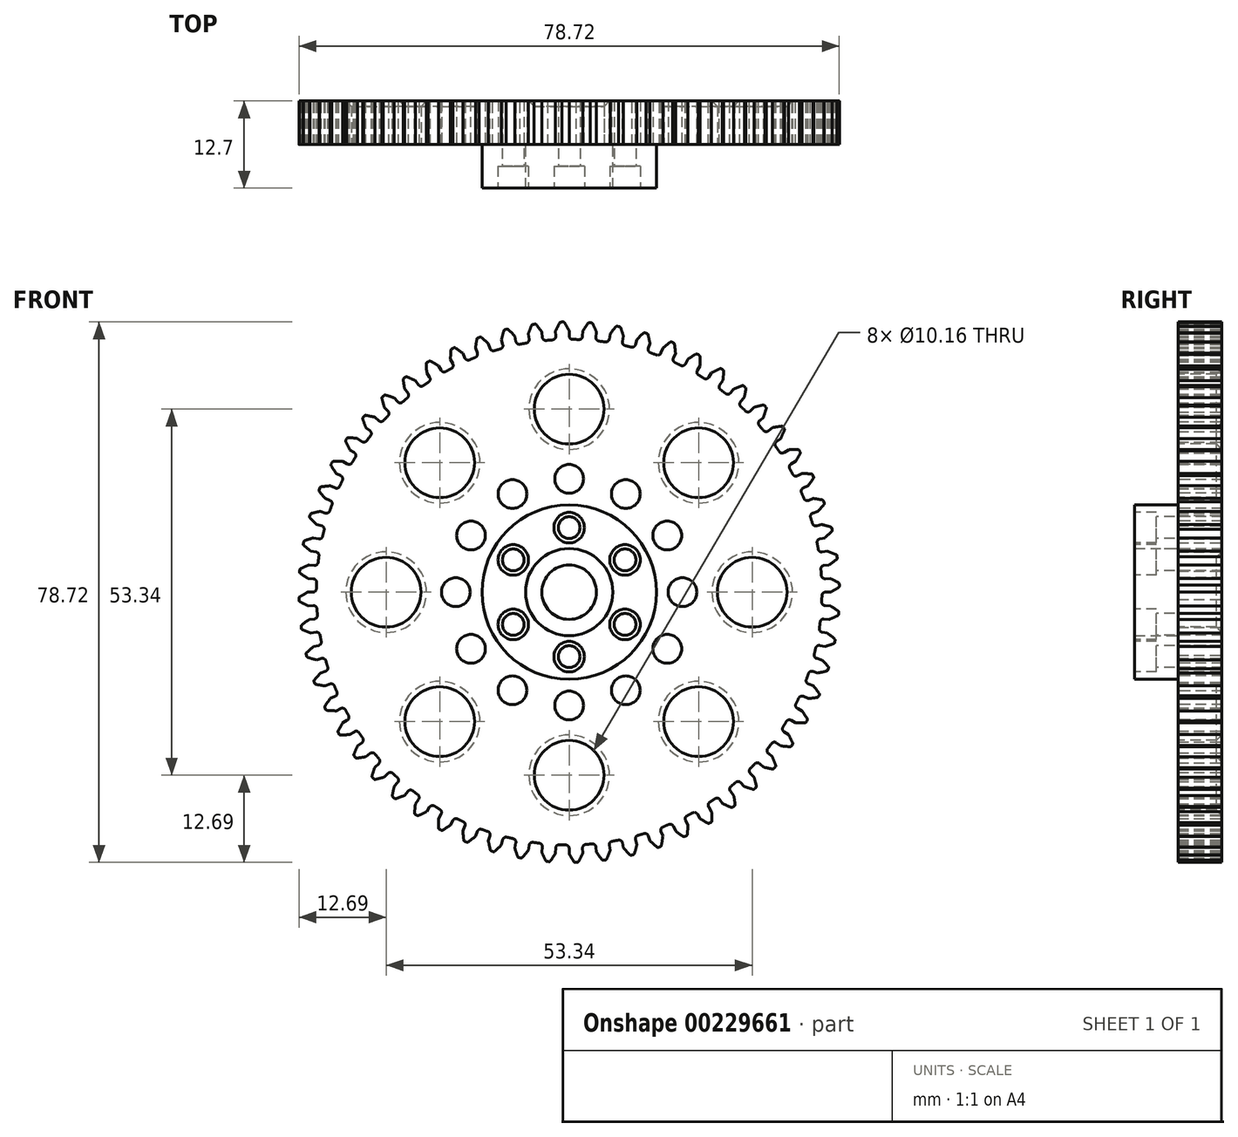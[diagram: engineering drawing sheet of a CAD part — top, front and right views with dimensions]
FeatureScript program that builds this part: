
annotation { "Feature Type Name" : "Feature", "Feature Type Description" : "" }
export const myFeature = defineFeature(function(context is Context, id is Id, definition is map)
    precondition{}
    {
        {
            var Q0;
            Q0=qCreatedBy(makeId("Front.planeOp"),FACE);
            var sketch = newSketch(context, id + "F0", { "sketchPlane" : qUnion([Q0])});
            skArc(sketch, "E0", {"start": v(-2.43, 36.75) * mm, "mid": v(-10.46, 35.31) * mm, "end": v(-17.98, 32.14) * mm});
            skLineSegment(sketch, "E1", {"start": v(0, 0) * mm, "end": v(-1.31, 50.07) * mm, "construction": true});
            skLineSegment(sketch, "E2", {"start": v(-0.86, 39.36) * mm, "end": v(-1.03, 39.36) * mm});
            skLineSegment(sketch, "E3", {"start": v(0, 38.1) * mm, "end": v(0, 37.33) * mm});
            skArc(sketch, "E4.trimOffspring", {"start": v(0, 38.1) * mm, "mid": v(-0.34, 38.69) * mm, "end": v(-0.68, 39.27) * mm});
            skLineSegment(sketch, "E5.MirrorCS", {"start": v(-1.2, 39.35) * mm, "end": v(-1.03, 39.36) * mm});
            skArc(sketch, "E6.MirrorCS", {"start": v(-2, 38.05) * mm, "mid": v(-1.69, 38.65) * mm, "end": v(-1.37, 39.25) * mm});
            skLineSegment(sketch, "E7.MirrorCS", {"start": v(-2, 38.05) * mm, "end": v(-1.95, 37.28) * mm});
            skPoint(sketch, "E8.visualSharp", {"position": v(-1.32, 39.35) * mm});
            skArc(sketch, "E8.filletArc", {"start": v(-1.2, 39.35) * mm, "mid": v(-1.3, 39.32) * mm, "end": v(-1.37, 39.25) * mm});
            skPoint(sketch, "E9.visualSharp", {"position": v(-0.74, 39.36) * mm});
            skArc(sketch, "E9.filletArc", {"start": v(-0.68, 39.27) * mm, "mid": v(-0.76, 39.34) * mm, "end": v(-0.86, 39.36) * mm});
            skPoint(sketch, "E10.visualSharp", {"position": v(0, 36.83) * mm});
            skArc(sketch, "E10.filletArc", {"start": v(0, 37.33) * mm, "mid": v(0.15, 36.98) * mm, "end": v(0.5, 36.83) * mm});
            skPoint(sketch, "E11.visualSharp", {"position": v(-1.93, 36.78) * mm});
            skArc(sketch, "E11.filletArc", {"start": v(-2.43, 36.75) * mm, "mid": v(-2.08, 36.92) * mm, "end": v(-1.95, 37.28) * mm});
            skArc(sketch, "E12.1.0", {"start": v(-6.26, 36.3) * mm, "mid": v(-5.93, 36.5) * mm, "end": v(-5.84, 36.87) * mm});
            skLineSegment(sketch, "E12.1.1", {"start": v(-5.96, 37.63) * mm, "end": v(-5.84, 36.87) * mm});
            skArc(sketch, "E12.1.2", {"start": v(-5.96, 37.63) * mm, "mid": v(-5.72, 38.26) * mm, "end": v(-5.47, 38.89) * mm});
            skArc(sketch, "E12.1.3", {"start": v(-5.31, 39.01) * mm, "mid": v(-5.4, 38.97) * mm, "end": v(-5.47, 38.89) * mm});
            skLineSegment(sketch, "E12.1.4", {"start": v(-5.31, 39.01) * mm, "end": v(-5.14, 39.04) * mm});
            skLineSegment(sketch, "E12.1.5", {"start": v(-4.97, 39.06) * mm, "end": v(-5.14, 39.04) * mm});
            skArc(sketch, "E12.1.6", {"start": v(-4.78, 38.98) * mm, "mid": v(-4.86, 39.04) * mm, "end": v(-4.97, 39.06) * mm});
            skArc(sketch, "E12.1.7", {"start": v(-3.98, 37.9) * mm, "mid": v(-4.38, 38.44) * mm, "end": v(-4.78, 38.98) * mm});
            skLineSegment(sketch, "E12.1.8", {"start": v(-3.98, 37.9) * mm, "end": v(-3.9, 37.13) * mm});
            skArc(sketch, "E12.1.9", {"start": v(-3.9, 37.13) * mm, "mid": v(-3.72, 36.8) * mm, "end": v(-3.35, 36.68) * mm});
            skArc(sketch, "E12.2.0", {"start": v(-10.02, 35.44) * mm, "mid": v(-9.71, 35.68) * mm, "end": v(-9.66, 36.06) * mm});
            skLineSegment(sketch, "E12.2.1", {"start": v(-9.86, 36.8) * mm, "end": v(-9.66, 36.06) * mm});
            skArc(sketch, "E12.2.2", {"start": v(-9.86, 36.8) * mm, "mid": v(-9.69, 37.46) * mm, "end": v(-9.5, 38.1) * mm});
            skArc(sketch, "E12.2.3", {"start": v(-9.36, 38.24) * mm, "mid": v(-9.45, 38.2) * mm, "end": v(-9.5, 38.1) * mm});
            skLineSegment(sketch, "E12.2.4", {"start": v(-9.36, 38.24) * mm, "end": v(-9.2, 38.29) * mm});
            skLineSegment(sketch, "E12.2.5", {"start": v(-9.02, 38.32) * mm, "end": v(-9.2, 38.29) * mm});
            skArc(sketch, "E12.2.6", {"start": v(-8.83, 38.27) * mm, "mid": v(-8.92, 38.32) * mm, "end": v(-9.02, 38.32) * mm});
            skArc(sketch, "E12.2.7", {"start": v(-7.92, 37.27) * mm, "mid": v(-8.37, 37.77) * mm, "end": v(-8.83, 38.27) * mm});
            skLineSegment(sketch, "E12.2.8", {"start": v(-7.92, 37.27) * mm, "end": v(-7.76, 36.52) * mm});
            skArc(sketch, "E12.2.9", {"start": v(-7.76, 36.52) * mm, "mid": v(-7.54, 36.2) * mm, "end": v(-7.17, 36.13) * mm});
            skArc(sketch, "E12.3.0", {"start": v(-13.67, 34.2) * mm, "mid": v(-13.39, 34.47) * mm, "end": v(-13.38, 34.85) * mm});
            skLineSegment(sketch, "E12.3.1", {"start": v(-13.65, 35.57) * mm, "end": v(-13.38, 34.85) * mm});
            skArc(sketch, "E12.3.2", {"start": v(-13.65, 35.57) * mm, "mid": v(-13.55, 36.24) * mm, "end": v(-13.43, 36.9) * mm});
            skArc(sketch, "E12.3.3", {"start": v(-13.3, 37.06) * mm, "mid": v(-13.4, 37) * mm, "end": v(-13.43, 36.9) * mm});
            skLineSegment(sketch, "E12.3.4", {"start": v(-13.3, 37.06) * mm, "end": v(-13.14, 37.12) * mm});
            skLineSegment(sketch, "E12.3.5", {"start": v(-12.98, 37.17) * mm, "end": v(-13.14, 37.12) * mm});
            skArc(sketch, "E12.3.6", {"start": v(-12.78, 37.13) * mm, "mid": v(-12.88, 37.18) * mm, "end": v(-12.98, 37.17) * mm});
            skArc(sketch, "E12.3.7", {"start": v(-11.77, 36.24) * mm, "mid": v(-12.27, 36.69) * mm, "end": v(-12.78, 37.13) * mm});
            skLineSegment(sketch, "E12.3.8", {"start": v(-11.77, 36.24) * mm, "end": v(-11.54, 35.5) * mm});
            skArc(sketch, "E12.3.9", {"start": v(-11.54, 35.5) * mm, "mid": v(-11.29, 35.21) * mm, "end": v(-10.9, 35.18) * mm});
            skArc(sketch, "E12.4.0", {"start": v(-17.17, 32.59) * mm, "mid": v(-16.92, 32.88) * mm, "end": v(-16.95, 33.27) * mm});
            skLineSegment(sketch, "E12.4.1", {"start": v(-17.3, 33.95) * mm, "end": v(-16.95, 33.27) * mm});
            skArc(sketch, "E12.4.2", {"start": v(-17.3, 33.95) * mm, "mid": v(-17.26, 34.62) * mm, "end": v(-17.22, 35.3) * mm});
            skArc(sketch, "E12.4.3", {"start": v(-17.1, 35.46) * mm, "mid": v(-17.18, 35.4) * mm, "end": v(-17.22, 35.3) * mm});
            skLineSegment(sketch, "E12.4.4", {"start": v(-17.1, 35.46) * mm, "end": v(-16.95, 35.54) * mm});
            skLineSegment(sketch, "E12.4.5", {"start": v(-16.8, 35.61) * mm, "end": v(-16.95, 35.54) * mm});
            skArc(sketch, "E12.4.6", {"start": v(-16.6, 35.6) * mm, "mid": v(-16.7, 35.63) * mm, "end": v(-16.8, 35.61) * mm});
            skArc(sketch, "E12.4.7", {"start": v(-15.5, 34.8) * mm, "mid": v(-16.04, 35.2) * mm, "end": v(-16.6, 35.6) * mm});
            skLineSegment(sketch, "E12.4.8", {"start": v(-15.5, 34.8) * mm, "end": v(-15.19, 34.1) * mm});
            skArc(sketch, "E12.4.9", {"start": v(-15.19, 34.1) * mm, "mid": v(-14.9, 33.84) * mm, "end": v(-14.52, 33.85) * mm});
            skArc(sketch, "E12.5.0", {"start": v(-20.48, 30.61) * mm, "mid": v(-20.26, 30.93) * mm, "end": v(-20.33, 31.31) * mm});
            skLineSegment(sketch, "E12.5.1", {"start": v(-20.75, 31.95) * mm, "end": v(-20.33, 31.31) * mm});
            skArc(sketch, "E12.5.2", {"start": v(-20.75, 31.95) * mm, "mid": v(-20.79, 32.63) * mm, "end": v(-20.81, 33.3) * mm});
            skArc(sketch, "E12.5.3", {"start": v(-20.72, 33.48) * mm, "mid": v(-20.79, 33.4) * mm, "end": v(-20.81, 33.3) * mm});
            skLineSegment(sketch, "E12.5.4", {"start": v(-20.72, 33.48) * mm, "end": v(-20.57, 33.57) * mm});
            skLineSegment(sketch, "E12.5.5", {"start": v(-20.42, 33.66) * mm, "end": v(-20.57, 33.57) * mm});
            skArc(sketch, "E12.5.6", {"start": v(-20.22, 33.66) * mm, "mid": v(-20.32, 33.69) * mm, "end": v(-20.42, 33.66) * mm});
            skArc(sketch, "E12.5.7", {"start": v(-19.05, 33) * mm, "mid": v(-19.63, 33.34) * mm, "end": v(-20.22, 33.66) * mm});
            skLineSegment(sketch, "E12.5.8", {"start": v(-19.05, 33) * mm, "end": v(-18.67, 32.33) * mm});
            skArc(sketch, "E12.5.9", {"start": v(-18.67, 32.33) * mm, "mid": v(-18.36, 32.1) * mm, "end": v(-17.98, 32.14) * mm});
            skArc(sketch, "E12.6.0", {"start": v(-23.57, 28.3) * mm, "mid": v(-23.38, 28.65) * mm, "end": v(-23.5, 29.01) * mm});
            skLineSegment(sketch, "E12.6.1", {"start": v(-23.98, 29.6) * mm, "end": v(-23.5, 29.01) * mm});
            skArc(sketch, "E12.6.2", {"start": v(-23.98, 29.6) * mm, "mid": v(-24.09, 30.28) * mm, "end": v(-24.18, 30.95) * mm});
            skArc(sketch, "E12.6.3", {"start": v(-24.1, 31.13) * mm, "mid": v(-24.17, 31.05) * mm, "end": v(-24.18, 30.95) * mm});
            skLineSegment(sketch, "E12.6.4", {"start": v(-24.1, 31.13) * mm, "end": v(-23.97, 31.24) * mm});
            skLineSegment(sketch, "E12.6.5", {"start": v(-23.83, 31.34) * mm, "end": v(-23.97, 31.24) * mm});
            skArc(sketch, "E12.6.6", {"start": v(-23.63, 31.37) * mm, "mid": v(-23.73, 31.38) * mm, "end": v(-23.83, 31.34) * mm});
            skArc(sketch, "E12.6.7", {"start": v(-22.4, 30.82) * mm, "mid": v(-23.01, 31.1) * mm, "end": v(-23.63, 31.37) * mm});
            skLineSegment(sketch, "E12.6.8", {"start": v(-22.4, 30.82) * mm, "end": v(-21.94, 30.2) * mm});
            skArc(sketch, "E12.6.9", {"start": v(-21.94, 30.2) * mm, "mid": v(-21.62, 30) * mm, "end": v(-21.24, 30.09) * mm});
            skArc(sketch, "E12.7.0", {"start": v(-26.4, 25.69) * mm, "mid": v(-26.25, 26.04) * mm, "end": v(-26.4, 26.4) * mm});
            skLineSegment(sketch, "E12.7.1", {"start": v(-26.94, 26.94) * mm, "end": v(-26.4, 26.4) * mm});
            skArc(sketch, "E12.7.2", {"start": v(-26.94, 26.94) * mm, "mid": v(-27.12, 27.6) * mm, "end": v(-27.28, 28.25) * mm});
            skArc(sketch, "E12.7.3", {"start": v(-27.23, 28.44) * mm, "mid": v(-27.28, 28.35) * mm, "end": v(-27.28, 28.25) * mm});
            skLineSegment(sketch, "E12.7.4", {"start": v(-27.23, 28.44) * mm, "end": v(-27.1, 28.56) * mm});
            skLineSegment(sketch, "E12.7.5", {"start": v(-26.98, 28.68) * mm, "end": v(-27.1, 28.56) * mm});
            skArc(sketch, "E12.7.6", {"start": v(-26.78, 28.72) * mm, "mid": v(-26.88, 28.73) * mm, "end": v(-26.98, 28.68) * mm});
            skArc(sketch, "E12.7.7", {"start": v(-25.5, 28.31) * mm, "mid": v(-26.14, 28.53) * mm, "end": v(-26.78, 28.72) * mm});
            skLineSegment(sketch, "E12.7.8", {"start": v(-25.5, 28.31) * mm, "end": v(-24.98, 27.74) * mm});
            skArc(sketch, "E12.7.9", {"start": v(-24.98, 27.74) * mm, "mid": v(-24.63, 27.58) * mm, "end": v(-24.27, 27.7) * mm});
            skArc(sketch, "E12.8.0", {"start": v(-28.93, 22.79) * mm, "mid": v(-28.83, 23.16) * mm, "end": v(-29.01, 23.5) * mm});
            skLineSegment(sketch, "E12.8.1", {"start": v(-29.6, 23.98) * mm, "end": v(-29.01, 23.5) * mm});
            skArc(sketch, "E12.8.2", {"start": v(-29.6, 23.98) * mm, "mid": v(-29.85, 24.6) * mm, "end": v(-30.09, 25.24) * mm});
            skArc(sketch, "E12.8.3", {"start": v(-30.05, 25.44) * mm, "mid": v(-30.1, 25.34) * mm, "end": v(-30.09, 25.24) * mm});
            skLineSegment(sketch, "E12.8.4", {"start": v(-30.05, 25.44) * mm, "end": v(-29.94, 25.57) * mm});
            skLineSegment(sketch, "E12.8.5", {"start": v(-29.83, 25.7) * mm, "end": v(-29.94, 25.57) * mm});
            skArc(sketch, "E12.8.6", {"start": v(-29.64, 25.77) * mm, "mid": v(-29.74, 25.76) * mm, "end": v(-29.83, 25.7) * mm});
            skArc(sketch, "E12.8.7", {"start": v(-28.31, 25.5) * mm, "mid": v(-28.97, 25.64) * mm, "end": v(-29.64, 25.77) * mm});
            skLineSegment(sketch, "E12.8.8", {"start": v(-28.31, 25.5) * mm, "end": v(-27.74, 24.98) * mm});
            skArc(sketch, "E12.8.9", {"start": v(-27.74, 24.98) * mm, "mid": v(-27.38, 24.85) * mm, "end": v(-27.03, 25.01) * mm});
            skArc(sketch, "E12.9.0", {"start": v(-31.16, 19.64) * mm, "mid": v(-31.1, 20.02) * mm, "end": v(-31.31, 20.33) * mm});
            skLineSegment(sketch, "E12.9.1", {"start": v(-31.95, 20.75) * mm, "end": v(-31.31, 20.33) * mm});
            skArc(sketch, "E12.9.2", {"start": v(-31.95, 20.75) * mm, "mid": v(-32.26, 21.35) * mm, "end": v(-32.56, 21.96) * mm});
            skArc(sketch, "E12.9.3", {"start": v(-32.55, 22.16) * mm, "mid": v(-32.58, 22.06) * mm, "end": v(-32.56, 21.96) * mm});
            skLineSegment(sketch, "E12.9.4", {"start": v(-32.55, 22.16) * mm, "end": v(-32.45, 22.3) * mm});
            skLineSegment(sketch, "E12.9.5", {"start": v(-32.35, 22.44) * mm, "end": v(-32.45, 22.3) * mm});
            skArc(sketch, "E12.9.6", {"start": v(-32.17, 22.53) * mm, "mid": v(-32.27, 22.5) * mm, "end": v(-32.35, 22.44) * mm});
            skArc(sketch, "E12.9.7", {"start": v(-30.82, 22.4) * mm, "mid": v(-31.5, 22.47) * mm, "end": v(-32.17, 22.53) * mm});
            skLineSegment(sketch, "E12.9.8", {"start": v(-30.82, 22.4) * mm, "end": v(-30.2, 21.94) * mm});
            skArc(sketch, "E12.9.9", {"start": v(-30.2, 21.94) * mm, "mid": v(-29.83, 21.85) * mm, "end": v(-29.5, 22.05) * mm});
            skArc(sketch, "E12.10.0", {"start": v(-33.04, 16.27) * mm, "mid": v(-33.01, 16.66) * mm, "end": v(-33.27, 16.95) * mm});
            skLineSegment(sketch, "E12.10.1", {"start": v(-33.95, 17.3) * mm, "end": v(-33.27, 16.95) * mm});
            skArc(sketch, "E12.10.2", {"start": v(-33.95, 17.3) * mm, "mid": v(-34.32, 17.86) * mm, "end": v(-34.68, 18.43) * mm});
            skArc(sketch, "E12.10.3", {"start": v(-34.68, 18.63) * mm, "mid": v(-34.7, 18.53) * mm, "end": v(-34.68, 18.43) * mm});
            skLineSegment(sketch, "E12.10.4", {"start": v(-34.68, 18.63) * mm, "end": v(-34.6, 18.79) * mm});
            skLineSegment(sketch, "E12.10.5", {"start": v(-34.52, 18.94) * mm, "end": v(-34.6, 18.79) * mm});
            skArc(sketch, "E12.10.6", {"start": v(-34.35, 19.04) * mm, "mid": v(-34.45, 19.01) * mm, "end": v(-34.52, 18.94) * mm});
            skArc(sketch, "E12.10.7", {"start": v(-33, 19.05) * mm, "mid": v(-33.67, 19.05) * mm, "end": v(-34.35, 19.04) * mm});
            skLineSegment(sketch, "E12.10.8", {"start": v(-33, 19.05) * mm, "end": v(-32.33, 18.67) * mm});
            skArc(sketch, "E12.10.9", {"start": v(-32.33, 18.67) * mm, "mid": v(-31.95, 18.62) * mm, "end": v(-31.64, 18.85) * mm});
            skArc(sketch, "E12.11.0", {"start": v(-34.56, 12.73) * mm, "mid": v(-34.57, 13.12) * mm, "end": v(-34.85, 13.38) * mm});
            skLineSegment(sketch, "E12.11.1", {"start": v(-35.57, 13.65) * mm, "end": v(-34.85, 13.38) * mm});
            skArc(sketch, "E12.11.2", {"start": v(-35.57, 13.65) * mm, "mid": v(-36, 14.18) * mm, "end": v(-36.41, 14.7) * mm});
            skArc(sketch, "E12.11.3", {"start": v(-36.44, 14.9) * mm, "mid": v(-36.45, 14.8) * mm, "end": v(-36.41, 14.7) * mm});
            skLineSegment(sketch, "E12.11.4", {"start": v(-36.44, 14.9) * mm, "end": v(-36.38, 15.07) * mm});
            skLineSegment(sketch, "E12.11.5", {"start": v(-36.3, 15.23) * mm, "end": v(-36.38, 15.07) * mm});
            skArc(sketch, "E12.11.6", {"start": v(-36.15, 15.35) * mm, "mid": v(-36.24, 15.3) * mm, "end": v(-36.3, 15.23) * mm});
            skArc(sketch, "E12.11.7", {"start": v(-34.8, 15.5) * mm, "mid": v(-35.48, 15.43) * mm, "end": v(-36.15, 15.35) * mm});
            skLineSegment(sketch, "E12.11.8", {"start": v(-34.8, 15.5) * mm, "end": v(-34.1, 15.19) * mm});
            skArc(sketch, "E12.11.9", {"start": v(-34.1, 15.19) * mm, "mid": v(-33.72, 15.17) * mm, "end": v(-33.44, 15.44) * mm});
            skArc(sketch, "E12.12.0", {"start": v(-35.7, 9.05) * mm, "mid": v(-35.76, 9.43) * mm, "end": v(-36.06, 9.66) * mm});
            skLineSegment(sketch, "E12.12.1", {"start": v(-36.8, 9.86) * mm, "end": v(-36.06, 9.66) * mm});
            skArc(sketch, "E12.12.2", {"start": v(-36.8, 9.86) * mm, "mid": v(-37.28, 10.34) * mm, "end": v(-37.75, 10.82) * mm});
            skArc(sketch, "E12.12.3", {"start": v(-37.8, 11.01) * mm, "mid": v(-37.8, 10.91) * mm, "end": v(-37.75, 10.82) * mm});
            skLineSegment(sketch, "E12.12.4", {"start": v(-37.8, 11.01) * mm, "end": v(-37.75, 11.18) * mm});
            skLineSegment(sketch, "E12.12.5", {"start": v(-37.7, 11.35) * mm, "end": v(-37.75, 11.18) * mm});
            skArc(sketch, "E12.12.6", {"start": v(-37.56, 11.48) * mm, "mid": v(-37.65, 11.44) * mm, "end": v(-37.7, 11.35) * mm});
            skArc(sketch, "E12.12.7", {"start": v(-36.24, 11.77) * mm, "mid": v(-36.9, 11.64) * mm, "end": v(-37.56, 11.48) * mm});
            skLineSegment(sketch, "E12.12.8", {"start": v(-36.24, 11.77) * mm, "end": v(-35.5, 11.54) * mm});
            skArc(sketch, "E12.12.9", {"start": v(-35.5, 11.54) * mm, "mid": v(-35.12, 11.57) * mm, "end": v(-34.87, 11.86) * mm});
            skArc(sketch, "E12.13.0", {"start": v(-36.45, 5.27) * mm, "mid": v(-36.55, 5.64) * mm, "end": v(-36.87, 5.84) * mm});
            skLineSegment(sketch, "E12.13.1", {"start": v(-37.63, 5.96) * mm, "end": v(-36.87, 5.84) * mm});
            skArc(sketch, "E12.13.2", {"start": v(-37.63, 5.96) * mm, "mid": v(-38.16, 6.38) * mm, "end": v(-38.68, 6.82) * mm});
            skArc(sketch, "E12.13.3", {"start": v(-38.74, 7) * mm, "mid": v(-38.73, 6.9) * mm, "end": v(-38.68, 6.82) * mm});
            skLineSegment(sketch, "E12.13.4", {"start": v(-38.74, 7) * mm, "end": v(-38.72, 7.18) * mm});
            skLineSegment(sketch, "E12.13.5", {"start": v(-38.68, 7.35) * mm, "end": v(-38.72, 7.18) * mm});
            skArc(sketch, "E12.13.6", {"start": v(-38.55, 7.5) * mm, "mid": v(-38.63, 7.44) * mm, "end": v(-38.68, 7.35) * mm});
            skArc(sketch, "E12.13.7", {"start": v(-37.27, 7.92) * mm, "mid": v(-37.91, 7.72) * mm, "end": v(-38.55, 7.5) * mm});
            skLineSegment(sketch, "E12.13.8", {"start": v(-37.27, 7.92) * mm, "end": v(-36.52, 7.76) * mm});
            skArc(sketch, "E12.13.9", {"start": v(-36.52, 7.76) * mm, "mid": v(-36.14, 7.83) * mm, "end": v(-35.92, 8.15) * mm});
            skArc(sketch, "E12.14.0", {"start": v(-36.8, 1.43) * mm, "mid": v(-36.93, 1.79) * mm, "end": v(-37.28, 1.95) * mm});
            skLineSegment(sketch, "E12.14.1", {"start": v(-38.05, 2) * mm, "end": v(-37.28, 1.95) * mm});
            skArc(sketch, "E12.14.2", {"start": v(-38.05, 2) * mm, "mid": v(-38.62, 2.36) * mm, "end": v(-39.18, 2.74) * mm});
            skArc(sketch, "E12.14.3", {"start": v(-39.26, 2.91) * mm, "mid": v(-39.24, 2.81) * mm, "end": v(-39.18, 2.74) * mm});
            skLineSegment(sketch, "E12.14.4", {"start": v(-39.26, 2.91) * mm, "end": v(-39.26, 3.09) * mm});
            skLineSegment(sketch, "E12.14.5", {"start": v(-39.24, 3.26) * mm, "end": v(-39.26, 3.09) * mm});
            skArc(sketch, "E12.14.6", {"start": v(-39.12, 3.43) * mm, "mid": v(-39.2, 3.36) * mm, "end": v(-39.24, 3.26) * mm});
            skArc(sketch, "E12.14.7", {"start": v(-37.9, 3.98) * mm, "mid": v(-38.5, 3.71) * mm, "end": v(-39.12, 3.43) * mm});
            skLineSegment(sketch, "E12.14.8", {"start": v(-37.9, 3.98) * mm, "end": v(-37.13, 3.9) * mm});
            skArc(sketch, "E12.14.9", {"start": v(-37.13, 3.9) * mm, "mid": v(-36.76, 4.01) * mm, "end": v(-36.57, 4.35) * mm});
            skArc(sketch, "E12.15.0", {"start": v(-36.75, -2.43) * mm, "mid": v(-36.92, -2.08) * mm, "end": v(-37.28, -1.95) * mm});
            skLineSegment(sketch, "E12.15.1", {"start": v(-38.05, -2) * mm, "end": v(-37.28, -1.95) * mm});
            skArc(sketch, "E12.15.2", {"start": v(-38.05, -2) * mm, "mid": v(-38.65, -1.69) * mm, "end": v(-39.25, -1.37) * mm});
            skArc(sketch, "E12.15.3", {"start": v(-39.35, -1.2) * mm, "mid": v(-39.32, -1.3) * mm, "end": v(-39.25, -1.37) * mm});
            skLineSegment(sketch, "E12.15.4", {"start": v(-39.35, -1.2) * mm, "end": v(-39.36, -1.03) * mm});
            skLineSegment(sketch, "E12.15.5", {"start": v(-39.36, -0.86) * mm, "end": v(-39.36, -1.03) * mm});
            skArc(sketch, "E12.15.6", {"start": v(-39.27, -0.68) * mm, "mid": v(-39.34, -0.76) * mm, "end": v(-39.36, -0.86) * mm});
            skArc(sketch, "E12.15.7", {"start": v(-38.1, 0) * mm, "mid": v(-38.69, -0.34) * mm, "end": v(-39.27, -0.68) * mm});
            skLineSegment(sketch, "E12.15.8", {"start": v(-38.1, 0) * mm, "end": v(-37.33, 0) * mm});
            skArc(sketch, "E12.15.9", {"start": v(-37.33, 0) * mm, "mid": v(-36.98, 0.15) * mm, "end": v(-36.83, 0.5) * mm});
            skArc(sketch, "E12.16.0", {"start": v(-36.3, -6.26) * mm, "mid": v(-36.5, -5.93) * mm, "end": v(-36.87, -5.84) * mm});
            skLineSegment(sketch, "E12.16.1", {"start": v(-37.63, -5.96) * mm, "end": v(-36.87, -5.84) * mm});
            skArc(sketch, "E12.16.2", {"start": v(-37.63, -5.96) * mm, "mid": v(-38.26, -5.72) * mm, "end": v(-38.89, -5.47) * mm});
            skArc(sketch, "E12.16.3", {"start": v(-39.01, -5.31) * mm, "mid": v(-38.97, -5.4) * mm, "end": v(-38.89, -5.47) * mm});
            skLineSegment(sketch, "E12.16.4", {"start": v(-39.01, -5.31) * mm, "end": v(-39.04, -5.14) * mm});
            skLineSegment(sketch, "E12.16.5", {"start": v(-39.06, -4.97) * mm, "end": v(-39.04, -5.14) * mm});
            skArc(sketch, "E12.16.6", {"start": v(-38.98, -4.78) * mm, "mid": v(-39.04, -4.86) * mm, "end": v(-39.06, -4.97) * mm});
            skArc(sketch, "E12.16.7", {"start": v(-37.9, -3.98) * mm, "mid": v(-38.44, -4.38) * mm, "end": v(-38.98, -4.78) * mm});
            skLineSegment(sketch, "E12.16.8", {"start": v(-37.9, -3.98) * mm, "end": v(-37.13, -3.9) * mm});
            skArc(sketch, "E12.16.9", {"start": v(-37.13, -3.9) * mm, "mid": v(-36.8, -3.72) * mm, "end": v(-36.68, -3.35) * mm});
            skArc(sketch, "E12.17.0", {"start": v(-35.44, -10.02) * mm, "mid": v(-35.68, -9.71) * mm, "end": v(-36.06, -9.66) * mm});
            skLineSegment(sketch, "E12.17.1", {"start": v(-36.8, -9.86) * mm, "end": v(-36.06, -9.66) * mm});
            skArc(sketch, "E12.17.2", {"start": v(-36.8, -9.86) * mm, "mid": v(-37.46, -9.69) * mm, "end": v(-38.1, -9.5) * mm});
            skArc(sketch, "E12.17.3", {"start": v(-38.24, -9.36) * mm, "mid": v(-38.2, -9.45) * mm, "end": v(-38.1, -9.5) * mm});
            skLineSegment(sketch, "E12.17.4", {"start": v(-38.24, -9.36) * mm, "end": v(-38.29, -9.2) * mm});
            skLineSegment(sketch, "E12.17.5", {"start": v(-38.32, -9.02) * mm, "end": v(-38.29, -9.2) * mm});
            skArc(sketch, "E12.17.6", {"start": v(-38.27, -8.83) * mm, "mid": v(-38.32, -8.92) * mm, "end": v(-38.32, -9.02) * mm});
            skArc(sketch, "E12.17.7", {"start": v(-37.27, -7.92) * mm, "mid": v(-37.77, -8.37) * mm, "end": v(-38.27, -8.83) * mm});
            skLineSegment(sketch, "E12.17.8", {"start": v(-37.27, -7.92) * mm, "end": v(-36.52, -7.76) * mm});
            skArc(sketch, "E12.17.9", {"start": v(-36.52, -7.76) * mm, "mid": v(-36.2, -7.54) * mm, "end": v(-36.13, -7.17) * mm});
            skArc(sketch, "E12.18.0", {"start": v(-34.2, -13.67) * mm, "mid": v(-34.47, -13.39) * mm, "end": v(-34.85, -13.38) * mm});
            skLineSegment(sketch, "E12.18.1", {"start": v(-35.57, -13.65) * mm, "end": v(-34.85, -13.38) * mm});
            skArc(sketch, "E12.18.2", {"start": v(-35.57, -13.65) * mm, "mid": v(-36.24, -13.55) * mm, "end": v(-36.9, -13.43) * mm});
            skArc(sketch, "E12.18.3", {"start": v(-37.06, -13.3) * mm, "mid": v(-37, -13.4) * mm, "end": v(-36.9, -13.43) * mm});
            skLineSegment(sketch, "E12.18.4", {"start": v(-37.06, -13.3) * mm, "end": v(-37.12, -13.14) * mm});
            skLineSegment(sketch, "E12.18.5", {"start": v(-37.17, -12.98) * mm, "end": v(-37.12, -13.14) * mm});
            skArc(sketch, "E12.18.6", {"start": v(-37.13, -12.78) * mm, "mid": v(-37.18, -12.88) * mm, "end": v(-37.17, -12.98) * mm});
            skArc(sketch, "E12.18.7", {"start": v(-36.24, -11.77) * mm, "mid": v(-36.69, -12.27) * mm, "end": v(-37.13, -12.78) * mm});
            skLineSegment(sketch, "E12.18.8", {"start": v(-36.24, -11.77) * mm, "end": v(-35.5, -11.54) * mm});
            skArc(sketch, "E12.18.9", {"start": v(-35.5, -11.54) * mm, "mid": v(-35.21, -11.29) * mm, "end": v(-35.18, -10.9) * mm});
            skArc(sketch, "E12.19.0", {"start": v(-32.59, -17.17) * mm, "mid": v(-32.88, -16.92) * mm, "end": v(-33.27, -16.95) * mm});
            skLineSegment(sketch, "E12.19.1", {"start": v(-33.95, -17.3) * mm, "end": v(-33.27, -16.95) * mm});
            skArc(sketch, "E12.19.2", {"start": v(-33.95, -17.3) * mm, "mid": v(-34.62, -17.26) * mm, "end": v(-35.3, -17.22) * mm});
            skArc(sketch, "E12.19.3", {"start": v(-35.46, -17.1) * mm, "mid": v(-35.4, -17.18) * mm, "end": v(-35.3, -17.22) * mm});
            skLineSegment(sketch, "E12.19.4", {"start": v(-35.46, -17.1) * mm, "end": v(-35.54, -16.95) * mm});
            skLineSegment(sketch, "E12.19.5", {"start": v(-35.61, -16.8) * mm, "end": v(-35.54, -16.95) * mm});
            skArc(sketch, "E12.19.6", {"start": v(-35.6, -16.6) * mm, "mid": v(-35.63, -16.7) * mm, "end": v(-35.61, -16.8) * mm});
            skArc(sketch, "E12.19.7", {"start": v(-34.8, -15.5) * mm, "mid": v(-35.2, -16.04) * mm, "end": v(-35.6, -16.6) * mm});
            skLineSegment(sketch, "E12.19.8", {"start": v(-34.8, -15.5) * mm, "end": v(-34.1, -15.19) * mm});
            skArc(sketch, "E12.19.9", {"start": v(-34.1, -15.19) * mm, "mid": v(-33.84, -14.9) * mm, "end": v(-33.85, -14.52) * mm});
            skArc(sketch, "E12.20.0", {"start": v(-30.61, -20.48) * mm, "mid": v(-30.93, -20.26) * mm, "end": v(-31.31, -20.33) * mm});
            skLineSegment(sketch, "E12.20.1", {"start": v(-31.95, -20.75) * mm, "end": v(-31.31, -20.33) * mm});
            skArc(sketch, "E12.20.2", {"start": v(-31.95, -20.75) * mm, "mid": v(-32.63, -20.79) * mm, "end": v(-33.3, -20.81) * mm});
            skArc(sketch, "E12.20.3", {"start": v(-33.48, -20.72) * mm, "mid": v(-33.4, -20.79) * mm, "end": v(-33.3, -20.81) * mm});
            skLineSegment(sketch, "E12.20.4", {"start": v(-33.48, -20.72) * mm, "end": v(-33.57, -20.57) * mm});
            skLineSegment(sketch, "E12.20.5", {"start": v(-33.66, -20.42) * mm, "end": v(-33.57, -20.57) * mm});
            skArc(sketch, "E12.20.6", {"start": v(-33.66, -20.22) * mm, "mid": v(-33.69, -20.32) * mm, "end": v(-33.66, -20.42) * mm});
            skArc(sketch, "E12.20.7", {"start": v(-33, -19.05) * mm, "mid": v(-33.34, -19.63) * mm, "end": v(-33.66, -20.22) * mm});
            skLineSegment(sketch, "E12.20.8", {"start": v(-33, -19.05) * mm, "end": v(-32.33, -18.67) * mm});
            skArc(sketch, "E12.20.9", {"start": v(-32.33, -18.67) * mm, "mid": v(-32.1, -18.36) * mm, "end": v(-32.14, -17.98) * mm});
            skArc(sketch, "E12.21.0", {"start": v(-28.3, -23.57) * mm, "mid": v(-28.65, -23.38) * mm, "end": v(-29.01, -23.5) * mm});
            skLineSegment(sketch, "E12.21.1", {"start": v(-29.6, -23.98) * mm, "end": v(-29.01, -23.5) * mm});
            skArc(sketch, "E12.21.2", {"start": v(-29.6, -23.98) * mm, "mid": v(-30.28, -24.09) * mm, "end": v(-30.95, -24.18) * mm});
            skArc(sketch, "E12.21.3", {"start": v(-31.13, -24.1) * mm, "mid": v(-31.05, -24.17) * mm, "end": v(-30.95, -24.18) * mm});
            skLineSegment(sketch, "E12.21.4", {"start": v(-31.13, -24.1) * mm, "end": v(-31.24, -23.97) * mm});
            skLineSegment(sketch, "E12.21.5", {"start": v(-31.34, -23.83) * mm, "end": v(-31.24, -23.97) * mm});
            skArc(sketch, "E12.21.6", {"start": v(-31.37, -23.63) * mm, "mid": v(-31.38, -23.73) * mm, "end": v(-31.34, -23.83) * mm});
            skArc(sketch, "E12.21.7", {"start": v(-30.82, -22.4) * mm, "mid": v(-31.1, -23.01) * mm, "end": v(-31.37, -23.63) * mm});
            skLineSegment(sketch, "E12.21.8", {"start": v(-30.82, -22.4) * mm, "end": v(-30.2, -21.94) * mm});
            skArc(sketch, "E12.21.9", {"start": v(-30.2, -21.94) * mm, "mid": v(-30, -21.62) * mm, "end": v(-30.09, -21.24) * mm});
            skArc(sketch, "E12.22.0", {"start": v(-25.69, -26.4) * mm, "mid": v(-26.04, -26.25) * mm, "end": v(-26.4, -26.4) * mm});
            skLineSegment(sketch, "E12.22.1", {"start": v(-26.94, -26.94) * mm, "end": v(-26.4, -26.4) * mm});
            skArc(sketch, "E12.22.2", {"start": v(-26.94, -26.94) * mm, "mid": v(-27.6, -27.12) * mm, "end": v(-28.25, -27.28) * mm});
            skArc(sketch, "E12.22.3", {"start": v(-28.44, -27.23) * mm, "mid": v(-28.35, -27.28) * mm, "end": v(-28.25, -27.28) * mm});
            skLineSegment(sketch, "E12.22.4", {"start": v(-28.44, -27.23) * mm, "end": v(-28.56, -27.1) * mm});
            skLineSegment(sketch, "E12.22.5", {"start": v(-28.68, -26.98) * mm, "end": v(-28.56, -27.1) * mm});
            skArc(sketch, "E12.22.6", {"start": v(-28.72, -26.78) * mm, "mid": v(-28.73, -26.88) * mm, "end": v(-28.68, -26.98) * mm});
            skArc(sketch, "E12.22.7", {"start": v(-28.31, -25.5) * mm, "mid": v(-28.53, -26.14) * mm, "end": v(-28.72, -26.78) * mm});
            skLineSegment(sketch, "E12.22.8", {"start": v(-28.31, -25.5) * mm, "end": v(-27.74, -24.98) * mm});
            skArc(sketch, "E12.22.9", {"start": v(-27.74, -24.98) * mm, "mid": v(-27.58, -24.63) * mm, "end": v(-27.7, -24.27) * mm});
            skArc(sketch, "E12.23.0", {"start": v(-22.79, -28.93) * mm, "mid": v(-23.16, -28.83) * mm, "end": v(-23.5, -29.01) * mm});
            skLineSegment(sketch, "E12.23.1", {"start": v(-23.98, -29.6) * mm, "end": v(-23.5, -29.01) * mm});
            skArc(sketch, "E12.23.2", {"start": v(-23.98, -29.6) * mm, "mid": v(-24.6, -29.85) * mm, "end": v(-25.24, -30.09) * mm});
            skArc(sketch, "E12.23.3", {"start": v(-25.44, -30.05) * mm, "mid": v(-25.34, -30.1) * mm, "end": v(-25.24, -30.09) * mm});
            skLineSegment(sketch, "E12.23.4", {"start": v(-25.44, -30.05) * mm, "end": v(-25.57, -29.94) * mm});
            skLineSegment(sketch, "E12.23.5", {"start": v(-25.7, -29.83) * mm, "end": v(-25.57, -29.94) * mm});
            skArc(sketch, "E12.23.6", {"start": v(-25.77, -29.64) * mm, "mid": v(-25.76, -29.74) * mm, "end": v(-25.7, -29.83) * mm});
            skArc(sketch, "E12.23.7", {"start": v(-25.5, -28.31) * mm, "mid": v(-25.64, -28.97) * mm, "end": v(-25.77, -29.64) * mm});
            skLineSegment(sketch, "E12.23.8", {"start": v(-25.5, -28.31) * mm, "end": v(-24.98, -27.74) * mm});
            skArc(sketch, "E12.23.9", {"start": v(-24.98, -27.74) * mm, "mid": v(-24.85, -27.38) * mm, "end": v(-25.01, -27.03) * mm});
            skArc(sketch, "E12.24.0", {"start": v(-19.64, -31.16) * mm, "mid": v(-20.02, -31.1) * mm, "end": v(-20.33, -31.31) * mm});
            skLineSegment(sketch, "E12.24.1", {"start": v(-20.75, -31.95) * mm, "end": v(-20.33, -31.31) * mm});
            skArc(sketch, "E12.24.2", {"start": v(-20.75, -31.95) * mm, "mid": v(-21.35, -32.26) * mm, "end": v(-21.96, -32.56) * mm});
            skArc(sketch, "E12.24.3", {"start": v(-22.16, -32.55) * mm, "mid": v(-22.06, -32.58) * mm, "end": v(-21.96, -32.56) * mm});
            skLineSegment(sketch, "E12.24.4", {"start": v(-22.16, -32.55) * mm, "end": v(-22.3, -32.45) * mm});
            skLineSegment(sketch, "E12.24.5", {"start": v(-22.44, -32.35) * mm, "end": v(-22.3, -32.45) * mm});
            skArc(sketch, "E12.24.6", {"start": v(-22.53, -32.17) * mm, "mid": v(-22.5, -32.27) * mm, "end": v(-22.44, -32.35) * mm});
            skArc(sketch, "E12.24.7", {"start": v(-22.4, -30.82) * mm, "mid": v(-22.47, -31.5) * mm, "end": v(-22.53, -32.17) * mm});
            skLineSegment(sketch, "E12.24.8", {"start": v(-22.4, -30.82) * mm, "end": v(-21.94, -30.2) * mm});
            skArc(sketch, "E12.24.9", {"start": v(-21.94, -30.2) * mm, "mid": v(-21.85, -29.83) * mm, "end": v(-22.05, -29.5) * mm});
            skArc(sketch, "E12.25.0", {"start": v(-16.27, -33.04) * mm, "mid": v(-16.66, -33.01) * mm, "end": v(-16.95, -33.27) * mm});
            skLineSegment(sketch, "E12.25.1", {"start": v(-17.3, -33.95) * mm, "end": v(-16.95, -33.27) * mm});
            skArc(sketch, "E12.25.2", {"start": v(-17.3, -33.95) * mm, "mid": v(-17.86, -34.32) * mm, "end": v(-18.43, -34.68) * mm});
            skArc(sketch, "E12.25.3", {"start": v(-18.63, -34.68) * mm, "mid": v(-18.53, -34.7) * mm, "end": v(-18.43, -34.68) * mm});
            skLineSegment(sketch, "E12.25.4", {"start": v(-18.63, -34.68) * mm, "end": v(-18.79, -34.6) * mm});
            skLineSegment(sketch, "E12.25.5", {"start": v(-18.94, -34.52) * mm, "end": v(-18.79, -34.6) * mm});
            skArc(sketch, "E12.25.6", {"start": v(-19.04, -34.35) * mm, "mid": v(-19.01, -34.45) * mm, "end": v(-18.94, -34.52) * mm});
            skArc(sketch, "E12.25.7", {"start": v(-19.05, -33) * mm, "mid": v(-19.05, -33.67) * mm, "end": v(-19.04, -34.35) * mm});
            skLineSegment(sketch, "E12.25.8", {"start": v(-19.05, -33) * mm, "end": v(-18.67, -32.33) * mm});
            skArc(sketch, "E12.25.9", {"start": v(-18.67, -32.33) * mm, "mid": v(-18.62, -31.95) * mm, "end": v(-18.85, -31.64) * mm});
            skArc(sketch, "E12.26.0", {"start": v(-12.73, -34.56) * mm, "mid": v(-13.12, -34.57) * mm, "end": v(-13.38, -34.85) * mm});
            skLineSegment(sketch, "E12.26.1", {"start": v(-13.65, -35.57) * mm, "end": v(-13.38, -34.85) * mm});
            skArc(sketch, "E12.26.2", {"start": v(-13.65, -35.57) * mm, "mid": v(-14.18, -36) * mm, "end": v(-14.7, -36.41) * mm});
            skArc(sketch, "E12.26.3", {"start": v(-14.9, -36.44) * mm, "mid": v(-14.8, -36.45) * mm, "end": v(-14.7, -36.41) * mm});
            skLineSegment(sketch, "E12.26.4", {"start": v(-14.9, -36.44) * mm, "end": v(-15.07, -36.38) * mm});
            skLineSegment(sketch, "E12.26.5", {"start": v(-15.23, -36.3) * mm, "end": v(-15.07, -36.38) * mm});
            skArc(sketch, "E12.26.6", {"start": v(-15.35, -36.15) * mm, "mid": v(-15.3, -36.24) * mm, "end": v(-15.23, -36.3) * mm});
            skArc(sketch, "E12.26.7", {"start": v(-15.5, -34.8) * mm, "mid": v(-15.43, -35.48) * mm, "end": v(-15.35, -36.15) * mm});
            skLineSegment(sketch, "E12.26.8", {"start": v(-15.5, -34.8) * mm, "end": v(-15.19, -34.1) * mm});
            skArc(sketch, "E12.26.9", {"start": v(-15.19, -34.1) * mm, "mid": v(-15.17, -33.72) * mm, "end": v(-15.44, -33.44) * mm});
            skArc(sketch, "E12.27.0", {"start": v(-9.05, -35.7) * mm, "mid": v(-9.43, -35.76) * mm, "end": v(-9.66, -36.06) * mm});
            skLineSegment(sketch, "E12.27.1", {"start": v(-9.86, -36.8) * mm, "end": v(-9.66, -36.06) * mm});
            skArc(sketch, "E12.27.2", {"start": v(-9.86, -36.8) * mm, "mid": v(-10.34, -37.28) * mm, "end": v(-10.82, -37.75) * mm});
            skArc(sketch, "E12.27.3", {"start": v(-11.01, -37.8) * mm, "mid": v(-10.91, -37.8) * mm, "end": v(-10.82, -37.75) * mm});
            skLineSegment(sketch, "E12.27.4", {"start": v(-11.01, -37.8) * mm, "end": v(-11.18, -37.75) * mm});
            skLineSegment(sketch, "E12.27.5", {"start": v(-11.35, -37.7) * mm, "end": v(-11.18, -37.75) * mm});
            skArc(sketch, "E12.27.6", {"start": v(-11.48, -37.56) * mm, "mid": v(-11.44, -37.65) * mm, "end": v(-11.35, -37.7) * mm});
            skArc(sketch, "E12.27.7", {"start": v(-11.77, -36.24) * mm, "mid": v(-11.64, -36.9) * mm, "end": v(-11.48, -37.56) * mm});
            skLineSegment(sketch, "E12.27.8", {"start": v(-11.77, -36.24) * mm, "end": v(-11.54, -35.5) * mm});
            skArc(sketch, "E12.27.9", {"start": v(-11.54, -35.5) * mm, "mid": v(-11.57, -35.12) * mm, "end": v(-11.86, -34.87) * mm});
            skArc(sketch, "E12.28.0", {"start": v(-5.27, -36.45) * mm, "mid": v(-5.64, -36.55) * mm, "end": v(-5.84, -36.87) * mm});
            skLineSegment(sketch, "E12.28.1", {"start": v(-5.96, -37.63) * mm, "end": v(-5.84, -36.87) * mm});
            skArc(sketch, "E12.28.2", {"start": v(-5.96, -37.63) * mm, "mid": v(-6.38, -38.16) * mm, "end": v(-6.82, -38.68) * mm});
            skArc(sketch, "E12.28.3", {"start": v(-7, -38.74) * mm, "mid": v(-6.9, -38.73) * mm, "end": v(-6.82, -38.68) * mm});
            skLineSegment(sketch, "E12.28.4", {"start": v(-7, -38.74) * mm, "end": v(-7.18, -38.72) * mm});
            skLineSegment(sketch, "E12.28.5", {"start": v(-7.35, -38.68) * mm, "end": v(-7.18, -38.72) * mm});
            skArc(sketch, "E12.28.6", {"start": v(-7.5, -38.55) * mm, "mid": v(-7.44, -38.63) * mm, "end": v(-7.35, -38.68) * mm});
            skArc(sketch, "E12.28.7", {"start": v(-7.92, -37.27) * mm, "mid": v(-7.72, -37.91) * mm, "end": v(-7.5, -38.55) * mm});
            skLineSegment(sketch, "E12.28.8", {"start": v(-7.92, -37.27) * mm, "end": v(-7.76, -36.52) * mm});
            skArc(sketch, "E12.28.9", {"start": v(-7.76, -36.52) * mm, "mid": v(-7.83, -36.14) * mm, "end": v(-8.15, -35.92) * mm});
            skArc(sketch, "E12.29.0", {"start": v(-1.43, -36.8) * mm, "mid": v(-1.79, -36.93) * mm, "end": v(-1.95, -37.28) * mm});
            skLineSegment(sketch, "E12.29.1", {"start": v(-2, -38.05) * mm, "end": v(-1.95, -37.28) * mm});
            skArc(sketch, "E12.29.2", {"start": v(-2, -38.05) * mm, "mid": v(-2.36, -38.62) * mm, "end": v(-2.74, -39.18) * mm});
            skArc(sketch, "E12.29.3", {"start": v(-2.91, -39.26) * mm, "mid": v(-2.81, -39.24) * mm, "end": v(-2.74, -39.18) * mm});
            skLineSegment(sketch, "E12.29.4", {"start": v(-2.91, -39.26) * mm, "end": v(-3.09, -39.26) * mm});
            skLineSegment(sketch, "E12.29.5", {"start": v(-3.26, -39.24) * mm, "end": v(-3.09, -39.26) * mm});
            skArc(sketch, "E12.29.6", {"start": v(-3.43, -39.12) * mm, "mid": v(-3.36, -39.2) * mm, "end": v(-3.26, -39.24) * mm});
            skArc(sketch, "E12.29.7", {"start": v(-3.98, -37.9) * mm, "mid": v(-3.71, -38.5) * mm, "end": v(-3.43, -39.12) * mm});
            skLineSegment(sketch, "E12.29.8", {"start": v(-3.98, -37.9) * mm, "end": v(-3.9, -37.13) * mm});
            skArc(sketch, "E12.29.9", {"start": v(-3.9, -37.13) * mm, "mid": v(-4.01, -36.76) * mm, "end": v(-4.35, -36.57) * mm});
            skArc(sketch, "E12.30.0", {"start": v(2.43, -36.75) * mm, "mid": v(2.08, -36.92) * mm, "end": v(1.95, -37.28) * mm});
            skLineSegment(sketch, "E12.30.1", {"start": v(2, -38.05) * mm, "end": v(1.95, -37.28) * mm});
            skArc(sketch, "E12.30.2", {"start": v(2, -38.05) * mm, "mid": v(1.69, -38.65) * mm, "end": v(1.37, -39.25) * mm});
            skArc(sketch, "E12.30.3", {"start": v(1.2, -39.35) * mm, "mid": v(1.3, -39.32) * mm, "end": v(1.37, -39.25) * mm});
            skLineSegment(sketch, "E12.30.4", {"start": v(1.2, -39.35) * mm, "end": v(1.03, -39.36) * mm});
            skLineSegment(sketch, "E12.30.5", {"start": v(0.86, -39.36) * mm, "end": v(1.03, -39.36) * mm});
            skArc(sketch, "E12.30.6", {"start": v(0.68, -39.27) * mm, "mid": v(0.76, -39.34) * mm, "end": v(0.86, -39.36) * mm});
            skArc(sketch, "E12.30.7", {"start": v(0, -38.1) * mm, "mid": v(0.34, -38.69) * mm, "end": v(0.68, -39.27) * mm});
            skLineSegment(sketch, "E12.30.8", {"start": v(0, -38.1) * mm, "end": v(0, -37.33) * mm});
            skArc(sketch, "E12.30.9", {"start": v(0, -37.33) * mm, "mid": v(-0.15, -36.98) * mm, "end": v(-0.5, -36.83) * mm});
            skArc(sketch, "E12.31.0", {"start": v(6.26, -36.3) * mm, "mid": v(5.93, -36.5) * mm, "end": v(5.84, -36.87) * mm});
            skLineSegment(sketch, "E12.31.1", {"start": v(5.96, -37.63) * mm, "end": v(5.84, -36.87) * mm});
            skArc(sketch, "E12.31.2", {"start": v(5.96, -37.63) * mm, "mid": v(5.72, -38.26) * mm, "end": v(5.47, -38.89) * mm});
            skArc(sketch, "E12.31.3", {"start": v(5.31, -39.01) * mm, "mid": v(5.4, -38.97) * mm, "end": v(5.47, -38.89) * mm});
            skLineSegment(sketch, "E12.31.4", {"start": v(5.31, -39.01) * mm, "end": v(5.14, -39.04) * mm});
            skLineSegment(sketch, "E12.31.5", {"start": v(4.97, -39.06) * mm, "end": v(5.14, -39.04) * mm});
            skArc(sketch, "E12.31.6", {"start": v(4.78, -38.98) * mm, "mid": v(4.86, -39.04) * mm, "end": v(4.97, -39.06) * mm});
            skArc(sketch, "E12.31.7", {"start": v(3.98, -37.9) * mm, "mid": v(4.38, -38.44) * mm, "end": v(4.78, -38.98) * mm});
            skLineSegment(sketch, "E12.31.8", {"start": v(3.98, -37.9) * mm, "end": v(3.9, -37.13) * mm});
            skArc(sketch, "E12.31.9", {"start": v(3.9, -37.13) * mm, "mid": v(3.72, -36.8) * mm, "end": v(3.35, -36.68) * mm});
            skArc(sketch, "E12.32.0", {"start": v(10.02, -35.44) * mm, "mid": v(9.71, -35.68) * mm, "end": v(9.66, -36.06) * mm});
            skLineSegment(sketch, "E12.32.1", {"start": v(9.86, -36.8) * mm, "end": v(9.66, -36.06) * mm});
            skArc(sketch, "E12.32.2", {"start": v(9.86, -36.8) * mm, "mid": v(9.69, -37.46) * mm, "end": v(9.5, -38.1) * mm});
            skArc(sketch, "E12.32.3", {"start": v(9.36, -38.24) * mm, "mid": v(9.45, -38.2) * mm, "end": v(9.5, -38.1) * mm});
            skLineSegment(sketch, "E12.32.4", {"start": v(9.36, -38.24) * mm, "end": v(9.2, -38.29) * mm});
            skLineSegment(sketch, "E12.32.5", {"start": v(9.02, -38.32) * mm, "end": v(9.2, -38.29) * mm});
            skArc(sketch, "E12.32.6", {"start": v(8.83, -38.27) * mm, "mid": v(8.92, -38.32) * mm, "end": v(9.02, -38.32) * mm});
            skArc(sketch, "E12.32.7", {"start": v(7.92, -37.27) * mm, "mid": v(8.37, -37.77) * mm, "end": v(8.83, -38.27) * mm});
            skLineSegment(sketch, "E12.32.8", {"start": v(7.92, -37.27) * mm, "end": v(7.76, -36.52) * mm});
            skArc(sketch, "E12.32.9", {"start": v(7.76, -36.52) * mm, "mid": v(7.54, -36.2) * mm, "end": v(7.17, -36.13) * mm});
            skArc(sketch, "E12.33.0", {"start": v(13.67, -34.2) * mm, "mid": v(13.39, -34.47) * mm, "end": v(13.38, -34.85) * mm});
            skLineSegment(sketch, "E12.33.1", {"start": v(13.65, -35.57) * mm, "end": v(13.38, -34.85) * mm});
            skArc(sketch, "E12.33.2", {"start": v(13.65, -35.57) * mm, "mid": v(13.55, -36.24) * mm, "end": v(13.43, -36.9) * mm});
            skArc(sketch, "E12.33.3", {"start": v(13.3, -37.06) * mm, "mid": v(13.4, -37) * mm, "end": v(13.43, -36.9) * mm});
            skLineSegment(sketch, "E12.33.4", {"start": v(13.3, -37.06) * mm, "end": v(13.14, -37.12) * mm});
            skLineSegment(sketch, "E12.33.5", {"start": v(12.98, -37.17) * mm, "end": v(13.14, -37.12) * mm});
            skArc(sketch, "E12.33.6", {"start": v(12.78, -37.13) * mm, "mid": v(12.88, -37.18) * mm, "end": v(12.98, -37.17) * mm});
            skArc(sketch, "E12.33.7", {"start": v(11.77, -36.24) * mm, "mid": v(12.27, -36.69) * mm, "end": v(12.78, -37.13) * mm});
            skLineSegment(sketch, "E12.33.8", {"start": v(11.77, -36.24) * mm, "end": v(11.54, -35.5) * mm});
            skArc(sketch, "E12.33.9", {"start": v(11.54, -35.5) * mm, "mid": v(11.29, -35.21) * mm, "end": v(10.9, -35.18) * mm});
            skArc(sketch, "E12.34.0", {"start": v(17.17, -32.59) * mm, "mid": v(16.92, -32.88) * mm, "end": v(16.95, -33.27) * mm});
            skLineSegment(sketch, "E12.34.1", {"start": v(17.3, -33.95) * mm, "end": v(16.95, -33.27) * mm});
            skArc(sketch, "E12.34.2", {"start": v(17.3, -33.95) * mm, "mid": v(17.26, -34.62) * mm, "end": v(17.22, -35.3) * mm});
            skArc(sketch, "E12.34.3", {"start": v(17.1, -35.46) * mm, "mid": v(17.18, -35.4) * mm, "end": v(17.22, -35.3) * mm});
            skLineSegment(sketch, "E12.34.4", {"start": v(17.1, -35.46) * mm, "end": v(16.95, -35.54) * mm});
            skLineSegment(sketch, "E12.34.5", {"start": v(16.8, -35.61) * mm, "end": v(16.95, -35.54) * mm});
            skArc(sketch, "E12.34.6", {"start": v(16.6, -35.6) * mm, "mid": v(16.7, -35.63) * mm, "end": v(16.8, -35.61) * mm});
            skArc(sketch, "E12.34.7", {"start": v(15.5, -34.8) * mm, "mid": v(16.04, -35.2) * mm, "end": v(16.6, -35.6) * mm});
            skLineSegment(sketch, "E12.34.8", {"start": v(15.5, -34.8) * mm, "end": v(15.19, -34.1) * mm});
            skArc(sketch, "E12.34.9", {"start": v(15.19, -34.1) * mm, "mid": v(14.9, -33.84) * mm, "end": v(14.52, -33.85) * mm});
            skArc(sketch, "E12.35.0", {"start": v(20.48, -30.61) * mm, "mid": v(20.26, -30.93) * mm, "end": v(20.33, -31.31) * mm});
            skLineSegment(sketch, "E12.35.1", {"start": v(20.75, -31.95) * mm, "end": v(20.33, -31.31) * mm});
            skArc(sketch, "E12.35.2", {"start": v(20.75, -31.95) * mm, "mid": v(20.79, -32.63) * mm, "end": v(20.81, -33.3) * mm});
            skArc(sketch, "E12.35.3", {"start": v(20.72, -33.48) * mm, "mid": v(20.79, -33.4) * mm, "end": v(20.81, -33.3) * mm});
            skLineSegment(sketch, "E12.35.4", {"start": v(20.72, -33.48) * mm, "end": v(20.57, -33.57) * mm});
            skLineSegment(sketch, "E12.35.5", {"start": v(20.42, -33.66) * mm, "end": v(20.57, -33.57) * mm});
            skArc(sketch, "E12.35.6", {"start": v(20.22, -33.66) * mm, "mid": v(20.32, -33.69) * mm, "end": v(20.42, -33.66) * mm});
            skArc(sketch, "E12.35.7", {"start": v(19.05, -33) * mm, "mid": v(19.63, -33.34) * mm, "end": v(20.22, -33.66) * mm});
            skLineSegment(sketch, "E12.35.8", {"start": v(19.05, -33) * mm, "end": v(18.67, -32.33) * mm});
            skArc(sketch, "E12.35.9", {"start": v(18.67, -32.33) * mm, "mid": v(18.36, -32.1) * mm, "end": v(17.98, -32.14) * mm});
            skArc(sketch, "E12.36.0", {"start": v(23.57, -28.3) * mm, "mid": v(23.38, -28.65) * mm, "end": v(23.5, -29.01) * mm});
            skLineSegment(sketch, "E12.36.1", {"start": v(23.98, -29.6) * mm, "end": v(23.5, -29.01) * mm});
            skArc(sketch, "E12.36.2", {"start": v(23.98, -29.6) * mm, "mid": v(24.09, -30.28) * mm, "end": v(24.18, -30.95) * mm});
            skArc(sketch, "E12.36.3", {"start": v(24.1, -31.13) * mm, "mid": v(24.17, -31.05) * mm, "end": v(24.18, -30.95) * mm});
            skLineSegment(sketch, "E12.36.4", {"start": v(24.1, -31.13) * mm, "end": v(23.97, -31.24) * mm});
            skLineSegment(sketch, "E12.36.5", {"start": v(23.83, -31.34) * mm, "end": v(23.97, -31.24) * mm});
            skArc(sketch, "E12.36.6", {"start": v(23.63, -31.37) * mm, "mid": v(23.73, -31.38) * mm, "end": v(23.83, -31.34) * mm});
            skArc(sketch, "E12.36.7", {"start": v(22.4, -30.82) * mm, "mid": v(23.01, -31.1) * mm, "end": v(23.63, -31.37) * mm});
            skLineSegment(sketch, "E12.36.8", {"start": v(22.4, -30.82) * mm, "end": v(21.94, -30.2) * mm});
            skArc(sketch, "E12.36.9", {"start": v(21.94, -30.2) * mm, "mid": v(21.62, -30) * mm, "end": v(21.24, -30.09) * mm});
            skArc(sketch, "E12.37.0", {"start": v(26.4, -25.69) * mm, "mid": v(26.25, -26.04) * mm, "end": v(26.4, -26.4) * mm});
            skLineSegment(sketch, "E12.37.1", {"start": v(26.94, -26.94) * mm, "end": v(26.4, -26.4) * mm});
            skArc(sketch, "E12.37.2", {"start": v(26.94, -26.94) * mm, "mid": v(27.12, -27.6) * mm, "end": v(27.28, -28.25) * mm});
            skArc(sketch, "E12.37.3", {"start": v(27.23, -28.44) * mm, "mid": v(27.28, -28.35) * mm, "end": v(27.28, -28.25) * mm});
            skLineSegment(sketch, "E12.37.4", {"start": v(27.23, -28.44) * mm, "end": v(27.1, -28.56) * mm});
            skLineSegment(sketch, "E12.37.5", {"start": v(26.98, -28.68) * mm, "end": v(27.1, -28.56) * mm});
            skArc(sketch, "E12.37.6", {"start": v(26.78, -28.72) * mm, "mid": v(26.88, -28.73) * mm, "end": v(26.98, -28.68) * mm});
            skArc(sketch, "E12.37.7", {"start": v(25.5, -28.31) * mm, "mid": v(26.14, -28.53) * mm, "end": v(26.78, -28.72) * mm});
            skLineSegment(sketch, "E12.37.8", {"start": v(25.5, -28.31) * mm, "end": v(24.98, -27.74) * mm});
            skArc(sketch, "E12.37.9", {"start": v(24.98, -27.74) * mm, "mid": v(24.63, -27.58) * mm, "end": v(24.27, -27.7) * mm});
            skArc(sketch, "E12.38.0", {"start": v(28.93, -22.79) * mm, "mid": v(28.83, -23.16) * mm, "end": v(29.01, -23.5) * mm});
            skLineSegment(sketch, "E12.38.1", {"start": v(29.6, -23.98) * mm, "end": v(29.01, -23.5) * mm});
            skArc(sketch, "E12.38.2", {"start": v(29.6, -23.98) * mm, "mid": v(29.85, -24.6) * mm, "end": v(30.09, -25.24) * mm});
            skArc(sketch, "E12.38.3", {"start": v(30.05, -25.44) * mm, "mid": v(30.1, -25.34) * mm, "end": v(30.09, -25.24) * mm});
            skLineSegment(sketch, "E12.38.4", {"start": v(30.05, -25.44) * mm, "end": v(29.94, -25.57) * mm});
            skLineSegment(sketch, "E12.38.5", {"start": v(29.83, -25.7) * mm, "end": v(29.94, -25.57) * mm});
            skArc(sketch, "E12.38.6", {"start": v(29.64, -25.77) * mm, "mid": v(29.74, -25.76) * mm, "end": v(29.83, -25.7) * mm});
            skArc(sketch, "E12.38.7", {"start": v(28.31, -25.5) * mm, "mid": v(28.97, -25.64) * mm, "end": v(29.64, -25.77) * mm});
            skLineSegment(sketch, "E12.38.8", {"start": v(28.31, -25.5) * mm, "end": v(27.74, -24.98) * mm});
            skArc(sketch, "E12.38.9", {"start": v(27.74, -24.98) * mm, "mid": v(27.38, -24.85) * mm, "end": v(27.03, -25.01) * mm});
            skArc(sketch, "E12.39.0", {"start": v(31.16, -19.64) * mm, "mid": v(31.1, -20.02) * mm, "end": v(31.31, -20.33) * mm});
            skLineSegment(sketch, "E12.39.1", {"start": v(31.95, -20.75) * mm, "end": v(31.31, -20.33) * mm});
            skArc(sketch, "E12.39.2", {"start": v(31.95, -20.75) * mm, "mid": v(32.26, -21.35) * mm, "end": v(32.56, -21.96) * mm});
            skArc(sketch, "E12.39.3", {"start": v(32.55, -22.16) * mm, "mid": v(32.58, -22.06) * mm, "end": v(32.56, -21.96) * mm});
            skLineSegment(sketch, "E12.39.4", {"start": v(32.55, -22.16) * mm, "end": v(32.45, -22.3) * mm});
            skLineSegment(sketch, "E12.39.5", {"start": v(32.35, -22.44) * mm, "end": v(32.45, -22.3) * mm});
            skArc(sketch, "E12.39.6", {"start": v(32.17, -22.53) * mm, "mid": v(32.27, -22.5) * mm, "end": v(32.35, -22.44) * mm});
            skArc(sketch, "E12.39.7", {"start": v(30.82, -22.4) * mm, "mid": v(31.5, -22.47) * mm, "end": v(32.17, -22.53) * mm});
            skLineSegment(sketch, "E12.39.8", {"start": v(30.82, -22.4) * mm, "end": v(30.2, -21.94) * mm});
            skArc(sketch, "E12.39.9", {"start": v(30.2, -21.94) * mm, "mid": v(29.83, -21.85) * mm, "end": v(29.5, -22.05) * mm});
            skArc(sketch, "E12.40.0", {"start": v(33.04, -16.27) * mm, "mid": v(33.01, -16.66) * mm, "end": v(33.27, -16.95) * mm});
            skLineSegment(sketch, "E12.40.1", {"start": v(33.95, -17.3) * mm, "end": v(33.27, -16.95) * mm});
            skArc(sketch, "E12.40.2", {"start": v(33.95, -17.3) * mm, "mid": v(34.32, -17.86) * mm, "end": v(34.68, -18.43) * mm});
            skArc(sketch, "E12.40.3", {"start": v(34.68, -18.63) * mm, "mid": v(34.7, -18.53) * mm, "end": v(34.68, -18.43) * mm});
            skLineSegment(sketch, "E12.40.4", {"start": v(34.68, -18.63) * mm, "end": v(34.6, -18.79) * mm});
            skLineSegment(sketch, "E12.40.5", {"start": v(34.52, -18.94) * mm, "end": v(34.6, -18.79) * mm});
            skArc(sketch, "E12.40.6", {"start": v(34.35, -19.04) * mm, "mid": v(34.45, -19.01) * mm, "end": v(34.52, -18.94) * mm});
            skArc(sketch, "E12.40.7", {"start": v(33, -19.05) * mm, "mid": v(33.67, -19.05) * mm, "end": v(34.35, -19.04) * mm});
            skLineSegment(sketch, "E12.40.8", {"start": v(33, -19.05) * mm, "end": v(32.33, -18.67) * mm});
            skArc(sketch, "E12.40.9", {"start": v(32.33, -18.67) * mm, "mid": v(31.95, -18.62) * mm, "end": v(31.64, -18.85) * mm});
            skArc(sketch, "E12.41.0", {"start": v(34.56, -12.73) * mm, "mid": v(34.57, -13.12) * mm, "end": v(34.85, -13.38) * mm});
            skLineSegment(sketch, "E12.41.1", {"start": v(35.57, -13.65) * mm, "end": v(34.85, -13.38) * mm});
            skArc(sketch, "E12.41.2", {"start": v(35.57, -13.65) * mm, "mid": v(36, -14.18) * mm, "end": v(36.41, -14.7) * mm});
            skArc(sketch, "E12.41.3", {"start": v(36.44, -14.9) * mm, "mid": v(36.45, -14.8) * mm, "end": v(36.41, -14.7) * mm});
            skLineSegment(sketch, "E12.41.4", {"start": v(36.44, -14.9) * mm, "end": v(36.38, -15.07) * mm});
            skLineSegment(sketch, "E12.41.5", {"start": v(36.3, -15.23) * mm, "end": v(36.38, -15.07) * mm});
            skArc(sketch, "E12.41.6", {"start": v(36.15, -15.35) * mm, "mid": v(36.24, -15.3) * mm, "end": v(36.3, -15.23) * mm});
            skArc(sketch, "E12.41.7", {"start": v(34.8, -15.5) * mm, "mid": v(35.48, -15.43) * mm, "end": v(36.15, -15.35) * mm});
            skLineSegment(sketch, "E12.41.8", {"start": v(34.8, -15.5) * mm, "end": v(34.1, -15.19) * mm});
            skArc(sketch, "E12.41.9", {"start": v(34.1, -15.19) * mm, "mid": v(33.72, -15.17) * mm, "end": v(33.44, -15.44) * mm});
            skArc(sketch, "E12.42.0", {"start": v(35.7, -9.05) * mm, "mid": v(35.76, -9.43) * mm, "end": v(36.06, -9.66) * mm});
            skLineSegment(sketch, "E12.42.1", {"start": v(36.8, -9.86) * mm, "end": v(36.06, -9.66) * mm});
            skArc(sketch, "E12.42.2", {"start": v(36.8, -9.86) * mm, "mid": v(37.28, -10.34) * mm, "end": v(37.75, -10.82) * mm});
            skArc(sketch, "E12.42.3", {"start": v(37.8, -11.01) * mm, "mid": v(37.8, -10.91) * mm, "end": v(37.75, -10.82) * mm});
            skLineSegment(sketch, "E12.42.4", {"start": v(37.8, -11.01) * mm, "end": v(37.75, -11.18) * mm});
            skLineSegment(sketch, "E12.42.5", {"start": v(37.7, -11.35) * mm, "end": v(37.75, -11.18) * mm});
            skArc(sketch, "E12.42.6", {"start": v(37.56, -11.48) * mm, "mid": v(37.65, -11.44) * mm, "end": v(37.7, -11.35) * mm});
            skArc(sketch, "E12.42.7", {"start": v(36.24, -11.77) * mm, "mid": v(36.9, -11.64) * mm, "end": v(37.56, -11.48) * mm});
            skLineSegment(sketch, "E12.42.8", {"start": v(36.24, -11.77) * mm, "end": v(35.5, -11.54) * mm});
            skArc(sketch, "E12.42.9", {"start": v(35.5, -11.54) * mm, "mid": v(35.12, -11.57) * mm, "end": v(34.87, -11.86) * mm});
            skArc(sketch, "E12.43.0", {"start": v(36.45, -5.27) * mm, "mid": v(36.55, -5.64) * mm, "end": v(36.87, -5.84) * mm});
            skLineSegment(sketch, "E12.43.1", {"start": v(37.63, -5.96) * mm, "end": v(36.87, -5.84) * mm});
            skArc(sketch, "E12.43.2", {"start": v(37.63, -5.96) * mm, "mid": v(38.16, -6.38) * mm, "end": v(38.68, -6.82) * mm});
            skArc(sketch, "E12.43.3", {"start": v(38.74, -7) * mm, "mid": v(38.73, -6.9) * mm, "end": v(38.68, -6.82) * mm});
            skLineSegment(sketch, "E12.43.4", {"start": v(38.74, -7) * mm, "end": v(38.72, -7.18) * mm});
            skLineSegment(sketch, "E12.43.5", {"start": v(38.68, -7.35) * mm, "end": v(38.72, -7.18) * mm});
            skArc(sketch, "E12.43.6", {"start": v(38.55, -7.5) * mm, "mid": v(38.63, -7.44) * mm, "end": v(38.68, -7.35) * mm});
            skArc(sketch, "E12.43.7", {"start": v(37.27, -7.92) * mm, "mid": v(37.91, -7.72) * mm, "end": v(38.55, -7.5) * mm});
            skLineSegment(sketch, "E12.43.8", {"start": v(37.27, -7.92) * mm, "end": v(36.52, -7.76) * mm});
            skArc(sketch, "E12.43.9", {"start": v(36.52, -7.76) * mm, "mid": v(36.14, -7.83) * mm, "end": v(35.92, -8.15) * mm});
            skArc(sketch, "E12.44.0", {"start": v(36.8, -1.43) * mm, "mid": v(36.93, -1.79) * mm, "end": v(37.28, -1.95) * mm});
            skLineSegment(sketch, "E12.44.1", {"start": v(38.05, -2) * mm, "end": v(37.28, -1.95) * mm});
            skArc(sketch, "E12.44.2", {"start": v(38.05, -2) * mm, "mid": v(38.62, -2.36) * mm, "end": v(39.18, -2.74) * mm});
            skArc(sketch, "E12.44.3", {"start": v(39.26, -2.91) * mm, "mid": v(39.24, -2.81) * mm, "end": v(39.18, -2.74) * mm});
            skLineSegment(sketch, "E12.44.4", {"start": v(39.26, -2.91) * mm, "end": v(39.26, -3.09) * mm});
            skLineSegment(sketch, "E12.44.5", {"start": v(39.24, -3.26) * mm, "end": v(39.26, -3.09) * mm});
            skArc(sketch, "E12.44.6", {"start": v(39.12, -3.43) * mm, "mid": v(39.2, -3.36) * mm, "end": v(39.24, -3.26) * mm});
            skArc(sketch, "E12.44.7", {"start": v(37.9, -3.98) * mm, "mid": v(38.5, -3.71) * mm, "end": v(39.12, -3.43) * mm});
            skLineSegment(sketch, "E12.44.8", {"start": v(37.9, -3.98) * mm, "end": v(37.13, -3.9) * mm});
            skArc(sketch, "E12.44.9", {"start": v(37.13, -3.9) * mm, "mid": v(36.76, -4.01) * mm, "end": v(36.57, -4.35) * mm});
            skArc(sketch, "E12.45.0", {"start": v(36.75, 2.43) * mm, "mid": v(36.92, 2.08) * mm, "end": v(37.28, 1.95) * mm});
            skLineSegment(sketch, "E12.45.1", {"start": v(38.05, 2) * mm, "end": v(37.28, 1.95) * mm});
            skArc(sketch, "E12.45.2", {"start": v(38.05, 2) * mm, "mid": v(38.65, 1.69) * mm, "end": v(39.25, 1.37) * mm});
            skArc(sketch, "E12.45.3", {"start": v(39.35, 1.2) * mm, "mid": v(39.32, 1.3) * mm, "end": v(39.25, 1.37) * mm});
            skLineSegment(sketch, "E12.45.4", {"start": v(39.35, 1.2) * mm, "end": v(39.36, 1.03) * mm});
            skLineSegment(sketch, "E12.45.5", {"start": v(39.36, 0.86) * mm, "end": v(39.36, 1.03) * mm});
            skArc(sketch, "E12.45.6", {"start": v(39.27, 0.68) * mm, "mid": v(39.34, 0.76) * mm, "end": v(39.36, 0.86) * mm});
            skArc(sketch, "E12.45.7", {"start": v(38.1, 0) * mm, "mid": v(38.69, 0.34) * mm, "end": v(39.27, 0.68) * mm});
            skLineSegment(sketch, "E12.45.8", {"start": v(38.1, 0) * mm, "end": v(37.33, 0) * mm});
            skArc(sketch, "E12.45.9", {"start": v(37.33, 0) * mm, "mid": v(36.98, -0.15) * mm, "end": v(36.83, -0.5) * mm});
            skArc(sketch, "E12.46.0", {"start": v(36.3, 6.26) * mm, "mid": v(36.5, 5.93) * mm, "end": v(36.87, 5.84) * mm});
            skLineSegment(sketch, "E12.46.1", {"start": v(37.63, 5.96) * mm, "end": v(36.87, 5.84) * mm});
            skArc(sketch, "E12.46.2", {"start": v(37.63, 5.96) * mm, "mid": v(38.26, 5.72) * mm, "end": v(38.89, 5.47) * mm});
            skArc(sketch, "E12.46.3", {"start": v(39.01, 5.31) * mm, "mid": v(38.97, 5.4) * mm, "end": v(38.89, 5.47) * mm});
            skLineSegment(sketch, "E12.46.4", {"start": v(39.01, 5.31) * mm, "end": v(39.04, 5.14) * mm});
            skLineSegment(sketch, "E12.46.5", {"start": v(39.06, 4.97) * mm, "end": v(39.04, 5.14) * mm});
            skArc(sketch, "E12.46.6", {"start": v(38.98, 4.78) * mm, "mid": v(39.04, 4.86) * mm, "end": v(39.06, 4.97) * mm});
            skArc(sketch, "E12.46.7", {"start": v(37.9, 3.98) * mm, "mid": v(38.44, 4.38) * mm, "end": v(38.98, 4.78) * mm});
            skLineSegment(sketch, "E12.46.8", {"start": v(37.9, 3.98) * mm, "end": v(37.13, 3.9) * mm});
            skArc(sketch, "E12.46.9", {"start": v(37.13, 3.9) * mm, "mid": v(36.8, 3.72) * mm, "end": v(36.68, 3.35) * mm});
            skArc(sketch, "E12.47.0", {"start": v(35.44, 10.02) * mm, "mid": v(35.68, 9.71) * mm, "end": v(36.06, 9.66) * mm});
            skLineSegment(sketch, "E12.47.1", {"start": v(36.8, 9.86) * mm, "end": v(36.06, 9.66) * mm});
            skArc(sketch, "E12.47.2", {"start": v(36.8, 9.86) * mm, "mid": v(37.46, 9.69) * mm, "end": v(38.1, 9.5) * mm});
            skArc(sketch, "E12.47.3", {"start": v(38.24, 9.36) * mm, "mid": v(38.2, 9.45) * mm, "end": v(38.1, 9.5) * mm});
            skLineSegment(sketch, "E12.47.4", {"start": v(38.24, 9.36) * mm, "end": v(38.29, 9.2) * mm});
            skLineSegment(sketch, "E12.47.5", {"start": v(38.32, 9.02) * mm, "end": v(38.29, 9.2) * mm});
            skArc(sketch, "E12.47.6", {"start": v(38.27, 8.83) * mm, "mid": v(38.32, 8.92) * mm, "end": v(38.32, 9.02) * mm});
            skArc(sketch, "E12.47.7", {"start": v(37.27, 7.92) * mm, "mid": v(37.77, 8.37) * mm, "end": v(38.27, 8.83) * mm});
            skLineSegment(sketch, "E12.47.8", {"start": v(37.27, 7.92) * mm, "end": v(36.52, 7.76) * mm});
            skArc(sketch, "E12.47.9", {"start": v(36.52, 7.76) * mm, "mid": v(36.2, 7.54) * mm, "end": v(36.13, 7.17) * mm});
            skArc(sketch, "E12.48.0", {"start": v(34.2, 13.67) * mm, "mid": v(34.47, 13.39) * mm, "end": v(34.85, 13.38) * mm});
            skLineSegment(sketch, "E12.48.1", {"start": v(35.57, 13.65) * mm, "end": v(34.85, 13.38) * mm});
            skArc(sketch, "E12.48.2", {"start": v(35.57, 13.65) * mm, "mid": v(36.24, 13.55) * mm, "end": v(36.9, 13.43) * mm});
            skArc(sketch, "E12.48.3", {"start": v(37.06, 13.3) * mm, "mid": v(37, 13.4) * mm, "end": v(36.9, 13.43) * mm});
            skLineSegment(sketch, "E12.48.4", {"start": v(37.06, 13.3) * mm, "end": v(37.12, 13.14) * mm});
            skLineSegment(sketch, "E12.48.5", {"start": v(37.17, 12.98) * mm, "end": v(37.12, 13.14) * mm});
            skArc(sketch, "E12.48.6", {"start": v(37.13, 12.78) * mm, "mid": v(37.18, 12.88) * mm, "end": v(37.17, 12.98) * mm});
            skArc(sketch, "E12.48.7", {"start": v(36.24, 11.77) * mm, "mid": v(36.69, 12.27) * mm, "end": v(37.13, 12.78) * mm});
            skLineSegment(sketch, "E12.48.8", {"start": v(36.24, 11.77) * mm, "end": v(35.5, 11.54) * mm});
            skArc(sketch, "E12.48.9", {"start": v(35.5, 11.54) * mm, "mid": v(35.21, 11.29) * mm, "end": v(35.18, 10.9) * mm});
            skArc(sketch, "E12.49.0", {"start": v(32.59, 17.17) * mm, "mid": v(32.88, 16.92) * mm, "end": v(33.27, 16.95) * mm});
            skLineSegment(sketch, "E12.49.1", {"start": v(33.95, 17.3) * mm, "end": v(33.27, 16.95) * mm});
            skArc(sketch, "E12.49.2", {"start": v(33.95, 17.3) * mm, "mid": v(34.62, 17.26) * mm, "end": v(35.3, 17.22) * mm});
            skArc(sketch, "E12.49.3", {"start": v(35.46, 17.1) * mm, "mid": v(35.4, 17.18) * mm, "end": v(35.3, 17.22) * mm});
            skLineSegment(sketch, "E12.49.4", {"start": v(35.46, 17.1) * mm, "end": v(35.54, 16.95) * mm});
            skLineSegment(sketch, "E12.49.5", {"start": v(35.61, 16.8) * mm, "end": v(35.54, 16.95) * mm});
            skArc(sketch, "E12.49.6", {"start": v(35.6, 16.6) * mm, "mid": v(35.63, 16.7) * mm, "end": v(35.61, 16.8) * mm});
            skArc(sketch, "E12.49.7", {"start": v(34.8, 15.5) * mm, "mid": v(35.2, 16.04) * mm, "end": v(35.6, 16.6) * mm});
            skLineSegment(sketch, "E12.49.8", {"start": v(34.8, 15.5) * mm, "end": v(34.1, 15.19) * mm});
            skArc(sketch, "E12.49.9", {"start": v(34.1, 15.19) * mm, "mid": v(33.84, 14.9) * mm, "end": v(33.85, 14.52) * mm});
            skArc(sketch, "E12.50.0", {"start": v(30.61, 20.48) * mm, "mid": v(30.93, 20.26) * mm, "end": v(31.31, 20.33) * mm});
            skLineSegment(sketch, "E12.50.1", {"start": v(31.95, 20.75) * mm, "end": v(31.31, 20.33) * mm});
            skArc(sketch, "E12.50.2", {"start": v(31.95, 20.75) * mm, "mid": v(32.63, 20.79) * mm, "end": v(33.3, 20.81) * mm});
            skArc(sketch, "E12.50.3", {"start": v(33.48, 20.72) * mm, "mid": v(33.4, 20.79) * mm, "end": v(33.3, 20.81) * mm});
            skLineSegment(sketch, "E12.50.4", {"start": v(33.48, 20.72) * mm, "end": v(33.57, 20.57) * mm});
            skLineSegment(sketch, "E12.50.5", {"start": v(33.66, 20.42) * mm, "end": v(33.57, 20.57) * mm});
            skArc(sketch, "E12.50.6", {"start": v(33.66, 20.22) * mm, "mid": v(33.69, 20.32) * mm, "end": v(33.66, 20.42) * mm});
            skArc(sketch, "E12.50.7", {"start": v(33, 19.05) * mm, "mid": v(33.34, 19.63) * mm, "end": v(33.66, 20.22) * mm});
            skLineSegment(sketch, "E12.50.8", {"start": v(33, 19.05) * mm, "end": v(32.33, 18.67) * mm});
            skArc(sketch, "E12.50.9", {"start": v(32.33, 18.67) * mm, "mid": v(32.1, 18.36) * mm, "end": v(32.14, 17.98) * mm});
            skArc(sketch, "E12.51.0", {"start": v(28.3, 23.57) * mm, "mid": v(28.65, 23.38) * mm, "end": v(29.01, 23.5) * mm});
            skLineSegment(sketch, "E12.51.1", {"start": v(29.6, 23.98) * mm, "end": v(29.01, 23.5) * mm});
            skArc(sketch, "E12.51.2", {"start": v(29.6, 23.98) * mm, "mid": v(30.28, 24.09) * mm, "end": v(30.95, 24.18) * mm});
            skArc(sketch, "E12.51.3", {"start": v(31.13, 24.1) * mm, "mid": v(31.05, 24.17) * mm, "end": v(30.95, 24.18) * mm});
            skLineSegment(sketch, "E12.51.4", {"start": v(31.13, 24.1) * mm, "end": v(31.24, 23.97) * mm});
            skLineSegment(sketch, "E12.51.5", {"start": v(31.34, 23.83) * mm, "end": v(31.24, 23.97) * mm});
            skArc(sketch, "E12.51.6", {"start": v(31.37, 23.63) * mm, "mid": v(31.38, 23.73) * mm, "end": v(31.34, 23.83) * mm});
            skArc(sketch, "E12.51.7", {"start": v(30.82, 22.4) * mm, "mid": v(31.1, 23.01) * mm, "end": v(31.37, 23.63) * mm});
            skLineSegment(sketch, "E12.51.8", {"start": v(30.82, 22.4) * mm, "end": v(30.2, 21.94) * mm});
            skArc(sketch, "E12.51.9", {"start": v(30.2, 21.94) * mm, "mid": v(30, 21.62) * mm, "end": v(30.09, 21.24) * mm});
            skArc(sketch, "E12.52.0", {"start": v(25.69, 26.4) * mm, "mid": v(26.04, 26.25) * mm, "end": v(26.4, 26.4) * mm});
            skLineSegment(sketch, "E12.52.1", {"start": v(26.94, 26.94) * mm, "end": v(26.4, 26.4) * mm});
            skArc(sketch, "E12.52.2", {"start": v(26.94, 26.94) * mm, "mid": v(27.6, 27.12) * mm, "end": v(28.25, 27.28) * mm});
            skArc(sketch, "E12.52.3", {"start": v(28.44, 27.23) * mm, "mid": v(28.35, 27.28) * mm, "end": v(28.25, 27.28) * mm});
            skLineSegment(sketch, "E12.52.4", {"start": v(28.44, 27.23) * mm, "end": v(28.56, 27.1) * mm});
            skLineSegment(sketch, "E12.52.5", {"start": v(28.68, 26.98) * mm, "end": v(28.56, 27.1) * mm});
            skArc(sketch, "E12.52.6", {"start": v(28.72, 26.78) * mm, "mid": v(28.73, 26.88) * mm, "end": v(28.68, 26.98) * mm});
            skArc(sketch, "E12.52.7", {"start": v(28.31, 25.5) * mm, "mid": v(28.53, 26.14) * mm, "end": v(28.72, 26.78) * mm});
            skLineSegment(sketch, "E12.52.8", {"start": v(28.31, 25.5) * mm, "end": v(27.74, 24.98) * mm});
            skArc(sketch, "E12.52.9", {"start": v(27.74, 24.98) * mm, "mid": v(27.58, 24.63) * mm, "end": v(27.7, 24.27) * mm});
            skArc(sketch, "E12.53.0", {"start": v(22.79, 28.93) * mm, "mid": v(23.16, 28.83) * mm, "end": v(23.5, 29.01) * mm});
            skLineSegment(sketch, "E12.53.1", {"start": v(23.98, 29.6) * mm, "end": v(23.5, 29.01) * mm});
            skArc(sketch, "E12.53.2", {"start": v(23.98, 29.6) * mm, "mid": v(24.6, 29.85) * mm, "end": v(25.24, 30.09) * mm});
            skArc(sketch, "E12.53.3", {"start": v(25.44, 30.05) * mm, "mid": v(25.34, 30.1) * mm, "end": v(25.24, 30.09) * mm});
            skLineSegment(sketch, "E12.53.4", {"start": v(25.44, 30.05) * mm, "end": v(25.57, 29.94) * mm});
            skLineSegment(sketch, "E12.53.5", {"start": v(25.7, 29.83) * mm, "end": v(25.57, 29.94) * mm});
            skArc(sketch, "E12.53.6", {"start": v(25.77, 29.64) * mm, "mid": v(25.76, 29.74) * mm, "end": v(25.7, 29.83) * mm});
            skArc(sketch, "E12.53.7", {"start": v(25.5, 28.31) * mm, "mid": v(25.64, 28.97) * mm, "end": v(25.77, 29.64) * mm});
            skLineSegment(sketch, "E12.53.8", {"start": v(25.5, 28.31) * mm, "end": v(24.98, 27.74) * mm});
            skArc(sketch, "E12.53.9", {"start": v(24.98, 27.74) * mm, "mid": v(24.85, 27.38) * mm, "end": v(25.01, 27.03) * mm});
            skArc(sketch, "E12.54.0", {"start": v(19.64, 31.16) * mm, "mid": v(20.02, 31.1) * mm, "end": v(20.33, 31.31) * mm});
            skLineSegment(sketch, "E12.54.1", {"start": v(20.75, 31.95) * mm, "end": v(20.33, 31.31) * mm});
            skArc(sketch, "E12.54.2", {"start": v(20.75, 31.95) * mm, "mid": v(21.35, 32.26) * mm, "end": v(21.96, 32.56) * mm});
            skArc(sketch, "E12.54.3", {"start": v(22.16, 32.55) * mm, "mid": v(22.06, 32.58) * mm, "end": v(21.96, 32.56) * mm});
            skLineSegment(sketch, "E12.54.4", {"start": v(22.16, 32.55) * mm, "end": v(22.3, 32.45) * mm});
            skLineSegment(sketch, "E12.54.5", {"start": v(22.44, 32.35) * mm, "end": v(22.3, 32.45) * mm});
            skArc(sketch, "E12.54.6", {"start": v(22.53, 32.17) * mm, "mid": v(22.5, 32.27) * mm, "end": v(22.44, 32.35) * mm});
            skArc(sketch, "E12.54.7", {"start": v(22.4, 30.82) * mm, "mid": v(22.47, 31.5) * mm, "end": v(22.53, 32.17) * mm});
            skLineSegment(sketch, "E12.54.8", {"start": v(22.4, 30.82) * mm, "end": v(21.94, 30.2) * mm});
            skArc(sketch, "E12.54.9", {"start": v(21.94, 30.2) * mm, "mid": v(21.85, 29.83) * mm, "end": v(22.05, 29.5) * mm});
            skArc(sketch, "E12.55.0", {"start": v(16.27, 33.04) * mm, "mid": v(16.66, 33.01) * mm, "end": v(16.95, 33.27) * mm});
            skLineSegment(sketch, "E12.55.1", {"start": v(17.3, 33.95) * mm, "end": v(16.95, 33.27) * mm});
            skArc(sketch, "E12.55.2", {"start": v(17.3, 33.95) * mm, "mid": v(17.86, 34.32) * mm, "end": v(18.43, 34.68) * mm});
            skArc(sketch, "E12.55.3", {"start": v(18.63, 34.68) * mm, "mid": v(18.53, 34.7) * mm, "end": v(18.43, 34.68) * mm});
            skLineSegment(sketch, "E12.55.4", {"start": v(18.63, 34.68) * mm, "end": v(18.79, 34.6) * mm});
            skLineSegment(sketch, "E12.55.5", {"start": v(18.94, 34.52) * mm, "end": v(18.79, 34.6) * mm});
            skArc(sketch, "E12.55.6", {"start": v(19.04, 34.35) * mm, "mid": v(19.01, 34.45) * mm, "end": v(18.94, 34.52) * mm});
            skArc(sketch, "E12.55.7", {"start": v(19.05, 33) * mm, "mid": v(19.05, 33.67) * mm, "end": v(19.04, 34.35) * mm});
            skLineSegment(sketch, "E12.55.8", {"start": v(19.05, 33) * mm, "end": v(18.67, 32.33) * mm});
            skArc(sketch, "E12.55.9", {"start": v(18.67, 32.33) * mm, "mid": v(18.62, 31.95) * mm, "end": v(18.85, 31.64) * mm});
            skArc(sketch, "E12.56.0", {"start": v(12.73, 34.56) * mm, "mid": v(13.12, 34.57) * mm, "end": v(13.38, 34.85) * mm});
            skLineSegment(sketch, "E12.56.1", {"start": v(13.65, 35.57) * mm, "end": v(13.38, 34.85) * mm});
            skArc(sketch, "E12.56.2", {"start": v(13.65, 35.57) * mm, "mid": v(14.18, 36) * mm, "end": v(14.7, 36.41) * mm});
            skArc(sketch, "E12.56.3", {"start": v(14.9, 36.44) * mm, "mid": v(14.8, 36.45) * mm, "end": v(14.7, 36.41) * mm});
            skLineSegment(sketch, "E12.56.4", {"start": v(14.9, 36.44) * mm, "end": v(15.07, 36.38) * mm});
            skLineSegment(sketch, "E12.56.5", {"start": v(15.23, 36.3) * mm, "end": v(15.07, 36.38) * mm});
            skArc(sketch, "E12.56.6", {"start": v(15.35, 36.15) * mm, "mid": v(15.3, 36.24) * mm, "end": v(15.23, 36.3) * mm});
            skArc(sketch, "E12.56.7", {"start": v(15.5, 34.8) * mm, "mid": v(15.43, 35.48) * mm, "end": v(15.35, 36.15) * mm});
            skLineSegment(sketch, "E12.56.8", {"start": v(15.5, 34.8) * mm, "end": v(15.19, 34.1) * mm});
            skArc(sketch, "E12.56.9", {"start": v(15.19, 34.1) * mm, "mid": v(15.17, 33.72) * mm, "end": v(15.44, 33.44) * mm});
            skArc(sketch, "E12.57.0", {"start": v(9.05, 35.7) * mm, "mid": v(9.43, 35.76) * mm, "end": v(9.66, 36.06) * mm});
            skLineSegment(sketch, "E12.57.1", {"start": v(9.86, 36.8) * mm, "end": v(9.66, 36.06) * mm});
            skArc(sketch, "E12.57.2", {"start": v(9.86, 36.8) * mm, "mid": v(10.34, 37.28) * mm, "end": v(10.82, 37.75) * mm});
            skArc(sketch, "E12.57.3", {"start": v(11.01, 37.8) * mm, "mid": v(10.91, 37.8) * mm, "end": v(10.82, 37.75) * mm});
            skLineSegment(sketch, "E12.57.4", {"start": v(11.01, 37.8) * mm, "end": v(11.18, 37.75) * mm});
            skLineSegment(sketch, "E12.57.5", {"start": v(11.35, 37.7) * mm, "end": v(11.18, 37.75) * mm});
            skArc(sketch, "E12.57.6", {"start": v(11.48, 37.56) * mm, "mid": v(11.44, 37.65) * mm, "end": v(11.35, 37.7) * mm});
            skArc(sketch, "E12.57.7", {"start": v(11.77, 36.24) * mm, "mid": v(11.64, 36.9) * mm, "end": v(11.48, 37.56) * mm});
            skLineSegment(sketch, "E12.57.8", {"start": v(11.77, 36.24) * mm, "end": v(11.54, 35.5) * mm});
            skArc(sketch, "E12.57.9", {"start": v(11.54, 35.5) * mm, "mid": v(11.57, 35.12) * mm, "end": v(11.86, 34.87) * mm});
            skArc(sketch, "E12.58.0", {"start": v(5.27, 36.45) * mm, "mid": v(5.64, 36.55) * mm, "end": v(5.84, 36.87) * mm});
            skLineSegment(sketch, "E12.58.1", {"start": v(5.96, 37.63) * mm, "end": v(5.84, 36.87) * mm});
            skArc(sketch, "E12.58.2", {"start": v(5.96, 37.63) * mm, "mid": v(6.38, 38.16) * mm, "end": v(6.82, 38.68) * mm});
            skArc(sketch, "E12.58.3", {"start": v(7, 38.74) * mm, "mid": v(6.9, 38.73) * mm, "end": v(6.82, 38.68) * mm});
            skLineSegment(sketch, "E12.58.4", {"start": v(7, 38.74) * mm, "end": v(7.18, 38.72) * mm});
            skLineSegment(sketch, "E12.58.5", {"start": v(7.35, 38.68) * mm, "end": v(7.18, 38.72) * mm});
            skArc(sketch, "E12.58.6", {"start": v(7.5, 38.55) * mm, "mid": v(7.44, 38.63) * mm, "end": v(7.35, 38.68) * mm});
            skArc(sketch, "E12.58.7", {"start": v(7.92, 37.27) * mm, "mid": v(7.72, 37.91) * mm, "end": v(7.5, 38.55) * mm});
            skLineSegment(sketch, "E12.58.8", {"start": v(7.92, 37.27) * mm, "end": v(7.76, 36.52) * mm});
            skArc(sketch, "E12.58.9", {"start": v(7.76, 36.52) * mm, "mid": v(7.83, 36.14) * mm, "end": v(8.15, 35.92) * mm});
            skArc(sketch, "E12.59.0", {"start": v(1.43, 36.8) * mm, "mid": v(1.79, 36.93) * mm, "end": v(1.95, 37.28) * mm});
            skLineSegment(sketch, "E12.59.1", {"start": v(2, 38.05) * mm, "end": v(1.95, 37.28) * mm});
            skArc(sketch, "E12.59.2", {"start": v(2, 38.05) * mm, "mid": v(2.36, 38.62) * mm, "end": v(2.74, 39.18) * mm});
            skArc(sketch, "E12.59.3", {"start": v(2.91, 39.26) * mm, "mid": v(2.81, 39.24) * mm, "end": v(2.74, 39.18) * mm});
            skLineSegment(sketch, "E12.59.4", {"start": v(2.91, 39.26) * mm, "end": v(3.09, 39.26) * mm});
            skLineSegment(sketch, "E12.59.5", {"start": v(3.26, 39.24) * mm, "end": v(3.09, 39.26) * mm});
            skArc(sketch, "E12.59.6", {"start": v(3.43, 39.12) * mm, "mid": v(3.36, 39.2) * mm, "end": v(3.26, 39.24) * mm});
            skArc(sketch, "E12.59.7", {"start": v(3.98, 37.9) * mm, "mid": v(3.71, 38.5) * mm, "end": v(3.43, 39.12) * mm});
            skLineSegment(sketch, "E12.59.8", {"start": v(3.98, 37.9) * mm, "end": v(3.9, 37.13) * mm});
            skArc(sketch, "E12.59.9", {"start": v(3.9, 37.13) * mm, "mid": v(4.01, 36.76) * mm, "end": v(4.35, 36.57) * mm});
            skArc(sketch, "E13.trimOffspring", {"start": v(-23.57, 28.3) * mm, "mid": v(12.3, -34.72) * mm, "end": v(0.5, 36.83) * mm});
            skArc(sketch, "E14.trimOffspring", {"start": v(-20.48, 30.61) * mm, "mid": v(-20.86, 30.35) * mm, "end": v(-21.24, 30.09) * mm});
            skSolve(sketch);
        }
        {
            var Q0;
            Q0 = qSketchRegion(id + "F0", true);
            extrude(context, id + "F1", {"entities" : qUnion([Q0]), "depth" : 6.35 * mm});
        }
        {
            var Q0;
            Q0=makeQuery(id+"F1.opExtrude","CAP_FACE",FACE,{"disambiguationData":[OSD([sQuery(id+"F0.wireOp",EDGE,"E0"),sQuery(id+"F0.wireOp",EDGE,"E2"),sQuery(id+"F0.wireOp",EDGE,"E3"),sQuery(id+"F0.wireOp",EDGE,"E4.trimOffspring"),sQuery(id+"F0.wireOp",EDGE,"E5.MirrorCS"),sQuery(id+"F0.wireOp",EDGE,"E6.MirrorCS"),sQuery(id+"F0.wireOp",EDGE,"E7.MirrorCS"),sQuery(id+"F0.wireOp",EDGE,"E8.filletArc"),sQuery(id+"F0.wireOp",EDGE,"E9.filletArc"),sQuery(id+"F0.wireOp",EDGE,"E10.filletArc"),sQuery(id+"F0.wireOp",EDGE,"E11.filletArc"),sQuery(id+"F0.wireOp",EDGE,"E12.1.0"),sQuery(id+"F0.wireOp",EDGE,"E12.1.1"),sQuery(id+"F0.wireOp",EDGE,"E12.1.2"),sQuery(id+"F0.wireOp",EDGE,"E12.1.3"),sQuery(id+"F0.wireOp",EDGE,"E12.1.4"),sQuery(id+"F0.wireOp",EDGE,"E12.1.5"),sQuery(id+"F0.wireOp",EDGE,"E12.1.6"),sQuery(id+"F0.wireOp",EDGE,"E12.1.7"),sQuery(id+"F0.wireOp",EDGE,"E12.1.8"),sQuery(id+"F0.wireOp",EDGE,"E12.1.9"),sQuery(id+"F0.wireOp",EDGE,"E12.2.0"),sQuery(id+"F0.wireOp",EDGE,"E12.2.1"),sQuery(id+"F0.wireOp",EDGE,"E12.2.2"),sQuery(id+"F0.wireOp",EDGE,"E12.2.3"),sQuery(id+"F0.wireOp",EDGE,"E12.2.4"),sQuery(id+"F0.wireOp",EDGE,"E12.2.5"),sQuery(id+"F0.wireOp",EDGE,"E12.2.6"),sQuery(id+"F0.wireOp",EDGE,"E12.2.7"),sQuery(id+"F0.wireOp",EDGE,"E12.2.8"),sQuery(id+"F0.wireOp",EDGE,"E12.2.9"),sQuery(id+"F0.wireOp",EDGE,"E12.3.0"),sQuery(id+"F0.wireOp",EDGE,"E12.3.1"),sQuery(id+"F0.wireOp",EDGE,"E12.3.2"),sQuery(id+"F0.wireOp",EDGE,"E12.3.3"),sQuery(id+"F0.wireOp",EDGE,"E12.3.4"),sQuery(id+"F0.wireOp",EDGE,"E12.3.5"),sQuery(id+"F0.wireOp",EDGE,"E12.3.6"),sQuery(id+"F0.wireOp",EDGE,"E12.3.7"),sQuery(id+"F0.wireOp",EDGE,"E12.3.8"),sQuery(id+"F0.wireOp",EDGE,"E12.3.9"),sQuery(id+"F0.wireOp",EDGE,"E12.4.0"),sQuery(id+"F0.wireOp",EDGE,"E12.4.1"),sQuery(id+"F0.wireOp",EDGE,"E12.4.2"),sQuery(id+"F0.wireOp",EDGE,"E12.4.3"),sQuery(id+"F0.wireOp",EDGE,"E12.4.4"),sQuery(id+"F0.wireOp",EDGE,"E12.4.5"),sQuery(id+"F0.wireOp",EDGE,"E12.4.6"),sQuery(id+"F0.wireOp",EDGE,"E12.4.7"),sQuery(id+"F0.wireOp",EDGE,"E12.4.8"),sQuery(id+"F0.wireOp",EDGE,"E12.4.9"),sQuery(id+"F0.wireOp",EDGE,"E12.5.0"),sQuery(id+"F0.wireOp",EDGE,"E12.5.1"),sQuery(id+"F0.wireOp",EDGE,"E12.5.2"),sQuery(id+"F0.wireOp",EDGE,"E12.5.3"),sQuery(id+"F0.wireOp",EDGE,"E12.5.4"),sQuery(id+"F0.wireOp",EDGE,"E12.5.5"),sQuery(id+"F0.wireOp",EDGE,"E12.5.6"),sQuery(id+"F0.wireOp",EDGE,"E12.5.7"),sQuery(id+"F0.wireOp",EDGE,"E12.5.8"),sQuery(id+"F0.wireOp",EDGE,"E12.5.9"),sQuery(id+"F0.wireOp",EDGE,"E12.6.0"),sQuery(id+"F0.wireOp",EDGE,"E12.6.1"),sQuery(id+"F0.wireOp",EDGE,"E12.6.2"),sQuery(id+"F0.wireOp",EDGE,"E12.6.3"),sQuery(id+"F0.wireOp",EDGE,"E12.6.4"),sQuery(id+"F0.wireOp",EDGE,"E12.6.5"),sQuery(id+"F0.wireOp",EDGE,"E12.6.6"),sQuery(id+"F0.wireOp",EDGE,"E12.6.7"),sQuery(id+"F0.wireOp",EDGE,"E12.6.8"),sQuery(id+"F0.wireOp",EDGE,"E12.6.9"),sQuery(id+"F0.wireOp",EDGE,"E12.7.0"),sQuery(id+"F0.wireOp",EDGE,"E12.7.1"),sQuery(id+"F0.wireOp",EDGE,"E12.7.2"),sQuery(id+"F0.wireOp",EDGE,"E12.7.3"),sQuery(id+"F0.wireOp",EDGE,"E12.7.4"),sQuery(id+"F0.wireOp",EDGE,"E12.7.5"),sQuery(id+"F0.wireOp",EDGE,"E12.7.6"),sQuery(id+"F0.wireOp",EDGE,"E12.7.7"),sQuery(id+"F0.wireOp",EDGE,"E12.7.8"),sQuery(id+"F0.wireOp",EDGE,"E12.7.9"),sQuery(id+"F0.wireOp",EDGE,"E12.8.0"),sQuery(id+"F0.wireOp",EDGE,"E12.8.1"),sQuery(id+"F0.wireOp",EDGE,"E12.8.2"),sQuery(id+"F0.wireOp",EDGE,"E12.8.3"),sQuery(id+"F0.wireOp",EDGE,"E12.8.4"),sQuery(id+"F0.wireOp",EDGE,"E12.8.5"),sQuery(id+"F0.wireOp",EDGE,"E12.8.6"),sQuery(id+"F0.wireOp",EDGE,"E12.8.7"),sQuery(id+"F0.wireOp",EDGE,"E12.8.8"),sQuery(id+"F0.wireOp",EDGE,"E12.8.9"),sQuery(id+"F0.wireOp",EDGE,"E12.9.0"),sQuery(id+"F0.wireOp",EDGE,"E12.9.1"),sQuery(id+"F0.wireOp",EDGE,"E12.9.2"),sQuery(id+"F0.wireOp",EDGE,"E12.9.3"),sQuery(id+"F0.wireOp",EDGE,"E12.9.4"),sQuery(id+"F0.wireOp",EDGE,"E12.9.5"),sQuery(id+"F0.wireOp",EDGE,"E12.9.6"),sQuery(id+"F0.wireOp",EDGE,"E12.9.7"),sQuery(id+"F0.wireOp",EDGE,"E12.9.8"),sQuery(id+"F0.wireOp",EDGE,"E12.9.9"),sQuery(id+"F0.wireOp",EDGE,"E12.10.0"),sQuery(id+"F0.wireOp",EDGE,"E12.10.1"),sQuery(id+"F0.wireOp",EDGE,"E12.10.2"),sQuery(id+"F0.wireOp",EDGE,"E12.10.3"),sQuery(id+"F0.wireOp",EDGE,"E12.10.4"),sQuery(id+"F0.wireOp",EDGE,"E12.10.5"),sQuery(id+"F0.wireOp",EDGE,"E12.10.6"),sQuery(id+"F0.wireOp",EDGE,"E12.10.7"),sQuery(id+"F0.wireOp",EDGE,"E12.10.8"),sQuery(id+"F0.wireOp",EDGE,"E12.10.9"),sQuery(id+"F0.wireOp",EDGE,"E12.11.0"),sQuery(id+"F0.wireOp",EDGE,"E12.11.1"),sQuery(id+"F0.wireOp",EDGE,"E12.11.2"),sQuery(id+"F0.wireOp",EDGE,"E12.11.3"),sQuery(id+"F0.wireOp",EDGE,"E12.11.4"),sQuery(id+"F0.wireOp",EDGE,"E12.11.5"),sQuery(id+"F0.wireOp",EDGE,"E12.11.6"),sQuery(id+"F0.wireOp",EDGE,"E12.11.7"),sQuery(id+"F0.wireOp",EDGE,"E12.11.8"),sQuery(id+"F0.wireOp",EDGE,"E12.11.9"),sQuery(id+"F0.wireOp",EDGE,"E12.12.0"),sQuery(id+"F0.wireOp",EDGE,"E12.12.1"),sQuery(id+"F0.wireOp",EDGE,"E12.12.2"),sQuery(id+"F0.wireOp",EDGE,"E12.12.3"),sQuery(id+"F0.wireOp",EDGE,"E12.12.4"),sQuery(id+"F0.wireOp",EDGE,"E12.12.5"),sQuery(id+"F0.wireOp",EDGE,"E12.12.6"),sQuery(id+"F0.wireOp",EDGE,"E12.12.7"),sQuery(id+"F0.wireOp",EDGE,"E12.12.8"),sQuery(id+"F0.wireOp",EDGE,"E12.12.9"),sQuery(id+"F0.wireOp",EDGE,"E12.13.0"),sQuery(id+"F0.wireOp",EDGE,"E12.13.1"),sQuery(id+"F0.wireOp",EDGE,"E12.13.2"),sQuery(id+"F0.wireOp",EDGE,"E12.13.3"),sQuery(id+"F0.wireOp",EDGE,"E12.13.4"),sQuery(id+"F0.wireOp",EDGE,"E12.13.5"),sQuery(id+"F0.wireOp",EDGE,"E12.13.6"),sQuery(id+"F0.wireOp",EDGE,"E12.13.7"),sQuery(id+"F0.wireOp",EDGE,"E12.13.8"),sQuery(id+"F0.wireOp",EDGE,"E12.13.9"),sQuery(id+"F0.wireOp",EDGE,"E12.14.0"),sQuery(id+"F0.wireOp",EDGE,"E12.14.1"),sQuery(id+"F0.wireOp",EDGE,"E12.14.2"),sQuery(id+"F0.wireOp",EDGE,"E12.14.3"),sQuery(id+"F0.wireOp",EDGE,"E12.14.4"),sQuery(id+"F0.wireOp",EDGE,"E12.14.5"),sQuery(id+"F0.wireOp",EDGE,"E12.14.6"),sQuery(id+"F0.wireOp",EDGE,"E12.14.7"),sQuery(id+"F0.wireOp",EDGE,"E12.14.8"),sQuery(id+"F0.wireOp",EDGE,"E12.14.9"),sQuery(id+"F0.wireOp",EDGE,"E12.15.0"),sQuery(id+"F0.wireOp",EDGE,"E12.15.1"),sQuery(id+"F0.wireOp",EDGE,"E12.15.2"),sQuery(id+"F0.wireOp",EDGE,"E12.15.3"),sQuery(id+"F0.wireOp",EDGE,"E12.15.4"),sQuery(id+"F0.wireOp",EDGE,"E12.15.5"),sQuery(id+"F0.wireOp",EDGE,"E12.15.6"),sQuery(id+"F0.wireOp",EDGE,"E12.15.7"),sQuery(id+"F0.wireOp",EDGE,"E12.15.8"),sQuery(id+"F0.wireOp",EDGE,"E12.15.9"),sQuery(id+"F0.wireOp",EDGE,"E12.16.0"),sQuery(id+"F0.wireOp",EDGE,"E12.16.1"),sQuery(id+"F0.wireOp",EDGE,"E12.16.2"),sQuery(id+"F0.wireOp",EDGE,"E12.16.3"),sQuery(id+"F0.wireOp",EDGE,"E12.16.4"),sQuery(id+"F0.wireOp",EDGE,"E12.16.5"),sQuery(id+"F0.wireOp",EDGE,"E12.16.6"),sQuery(id+"F0.wireOp",EDGE,"E12.16.7"),sQuery(id+"F0.wireOp",EDGE,"E12.16.8"),sQuery(id+"F0.wireOp",EDGE,"E12.16.9"),sQuery(id+"F0.wireOp",EDGE,"E12.17.0"),sQuery(id+"F0.wireOp",EDGE,"E12.17.1"),sQuery(id+"F0.wireOp",EDGE,"E12.17.2"),sQuery(id+"F0.wireOp",EDGE,"E12.17.3"),sQuery(id+"F0.wireOp",EDGE,"E12.17.4"),sQuery(id+"F0.wireOp",EDGE,"E12.17.5"),sQuery(id+"F0.wireOp",EDGE,"E12.17.6"),sQuery(id+"F0.wireOp",EDGE,"E12.17.7"),sQuery(id+"F0.wireOp",EDGE,"E12.17.8"),sQuery(id+"F0.wireOp",EDGE,"E12.17.9"),sQuery(id+"F0.wireOp",EDGE,"E12.18.0"),sQuery(id+"F0.wireOp",EDGE,"E12.18.1"),sQuery(id+"F0.wireOp",EDGE,"E12.18.2"),sQuery(id+"F0.wireOp",EDGE,"E12.18.3"),sQuery(id+"F0.wireOp",EDGE,"E12.18.4"),sQuery(id+"F0.wireOp",EDGE,"E12.18.5"),sQuery(id+"F0.wireOp",EDGE,"E12.18.6"),sQuery(id+"F0.wireOp",EDGE,"E12.18.7"),sQuery(id+"F0.wireOp",EDGE,"E12.18.8"),sQuery(id+"F0.wireOp",EDGE,"E12.18.9"),sQuery(id+"F0.wireOp",EDGE,"E12.19.0"),sQuery(id+"F0.wireOp",EDGE,"E12.19.1"),sQuery(id+"F0.wireOp",EDGE,"E12.19.2"),sQuery(id+"F0.wireOp",EDGE,"E12.19.3"),sQuery(id+"F0.wireOp",EDGE,"E12.19.4"),sQuery(id+"F0.wireOp",EDGE,"E12.19.5"),sQuery(id+"F0.wireOp",EDGE,"E12.19.6"),sQuery(id+"F0.wireOp",EDGE,"E12.19.7"),sQuery(id+"F0.wireOp",EDGE,"E12.19.8"),sQuery(id+"F0.wireOp",EDGE,"E12.19.9"),sQuery(id+"F0.wireOp",EDGE,"E12.20.0"),sQuery(id+"F0.wireOp",EDGE,"E12.20.1"),sQuery(id+"F0.wireOp",EDGE,"E12.20.2"),sQuery(id+"F0.wireOp",EDGE,"E12.20.3"),sQuery(id+"F0.wireOp",EDGE,"E12.20.4"),sQuery(id+"F0.wireOp",EDGE,"E12.20.5"),sQuery(id+"F0.wireOp",EDGE,"E12.20.6"),sQuery(id+"F0.wireOp",EDGE,"E12.20.7"),sQuery(id+"F0.wireOp",EDGE,"E12.20.8"),sQuery(id+"F0.wireOp",EDGE,"E12.20.9"),sQuery(id+"F0.wireOp",EDGE,"E12.21.0"),sQuery(id+"F0.wireOp",EDGE,"E12.21.1"),sQuery(id+"F0.wireOp",EDGE,"E12.21.2"),sQuery(id+"F0.wireOp",EDGE,"E12.21.3"),sQuery(id+"F0.wireOp",EDGE,"E12.21.4"),sQuery(id+"F0.wireOp",EDGE,"E12.21.5"),sQuery(id+"F0.wireOp",EDGE,"E12.21.6"),sQuery(id+"F0.wireOp",EDGE,"E12.21.7"),sQuery(id+"F0.wireOp",EDGE,"E12.21.8"),sQuery(id+"F0.wireOp",EDGE,"E12.21.9"),sQuery(id+"F0.wireOp",EDGE,"E12.22.0"),sQuery(id+"F0.wireOp",EDGE,"E12.22.1"),sQuery(id+"F0.wireOp",EDGE,"E12.22.2"),sQuery(id+"F0.wireOp",EDGE,"E12.22.3"),sQuery(id+"F0.wireOp",EDGE,"E12.22.4"),sQuery(id+"F0.wireOp",EDGE,"E12.22.5"),sQuery(id+"F0.wireOp",EDGE,"E12.22.6"),sQuery(id+"F0.wireOp",EDGE,"E12.22.7"),sQuery(id+"F0.wireOp",EDGE,"E12.22.8"),sQuery(id+"F0.wireOp",EDGE,"E12.22.9"),sQuery(id+"F0.wireOp",EDGE,"E12.23.0"),sQuery(id+"F0.wireOp",EDGE,"E12.23.1"),sQuery(id+"F0.wireOp",EDGE,"E12.23.2"),sQuery(id+"F0.wireOp",EDGE,"E12.23.3"),sQuery(id+"F0.wireOp",EDGE,"E12.23.4"),sQuery(id+"F0.wireOp",EDGE,"E12.23.5"),sQuery(id+"F0.wireOp",EDGE,"E12.23.6"),sQuery(id+"F0.wireOp",EDGE,"E12.23.7"),sQuery(id+"F0.wireOp",EDGE,"E12.23.8"),sQuery(id+"F0.wireOp",EDGE,"E12.23.9"),sQuery(id+"F0.wireOp",EDGE,"E12.24.0"),sQuery(id+"F0.wireOp",EDGE,"E12.24.1"),sQuery(id+"F0.wireOp",EDGE,"E12.24.2"),sQuery(id+"F0.wireOp",EDGE,"E12.24.3"),sQuery(id+"F0.wireOp",EDGE,"E12.24.4"),sQuery(id+"F0.wireOp",EDGE,"E12.24.5"),sQuery(id+"F0.wireOp",EDGE,"E12.24.6"),sQuery(id+"F0.wireOp",EDGE,"E12.24.7"),sQuery(id+"F0.wireOp",EDGE,"E12.24.8"),sQuery(id+"F0.wireOp",EDGE,"E12.24.9"),sQuery(id+"F0.wireOp",EDGE,"E12.25.0"),sQuery(id+"F0.wireOp",EDGE,"E12.25.1"),sQuery(id+"F0.wireOp",EDGE,"E12.25.2"),sQuery(id+"F0.wireOp",EDGE,"E12.25.3"),sQuery(id+"F0.wireOp",EDGE,"E12.25.4"),sQuery(id+"F0.wireOp",EDGE,"E12.25.5"),sQuery(id+"F0.wireOp",EDGE,"E12.25.6"),sQuery(id+"F0.wireOp",EDGE,"E12.25.7"),sQuery(id+"F0.wireOp",EDGE,"E12.25.8"),sQuery(id+"F0.wireOp",EDGE,"E12.25.9"),sQuery(id+"F0.wireOp",EDGE,"E12.26.0"),sQuery(id+"F0.wireOp",EDGE,"E12.26.1"),sQuery(id+"F0.wireOp",EDGE,"E12.26.2"),sQuery(id+"F0.wireOp",EDGE,"E12.26.3"),sQuery(id+"F0.wireOp",EDGE,"E12.26.4"),sQuery(id+"F0.wireOp",EDGE,"E12.26.5"),sQuery(id+"F0.wireOp",EDGE,"E12.26.6"),sQuery(id+"F0.wireOp",EDGE,"E12.26.7"),sQuery(id+"F0.wireOp",EDGE,"E12.26.8"),sQuery(id+"F0.wireOp",EDGE,"E12.26.9"),sQuery(id+"F0.wireOp",EDGE,"E12.27.0"),sQuery(id+"F0.wireOp",EDGE,"E12.27.1"),sQuery(id+"F0.wireOp",EDGE,"E12.27.2"),sQuery(id+"F0.wireOp",EDGE,"E12.27.3"),sQuery(id+"F0.wireOp",EDGE,"E12.27.4"),sQuery(id+"F0.wireOp",EDGE,"E12.27.5"),sQuery(id+"F0.wireOp",EDGE,"E12.27.6"),sQuery(id+"F0.wireOp",EDGE,"E12.27.7"),sQuery(id+"F0.wireOp",EDGE,"E12.27.8"),sQuery(id+"F0.wireOp",EDGE,"E12.27.9"),sQuery(id+"F0.wireOp",EDGE,"E12.28.0"),sQuery(id+"F0.wireOp",EDGE,"E12.28.1"),sQuery(id+"F0.wireOp",EDGE,"E12.28.2"),sQuery(id+"F0.wireOp",EDGE,"E12.28.3"),sQuery(id+"F0.wireOp",EDGE,"E12.28.4"),sQuery(id+"F0.wireOp",EDGE,"E12.28.5"),sQuery(id+"F0.wireOp",EDGE,"E12.28.6"),sQuery(id+"F0.wireOp",EDGE,"E12.28.7"),sQuery(id+"F0.wireOp",EDGE,"E12.28.8"),sQuery(id+"F0.wireOp",EDGE,"E12.28.9"),sQuery(id+"F0.wireOp",EDGE,"E12.29.0"),sQuery(id+"F0.wireOp",EDGE,"E12.29.1"),sQuery(id+"F0.wireOp",EDGE,"E12.29.2"),sQuery(id+"F0.wireOp",EDGE,"E12.29.3"),sQuery(id+"F0.wireOp",EDGE,"E12.29.4"),sQuery(id+"F0.wireOp",EDGE,"E12.29.5"),sQuery(id+"F0.wireOp",EDGE,"E12.29.6"),sQuery(id+"F0.wireOp",EDGE,"E12.29.7"),sQuery(id+"F0.wireOp",EDGE,"E12.29.8"),sQuery(id+"F0.wireOp",EDGE,"E12.29.9"),sQuery(id+"F0.wireOp",EDGE,"E12.30.0"),sQuery(id+"F0.wireOp",EDGE,"E12.30.1"),sQuery(id+"F0.wireOp",EDGE,"E12.30.2"),sQuery(id+"F0.wireOp",EDGE,"E12.30.3"),sQuery(id+"F0.wireOp",EDGE,"E12.30.4"),sQuery(id+"F0.wireOp",EDGE,"E12.30.5"),sQuery(id+"F0.wireOp",EDGE,"E12.30.6"),sQuery(id+"F0.wireOp",EDGE,"E12.30.7"),sQuery(id+"F0.wireOp",EDGE,"E12.30.8"),sQuery(id+"F0.wireOp",EDGE,"E12.30.9"),sQuery(id+"F0.wireOp",EDGE,"E12.31.0"),sQuery(id+"F0.wireOp",EDGE,"E12.31.1"),sQuery(id+"F0.wireOp",EDGE,"E12.31.2"),sQuery(id+"F0.wireOp",EDGE,"E12.31.3"),sQuery(id+"F0.wireOp",EDGE,"E12.31.4"),sQuery(id+"F0.wireOp",EDGE,"E12.31.5"),sQuery(id+"F0.wireOp",EDGE,"E12.31.6"),sQuery(id+"F0.wireOp",EDGE,"E12.31.7"),sQuery(id+"F0.wireOp",EDGE,"E12.31.8"),sQuery(id+"F0.wireOp",EDGE,"E12.31.9"),sQuery(id+"F0.wireOp",EDGE,"E12.32.0"),sQuery(id+"F0.wireOp",EDGE,"E12.32.1"),sQuery(id+"F0.wireOp",EDGE,"E12.32.2"),sQuery(id+"F0.wireOp",EDGE,"E12.32.3"),sQuery(id+"F0.wireOp",EDGE,"E12.32.4"),sQuery(id+"F0.wireOp",EDGE,"E12.32.5"),sQuery(id+"F0.wireOp",EDGE,"E12.32.6"),sQuery(id+"F0.wireOp",EDGE,"E12.32.7"),sQuery(id+"F0.wireOp",EDGE,"E12.32.8"),sQuery(id+"F0.wireOp",EDGE,"E12.32.9"),sQuery(id+"F0.wireOp",EDGE,"E12.33.0"),sQuery(id+"F0.wireOp",EDGE,"E12.33.1"),sQuery(id+"F0.wireOp",EDGE,"E12.33.2"),sQuery(id+"F0.wireOp",EDGE,"E12.33.3"),sQuery(id+"F0.wireOp",EDGE,"E12.33.4"),sQuery(id+"F0.wireOp",EDGE,"E12.33.5"),sQuery(id+"F0.wireOp",EDGE,"E12.33.6"),sQuery(id+"F0.wireOp",EDGE,"E12.33.7"),sQuery(id+"F0.wireOp",EDGE,"E12.33.8"),sQuery(id+"F0.wireOp",EDGE,"E12.33.9"),sQuery(id+"F0.wireOp",EDGE,"E12.34.0"),sQuery(id+"F0.wireOp",EDGE,"E12.34.1"),sQuery(id+"F0.wireOp",EDGE,"E12.34.2"),sQuery(id+"F0.wireOp",EDGE,"E12.34.3"),sQuery(id+"F0.wireOp",EDGE,"E12.34.4"),sQuery(id+"F0.wireOp",EDGE,"E12.34.5"),sQuery(id+"F0.wireOp",EDGE,"E12.34.6"),sQuery(id+"F0.wireOp",EDGE,"E12.34.7"),sQuery(id+"F0.wireOp",EDGE,"E12.34.8"),sQuery(id+"F0.wireOp",EDGE,"E12.34.9"),sQuery(id+"F0.wireOp",EDGE,"E12.35.0"),sQuery(id+"F0.wireOp",EDGE,"E12.35.1"),sQuery(id+"F0.wireOp",EDGE,"E12.35.2"),sQuery(id+"F0.wireOp",EDGE,"E12.35.3"),sQuery(id+"F0.wireOp",EDGE,"E12.35.4"),sQuery(id+"F0.wireOp",EDGE,"E12.35.5"),sQuery(id+"F0.wireOp",EDGE,"E12.35.6"),sQuery(id+"F0.wireOp",EDGE,"E12.35.7"),sQuery(id+"F0.wireOp",EDGE,"E12.35.8"),sQuery(id+"F0.wireOp",EDGE,"E12.35.9"),sQuery(id+"F0.wireOp",EDGE,"E12.36.0"),sQuery(id+"F0.wireOp",EDGE,"E12.36.1"),sQuery(id+"F0.wireOp",EDGE,"E12.36.2"),sQuery(id+"F0.wireOp",EDGE,"E12.36.3"),sQuery(id+"F0.wireOp",EDGE,"E12.36.4"),sQuery(id+"F0.wireOp",EDGE,"E12.36.5"),sQuery(id+"F0.wireOp",EDGE,"E12.36.6"),sQuery(id+"F0.wireOp",EDGE,"E12.36.7"),sQuery(id+"F0.wireOp",EDGE,"E12.36.8"),sQuery(id+"F0.wireOp",EDGE,"E12.36.9"),sQuery(id+"F0.wireOp",EDGE,"E12.37.0"),sQuery(id+"F0.wireOp",EDGE,"E12.37.1"),sQuery(id+"F0.wireOp",EDGE,"E12.37.2"),sQuery(id+"F0.wireOp",EDGE,"E12.37.3"),sQuery(id+"F0.wireOp",EDGE,"E12.37.4"),sQuery(id+"F0.wireOp",EDGE,"E12.37.5"),sQuery(id+"F0.wireOp",EDGE,"E12.37.6"),sQuery(id+"F0.wireOp",EDGE,"E12.37.7"),sQuery(id+"F0.wireOp",EDGE,"E12.37.8"),sQuery(id+"F0.wireOp",EDGE,"E12.37.9"),sQuery(id+"F0.wireOp",EDGE,"E12.38.0"),sQuery(id+"F0.wireOp",EDGE,"E12.38.1"),sQuery(id+"F0.wireOp",EDGE,"E12.38.2"),sQuery(id+"F0.wireOp",EDGE,"E12.38.3"),sQuery(id+"F0.wireOp",EDGE,"E12.38.4"),sQuery(id+"F0.wireOp",EDGE,"E12.38.5"),sQuery(id+"F0.wireOp",EDGE,"E12.38.6"),sQuery(id+"F0.wireOp",EDGE,"E12.38.7"),sQuery(id+"F0.wireOp",EDGE,"E12.38.8"),sQuery(id+"F0.wireOp",EDGE,"E12.38.9"),sQuery(id+"F0.wireOp",EDGE,"E12.39.0"),sQuery(id+"F0.wireOp",EDGE,"E12.39.1"),sQuery(id+"F0.wireOp",EDGE,"E12.39.2"),sQuery(id+"F0.wireOp",EDGE,"E12.39.3"),sQuery(id+"F0.wireOp",EDGE,"E12.39.4"),sQuery(id+"F0.wireOp",EDGE,"E12.39.5"),sQuery(id+"F0.wireOp",EDGE,"E12.39.6"),sQuery(id+"F0.wireOp",EDGE,"E12.39.7"),sQuery(id+"F0.wireOp",EDGE,"E12.39.8"),sQuery(id+"F0.wireOp",EDGE,"E12.39.9"),sQuery(id+"F0.wireOp",EDGE,"E12.40.0"),sQuery(id+"F0.wireOp",EDGE,"E12.40.1"),sQuery(id+"F0.wireOp",EDGE,"E12.40.2"),sQuery(id+"F0.wireOp",EDGE,"E12.40.3"),sQuery(id+"F0.wireOp",EDGE,"E12.40.4"),sQuery(id+"F0.wireOp",EDGE,"E12.40.5"),sQuery(id+"F0.wireOp",EDGE,"E12.40.6"),sQuery(id+"F0.wireOp",EDGE,"E12.40.7"),sQuery(id+"F0.wireOp",EDGE,"E12.40.8"),sQuery(id+"F0.wireOp",EDGE,"E12.40.9"),sQuery(id+"F0.wireOp",EDGE,"E12.41.0"),sQuery(id+"F0.wireOp",EDGE,"E12.41.1"),sQuery(id+"F0.wireOp",EDGE,"E12.41.2"),sQuery(id+"F0.wireOp",EDGE,"E12.41.3"),sQuery(id+"F0.wireOp",EDGE,"E12.41.4"),sQuery(id+"F0.wireOp",EDGE,"E12.41.5"),sQuery(id+"F0.wireOp",EDGE,"E12.41.6"),sQuery(id+"F0.wireOp",EDGE,"E12.41.7"),sQuery(id+"F0.wireOp",EDGE,"E12.41.8"),sQuery(id+"F0.wireOp",EDGE,"E12.41.9"),sQuery(id+"F0.wireOp",EDGE,"E12.42.0"),sQuery(id+"F0.wireOp",EDGE,"E12.42.1"),sQuery(id+"F0.wireOp",EDGE,"E12.42.2"),sQuery(id+"F0.wireOp",EDGE,"E12.42.3"),sQuery(id+"F0.wireOp",EDGE,"E12.42.4"),sQuery(id+"F0.wireOp",EDGE,"E12.42.5"),sQuery(id+"F0.wireOp",EDGE,"E12.42.6"),sQuery(id+"F0.wireOp",EDGE,"E12.42.7"),sQuery(id+"F0.wireOp",EDGE,"E12.42.8"),sQuery(id+"F0.wireOp",EDGE,"E12.42.9"),sQuery(id+"F0.wireOp",EDGE,"E12.43.0"),sQuery(id+"F0.wireOp",EDGE,"E12.43.1"),sQuery(id+"F0.wireOp",EDGE,"E12.43.2"),sQuery(id+"F0.wireOp",EDGE,"E12.43.3"),sQuery(id+"F0.wireOp",EDGE,"E12.43.4"),sQuery(id+"F0.wireOp",EDGE,"E12.43.5"),sQuery(id+"F0.wireOp",EDGE,"E12.43.6"),sQuery(id+"F0.wireOp",EDGE,"E12.43.7"),sQuery(id+"F0.wireOp",EDGE,"E12.43.8"),sQuery(id+"F0.wireOp",EDGE,"E12.43.9"),sQuery(id+"F0.wireOp",EDGE,"E12.44.0"),sQuery(id+"F0.wireOp",EDGE,"E12.44.1"),sQuery(id+"F0.wireOp",EDGE,"E12.44.2"),sQuery(id+"F0.wireOp",EDGE,"E12.44.3"),sQuery(id+"F0.wireOp",EDGE,"E12.44.4"),sQuery(id+"F0.wireOp",EDGE,"E12.44.5"),sQuery(id+"F0.wireOp",EDGE,"E12.44.6"),sQuery(id+"F0.wireOp",EDGE,"E12.44.7"),sQuery(id+"F0.wireOp",EDGE,"E12.44.8"),sQuery(id+"F0.wireOp",EDGE,"E12.44.9"),sQuery(id+"F0.wireOp",EDGE,"E12.45.0"),sQuery(id+"F0.wireOp",EDGE,"E12.45.1"),sQuery(id+"F0.wireOp",EDGE,"E12.45.2"),sQuery(id+"F0.wireOp",EDGE,"E12.45.3"),sQuery(id+"F0.wireOp",EDGE,"E12.45.4"),sQuery(id+"F0.wireOp",EDGE,"E12.45.5"),sQuery(id+"F0.wireOp",EDGE,"E12.45.6"),sQuery(id+"F0.wireOp",EDGE,"E12.45.7"),sQuery(id+"F0.wireOp",EDGE,"E12.45.8"),sQuery(id+"F0.wireOp",EDGE,"E12.45.9"),sQuery(id+"F0.wireOp",EDGE,"E12.46.0"),sQuery(id+"F0.wireOp",EDGE,"E12.46.1"),sQuery(id+"F0.wireOp",EDGE,"E12.46.2"),sQuery(id+"F0.wireOp",EDGE,"E12.46.3"),sQuery(id+"F0.wireOp",EDGE,"E12.46.4"),sQuery(id+"F0.wireOp",EDGE,"E12.46.5"),sQuery(id+"F0.wireOp",EDGE,"E12.46.6"),sQuery(id+"F0.wireOp",EDGE,"E12.46.7"),sQuery(id+"F0.wireOp",EDGE,"E12.46.8"),sQuery(id+"F0.wireOp",EDGE,"E12.46.9"),sQuery(id+"F0.wireOp",EDGE,"E12.47.0"),sQuery(id+"F0.wireOp",EDGE,"E12.47.1"),sQuery(id+"F0.wireOp",EDGE,"E12.47.2"),sQuery(id+"F0.wireOp",EDGE,"E12.47.3"),sQuery(id+"F0.wireOp",EDGE,"E12.47.4"),sQuery(id+"F0.wireOp",EDGE,"E12.47.5"),sQuery(id+"F0.wireOp",EDGE,"E12.47.6"),sQuery(id+"F0.wireOp",EDGE,"E12.47.7"),sQuery(id+"F0.wireOp",EDGE,"E12.47.8"),sQuery(id+"F0.wireOp",EDGE,"E12.47.9"),sQuery(id+"F0.wireOp",EDGE,"E12.48.0"),sQuery(id+"F0.wireOp",EDGE,"E12.48.1"),sQuery(id+"F0.wireOp",EDGE,"E12.48.2"),sQuery(id+"F0.wireOp",EDGE,"E12.48.3"),sQuery(id+"F0.wireOp",EDGE,"E12.48.4"),sQuery(id+"F0.wireOp",EDGE,"E12.48.5"),sQuery(id+"F0.wireOp",EDGE,"E12.48.6"),sQuery(id+"F0.wireOp",EDGE,"E12.48.7"),sQuery(id+"F0.wireOp",EDGE,"E12.48.8"),sQuery(id+"F0.wireOp",EDGE,"E12.48.9"),sQuery(id+"F0.wireOp",EDGE,"E12.49.0"),sQuery(id+"F0.wireOp",EDGE,"E12.49.1"),sQuery(id+"F0.wireOp",EDGE,"E12.49.2"),sQuery(id+"F0.wireOp",EDGE,"E12.49.3"),sQuery(id+"F0.wireOp",EDGE,"E12.49.4"),sQuery(id+"F0.wireOp",EDGE,"E12.49.5"),sQuery(id+"F0.wireOp",EDGE,"E12.49.6"),sQuery(id+"F0.wireOp",EDGE,"E12.49.7"),sQuery(id+"F0.wireOp",EDGE,"E12.49.8"),sQuery(id+"F0.wireOp",EDGE,"E12.49.9"),sQuery(id+"F0.wireOp",EDGE,"E12.50.0"),sQuery(id+"F0.wireOp",EDGE,"E12.50.1"),sQuery(id+"F0.wireOp",EDGE,"E12.50.2"),sQuery(id+"F0.wireOp",EDGE,"E12.50.3"),sQuery(id+"F0.wireOp",EDGE,"E12.50.4"),sQuery(id+"F0.wireOp",EDGE,"E12.50.5"),sQuery(id+"F0.wireOp",EDGE,"E12.50.6"),sQuery(id+"F0.wireOp",EDGE,"E12.50.7"),sQuery(id+"F0.wireOp",EDGE,"E12.50.8"),sQuery(id+"F0.wireOp",EDGE,"E12.50.9"),sQuery(id+"F0.wireOp",EDGE,"E12.51.0"),sQuery(id+"F0.wireOp",EDGE,"E12.51.1"),sQuery(id+"F0.wireOp",EDGE,"E12.51.2"),sQuery(id+"F0.wireOp",EDGE,"E12.51.3"),sQuery(id+"F0.wireOp",EDGE,"E12.51.4"),sQuery(id+"F0.wireOp",EDGE,"E12.51.5"),sQuery(id+"F0.wireOp",EDGE,"E12.51.6"),sQuery(id+"F0.wireOp",EDGE,"E12.51.7"),sQuery(id+"F0.wireOp",EDGE,"E12.51.8"),sQuery(id+"F0.wireOp",EDGE,"E12.51.9"),sQuery(id+"F0.wireOp",EDGE,"E12.52.0"),sQuery(id+"F0.wireOp",EDGE,"E12.52.1"),sQuery(id+"F0.wireOp",EDGE,"E12.52.2"),sQuery(id+"F0.wireOp",EDGE,"E12.52.3"),sQuery(id+"F0.wireOp",EDGE,"E12.52.4"),sQuery(id+"F0.wireOp",EDGE,"E12.52.5"),sQuery(id+"F0.wireOp",EDGE,"E12.52.6"),sQuery(id+"F0.wireOp",EDGE,"E12.52.7"),sQuery(id+"F0.wireOp",EDGE,"E12.52.8"),sQuery(id+"F0.wireOp",EDGE,"E12.52.9"),sQuery(id+"F0.wireOp",EDGE,"E12.53.0"),sQuery(id+"F0.wireOp",EDGE,"E12.53.1"),sQuery(id+"F0.wireOp",EDGE,"E12.53.2"),sQuery(id+"F0.wireOp",EDGE,"E12.53.3"),sQuery(id+"F0.wireOp",EDGE,"E12.53.4"),sQuery(id+"F0.wireOp",EDGE,"E12.53.5"),sQuery(id+"F0.wireOp",EDGE,"E12.53.6"),sQuery(id+"F0.wireOp",EDGE,"E12.53.7"),sQuery(id+"F0.wireOp",EDGE,"E12.53.8"),sQuery(id+"F0.wireOp",EDGE,"E12.53.9"),sQuery(id+"F0.wireOp",EDGE,"E12.54.0"),sQuery(id+"F0.wireOp",EDGE,"E12.54.1"),sQuery(id+"F0.wireOp",EDGE,"E12.54.2"),sQuery(id+"F0.wireOp",EDGE,"E12.54.3"),sQuery(id+"F0.wireOp",EDGE,"E12.54.4"),sQuery(id+"F0.wireOp",EDGE,"E12.54.5"),sQuery(id+"F0.wireOp",EDGE,"E12.54.6"),sQuery(id+"F0.wireOp",EDGE,"E12.54.7"),sQuery(id+"F0.wireOp",EDGE,"E12.54.8"),sQuery(id+"F0.wireOp",EDGE,"E12.54.9"),sQuery(id+"F0.wireOp",EDGE,"E12.55.0"),sQuery(id+"F0.wireOp",EDGE,"E12.55.1"),sQuery(id+"F0.wireOp",EDGE,"E12.55.2"),sQuery(id+"F0.wireOp",EDGE,"E12.55.3"),sQuery(id+"F0.wireOp",EDGE,"E12.55.4"),sQuery(id+"F0.wireOp",EDGE,"E12.55.5"),sQuery(id+"F0.wireOp",EDGE,"E12.55.6"),sQuery(id+"F0.wireOp",EDGE,"E12.55.7"),sQuery(id+"F0.wireOp",EDGE,"E12.55.8"),sQuery(id+"F0.wireOp",EDGE,"E12.55.9"),sQuery(id+"F0.wireOp",EDGE,"E12.56.0"),sQuery(id+"F0.wireOp",EDGE,"E12.56.1"),sQuery(id+"F0.wireOp",EDGE,"E12.56.2"),sQuery(id+"F0.wireOp",EDGE,"E12.56.3"),sQuery(id+"F0.wireOp",EDGE,"E12.56.4"),sQuery(id+"F0.wireOp",EDGE,"E12.56.5"),sQuery(id+"F0.wireOp",EDGE,"E12.56.6"),sQuery(id+"F0.wireOp",EDGE,"E12.56.7"),sQuery(id+"F0.wireOp",EDGE,"E12.56.8"),sQuery(id+"F0.wireOp",EDGE,"E12.56.9"),sQuery(id+"F0.wireOp",EDGE,"E12.57.0"),sQuery(id+"F0.wireOp",EDGE,"E12.57.1"),sQuery(id+"F0.wireOp",EDGE,"E12.57.2"),sQuery(id+"F0.wireOp",EDGE,"E12.57.3"),sQuery(id+"F0.wireOp",EDGE,"E12.57.4"),sQuery(id+"F0.wireOp",EDGE,"E12.57.5"),sQuery(id+"F0.wireOp",EDGE,"E12.57.6"),sQuery(id+"F0.wireOp",EDGE,"E12.57.7"),sQuery(id+"F0.wireOp",EDGE,"E12.57.8"),sQuery(id+"F0.wireOp",EDGE,"E12.57.9"),sQuery(id+"F0.wireOp",EDGE,"E12.58.0"),sQuery(id+"F0.wireOp",EDGE,"E12.58.1"),sQuery(id+"F0.wireOp",EDGE,"E12.58.2"),sQuery(id+"F0.wireOp",EDGE,"E12.58.3"),sQuery(id+"F0.wireOp",EDGE,"E12.58.4"),sQuery(id+"F0.wireOp",EDGE,"E12.58.5"),sQuery(id+"F0.wireOp",EDGE,"E12.58.6"),sQuery(id+"F0.wireOp",EDGE,"E12.58.7"),sQuery(id+"F0.wireOp",EDGE,"E12.58.8"),sQuery(id+"F0.wireOp",EDGE,"E12.58.9"),sQuery(id+"F0.wireOp",EDGE,"E12.59.0"),sQuery(id+"F0.wireOp",EDGE,"E12.59.1"),sQuery(id+"F0.wireOp",EDGE,"E12.59.2"),sQuery(id+"F0.wireOp",EDGE,"E12.59.3"),sQuery(id+"F0.wireOp",EDGE,"E12.59.4"),sQuery(id+"F0.wireOp",EDGE,"E12.59.5"),sQuery(id+"F0.wireOp",EDGE,"E12.59.6"),sQuery(id+"F0.wireOp",EDGE,"E12.59.7"),sQuery(id+"F0.wireOp",EDGE,"E12.59.8"),sQuery(id+"F0.wireOp",EDGE,"E12.59.9"),sQuery(id+"F0.wireOp",EDGE,"E13.trimOffspring"),sQuery(id+"F0.wireOp",EDGE,"E14.trimOffspring")])],"isStart":false});
            var sketch = newSketch(context, id + "F2", { "sketchPlane" : qUnion([Q0])});
            skCircle(sketch, "E15", {"center": v(0, 26.67) * mm, "radius": 5.08 * mm});
            skCircle(sketch, "E16", {"center": v(0, 16.51) * mm, "radius": 2.1 * mm});
            skCircle(sketch, "E17.1.0", {"center": v(-18.86, 18.86) * mm, "radius": 5.08 * mm});
            skCircle(sketch, "E17.2.0", {"center": v(-26.67, 0) * mm, "radius": 5.08 * mm});
            skCircle(sketch, "E17.3.0", {"center": v(-18.86, -18.86) * mm, "radius": 5.08 * mm});
            skCircle(sketch, "E17.4.0", {"center": v(0, -26.67) * mm, "radius": 5.08 * mm});
            skCircle(sketch, "E17.5.0", {"center": v(18.86, -18.86) * mm, "radius": 5.08 * mm});
            skCircle(sketch, "E17.6.0", {"center": v(26.67, 0) * mm, "radius": 5.08 * mm});
            skCircle(sketch, "E17.7.0", {"center": v(18.86, 18.86) * mm, "radius": 5.08 * mm});
            skPoint(sketch, "E17.center", {"position": v(0, 0) * mm});
            skCircle(sketch, "E18.1.0", {"center": v(-8.26, 14.3) * mm, "radius": 2.1 * mm});
            skCircle(sketch, "E18.2.0", {"center": v(-14.3, 8.26) * mm, "radius": 2.1 * mm});
            skCircle(sketch, "E18.3.0", {"center": v(-16.51, 0) * mm, "radius": 2.1 * mm});
            skCircle(sketch, "E18.4.0", {"center": v(-14.3, -8.25) * mm, "radius": 2.1 * mm});
            skCircle(sketch, "E18.5.0", {"center": v(-8.26, -14.3) * mm, "radius": 2.1 * mm});
            skCircle(sketch, "E18.6.0", {"center": v(0, -16.51) * mm, "radius": 2.1 * mm});
            skCircle(sketch, "E18.7.0", {"center": v(8.25, -14.3) * mm, "radius": 2.1 * mm});
            skCircle(sketch, "E18.8.0", {"center": v(14.3, -8.26) * mm, "radius": 2.1 * mm});
            skCircle(sketch, "E18.9.0", {"center": v(16.51, 0) * mm, "radius": 2.1 * mm});
            skCircle(sketch, "E18.10.0", {"center": v(14.3, 8.25) * mm, "radius": 2.1 * mm});
            skCircle(sketch, "E18.11.0", {"center": v(8.26, 14.3) * mm, "radius": 2.1 * mm});
            skSolve(sketch);
        }
        {
            var Q0;
            Q0 = qSketchRegion(id + "F2", true);
            extrude(context, id + "F3", {"entities" : qUnion([Q0]), "operationType" : NewBodyOperationType.REMOVE, "endBound" : BoundingType.THROUGH_ALL, "oppositeDirection" : true, "depth" : 25.4 * mm});
        }
        {
            var Q0;
            Q0=makeQuery(id+"F1.opExtrude","CAP_FACE",FACE,{"disambiguationData":[OSD([sQuery(id+"F0.wireOp",EDGE,"E0"),sQuery(id+"F0.wireOp",EDGE,"E2"),sQuery(id+"F0.wireOp",EDGE,"E3"),sQuery(id+"F0.wireOp",EDGE,"E4.trimOffspring"),sQuery(id+"F0.wireOp",EDGE,"E5.MirrorCS"),sQuery(id+"F0.wireOp",EDGE,"E6.MirrorCS"),sQuery(id+"F0.wireOp",EDGE,"E7.MirrorCS"),sQuery(id+"F0.wireOp",EDGE,"E8.filletArc"),sQuery(id+"F0.wireOp",EDGE,"E9.filletArc"),sQuery(id+"F0.wireOp",EDGE,"E10.filletArc"),sQuery(id+"F0.wireOp",EDGE,"E11.filletArc"),sQuery(id+"F0.wireOp",EDGE,"E12.1.0"),sQuery(id+"F0.wireOp",EDGE,"E12.1.1"),sQuery(id+"F0.wireOp",EDGE,"E12.1.2"),sQuery(id+"F0.wireOp",EDGE,"E12.1.3"),sQuery(id+"F0.wireOp",EDGE,"E12.1.4"),sQuery(id+"F0.wireOp",EDGE,"E12.1.5"),sQuery(id+"F0.wireOp",EDGE,"E12.1.6"),sQuery(id+"F0.wireOp",EDGE,"E12.1.7"),sQuery(id+"F0.wireOp",EDGE,"E12.1.8"),sQuery(id+"F0.wireOp",EDGE,"E12.1.9"),sQuery(id+"F0.wireOp",EDGE,"E12.2.0"),sQuery(id+"F0.wireOp",EDGE,"E12.2.1"),sQuery(id+"F0.wireOp",EDGE,"E12.2.2"),sQuery(id+"F0.wireOp",EDGE,"E12.2.3"),sQuery(id+"F0.wireOp",EDGE,"E12.2.4"),sQuery(id+"F0.wireOp",EDGE,"E12.2.5"),sQuery(id+"F0.wireOp",EDGE,"E12.2.6"),sQuery(id+"F0.wireOp",EDGE,"E12.2.7"),sQuery(id+"F0.wireOp",EDGE,"E12.2.8"),sQuery(id+"F0.wireOp",EDGE,"E12.2.9"),sQuery(id+"F0.wireOp",EDGE,"E12.3.0"),sQuery(id+"F0.wireOp",EDGE,"E12.3.1"),sQuery(id+"F0.wireOp",EDGE,"E12.3.2"),sQuery(id+"F0.wireOp",EDGE,"E12.3.3"),sQuery(id+"F0.wireOp",EDGE,"E12.3.4"),sQuery(id+"F0.wireOp",EDGE,"E12.3.5"),sQuery(id+"F0.wireOp",EDGE,"E12.3.6"),sQuery(id+"F0.wireOp",EDGE,"E12.3.7"),sQuery(id+"F0.wireOp",EDGE,"E12.3.8"),sQuery(id+"F0.wireOp",EDGE,"E12.3.9"),sQuery(id+"F0.wireOp",EDGE,"E12.4.0"),sQuery(id+"F0.wireOp",EDGE,"E12.4.1"),sQuery(id+"F0.wireOp",EDGE,"E12.4.2"),sQuery(id+"F0.wireOp",EDGE,"E12.4.3"),sQuery(id+"F0.wireOp",EDGE,"E12.4.4"),sQuery(id+"F0.wireOp",EDGE,"E12.4.5"),sQuery(id+"F0.wireOp",EDGE,"E12.4.6"),sQuery(id+"F0.wireOp",EDGE,"E12.4.7"),sQuery(id+"F0.wireOp",EDGE,"E12.4.8"),sQuery(id+"F0.wireOp",EDGE,"E12.4.9"),sQuery(id+"F0.wireOp",EDGE,"E12.5.0"),sQuery(id+"F0.wireOp",EDGE,"E12.5.1"),sQuery(id+"F0.wireOp",EDGE,"E12.5.2"),sQuery(id+"F0.wireOp",EDGE,"E12.5.3"),sQuery(id+"F0.wireOp",EDGE,"E12.5.4"),sQuery(id+"F0.wireOp",EDGE,"E12.5.5"),sQuery(id+"F0.wireOp",EDGE,"E12.5.6"),sQuery(id+"F0.wireOp",EDGE,"E12.5.7"),sQuery(id+"F0.wireOp",EDGE,"E12.5.8"),sQuery(id+"F0.wireOp",EDGE,"E12.5.9"),sQuery(id+"F0.wireOp",EDGE,"E12.6.0"),sQuery(id+"F0.wireOp",EDGE,"E12.6.1"),sQuery(id+"F0.wireOp",EDGE,"E12.6.2"),sQuery(id+"F0.wireOp",EDGE,"E12.6.3"),sQuery(id+"F0.wireOp",EDGE,"E12.6.4"),sQuery(id+"F0.wireOp",EDGE,"E12.6.5"),sQuery(id+"F0.wireOp",EDGE,"E12.6.6"),sQuery(id+"F0.wireOp",EDGE,"E12.6.7"),sQuery(id+"F0.wireOp",EDGE,"E12.6.8"),sQuery(id+"F0.wireOp",EDGE,"E12.6.9"),sQuery(id+"F0.wireOp",EDGE,"E12.7.0"),sQuery(id+"F0.wireOp",EDGE,"E12.7.1"),sQuery(id+"F0.wireOp",EDGE,"E12.7.2"),sQuery(id+"F0.wireOp",EDGE,"E12.7.3"),sQuery(id+"F0.wireOp",EDGE,"E12.7.4"),sQuery(id+"F0.wireOp",EDGE,"E12.7.5"),sQuery(id+"F0.wireOp",EDGE,"E12.7.6"),sQuery(id+"F0.wireOp",EDGE,"E12.7.7"),sQuery(id+"F0.wireOp",EDGE,"E12.7.8"),sQuery(id+"F0.wireOp",EDGE,"E12.7.9"),sQuery(id+"F0.wireOp",EDGE,"E12.8.0"),sQuery(id+"F0.wireOp",EDGE,"E12.8.1"),sQuery(id+"F0.wireOp",EDGE,"E12.8.2"),sQuery(id+"F0.wireOp",EDGE,"E12.8.3"),sQuery(id+"F0.wireOp",EDGE,"E12.8.4"),sQuery(id+"F0.wireOp",EDGE,"E12.8.5"),sQuery(id+"F0.wireOp",EDGE,"E12.8.6"),sQuery(id+"F0.wireOp",EDGE,"E12.8.7"),sQuery(id+"F0.wireOp",EDGE,"E12.8.8"),sQuery(id+"F0.wireOp",EDGE,"E12.8.9"),sQuery(id+"F0.wireOp",EDGE,"E12.9.0"),sQuery(id+"F0.wireOp",EDGE,"E12.9.1"),sQuery(id+"F0.wireOp",EDGE,"E12.9.2"),sQuery(id+"F0.wireOp",EDGE,"E12.9.3"),sQuery(id+"F0.wireOp",EDGE,"E12.9.4"),sQuery(id+"F0.wireOp",EDGE,"E12.9.5"),sQuery(id+"F0.wireOp",EDGE,"E12.9.6"),sQuery(id+"F0.wireOp",EDGE,"E12.9.7"),sQuery(id+"F0.wireOp",EDGE,"E12.9.8"),sQuery(id+"F0.wireOp",EDGE,"E12.9.9"),sQuery(id+"F0.wireOp",EDGE,"E12.10.0"),sQuery(id+"F0.wireOp",EDGE,"E12.10.1"),sQuery(id+"F0.wireOp",EDGE,"E12.10.2"),sQuery(id+"F0.wireOp",EDGE,"E12.10.3"),sQuery(id+"F0.wireOp",EDGE,"E12.10.4"),sQuery(id+"F0.wireOp",EDGE,"E12.10.5"),sQuery(id+"F0.wireOp",EDGE,"E12.10.6"),sQuery(id+"F0.wireOp",EDGE,"E12.10.7"),sQuery(id+"F0.wireOp",EDGE,"E12.10.8"),sQuery(id+"F0.wireOp",EDGE,"E12.10.9"),sQuery(id+"F0.wireOp",EDGE,"E12.11.0"),sQuery(id+"F0.wireOp",EDGE,"E12.11.1"),sQuery(id+"F0.wireOp",EDGE,"E12.11.2"),sQuery(id+"F0.wireOp",EDGE,"E12.11.3"),sQuery(id+"F0.wireOp",EDGE,"E12.11.4"),sQuery(id+"F0.wireOp",EDGE,"E12.11.5"),sQuery(id+"F0.wireOp",EDGE,"E12.11.6"),sQuery(id+"F0.wireOp",EDGE,"E12.11.7"),sQuery(id+"F0.wireOp",EDGE,"E12.11.8"),sQuery(id+"F0.wireOp",EDGE,"E12.11.9"),sQuery(id+"F0.wireOp",EDGE,"E12.12.0"),sQuery(id+"F0.wireOp",EDGE,"E12.12.1"),sQuery(id+"F0.wireOp",EDGE,"E12.12.2"),sQuery(id+"F0.wireOp",EDGE,"E12.12.3"),sQuery(id+"F0.wireOp",EDGE,"E12.12.4"),sQuery(id+"F0.wireOp",EDGE,"E12.12.5"),sQuery(id+"F0.wireOp",EDGE,"E12.12.6"),sQuery(id+"F0.wireOp",EDGE,"E12.12.7"),sQuery(id+"F0.wireOp",EDGE,"E12.12.8"),sQuery(id+"F0.wireOp",EDGE,"E12.12.9"),sQuery(id+"F0.wireOp",EDGE,"E12.13.0"),sQuery(id+"F0.wireOp",EDGE,"E12.13.1"),sQuery(id+"F0.wireOp",EDGE,"E12.13.2"),sQuery(id+"F0.wireOp",EDGE,"E12.13.3"),sQuery(id+"F0.wireOp",EDGE,"E12.13.4"),sQuery(id+"F0.wireOp",EDGE,"E12.13.5"),sQuery(id+"F0.wireOp",EDGE,"E12.13.6"),sQuery(id+"F0.wireOp",EDGE,"E12.13.7"),sQuery(id+"F0.wireOp",EDGE,"E12.13.8"),sQuery(id+"F0.wireOp",EDGE,"E12.13.9"),sQuery(id+"F0.wireOp",EDGE,"E12.14.0"),sQuery(id+"F0.wireOp",EDGE,"E12.14.1"),sQuery(id+"F0.wireOp",EDGE,"E12.14.2"),sQuery(id+"F0.wireOp",EDGE,"E12.14.3"),sQuery(id+"F0.wireOp",EDGE,"E12.14.4"),sQuery(id+"F0.wireOp",EDGE,"E12.14.5"),sQuery(id+"F0.wireOp",EDGE,"E12.14.6"),sQuery(id+"F0.wireOp",EDGE,"E12.14.7"),sQuery(id+"F0.wireOp",EDGE,"E12.14.8"),sQuery(id+"F0.wireOp",EDGE,"E12.14.9"),sQuery(id+"F0.wireOp",EDGE,"E12.15.0"),sQuery(id+"F0.wireOp",EDGE,"E12.15.1"),sQuery(id+"F0.wireOp",EDGE,"E12.15.2"),sQuery(id+"F0.wireOp",EDGE,"E12.15.3"),sQuery(id+"F0.wireOp",EDGE,"E12.15.4"),sQuery(id+"F0.wireOp",EDGE,"E12.15.5"),sQuery(id+"F0.wireOp",EDGE,"E12.15.6"),sQuery(id+"F0.wireOp",EDGE,"E12.15.7"),sQuery(id+"F0.wireOp",EDGE,"E12.15.8"),sQuery(id+"F0.wireOp",EDGE,"E12.15.9"),sQuery(id+"F0.wireOp",EDGE,"E12.16.0"),sQuery(id+"F0.wireOp",EDGE,"E12.16.1"),sQuery(id+"F0.wireOp",EDGE,"E12.16.2"),sQuery(id+"F0.wireOp",EDGE,"E12.16.3"),sQuery(id+"F0.wireOp",EDGE,"E12.16.4"),sQuery(id+"F0.wireOp",EDGE,"E12.16.5"),sQuery(id+"F0.wireOp",EDGE,"E12.16.6"),sQuery(id+"F0.wireOp",EDGE,"E12.16.7"),sQuery(id+"F0.wireOp",EDGE,"E12.16.8"),sQuery(id+"F0.wireOp",EDGE,"E12.16.9"),sQuery(id+"F0.wireOp",EDGE,"E12.17.0"),sQuery(id+"F0.wireOp",EDGE,"E12.17.1"),sQuery(id+"F0.wireOp",EDGE,"E12.17.2"),sQuery(id+"F0.wireOp",EDGE,"E12.17.3"),sQuery(id+"F0.wireOp",EDGE,"E12.17.4"),sQuery(id+"F0.wireOp",EDGE,"E12.17.5"),sQuery(id+"F0.wireOp",EDGE,"E12.17.6"),sQuery(id+"F0.wireOp",EDGE,"E12.17.7"),sQuery(id+"F0.wireOp",EDGE,"E12.17.8"),sQuery(id+"F0.wireOp",EDGE,"E12.17.9"),sQuery(id+"F0.wireOp",EDGE,"E12.18.0"),sQuery(id+"F0.wireOp",EDGE,"E12.18.1"),sQuery(id+"F0.wireOp",EDGE,"E12.18.2"),sQuery(id+"F0.wireOp",EDGE,"E12.18.3"),sQuery(id+"F0.wireOp",EDGE,"E12.18.4"),sQuery(id+"F0.wireOp",EDGE,"E12.18.5"),sQuery(id+"F0.wireOp",EDGE,"E12.18.6"),sQuery(id+"F0.wireOp",EDGE,"E12.18.7"),sQuery(id+"F0.wireOp",EDGE,"E12.18.8"),sQuery(id+"F0.wireOp",EDGE,"E12.18.9"),sQuery(id+"F0.wireOp",EDGE,"E12.19.0"),sQuery(id+"F0.wireOp",EDGE,"E12.19.1"),sQuery(id+"F0.wireOp",EDGE,"E12.19.2"),sQuery(id+"F0.wireOp",EDGE,"E12.19.3"),sQuery(id+"F0.wireOp",EDGE,"E12.19.4"),sQuery(id+"F0.wireOp",EDGE,"E12.19.5"),sQuery(id+"F0.wireOp",EDGE,"E12.19.6"),sQuery(id+"F0.wireOp",EDGE,"E12.19.7"),sQuery(id+"F0.wireOp",EDGE,"E12.19.8"),sQuery(id+"F0.wireOp",EDGE,"E12.19.9"),sQuery(id+"F0.wireOp",EDGE,"E12.20.0"),sQuery(id+"F0.wireOp",EDGE,"E12.20.1"),sQuery(id+"F0.wireOp",EDGE,"E12.20.2"),sQuery(id+"F0.wireOp",EDGE,"E12.20.3"),sQuery(id+"F0.wireOp",EDGE,"E12.20.4"),sQuery(id+"F0.wireOp",EDGE,"E12.20.5"),sQuery(id+"F0.wireOp",EDGE,"E12.20.6"),sQuery(id+"F0.wireOp",EDGE,"E12.20.7"),sQuery(id+"F0.wireOp",EDGE,"E12.20.8"),sQuery(id+"F0.wireOp",EDGE,"E12.20.9"),sQuery(id+"F0.wireOp",EDGE,"E12.21.0"),sQuery(id+"F0.wireOp",EDGE,"E12.21.1"),sQuery(id+"F0.wireOp",EDGE,"E12.21.2"),sQuery(id+"F0.wireOp",EDGE,"E12.21.3"),sQuery(id+"F0.wireOp",EDGE,"E12.21.4"),sQuery(id+"F0.wireOp",EDGE,"E12.21.5"),sQuery(id+"F0.wireOp",EDGE,"E12.21.6"),sQuery(id+"F0.wireOp",EDGE,"E12.21.7"),sQuery(id+"F0.wireOp",EDGE,"E12.21.8"),sQuery(id+"F0.wireOp",EDGE,"E12.21.9"),sQuery(id+"F0.wireOp",EDGE,"E12.22.0"),sQuery(id+"F0.wireOp",EDGE,"E12.22.1"),sQuery(id+"F0.wireOp",EDGE,"E12.22.2"),sQuery(id+"F0.wireOp",EDGE,"E12.22.3"),sQuery(id+"F0.wireOp",EDGE,"E12.22.4"),sQuery(id+"F0.wireOp",EDGE,"E12.22.5"),sQuery(id+"F0.wireOp",EDGE,"E12.22.6"),sQuery(id+"F0.wireOp",EDGE,"E12.22.7"),sQuery(id+"F0.wireOp",EDGE,"E12.22.8"),sQuery(id+"F0.wireOp",EDGE,"E12.22.9"),sQuery(id+"F0.wireOp",EDGE,"E12.23.0"),sQuery(id+"F0.wireOp",EDGE,"E12.23.1"),sQuery(id+"F0.wireOp",EDGE,"E12.23.2"),sQuery(id+"F0.wireOp",EDGE,"E12.23.3"),sQuery(id+"F0.wireOp",EDGE,"E12.23.4"),sQuery(id+"F0.wireOp",EDGE,"E12.23.5"),sQuery(id+"F0.wireOp",EDGE,"E12.23.6"),sQuery(id+"F0.wireOp",EDGE,"E12.23.7"),sQuery(id+"F0.wireOp",EDGE,"E12.23.8"),sQuery(id+"F0.wireOp",EDGE,"E12.23.9"),sQuery(id+"F0.wireOp",EDGE,"E12.24.0"),sQuery(id+"F0.wireOp",EDGE,"E12.24.1"),sQuery(id+"F0.wireOp",EDGE,"E12.24.2"),sQuery(id+"F0.wireOp",EDGE,"E12.24.3"),sQuery(id+"F0.wireOp",EDGE,"E12.24.4"),sQuery(id+"F0.wireOp",EDGE,"E12.24.5"),sQuery(id+"F0.wireOp",EDGE,"E12.24.6"),sQuery(id+"F0.wireOp",EDGE,"E12.24.7"),sQuery(id+"F0.wireOp",EDGE,"E12.24.8"),sQuery(id+"F0.wireOp",EDGE,"E12.24.9"),sQuery(id+"F0.wireOp",EDGE,"E12.25.0"),sQuery(id+"F0.wireOp",EDGE,"E12.25.1"),sQuery(id+"F0.wireOp",EDGE,"E12.25.2"),sQuery(id+"F0.wireOp",EDGE,"E12.25.3"),sQuery(id+"F0.wireOp",EDGE,"E12.25.4"),sQuery(id+"F0.wireOp",EDGE,"E12.25.5"),sQuery(id+"F0.wireOp",EDGE,"E12.25.6"),sQuery(id+"F0.wireOp",EDGE,"E12.25.7"),sQuery(id+"F0.wireOp",EDGE,"E12.25.8"),sQuery(id+"F0.wireOp",EDGE,"E12.25.9"),sQuery(id+"F0.wireOp",EDGE,"E12.26.0"),sQuery(id+"F0.wireOp",EDGE,"E12.26.1"),sQuery(id+"F0.wireOp",EDGE,"E12.26.2"),sQuery(id+"F0.wireOp",EDGE,"E12.26.3"),sQuery(id+"F0.wireOp",EDGE,"E12.26.4"),sQuery(id+"F0.wireOp",EDGE,"E12.26.5"),sQuery(id+"F0.wireOp",EDGE,"E12.26.6"),sQuery(id+"F0.wireOp",EDGE,"E12.26.7"),sQuery(id+"F0.wireOp",EDGE,"E12.26.8"),sQuery(id+"F0.wireOp",EDGE,"E12.26.9"),sQuery(id+"F0.wireOp",EDGE,"E12.27.0"),sQuery(id+"F0.wireOp",EDGE,"E12.27.1"),sQuery(id+"F0.wireOp",EDGE,"E12.27.2"),sQuery(id+"F0.wireOp",EDGE,"E12.27.3"),sQuery(id+"F0.wireOp",EDGE,"E12.27.4"),sQuery(id+"F0.wireOp",EDGE,"E12.27.5"),sQuery(id+"F0.wireOp",EDGE,"E12.27.6"),sQuery(id+"F0.wireOp",EDGE,"E12.27.7"),sQuery(id+"F0.wireOp",EDGE,"E12.27.8"),sQuery(id+"F0.wireOp",EDGE,"E12.27.9"),sQuery(id+"F0.wireOp",EDGE,"E12.28.0"),sQuery(id+"F0.wireOp",EDGE,"E12.28.1"),sQuery(id+"F0.wireOp",EDGE,"E12.28.2"),sQuery(id+"F0.wireOp",EDGE,"E12.28.3"),sQuery(id+"F0.wireOp",EDGE,"E12.28.4"),sQuery(id+"F0.wireOp",EDGE,"E12.28.5"),sQuery(id+"F0.wireOp",EDGE,"E12.28.6"),sQuery(id+"F0.wireOp",EDGE,"E12.28.7"),sQuery(id+"F0.wireOp",EDGE,"E12.28.8"),sQuery(id+"F0.wireOp",EDGE,"E12.28.9"),sQuery(id+"F0.wireOp",EDGE,"E12.29.0"),sQuery(id+"F0.wireOp",EDGE,"E12.29.1"),sQuery(id+"F0.wireOp",EDGE,"E12.29.2"),sQuery(id+"F0.wireOp",EDGE,"E12.29.3"),sQuery(id+"F0.wireOp",EDGE,"E12.29.4"),sQuery(id+"F0.wireOp",EDGE,"E12.29.5"),sQuery(id+"F0.wireOp",EDGE,"E12.29.6"),sQuery(id+"F0.wireOp",EDGE,"E12.29.7"),sQuery(id+"F0.wireOp",EDGE,"E12.29.8"),sQuery(id+"F0.wireOp",EDGE,"E12.29.9"),sQuery(id+"F0.wireOp",EDGE,"E12.30.0"),sQuery(id+"F0.wireOp",EDGE,"E12.30.1"),sQuery(id+"F0.wireOp",EDGE,"E12.30.2"),sQuery(id+"F0.wireOp",EDGE,"E12.30.3"),sQuery(id+"F0.wireOp",EDGE,"E12.30.4"),sQuery(id+"F0.wireOp",EDGE,"E12.30.5"),sQuery(id+"F0.wireOp",EDGE,"E12.30.6"),sQuery(id+"F0.wireOp",EDGE,"E12.30.7"),sQuery(id+"F0.wireOp",EDGE,"E12.30.8"),sQuery(id+"F0.wireOp",EDGE,"E12.30.9"),sQuery(id+"F0.wireOp",EDGE,"E12.31.0"),sQuery(id+"F0.wireOp",EDGE,"E12.31.1"),sQuery(id+"F0.wireOp",EDGE,"E12.31.2"),sQuery(id+"F0.wireOp",EDGE,"E12.31.3"),sQuery(id+"F0.wireOp",EDGE,"E12.31.4"),sQuery(id+"F0.wireOp",EDGE,"E12.31.5"),sQuery(id+"F0.wireOp",EDGE,"E12.31.6"),sQuery(id+"F0.wireOp",EDGE,"E12.31.7"),sQuery(id+"F0.wireOp",EDGE,"E12.31.8"),sQuery(id+"F0.wireOp",EDGE,"E12.31.9"),sQuery(id+"F0.wireOp",EDGE,"E12.32.0"),sQuery(id+"F0.wireOp",EDGE,"E12.32.1"),sQuery(id+"F0.wireOp",EDGE,"E12.32.2"),sQuery(id+"F0.wireOp",EDGE,"E12.32.3"),sQuery(id+"F0.wireOp",EDGE,"E12.32.4"),sQuery(id+"F0.wireOp",EDGE,"E12.32.5"),sQuery(id+"F0.wireOp",EDGE,"E12.32.6"),sQuery(id+"F0.wireOp",EDGE,"E12.32.7"),sQuery(id+"F0.wireOp",EDGE,"E12.32.8"),sQuery(id+"F0.wireOp",EDGE,"E12.32.9"),sQuery(id+"F0.wireOp",EDGE,"E12.33.0"),sQuery(id+"F0.wireOp",EDGE,"E12.33.1"),sQuery(id+"F0.wireOp",EDGE,"E12.33.2"),sQuery(id+"F0.wireOp",EDGE,"E12.33.3"),sQuery(id+"F0.wireOp",EDGE,"E12.33.4"),sQuery(id+"F0.wireOp",EDGE,"E12.33.5"),sQuery(id+"F0.wireOp",EDGE,"E12.33.6"),sQuery(id+"F0.wireOp",EDGE,"E12.33.7"),sQuery(id+"F0.wireOp",EDGE,"E12.33.8"),sQuery(id+"F0.wireOp",EDGE,"E12.33.9"),sQuery(id+"F0.wireOp",EDGE,"E12.34.0"),sQuery(id+"F0.wireOp",EDGE,"E12.34.1"),sQuery(id+"F0.wireOp",EDGE,"E12.34.2"),sQuery(id+"F0.wireOp",EDGE,"E12.34.3"),sQuery(id+"F0.wireOp",EDGE,"E12.34.4"),sQuery(id+"F0.wireOp",EDGE,"E12.34.5"),sQuery(id+"F0.wireOp",EDGE,"E12.34.6"),sQuery(id+"F0.wireOp",EDGE,"E12.34.7"),sQuery(id+"F0.wireOp",EDGE,"E12.34.8"),sQuery(id+"F0.wireOp",EDGE,"E12.34.9"),sQuery(id+"F0.wireOp",EDGE,"E12.35.0"),sQuery(id+"F0.wireOp",EDGE,"E12.35.1"),sQuery(id+"F0.wireOp",EDGE,"E12.35.2"),sQuery(id+"F0.wireOp",EDGE,"E12.35.3"),sQuery(id+"F0.wireOp",EDGE,"E12.35.4"),sQuery(id+"F0.wireOp",EDGE,"E12.35.5"),sQuery(id+"F0.wireOp",EDGE,"E12.35.6"),sQuery(id+"F0.wireOp",EDGE,"E12.35.7"),sQuery(id+"F0.wireOp",EDGE,"E12.35.8"),sQuery(id+"F0.wireOp",EDGE,"E12.35.9"),sQuery(id+"F0.wireOp",EDGE,"E12.36.0"),sQuery(id+"F0.wireOp",EDGE,"E12.36.1"),sQuery(id+"F0.wireOp",EDGE,"E12.36.2"),sQuery(id+"F0.wireOp",EDGE,"E12.36.3"),sQuery(id+"F0.wireOp",EDGE,"E12.36.4"),sQuery(id+"F0.wireOp",EDGE,"E12.36.5"),sQuery(id+"F0.wireOp",EDGE,"E12.36.6"),sQuery(id+"F0.wireOp",EDGE,"E12.36.7"),sQuery(id+"F0.wireOp",EDGE,"E12.36.8"),sQuery(id+"F0.wireOp",EDGE,"E12.36.9"),sQuery(id+"F0.wireOp",EDGE,"E12.37.0"),sQuery(id+"F0.wireOp",EDGE,"E12.37.1"),sQuery(id+"F0.wireOp",EDGE,"E12.37.2"),sQuery(id+"F0.wireOp",EDGE,"E12.37.3"),sQuery(id+"F0.wireOp",EDGE,"E12.37.4"),sQuery(id+"F0.wireOp",EDGE,"E12.37.5"),sQuery(id+"F0.wireOp",EDGE,"E12.37.6"),sQuery(id+"F0.wireOp",EDGE,"E12.37.7"),sQuery(id+"F0.wireOp",EDGE,"E12.37.8"),sQuery(id+"F0.wireOp",EDGE,"E12.37.9"),sQuery(id+"F0.wireOp",EDGE,"E12.38.0"),sQuery(id+"F0.wireOp",EDGE,"E12.38.1"),sQuery(id+"F0.wireOp",EDGE,"E12.38.2"),sQuery(id+"F0.wireOp",EDGE,"E12.38.3"),sQuery(id+"F0.wireOp",EDGE,"E12.38.4"),sQuery(id+"F0.wireOp",EDGE,"E12.38.5"),sQuery(id+"F0.wireOp",EDGE,"E12.38.6"),sQuery(id+"F0.wireOp",EDGE,"E12.38.7"),sQuery(id+"F0.wireOp",EDGE,"E12.38.8"),sQuery(id+"F0.wireOp",EDGE,"E12.38.9"),sQuery(id+"F0.wireOp",EDGE,"E12.39.0"),sQuery(id+"F0.wireOp",EDGE,"E12.39.1"),sQuery(id+"F0.wireOp",EDGE,"E12.39.2"),sQuery(id+"F0.wireOp",EDGE,"E12.39.3"),sQuery(id+"F0.wireOp",EDGE,"E12.39.4"),sQuery(id+"F0.wireOp",EDGE,"E12.39.5"),sQuery(id+"F0.wireOp",EDGE,"E12.39.6"),sQuery(id+"F0.wireOp",EDGE,"E12.39.7"),sQuery(id+"F0.wireOp",EDGE,"E12.39.8"),sQuery(id+"F0.wireOp",EDGE,"E12.39.9"),sQuery(id+"F0.wireOp",EDGE,"E12.40.0"),sQuery(id+"F0.wireOp",EDGE,"E12.40.1"),sQuery(id+"F0.wireOp",EDGE,"E12.40.2"),sQuery(id+"F0.wireOp",EDGE,"E12.40.3"),sQuery(id+"F0.wireOp",EDGE,"E12.40.4"),sQuery(id+"F0.wireOp",EDGE,"E12.40.5"),sQuery(id+"F0.wireOp",EDGE,"E12.40.6"),sQuery(id+"F0.wireOp",EDGE,"E12.40.7"),sQuery(id+"F0.wireOp",EDGE,"E12.40.8"),sQuery(id+"F0.wireOp",EDGE,"E12.40.9"),sQuery(id+"F0.wireOp",EDGE,"E12.41.0"),sQuery(id+"F0.wireOp",EDGE,"E12.41.1"),sQuery(id+"F0.wireOp",EDGE,"E12.41.2"),sQuery(id+"F0.wireOp",EDGE,"E12.41.3"),sQuery(id+"F0.wireOp",EDGE,"E12.41.4"),sQuery(id+"F0.wireOp",EDGE,"E12.41.5"),sQuery(id+"F0.wireOp",EDGE,"E12.41.6"),sQuery(id+"F0.wireOp",EDGE,"E12.41.7"),sQuery(id+"F0.wireOp",EDGE,"E12.41.8"),sQuery(id+"F0.wireOp",EDGE,"E12.41.9"),sQuery(id+"F0.wireOp",EDGE,"E12.42.0"),sQuery(id+"F0.wireOp",EDGE,"E12.42.1"),sQuery(id+"F0.wireOp",EDGE,"E12.42.2"),sQuery(id+"F0.wireOp",EDGE,"E12.42.3"),sQuery(id+"F0.wireOp",EDGE,"E12.42.4"),sQuery(id+"F0.wireOp",EDGE,"E12.42.5"),sQuery(id+"F0.wireOp",EDGE,"E12.42.6"),sQuery(id+"F0.wireOp",EDGE,"E12.42.7"),sQuery(id+"F0.wireOp",EDGE,"E12.42.8"),sQuery(id+"F0.wireOp",EDGE,"E12.42.9"),sQuery(id+"F0.wireOp",EDGE,"E12.43.0"),sQuery(id+"F0.wireOp",EDGE,"E12.43.1"),sQuery(id+"F0.wireOp",EDGE,"E12.43.2"),sQuery(id+"F0.wireOp",EDGE,"E12.43.3"),sQuery(id+"F0.wireOp",EDGE,"E12.43.4"),sQuery(id+"F0.wireOp",EDGE,"E12.43.5"),sQuery(id+"F0.wireOp",EDGE,"E12.43.6"),sQuery(id+"F0.wireOp",EDGE,"E12.43.7"),sQuery(id+"F0.wireOp",EDGE,"E12.43.8"),sQuery(id+"F0.wireOp",EDGE,"E12.43.9"),sQuery(id+"F0.wireOp",EDGE,"E12.44.0"),sQuery(id+"F0.wireOp",EDGE,"E12.44.1"),sQuery(id+"F0.wireOp",EDGE,"E12.44.2"),sQuery(id+"F0.wireOp",EDGE,"E12.44.3"),sQuery(id+"F0.wireOp",EDGE,"E12.44.4"),sQuery(id+"F0.wireOp",EDGE,"E12.44.5"),sQuery(id+"F0.wireOp",EDGE,"E12.44.6"),sQuery(id+"F0.wireOp",EDGE,"E12.44.7"),sQuery(id+"F0.wireOp",EDGE,"E12.44.8"),sQuery(id+"F0.wireOp",EDGE,"E12.44.9"),sQuery(id+"F0.wireOp",EDGE,"E12.45.0"),sQuery(id+"F0.wireOp",EDGE,"E12.45.1"),sQuery(id+"F0.wireOp",EDGE,"E12.45.2"),sQuery(id+"F0.wireOp",EDGE,"E12.45.3"),sQuery(id+"F0.wireOp",EDGE,"E12.45.4"),sQuery(id+"F0.wireOp",EDGE,"E12.45.5"),sQuery(id+"F0.wireOp",EDGE,"E12.45.6"),sQuery(id+"F0.wireOp",EDGE,"E12.45.7"),sQuery(id+"F0.wireOp",EDGE,"E12.45.8"),sQuery(id+"F0.wireOp",EDGE,"E12.45.9"),sQuery(id+"F0.wireOp",EDGE,"E12.46.0"),sQuery(id+"F0.wireOp",EDGE,"E12.46.1"),sQuery(id+"F0.wireOp",EDGE,"E12.46.2"),sQuery(id+"F0.wireOp",EDGE,"E12.46.3"),sQuery(id+"F0.wireOp",EDGE,"E12.46.4"),sQuery(id+"F0.wireOp",EDGE,"E12.46.5"),sQuery(id+"F0.wireOp",EDGE,"E12.46.6"),sQuery(id+"F0.wireOp",EDGE,"E12.46.7"),sQuery(id+"F0.wireOp",EDGE,"E12.46.8"),sQuery(id+"F0.wireOp",EDGE,"E12.46.9"),sQuery(id+"F0.wireOp",EDGE,"E12.47.0"),sQuery(id+"F0.wireOp",EDGE,"E12.47.1"),sQuery(id+"F0.wireOp",EDGE,"E12.47.2"),sQuery(id+"F0.wireOp",EDGE,"E12.47.3"),sQuery(id+"F0.wireOp",EDGE,"E12.47.4"),sQuery(id+"F0.wireOp",EDGE,"E12.47.5"),sQuery(id+"F0.wireOp",EDGE,"E12.47.6"),sQuery(id+"F0.wireOp",EDGE,"E12.47.7"),sQuery(id+"F0.wireOp",EDGE,"E12.47.8"),sQuery(id+"F0.wireOp",EDGE,"E12.47.9"),sQuery(id+"F0.wireOp",EDGE,"E12.48.0"),sQuery(id+"F0.wireOp",EDGE,"E12.48.1"),sQuery(id+"F0.wireOp",EDGE,"E12.48.2"),sQuery(id+"F0.wireOp",EDGE,"E12.48.3"),sQuery(id+"F0.wireOp",EDGE,"E12.48.4"),sQuery(id+"F0.wireOp",EDGE,"E12.48.5"),sQuery(id+"F0.wireOp",EDGE,"E12.48.6"),sQuery(id+"F0.wireOp",EDGE,"E12.48.7"),sQuery(id+"F0.wireOp",EDGE,"E12.48.8"),sQuery(id+"F0.wireOp",EDGE,"E12.48.9"),sQuery(id+"F0.wireOp",EDGE,"E12.49.0"),sQuery(id+"F0.wireOp",EDGE,"E12.49.1"),sQuery(id+"F0.wireOp",EDGE,"E12.49.2"),sQuery(id+"F0.wireOp",EDGE,"E12.49.3"),sQuery(id+"F0.wireOp",EDGE,"E12.49.4"),sQuery(id+"F0.wireOp",EDGE,"E12.49.5"),sQuery(id+"F0.wireOp",EDGE,"E12.49.6"),sQuery(id+"F0.wireOp",EDGE,"E12.49.7"),sQuery(id+"F0.wireOp",EDGE,"E12.49.8"),sQuery(id+"F0.wireOp",EDGE,"E12.49.9"),sQuery(id+"F0.wireOp",EDGE,"E12.50.0"),sQuery(id+"F0.wireOp",EDGE,"E12.50.1"),sQuery(id+"F0.wireOp",EDGE,"E12.50.2"),sQuery(id+"F0.wireOp",EDGE,"E12.50.3"),sQuery(id+"F0.wireOp",EDGE,"E12.50.4"),sQuery(id+"F0.wireOp",EDGE,"E12.50.5"),sQuery(id+"F0.wireOp",EDGE,"E12.50.6"),sQuery(id+"F0.wireOp",EDGE,"E12.50.7"),sQuery(id+"F0.wireOp",EDGE,"E12.50.8"),sQuery(id+"F0.wireOp",EDGE,"E12.50.9"),sQuery(id+"F0.wireOp",EDGE,"E12.51.0"),sQuery(id+"F0.wireOp",EDGE,"E12.51.1"),sQuery(id+"F0.wireOp",EDGE,"E12.51.2"),sQuery(id+"F0.wireOp",EDGE,"E12.51.3"),sQuery(id+"F0.wireOp",EDGE,"E12.51.4"),sQuery(id+"F0.wireOp",EDGE,"E12.51.5"),sQuery(id+"F0.wireOp",EDGE,"E12.51.6"),sQuery(id+"F0.wireOp",EDGE,"E12.51.7"),sQuery(id+"F0.wireOp",EDGE,"E12.51.8"),sQuery(id+"F0.wireOp",EDGE,"E12.51.9"),sQuery(id+"F0.wireOp",EDGE,"E12.52.0"),sQuery(id+"F0.wireOp",EDGE,"E12.52.1"),sQuery(id+"F0.wireOp",EDGE,"E12.52.2"),sQuery(id+"F0.wireOp",EDGE,"E12.52.3"),sQuery(id+"F0.wireOp",EDGE,"E12.52.4"),sQuery(id+"F0.wireOp",EDGE,"E12.52.5"),sQuery(id+"F0.wireOp",EDGE,"E12.52.6"),sQuery(id+"F0.wireOp",EDGE,"E12.52.7"),sQuery(id+"F0.wireOp",EDGE,"E12.52.8"),sQuery(id+"F0.wireOp",EDGE,"E12.52.9"),sQuery(id+"F0.wireOp",EDGE,"E12.53.0"),sQuery(id+"F0.wireOp",EDGE,"E12.53.1"),sQuery(id+"F0.wireOp",EDGE,"E12.53.2"),sQuery(id+"F0.wireOp",EDGE,"E12.53.3"),sQuery(id+"F0.wireOp",EDGE,"E12.53.4"),sQuery(id+"F0.wireOp",EDGE,"E12.53.5"),sQuery(id+"F0.wireOp",EDGE,"E12.53.6"),sQuery(id+"F0.wireOp",EDGE,"E12.53.7"),sQuery(id+"F0.wireOp",EDGE,"E12.53.8"),sQuery(id+"F0.wireOp",EDGE,"E12.53.9"),sQuery(id+"F0.wireOp",EDGE,"E12.54.0"),sQuery(id+"F0.wireOp",EDGE,"E12.54.1"),sQuery(id+"F0.wireOp",EDGE,"E12.54.2"),sQuery(id+"F0.wireOp",EDGE,"E12.54.3"),sQuery(id+"F0.wireOp",EDGE,"E12.54.4"),sQuery(id+"F0.wireOp",EDGE,"E12.54.5"),sQuery(id+"F0.wireOp",EDGE,"E12.54.6"),sQuery(id+"F0.wireOp",EDGE,"E12.54.7"),sQuery(id+"F0.wireOp",EDGE,"E12.54.8"),sQuery(id+"F0.wireOp",EDGE,"E12.54.9"),sQuery(id+"F0.wireOp",EDGE,"E12.55.0"),sQuery(id+"F0.wireOp",EDGE,"E12.55.1"),sQuery(id+"F0.wireOp",EDGE,"E12.55.2"),sQuery(id+"F0.wireOp",EDGE,"E12.55.3"),sQuery(id+"F0.wireOp",EDGE,"E12.55.4"),sQuery(id+"F0.wireOp",EDGE,"E12.55.5"),sQuery(id+"F0.wireOp",EDGE,"E12.55.6"),sQuery(id+"F0.wireOp",EDGE,"E12.55.7"),sQuery(id+"F0.wireOp",EDGE,"E12.55.8"),sQuery(id+"F0.wireOp",EDGE,"E12.55.9"),sQuery(id+"F0.wireOp",EDGE,"E12.56.0"),sQuery(id+"F0.wireOp",EDGE,"E12.56.1"),sQuery(id+"F0.wireOp",EDGE,"E12.56.2"),sQuery(id+"F0.wireOp",EDGE,"E12.56.3"),sQuery(id+"F0.wireOp",EDGE,"E12.56.4"),sQuery(id+"F0.wireOp",EDGE,"E12.56.5"),sQuery(id+"F0.wireOp",EDGE,"E12.56.6"),sQuery(id+"F0.wireOp",EDGE,"E12.56.7"),sQuery(id+"F0.wireOp",EDGE,"E12.56.8"),sQuery(id+"F0.wireOp",EDGE,"E12.56.9"),sQuery(id+"F0.wireOp",EDGE,"E12.57.0"),sQuery(id+"F0.wireOp",EDGE,"E12.57.1"),sQuery(id+"F0.wireOp",EDGE,"E12.57.2"),sQuery(id+"F0.wireOp",EDGE,"E12.57.3"),sQuery(id+"F0.wireOp",EDGE,"E12.57.4"),sQuery(id+"F0.wireOp",EDGE,"E12.57.5"),sQuery(id+"F0.wireOp",EDGE,"E12.57.6"),sQuery(id+"F0.wireOp",EDGE,"E12.57.7"),sQuery(id+"F0.wireOp",EDGE,"E12.57.8"),sQuery(id+"F0.wireOp",EDGE,"E12.57.9"),sQuery(id+"F0.wireOp",EDGE,"E12.58.0"),sQuery(id+"F0.wireOp",EDGE,"E12.58.1"),sQuery(id+"F0.wireOp",EDGE,"E12.58.2"),sQuery(id+"F0.wireOp",EDGE,"E12.58.3"),sQuery(id+"F0.wireOp",EDGE,"E12.58.4"),sQuery(id+"F0.wireOp",EDGE,"E12.58.5"),sQuery(id+"F0.wireOp",EDGE,"E12.58.6"),sQuery(id+"F0.wireOp",EDGE,"E12.58.7"),sQuery(id+"F0.wireOp",EDGE,"E12.58.8"),sQuery(id+"F0.wireOp",EDGE,"E12.58.9"),sQuery(id+"F0.wireOp",EDGE,"E12.59.0"),sQuery(id+"F0.wireOp",EDGE,"E12.59.1"),sQuery(id+"F0.wireOp",EDGE,"E12.59.2"),sQuery(id+"F0.wireOp",EDGE,"E12.59.3"),sQuery(id+"F0.wireOp",EDGE,"E12.59.4"),sQuery(id+"F0.wireOp",EDGE,"E12.59.5"),sQuery(id+"F0.wireOp",EDGE,"E12.59.6"),sQuery(id+"F0.wireOp",EDGE,"E12.59.7"),sQuery(id+"F0.wireOp",EDGE,"E12.59.8"),sQuery(id+"F0.wireOp",EDGE,"E12.59.9"),sQuery(id+"F0.wireOp",EDGE,"E13.trimOffspring"),sQuery(id+"F0.wireOp",EDGE,"E14.trimOffspring")])],"isStart":false});
            var sketch = newSketch(context, id + "F4", { "sketchPlane" : qUnion([Q0])});
            skCircle(sketch, "E19", {"center": v(0, 0) * mm, "radius": 3.97 * mm});
            skSolve(sketch);
        }
        {
            var Q0;
            Q0 = qSketchRegion(id + "F4", true);
            extrude(context, id + "F5", {"entities" : qUnion([Q0]), "operationType" : NewBodyOperationType.REMOVE, "endBound" : BoundingType.THROUGH_ALL, "oppositeDirection" : true, "depth" : 25.4 * mm});
        }
        {
            var Q0;
            Q0=makeQuery(id+"F1.opExtrude","CAP_FACE",FACE,{"disambiguationData":[OSD([sQuery(id+"F0.wireOp",EDGE,"E0"),sQuery(id+"F0.wireOp",EDGE,"E2"),sQuery(id+"F0.wireOp",EDGE,"E3"),sQuery(id+"F0.wireOp",EDGE,"E4.trimOffspring"),sQuery(id+"F0.wireOp",EDGE,"E5.MirrorCS"),sQuery(id+"F0.wireOp",EDGE,"E6.MirrorCS"),sQuery(id+"F0.wireOp",EDGE,"E7.MirrorCS"),sQuery(id+"F0.wireOp",EDGE,"E8.filletArc"),sQuery(id+"F0.wireOp",EDGE,"E9.filletArc"),sQuery(id+"F0.wireOp",EDGE,"E10.filletArc"),sQuery(id+"F0.wireOp",EDGE,"E11.filletArc"),sQuery(id+"F0.wireOp",EDGE,"E12.1.0"),sQuery(id+"F0.wireOp",EDGE,"E12.1.1"),sQuery(id+"F0.wireOp",EDGE,"E12.1.2"),sQuery(id+"F0.wireOp",EDGE,"E12.1.3"),sQuery(id+"F0.wireOp",EDGE,"E12.1.4"),sQuery(id+"F0.wireOp",EDGE,"E12.1.5"),sQuery(id+"F0.wireOp",EDGE,"E12.1.6"),sQuery(id+"F0.wireOp",EDGE,"E12.1.7"),sQuery(id+"F0.wireOp",EDGE,"E12.1.8"),sQuery(id+"F0.wireOp",EDGE,"E12.1.9"),sQuery(id+"F0.wireOp",EDGE,"E12.2.0"),sQuery(id+"F0.wireOp",EDGE,"E12.2.1"),sQuery(id+"F0.wireOp",EDGE,"E12.2.2"),sQuery(id+"F0.wireOp",EDGE,"E12.2.3"),sQuery(id+"F0.wireOp",EDGE,"E12.2.4"),sQuery(id+"F0.wireOp",EDGE,"E12.2.5"),sQuery(id+"F0.wireOp",EDGE,"E12.2.6"),sQuery(id+"F0.wireOp",EDGE,"E12.2.7"),sQuery(id+"F0.wireOp",EDGE,"E12.2.8"),sQuery(id+"F0.wireOp",EDGE,"E12.2.9"),sQuery(id+"F0.wireOp",EDGE,"E12.3.0"),sQuery(id+"F0.wireOp",EDGE,"E12.3.1"),sQuery(id+"F0.wireOp",EDGE,"E12.3.2"),sQuery(id+"F0.wireOp",EDGE,"E12.3.3"),sQuery(id+"F0.wireOp",EDGE,"E12.3.4"),sQuery(id+"F0.wireOp",EDGE,"E12.3.5"),sQuery(id+"F0.wireOp",EDGE,"E12.3.6"),sQuery(id+"F0.wireOp",EDGE,"E12.3.7"),sQuery(id+"F0.wireOp",EDGE,"E12.3.8"),sQuery(id+"F0.wireOp",EDGE,"E12.3.9"),sQuery(id+"F0.wireOp",EDGE,"E12.4.0"),sQuery(id+"F0.wireOp",EDGE,"E12.4.1"),sQuery(id+"F0.wireOp",EDGE,"E12.4.2"),sQuery(id+"F0.wireOp",EDGE,"E12.4.3"),sQuery(id+"F0.wireOp",EDGE,"E12.4.4"),sQuery(id+"F0.wireOp",EDGE,"E12.4.5"),sQuery(id+"F0.wireOp",EDGE,"E12.4.6"),sQuery(id+"F0.wireOp",EDGE,"E12.4.7"),sQuery(id+"F0.wireOp",EDGE,"E12.4.8"),sQuery(id+"F0.wireOp",EDGE,"E12.4.9"),sQuery(id+"F0.wireOp",EDGE,"E12.5.0"),sQuery(id+"F0.wireOp",EDGE,"E12.5.1"),sQuery(id+"F0.wireOp",EDGE,"E12.5.2"),sQuery(id+"F0.wireOp",EDGE,"E12.5.3"),sQuery(id+"F0.wireOp",EDGE,"E12.5.4"),sQuery(id+"F0.wireOp",EDGE,"E12.5.5"),sQuery(id+"F0.wireOp",EDGE,"E12.5.6"),sQuery(id+"F0.wireOp",EDGE,"E12.5.7"),sQuery(id+"F0.wireOp",EDGE,"E12.5.8"),sQuery(id+"F0.wireOp",EDGE,"E12.5.9"),sQuery(id+"F0.wireOp",EDGE,"E12.6.0"),sQuery(id+"F0.wireOp",EDGE,"E12.6.1"),sQuery(id+"F0.wireOp",EDGE,"E12.6.2"),sQuery(id+"F0.wireOp",EDGE,"E12.6.3"),sQuery(id+"F0.wireOp",EDGE,"E12.6.4"),sQuery(id+"F0.wireOp",EDGE,"E12.6.5"),sQuery(id+"F0.wireOp",EDGE,"E12.6.6"),sQuery(id+"F0.wireOp",EDGE,"E12.6.7"),sQuery(id+"F0.wireOp",EDGE,"E12.6.8"),sQuery(id+"F0.wireOp",EDGE,"E12.6.9"),sQuery(id+"F0.wireOp",EDGE,"E12.7.0"),sQuery(id+"F0.wireOp",EDGE,"E12.7.1"),sQuery(id+"F0.wireOp",EDGE,"E12.7.2"),sQuery(id+"F0.wireOp",EDGE,"E12.7.3"),sQuery(id+"F0.wireOp",EDGE,"E12.7.4"),sQuery(id+"F0.wireOp",EDGE,"E12.7.5"),sQuery(id+"F0.wireOp",EDGE,"E12.7.6"),sQuery(id+"F0.wireOp",EDGE,"E12.7.7"),sQuery(id+"F0.wireOp",EDGE,"E12.7.8"),sQuery(id+"F0.wireOp",EDGE,"E12.7.9"),sQuery(id+"F0.wireOp",EDGE,"E12.8.0"),sQuery(id+"F0.wireOp",EDGE,"E12.8.1"),sQuery(id+"F0.wireOp",EDGE,"E12.8.2"),sQuery(id+"F0.wireOp",EDGE,"E12.8.3"),sQuery(id+"F0.wireOp",EDGE,"E12.8.4"),sQuery(id+"F0.wireOp",EDGE,"E12.8.5"),sQuery(id+"F0.wireOp",EDGE,"E12.8.6"),sQuery(id+"F0.wireOp",EDGE,"E12.8.7"),sQuery(id+"F0.wireOp",EDGE,"E12.8.8"),sQuery(id+"F0.wireOp",EDGE,"E12.8.9"),sQuery(id+"F0.wireOp",EDGE,"E12.9.0"),sQuery(id+"F0.wireOp",EDGE,"E12.9.1"),sQuery(id+"F0.wireOp",EDGE,"E12.9.2"),sQuery(id+"F0.wireOp",EDGE,"E12.9.3"),sQuery(id+"F0.wireOp",EDGE,"E12.9.4"),sQuery(id+"F0.wireOp",EDGE,"E12.9.5"),sQuery(id+"F0.wireOp",EDGE,"E12.9.6"),sQuery(id+"F0.wireOp",EDGE,"E12.9.7"),sQuery(id+"F0.wireOp",EDGE,"E12.9.8"),sQuery(id+"F0.wireOp",EDGE,"E12.9.9"),sQuery(id+"F0.wireOp",EDGE,"E12.10.0"),sQuery(id+"F0.wireOp",EDGE,"E12.10.1"),sQuery(id+"F0.wireOp",EDGE,"E12.10.2"),sQuery(id+"F0.wireOp",EDGE,"E12.10.3"),sQuery(id+"F0.wireOp",EDGE,"E12.10.4"),sQuery(id+"F0.wireOp",EDGE,"E12.10.5"),sQuery(id+"F0.wireOp",EDGE,"E12.10.6"),sQuery(id+"F0.wireOp",EDGE,"E12.10.7"),sQuery(id+"F0.wireOp",EDGE,"E12.10.8"),sQuery(id+"F0.wireOp",EDGE,"E12.10.9"),sQuery(id+"F0.wireOp",EDGE,"E12.11.0"),sQuery(id+"F0.wireOp",EDGE,"E12.11.1"),sQuery(id+"F0.wireOp",EDGE,"E12.11.2"),sQuery(id+"F0.wireOp",EDGE,"E12.11.3"),sQuery(id+"F0.wireOp",EDGE,"E12.11.4"),sQuery(id+"F0.wireOp",EDGE,"E12.11.5"),sQuery(id+"F0.wireOp",EDGE,"E12.11.6"),sQuery(id+"F0.wireOp",EDGE,"E12.11.7"),sQuery(id+"F0.wireOp",EDGE,"E12.11.8"),sQuery(id+"F0.wireOp",EDGE,"E12.11.9"),sQuery(id+"F0.wireOp",EDGE,"E12.12.0"),sQuery(id+"F0.wireOp",EDGE,"E12.12.1"),sQuery(id+"F0.wireOp",EDGE,"E12.12.2"),sQuery(id+"F0.wireOp",EDGE,"E12.12.3"),sQuery(id+"F0.wireOp",EDGE,"E12.12.4"),sQuery(id+"F0.wireOp",EDGE,"E12.12.5"),sQuery(id+"F0.wireOp",EDGE,"E12.12.6"),sQuery(id+"F0.wireOp",EDGE,"E12.12.7"),sQuery(id+"F0.wireOp",EDGE,"E12.12.8"),sQuery(id+"F0.wireOp",EDGE,"E12.12.9"),sQuery(id+"F0.wireOp",EDGE,"E12.13.0"),sQuery(id+"F0.wireOp",EDGE,"E12.13.1"),sQuery(id+"F0.wireOp",EDGE,"E12.13.2"),sQuery(id+"F0.wireOp",EDGE,"E12.13.3"),sQuery(id+"F0.wireOp",EDGE,"E12.13.4"),sQuery(id+"F0.wireOp",EDGE,"E12.13.5"),sQuery(id+"F0.wireOp",EDGE,"E12.13.6"),sQuery(id+"F0.wireOp",EDGE,"E12.13.7"),sQuery(id+"F0.wireOp",EDGE,"E12.13.8"),sQuery(id+"F0.wireOp",EDGE,"E12.13.9"),sQuery(id+"F0.wireOp",EDGE,"E12.14.0"),sQuery(id+"F0.wireOp",EDGE,"E12.14.1"),sQuery(id+"F0.wireOp",EDGE,"E12.14.2"),sQuery(id+"F0.wireOp",EDGE,"E12.14.3"),sQuery(id+"F0.wireOp",EDGE,"E12.14.4"),sQuery(id+"F0.wireOp",EDGE,"E12.14.5"),sQuery(id+"F0.wireOp",EDGE,"E12.14.6"),sQuery(id+"F0.wireOp",EDGE,"E12.14.7"),sQuery(id+"F0.wireOp",EDGE,"E12.14.8"),sQuery(id+"F0.wireOp",EDGE,"E12.14.9"),sQuery(id+"F0.wireOp",EDGE,"E12.15.0"),sQuery(id+"F0.wireOp",EDGE,"E12.15.1"),sQuery(id+"F0.wireOp",EDGE,"E12.15.2"),sQuery(id+"F0.wireOp",EDGE,"E12.15.3"),sQuery(id+"F0.wireOp",EDGE,"E12.15.4"),sQuery(id+"F0.wireOp",EDGE,"E12.15.5"),sQuery(id+"F0.wireOp",EDGE,"E12.15.6"),sQuery(id+"F0.wireOp",EDGE,"E12.15.7"),sQuery(id+"F0.wireOp",EDGE,"E12.15.8"),sQuery(id+"F0.wireOp",EDGE,"E12.15.9"),sQuery(id+"F0.wireOp",EDGE,"E12.16.0"),sQuery(id+"F0.wireOp",EDGE,"E12.16.1"),sQuery(id+"F0.wireOp",EDGE,"E12.16.2"),sQuery(id+"F0.wireOp",EDGE,"E12.16.3"),sQuery(id+"F0.wireOp",EDGE,"E12.16.4"),sQuery(id+"F0.wireOp",EDGE,"E12.16.5"),sQuery(id+"F0.wireOp",EDGE,"E12.16.6"),sQuery(id+"F0.wireOp",EDGE,"E12.16.7"),sQuery(id+"F0.wireOp",EDGE,"E12.16.8"),sQuery(id+"F0.wireOp",EDGE,"E12.16.9"),sQuery(id+"F0.wireOp",EDGE,"E12.17.0"),sQuery(id+"F0.wireOp",EDGE,"E12.17.1"),sQuery(id+"F0.wireOp",EDGE,"E12.17.2"),sQuery(id+"F0.wireOp",EDGE,"E12.17.3"),sQuery(id+"F0.wireOp",EDGE,"E12.17.4"),sQuery(id+"F0.wireOp",EDGE,"E12.17.5"),sQuery(id+"F0.wireOp",EDGE,"E12.17.6"),sQuery(id+"F0.wireOp",EDGE,"E12.17.7"),sQuery(id+"F0.wireOp",EDGE,"E12.17.8"),sQuery(id+"F0.wireOp",EDGE,"E12.17.9"),sQuery(id+"F0.wireOp",EDGE,"E12.18.0"),sQuery(id+"F0.wireOp",EDGE,"E12.18.1"),sQuery(id+"F0.wireOp",EDGE,"E12.18.2"),sQuery(id+"F0.wireOp",EDGE,"E12.18.3"),sQuery(id+"F0.wireOp",EDGE,"E12.18.4"),sQuery(id+"F0.wireOp",EDGE,"E12.18.5"),sQuery(id+"F0.wireOp",EDGE,"E12.18.6"),sQuery(id+"F0.wireOp",EDGE,"E12.18.7"),sQuery(id+"F0.wireOp",EDGE,"E12.18.8"),sQuery(id+"F0.wireOp",EDGE,"E12.18.9"),sQuery(id+"F0.wireOp",EDGE,"E12.19.0"),sQuery(id+"F0.wireOp",EDGE,"E12.19.1"),sQuery(id+"F0.wireOp",EDGE,"E12.19.2"),sQuery(id+"F0.wireOp",EDGE,"E12.19.3"),sQuery(id+"F0.wireOp",EDGE,"E12.19.4"),sQuery(id+"F0.wireOp",EDGE,"E12.19.5"),sQuery(id+"F0.wireOp",EDGE,"E12.19.6"),sQuery(id+"F0.wireOp",EDGE,"E12.19.7"),sQuery(id+"F0.wireOp",EDGE,"E12.19.8"),sQuery(id+"F0.wireOp",EDGE,"E12.19.9"),sQuery(id+"F0.wireOp",EDGE,"E12.20.0"),sQuery(id+"F0.wireOp",EDGE,"E12.20.1"),sQuery(id+"F0.wireOp",EDGE,"E12.20.2"),sQuery(id+"F0.wireOp",EDGE,"E12.20.3"),sQuery(id+"F0.wireOp",EDGE,"E12.20.4"),sQuery(id+"F0.wireOp",EDGE,"E12.20.5"),sQuery(id+"F0.wireOp",EDGE,"E12.20.6"),sQuery(id+"F0.wireOp",EDGE,"E12.20.7"),sQuery(id+"F0.wireOp",EDGE,"E12.20.8"),sQuery(id+"F0.wireOp",EDGE,"E12.20.9"),sQuery(id+"F0.wireOp",EDGE,"E12.21.0"),sQuery(id+"F0.wireOp",EDGE,"E12.21.1"),sQuery(id+"F0.wireOp",EDGE,"E12.21.2"),sQuery(id+"F0.wireOp",EDGE,"E12.21.3"),sQuery(id+"F0.wireOp",EDGE,"E12.21.4"),sQuery(id+"F0.wireOp",EDGE,"E12.21.5"),sQuery(id+"F0.wireOp",EDGE,"E12.21.6"),sQuery(id+"F0.wireOp",EDGE,"E12.21.7"),sQuery(id+"F0.wireOp",EDGE,"E12.21.8"),sQuery(id+"F0.wireOp",EDGE,"E12.21.9"),sQuery(id+"F0.wireOp",EDGE,"E12.22.0"),sQuery(id+"F0.wireOp",EDGE,"E12.22.1"),sQuery(id+"F0.wireOp",EDGE,"E12.22.2"),sQuery(id+"F0.wireOp",EDGE,"E12.22.3"),sQuery(id+"F0.wireOp",EDGE,"E12.22.4"),sQuery(id+"F0.wireOp",EDGE,"E12.22.5"),sQuery(id+"F0.wireOp",EDGE,"E12.22.6"),sQuery(id+"F0.wireOp",EDGE,"E12.22.7"),sQuery(id+"F0.wireOp",EDGE,"E12.22.8"),sQuery(id+"F0.wireOp",EDGE,"E12.22.9"),sQuery(id+"F0.wireOp",EDGE,"E12.23.0"),sQuery(id+"F0.wireOp",EDGE,"E12.23.1"),sQuery(id+"F0.wireOp",EDGE,"E12.23.2"),sQuery(id+"F0.wireOp",EDGE,"E12.23.3"),sQuery(id+"F0.wireOp",EDGE,"E12.23.4"),sQuery(id+"F0.wireOp",EDGE,"E12.23.5"),sQuery(id+"F0.wireOp",EDGE,"E12.23.6"),sQuery(id+"F0.wireOp",EDGE,"E12.23.7"),sQuery(id+"F0.wireOp",EDGE,"E12.23.8"),sQuery(id+"F0.wireOp",EDGE,"E12.23.9"),sQuery(id+"F0.wireOp",EDGE,"E12.24.0"),sQuery(id+"F0.wireOp",EDGE,"E12.24.1"),sQuery(id+"F0.wireOp",EDGE,"E12.24.2"),sQuery(id+"F0.wireOp",EDGE,"E12.24.3"),sQuery(id+"F0.wireOp",EDGE,"E12.24.4"),sQuery(id+"F0.wireOp",EDGE,"E12.24.5"),sQuery(id+"F0.wireOp",EDGE,"E12.24.6"),sQuery(id+"F0.wireOp",EDGE,"E12.24.7"),sQuery(id+"F0.wireOp",EDGE,"E12.24.8"),sQuery(id+"F0.wireOp",EDGE,"E12.24.9"),sQuery(id+"F0.wireOp",EDGE,"E12.25.0"),sQuery(id+"F0.wireOp",EDGE,"E12.25.1"),sQuery(id+"F0.wireOp",EDGE,"E12.25.2"),sQuery(id+"F0.wireOp",EDGE,"E12.25.3"),sQuery(id+"F0.wireOp",EDGE,"E12.25.4"),sQuery(id+"F0.wireOp",EDGE,"E12.25.5"),sQuery(id+"F0.wireOp",EDGE,"E12.25.6"),sQuery(id+"F0.wireOp",EDGE,"E12.25.7"),sQuery(id+"F0.wireOp",EDGE,"E12.25.8"),sQuery(id+"F0.wireOp",EDGE,"E12.25.9"),sQuery(id+"F0.wireOp",EDGE,"E12.26.0"),sQuery(id+"F0.wireOp",EDGE,"E12.26.1"),sQuery(id+"F0.wireOp",EDGE,"E12.26.2"),sQuery(id+"F0.wireOp",EDGE,"E12.26.3"),sQuery(id+"F0.wireOp",EDGE,"E12.26.4"),sQuery(id+"F0.wireOp",EDGE,"E12.26.5"),sQuery(id+"F0.wireOp",EDGE,"E12.26.6"),sQuery(id+"F0.wireOp",EDGE,"E12.26.7"),sQuery(id+"F0.wireOp",EDGE,"E12.26.8"),sQuery(id+"F0.wireOp",EDGE,"E12.26.9"),sQuery(id+"F0.wireOp",EDGE,"E12.27.0"),sQuery(id+"F0.wireOp",EDGE,"E12.27.1"),sQuery(id+"F0.wireOp",EDGE,"E12.27.2"),sQuery(id+"F0.wireOp",EDGE,"E12.27.3"),sQuery(id+"F0.wireOp",EDGE,"E12.27.4"),sQuery(id+"F0.wireOp",EDGE,"E12.27.5"),sQuery(id+"F0.wireOp",EDGE,"E12.27.6"),sQuery(id+"F0.wireOp",EDGE,"E12.27.7"),sQuery(id+"F0.wireOp",EDGE,"E12.27.8"),sQuery(id+"F0.wireOp",EDGE,"E12.27.9"),sQuery(id+"F0.wireOp",EDGE,"E12.28.0"),sQuery(id+"F0.wireOp",EDGE,"E12.28.1"),sQuery(id+"F0.wireOp",EDGE,"E12.28.2"),sQuery(id+"F0.wireOp",EDGE,"E12.28.3"),sQuery(id+"F0.wireOp",EDGE,"E12.28.4"),sQuery(id+"F0.wireOp",EDGE,"E12.28.5"),sQuery(id+"F0.wireOp",EDGE,"E12.28.6"),sQuery(id+"F0.wireOp",EDGE,"E12.28.7"),sQuery(id+"F0.wireOp",EDGE,"E12.28.8"),sQuery(id+"F0.wireOp",EDGE,"E12.28.9"),sQuery(id+"F0.wireOp",EDGE,"E12.29.0"),sQuery(id+"F0.wireOp",EDGE,"E12.29.1"),sQuery(id+"F0.wireOp",EDGE,"E12.29.2"),sQuery(id+"F0.wireOp",EDGE,"E12.29.3"),sQuery(id+"F0.wireOp",EDGE,"E12.29.4"),sQuery(id+"F0.wireOp",EDGE,"E12.29.5"),sQuery(id+"F0.wireOp",EDGE,"E12.29.6"),sQuery(id+"F0.wireOp",EDGE,"E12.29.7"),sQuery(id+"F0.wireOp",EDGE,"E12.29.8"),sQuery(id+"F0.wireOp",EDGE,"E12.29.9"),sQuery(id+"F0.wireOp",EDGE,"E12.30.0"),sQuery(id+"F0.wireOp",EDGE,"E12.30.1"),sQuery(id+"F0.wireOp",EDGE,"E12.30.2"),sQuery(id+"F0.wireOp",EDGE,"E12.30.3"),sQuery(id+"F0.wireOp",EDGE,"E12.30.4"),sQuery(id+"F0.wireOp",EDGE,"E12.30.5"),sQuery(id+"F0.wireOp",EDGE,"E12.30.6"),sQuery(id+"F0.wireOp",EDGE,"E12.30.7"),sQuery(id+"F0.wireOp",EDGE,"E12.30.8"),sQuery(id+"F0.wireOp",EDGE,"E12.30.9"),sQuery(id+"F0.wireOp",EDGE,"E12.31.0"),sQuery(id+"F0.wireOp",EDGE,"E12.31.1"),sQuery(id+"F0.wireOp",EDGE,"E12.31.2"),sQuery(id+"F0.wireOp",EDGE,"E12.31.3"),sQuery(id+"F0.wireOp",EDGE,"E12.31.4"),sQuery(id+"F0.wireOp",EDGE,"E12.31.5"),sQuery(id+"F0.wireOp",EDGE,"E12.31.6"),sQuery(id+"F0.wireOp",EDGE,"E12.31.7"),sQuery(id+"F0.wireOp",EDGE,"E12.31.8"),sQuery(id+"F0.wireOp",EDGE,"E12.31.9"),sQuery(id+"F0.wireOp",EDGE,"E12.32.0"),sQuery(id+"F0.wireOp",EDGE,"E12.32.1"),sQuery(id+"F0.wireOp",EDGE,"E12.32.2"),sQuery(id+"F0.wireOp",EDGE,"E12.32.3"),sQuery(id+"F0.wireOp",EDGE,"E12.32.4"),sQuery(id+"F0.wireOp",EDGE,"E12.32.5"),sQuery(id+"F0.wireOp",EDGE,"E12.32.6"),sQuery(id+"F0.wireOp",EDGE,"E12.32.7"),sQuery(id+"F0.wireOp",EDGE,"E12.32.8"),sQuery(id+"F0.wireOp",EDGE,"E12.32.9"),sQuery(id+"F0.wireOp",EDGE,"E12.33.0"),sQuery(id+"F0.wireOp",EDGE,"E12.33.1"),sQuery(id+"F0.wireOp",EDGE,"E12.33.2"),sQuery(id+"F0.wireOp",EDGE,"E12.33.3"),sQuery(id+"F0.wireOp",EDGE,"E12.33.4"),sQuery(id+"F0.wireOp",EDGE,"E12.33.5"),sQuery(id+"F0.wireOp",EDGE,"E12.33.6"),sQuery(id+"F0.wireOp",EDGE,"E12.33.7"),sQuery(id+"F0.wireOp",EDGE,"E12.33.8"),sQuery(id+"F0.wireOp",EDGE,"E12.33.9"),sQuery(id+"F0.wireOp",EDGE,"E12.34.0"),sQuery(id+"F0.wireOp",EDGE,"E12.34.1"),sQuery(id+"F0.wireOp",EDGE,"E12.34.2"),sQuery(id+"F0.wireOp",EDGE,"E12.34.3"),sQuery(id+"F0.wireOp",EDGE,"E12.34.4"),sQuery(id+"F0.wireOp",EDGE,"E12.34.5"),sQuery(id+"F0.wireOp",EDGE,"E12.34.6"),sQuery(id+"F0.wireOp",EDGE,"E12.34.7"),sQuery(id+"F0.wireOp",EDGE,"E12.34.8"),sQuery(id+"F0.wireOp",EDGE,"E12.34.9"),sQuery(id+"F0.wireOp",EDGE,"E12.35.0"),sQuery(id+"F0.wireOp",EDGE,"E12.35.1"),sQuery(id+"F0.wireOp",EDGE,"E12.35.2"),sQuery(id+"F0.wireOp",EDGE,"E12.35.3"),sQuery(id+"F0.wireOp",EDGE,"E12.35.4"),sQuery(id+"F0.wireOp",EDGE,"E12.35.5"),sQuery(id+"F0.wireOp",EDGE,"E12.35.6"),sQuery(id+"F0.wireOp",EDGE,"E12.35.7"),sQuery(id+"F0.wireOp",EDGE,"E12.35.8"),sQuery(id+"F0.wireOp",EDGE,"E12.35.9"),sQuery(id+"F0.wireOp",EDGE,"E12.36.0"),sQuery(id+"F0.wireOp",EDGE,"E12.36.1"),sQuery(id+"F0.wireOp",EDGE,"E12.36.2"),sQuery(id+"F0.wireOp",EDGE,"E12.36.3"),sQuery(id+"F0.wireOp",EDGE,"E12.36.4"),sQuery(id+"F0.wireOp",EDGE,"E12.36.5"),sQuery(id+"F0.wireOp",EDGE,"E12.36.6"),sQuery(id+"F0.wireOp",EDGE,"E12.36.7"),sQuery(id+"F0.wireOp",EDGE,"E12.36.8"),sQuery(id+"F0.wireOp",EDGE,"E12.36.9"),sQuery(id+"F0.wireOp",EDGE,"E12.37.0"),sQuery(id+"F0.wireOp",EDGE,"E12.37.1"),sQuery(id+"F0.wireOp",EDGE,"E12.37.2"),sQuery(id+"F0.wireOp",EDGE,"E12.37.3"),sQuery(id+"F0.wireOp",EDGE,"E12.37.4"),sQuery(id+"F0.wireOp",EDGE,"E12.37.5"),sQuery(id+"F0.wireOp",EDGE,"E12.37.6"),sQuery(id+"F0.wireOp",EDGE,"E12.37.7"),sQuery(id+"F0.wireOp",EDGE,"E12.37.8"),sQuery(id+"F0.wireOp",EDGE,"E12.37.9"),sQuery(id+"F0.wireOp",EDGE,"E12.38.0"),sQuery(id+"F0.wireOp",EDGE,"E12.38.1"),sQuery(id+"F0.wireOp",EDGE,"E12.38.2"),sQuery(id+"F0.wireOp",EDGE,"E12.38.3"),sQuery(id+"F0.wireOp",EDGE,"E12.38.4"),sQuery(id+"F0.wireOp",EDGE,"E12.38.5"),sQuery(id+"F0.wireOp",EDGE,"E12.38.6"),sQuery(id+"F0.wireOp",EDGE,"E12.38.7"),sQuery(id+"F0.wireOp",EDGE,"E12.38.8"),sQuery(id+"F0.wireOp",EDGE,"E12.38.9"),sQuery(id+"F0.wireOp",EDGE,"E12.39.0"),sQuery(id+"F0.wireOp",EDGE,"E12.39.1"),sQuery(id+"F0.wireOp",EDGE,"E12.39.2"),sQuery(id+"F0.wireOp",EDGE,"E12.39.3"),sQuery(id+"F0.wireOp",EDGE,"E12.39.4"),sQuery(id+"F0.wireOp",EDGE,"E12.39.5"),sQuery(id+"F0.wireOp",EDGE,"E12.39.6"),sQuery(id+"F0.wireOp",EDGE,"E12.39.7"),sQuery(id+"F0.wireOp",EDGE,"E12.39.8"),sQuery(id+"F0.wireOp",EDGE,"E12.39.9"),sQuery(id+"F0.wireOp",EDGE,"E12.40.0"),sQuery(id+"F0.wireOp",EDGE,"E12.40.1"),sQuery(id+"F0.wireOp",EDGE,"E12.40.2"),sQuery(id+"F0.wireOp",EDGE,"E12.40.3"),sQuery(id+"F0.wireOp",EDGE,"E12.40.4"),sQuery(id+"F0.wireOp",EDGE,"E12.40.5"),sQuery(id+"F0.wireOp",EDGE,"E12.40.6"),sQuery(id+"F0.wireOp",EDGE,"E12.40.7"),sQuery(id+"F0.wireOp",EDGE,"E12.40.8"),sQuery(id+"F0.wireOp",EDGE,"E12.40.9"),sQuery(id+"F0.wireOp",EDGE,"E12.41.0"),sQuery(id+"F0.wireOp",EDGE,"E12.41.1"),sQuery(id+"F0.wireOp",EDGE,"E12.41.2"),sQuery(id+"F0.wireOp",EDGE,"E12.41.3"),sQuery(id+"F0.wireOp",EDGE,"E12.41.4"),sQuery(id+"F0.wireOp",EDGE,"E12.41.5"),sQuery(id+"F0.wireOp",EDGE,"E12.41.6"),sQuery(id+"F0.wireOp",EDGE,"E12.41.7"),sQuery(id+"F0.wireOp",EDGE,"E12.41.8"),sQuery(id+"F0.wireOp",EDGE,"E12.41.9"),sQuery(id+"F0.wireOp",EDGE,"E12.42.0"),sQuery(id+"F0.wireOp",EDGE,"E12.42.1"),sQuery(id+"F0.wireOp",EDGE,"E12.42.2"),sQuery(id+"F0.wireOp",EDGE,"E12.42.3"),sQuery(id+"F0.wireOp",EDGE,"E12.42.4"),sQuery(id+"F0.wireOp",EDGE,"E12.42.5"),sQuery(id+"F0.wireOp",EDGE,"E12.42.6"),sQuery(id+"F0.wireOp",EDGE,"E12.42.7"),sQuery(id+"F0.wireOp",EDGE,"E12.42.8"),sQuery(id+"F0.wireOp",EDGE,"E12.42.9"),sQuery(id+"F0.wireOp",EDGE,"E12.43.0"),sQuery(id+"F0.wireOp",EDGE,"E12.43.1"),sQuery(id+"F0.wireOp",EDGE,"E12.43.2"),sQuery(id+"F0.wireOp",EDGE,"E12.43.3"),sQuery(id+"F0.wireOp",EDGE,"E12.43.4"),sQuery(id+"F0.wireOp",EDGE,"E12.43.5"),sQuery(id+"F0.wireOp",EDGE,"E12.43.6"),sQuery(id+"F0.wireOp",EDGE,"E12.43.7"),sQuery(id+"F0.wireOp",EDGE,"E12.43.8"),sQuery(id+"F0.wireOp",EDGE,"E12.43.9"),sQuery(id+"F0.wireOp",EDGE,"E12.44.0"),sQuery(id+"F0.wireOp",EDGE,"E12.44.1"),sQuery(id+"F0.wireOp",EDGE,"E12.44.2"),sQuery(id+"F0.wireOp",EDGE,"E12.44.3"),sQuery(id+"F0.wireOp",EDGE,"E12.44.4"),sQuery(id+"F0.wireOp",EDGE,"E12.44.5"),sQuery(id+"F0.wireOp",EDGE,"E12.44.6"),sQuery(id+"F0.wireOp",EDGE,"E12.44.7"),sQuery(id+"F0.wireOp",EDGE,"E12.44.8"),sQuery(id+"F0.wireOp",EDGE,"E12.44.9"),sQuery(id+"F0.wireOp",EDGE,"E12.45.0"),sQuery(id+"F0.wireOp",EDGE,"E12.45.1"),sQuery(id+"F0.wireOp",EDGE,"E12.45.2"),sQuery(id+"F0.wireOp",EDGE,"E12.45.3"),sQuery(id+"F0.wireOp",EDGE,"E12.45.4"),sQuery(id+"F0.wireOp",EDGE,"E12.45.5"),sQuery(id+"F0.wireOp",EDGE,"E12.45.6"),sQuery(id+"F0.wireOp",EDGE,"E12.45.7"),sQuery(id+"F0.wireOp",EDGE,"E12.45.8"),sQuery(id+"F0.wireOp",EDGE,"E12.45.9"),sQuery(id+"F0.wireOp",EDGE,"E12.46.0"),sQuery(id+"F0.wireOp",EDGE,"E12.46.1"),sQuery(id+"F0.wireOp",EDGE,"E12.46.2"),sQuery(id+"F0.wireOp",EDGE,"E12.46.3"),sQuery(id+"F0.wireOp",EDGE,"E12.46.4"),sQuery(id+"F0.wireOp",EDGE,"E12.46.5"),sQuery(id+"F0.wireOp",EDGE,"E12.46.6"),sQuery(id+"F0.wireOp",EDGE,"E12.46.7"),sQuery(id+"F0.wireOp",EDGE,"E12.46.8"),sQuery(id+"F0.wireOp",EDGE,"E12.46.9"),sQuery(id+"F0.wireOp",EDGE,"E12.47.0"),sQuery(id+"F0.wireOp",EDGE,"E12.47.1"),sQuery(id+"F0.wireOp",EDGE,"E12.47.2"),sQuery(id+"F0.wireOp",EDGE,"E12.47.3"),sQuery(id+"F0.wireOp",EDGE,"E12.47.4"),sQuery(id+"F0.wireOp",EDGE,"E12.47.5"),sQuery(id+"F0.wireOp",EDGE,"E12.47.6"),sQuery(id+"F0.wireOp",EDGE,"E12.47.7"),sQuery(id+"F0.wireOp",EDGE,"E12.47.8"),sQuery(id+"F0.wireOp",EDGE,"E12.47.9"),sQuery(id+"F0.wireOp",EDGE,"E12.48.0"),sQuery(id+"F0.wireOp",EDGE,"E12.48.1"),sQuery(id+"F0.wireOp",EDGE,"E12.48.2"),sQuery(id+"F0.wireOp",EDGE,"E12.48.3"),sQuery(id+"F0.wireOp",EDGE,"E12.48.4"),sQuery(id+"F0.wireOp",EDGE,"E12.48.5"),sQuery(id+"F0.wireOp",EDGE,"E12.48.6"),sQuery(id+"F0.wireOp",EDGE,"E12.48.7"),sQuery(id+"F0.wireOp",EDGE,"E12.48.8"),sQuery(id+"F0.wireOp",EDGE,"E12.48.9"),sQuery(id+"F0.wireOp",EDGE,"E12.49.0"),sQuery(id+"F0.wireOp",EDGE,"E12.49.1"),sQuery(id+"F0.wireOp",EDGE,"E12.49.2"),sQuery(id+"F0.wireOp",EDGE,"E12.49.3"),sQuery(id+"F0.wireOp",EDGE,"E12.49.4"),sQuery(id+"F0.wireOp",EDGE,"E12.49.5"),sQuery(id+"F0.wireOp",EDGE,"E12.49.6"),sQuery(id+"F0.wireOp",EDGE,"E12.49.7"),sQuery(id+"F0.wireOp",EDGE,"E12.49.8"),sQuery(id+"F0.wireOp",EDGE,"E12.49.9"),sQuery(id+"F0.wireOp",EDGE,"E12.50.0"),sQuery(id+"F0.wireOp",EDGE,"E12.50.1"),sQuery(id+"F0.wireOp",EDGE,"E12.50.2"),sQuery(id+"F0.wireOp",EDGE,"E12.50.3"),sQuery(id+"F0.wireOp",EDGE,"E12.50.4"),sQuery(id+"F0.wireOp",EDGE,"E12.50.5"),sQuery(id+"F0.wireOp",EDGE,"E12.50.6"),sQuery(id+"F0.wireOp",EDGE,"E12.50.7"),sQuery(id+"F0.wireOp",EDGE,"E12.50.8"),sQuery(id+"F0.wireOp",EDGE,"E12.50.9"),sQuery(id+"F0.wireOp",EDGE,"E12.51.0"),sQuery(id+"F0.wireOp",EDGE,"E12.51.1"),sQuery(id+"F0.wireOp",EDGE,"E12.51.2"),sQuery(id+"F0.wireOp",EDGE,"E12.51.3"),sQuery(id+"F0.wireOp",EDGE,"E12.51.4"),sQuery(id+"F0.wireOp",EDGE,"E12.51.5"),sQuery(id+"F0.wireOp",EDGE,"E12.51.6"),sQuery(id+"F0.wireOp",EDGE,"E12.51.7"),sQuery(id+"F0.wireOp",EDGE,"E12.51.8"),sQuery(id+"F0.wireOp",EDGE,"E12.51.9"),sQuery(id+"F0.wireOp",EDGE,"E12.52.0"),sQuery(id+"F0.wireOp",EDGE,"E12.52.1"),sQuery(id+"F0.wireOp",EDGE,"E12.52.2"),sQuery(id+"F0.wireOp",EDGE,"E12.52.3"),sQuery(id+"F0.wireOp",EDGE,"E12.52.4"),sQuery(id+"F0.wireOp",EDGE,"E12.52.5"),sQuery(id+"F0.wireOp",EDGE,"E12.52.6"),sQuery(id+"F0.wireOp",EDGE,"E12.52.7"),sQuery(id+"F0.wireOp",EDGE,"E12.52.8"),sQuery(id+"F0.wireOp",EDGE,"E12.52.9"),sQuery(id+"F0.wireOp",EDGE,"E12.53.0"),sQuery(id+"F0.wireOp",EDGE,"E12.53.1"),sQuery(id+"F0.wireOp",EDGE,"E12.53.2"),sQuery(id+"F0.wireOp",EDGE,"E12.53.3"),sQuery(id+"F0.wireOp",EDGE,"E12.53.4"),sQuery(id+"F0.wireOp",EDGE,"E12.53.5"),sQuery(id+"F0.wireOp",EDGE,"E12.53.6"),sQuery(id+"F0.wireOp",EDGE,"E12.53.7"),sQuery(id+"F0.wireOp",EDGE,"E12.53.8"),sQuery(id+"F0.wireOp",EDGE,"E12.53.9"),sQuery(id+"F0.wireOp",EDGE,"E12.54.0"),sQuery(id+"F0.wireOp",EDGE,"E12.54.1"),sQuery(id+"F0.wireOp",EDGE,"E12.54.2"),sQuery(id+"F0.wireOp",EDGE,"E12.54.3"),sQuery(id+"F0.wireOp",EDGE,"E12.54.4"),sQuery(id+"F0.wireOp",EDGE,"E12.54.5"),sQuery(id+"F0.wireOp",EDGE,"E12.54.6"),sQuery(id+"F0.wireOp",EDGE,"E12.54.7"),sQuery(id+"F0.wireOp",EDGE,"E12.54.8"),sQuery(id+"F0.wireOp",EDGE,"E12.54.9"),sQuery(id+"F0.wireOp",EDGE,"E12.55.0"),sQuery(id+"F0.wireOp",EDGE,"E12.55.1"),sQuery(id+"F0.wireOp",EDGE,"E12.55.2"),sQuery(id+"F0.wireOp",EDGE,"E12.55.3"),sQuery(id+"F0.wireOp",EDGE,"E12.55.4"),sQuery(id+"F0.wireOp",EDGE,"E12.55.5"),sQuery(id+"F0.wireOp",EDGE,"E12.55.6"),sQuery(id+"F0.wireOp",EDGE,"E12.55.7"),sQuery(id+"F0.wireOp",EDGE,"E12.55.8"),sQuery(id+"F0.wireOp",EDGE,"E12.55.9"),sQuery(id+"F0.wireOp",EDGE,"E12.56.0"),sQuery(id+"F0.wireOp",EDGE,"E12.56.1"),sQuery(id+"F0.wireOp",EDGE,"E12.56.2"),sQuery(id+"F0.wireOp",EDGE,"E12.56.3"),sQuery(id+"F0.wireOp",EDGE,"E12.56.4"),sQuery(id+"F0.wireOp",EDGE,"E12.56.5"),sQuery(id+"F0.wireOp",EDGE,"E12.56.6"),sQuery(id+"F0.wireOp",EDGE,"E12.56.7"),sQuery(id+"F0.wireOp",EDGE,"E12.56.8"),sQuery(id+"F0.wireOp",EDGE,"E12.56.9"),sQuery(id+"F0.wireOp",EDGE,"E12.57.0"),sQuery(id+"F0.wireOp",EDGE,"E12.57.1"),sQuery(id+"F0.wireOp",EDGE,"E12.57.2"),sQuery(id+"F0.wireOp",EDGE,"E12.57.3"),sQuery(id+"F0.wireOp",EDGE,"E12.57.4"),sQuery(id+"F0.wireOp",EDGE,"E12.57.5"),sQuery(id+"F0.wireOp",EDGE,"E12.57.6"),sQuery(id+"F0.wireOp",EDGE,"E12.57.7"),sQuery(id+"F0.wireOp",EDGE,"E12.57.8"),sQuery(id+"F0.wireOp",EDGE,"E12.57.9"),sQuery(id+"F0.wireOp",EDGE,"E12.58.0"),sQuery(id+"F0.wireOp",EDGE,"E12.58.1"),sQuery(id+"F0.wireOp",EDGE,"E12.58.2"),sQuery(id+"F0.wireOp",EDGE,"E12.58.3"),sQuery(id+"F0.wireOp",EDGE,"E12.58.4"),sQuery(id+"F0.wireOp",EDGE,"E12.58.5"),sQuery(id+"F0.wireOp",EDGE,"E12.58.6"),sQuery(id+"F0.wireOp",EDGE,"E12.58.7"),sQuery(id+"F0.wireOp",EDGE,"E12.58.8"),sQuery(id+"F0.wireOp",EDGE,"E12.58.9"),sQuery(id+"F0.wireOp",EDGE,"E12.59.0"),sQuery(id+"F0.wireOp",EDGE,"E12.59.1"),sQuery(id+"F0.wireOp",EDGE,"E12.59.2"),sQuery(id+"F0.wireOp",EDGE,"E12.59.3"),sQuery(id+"F0.wireOp",EDGE,"E12.59.4"),sQuery(id+"F0.wireOp",EDGE,"E12.59.5"),sQuery(id+"F0.wireOp",EDGE,"E12.59.6"),sQuery(id+"F0.wireOp",EDGE,"E12.59.7"),sQuery(id+"F0.wireOp",EDGE,"E12.59.8"),sQuery(id+"F0.wireOp",EDGE,"E12.59.9"),sQuery(id+"F0.wireOp",EDGE,"E13.trimOffspring"),sQuery(id+"F0.wireOp",EDGE,"E14.trimOffspring")])],"isStart":false});
            var sketch = newSketch(context, id + "F6", { "sketchPlane" : qUnion([Q0])});
            skCircle(sketch, "E20", {"center": v(0, 0) * mm, "radius": 12.7 * mm});
            skCircle(sketch, "E21", {"center": v(0, 0) * mm, "radius": 6.35 * mm});
            skSolve(sketch);
        }
        {
            var Q0;
            Q0 = qSketchRegion(id + "F6", true);
            extrude(context, id + "F7", {"entities" : qUnion([Q0]), "operationType" : NewBodyOperationType.ADD, "depth" : 6.35 * mm});
        }
        {
            var Q0;
            Q0=makeQuery(id+"F7.opExtrude","CAP_FACE",FACE,{"disambiguationData":[OSD([sQuery(id+"F6.wireOp",EDGE,"E20"),sQuery(id+"F6.wireOp",EDGE,"E21")])],"isStart":false});
            var sketch = newSketch(context, id + "F8", { "sketchPlane" : qUnion([Q0])});
            skPoint(sketch, "E22", {"position": v(0, 9.4) * mm});
            skPoint(sketch, "E23.1.0", {"position": v(-8.14, 4.7) * mm});
            skPoint(sketch, "E23.2.0", {"position": v(-8.14, -4.7) * mm});
            skPoint(sketch, "E23.3.0", {"position": v(0, -9.4) * mm});
            skPoint(sketch, "E23.4.0", {"position": v(8.14, -4.7) * mm});
            skPoint(sketch, "E23.5.0", {"position": v(8.14, 4.7) * mm});
            skPoint(sketch, "E23.center", {"position": v(0, 0) * mm});
            skSolve(sketch);
        }
        {
            var Q0;
            Q0=sQuery(id+"F8.wireOp",VERTEX,"E22");
            var Q1;
            Q1=sQuery(id+"F8.wireOp",VERTEX,"E23.5.0");
            var Q2;
            Q2=sQuery(id+"F8.wireOp",VERTEX,"E23.4.0");
            var Q3;
            Q3=sQuery(id+"F8.wireOp",VERTEX,"E23.3.0");
            var Q4;
            Q4=sQuery(id+"F8.wireOp",VERTEX,"E23.2.0");
            var Q5;
            Q5=sQuery(id+"F8.wireOp",VERTEX,"E23.1.0");
            var Q6;
            Q6=makeQuery(id+"F1.opExtrude","SWEPT_BODY",BODY,{"disambiguationData":[OSD([sQuery(id+"F0.wireOp",EDGE,"E0"),sQuery(id+"F0.wireOp",EDGE,"E2"),sQuery(id+"F0.wireOp",EDGE,"E3"),sQuery(id+"F0.wireOp",EDGE,"E4.trimOffspring"),sQuery(id+"F0.wireOp",EDGE,"E5.MirrorCS"),sQuery(id+"F0.wireOp",EDGE,"E6.MirrorCS"),sQuery(id+"F0.wireOp",EDGE,"E7.MirrorCS"),sQuery(id+"F0.wireOp",EDGE,"E8.filletArc"),sQuery(id+"F0.wireOp",EDGE,"E9.filletArc"),sQuery(id+"F0.wireOp",EDGE,"E10.filletArc"),sQuery(id+"F0.wireOp",EDGE,"E11.filletArc"),sQuery(id+"F0.wireOp",EDGE,"E12.1.0"),sQuery(id+"F0.wireOp",EDGE,"E12.1.1"),sQuery(id+"F0.wireOp",EDGE,"E12.1.2"),sQuery(id+"F0.wireOp",EDGE,"E12.1.3"),sQuery(id+"F0.wireOp",EDGE,"E12.1.4"),sQuery(id+"F0.wireOp",EDGE,"E12.1.5"),sQuery(id+"F0.wireOp",EDGE,"E12.1.6"),sQuery(id+"F0.wireOp",EDGE,"E12.1.7"),sQuery(id+"F0.wireOp",EDGE,"E12.1.8"),sQuery(id+"F0.wireOp",EDGE,"E12.1.9"),sQuery(id+"F0.wireOp",EDGE,"E12.2.0"),sQuery(id+"F0.wireOp",EDGE,"E12.2.1"),sQuery(id+"F0.wireOp",EDGE,"E12.2.2"),sQuery(id+"F0.wireOp",EDGE,"E12.2.3"),sQuery(id+"F0.wireOp",EDGE,"E12.2.4"),sQuery(id+"F0.wireOp",EDGE,"E12.2.5"),sQuery(id+"F0.wireOp",EDGE,"E12.2.6"),sQuery(id+"F0.wireOp",EDGE,"E12.2.7"),sQuery(id+"F0.wireOp",EDGE,"E12.2.8"),sQuery(id+"F0.wireOp",EDGE,"E12.2.9"),sQuery(id+"F0.wireOp",EDGE,"E12.3.0"),sQuery(id+"F0.wireOp",EDGE,"E12.3.1"),sQuery(id+"F0.wireOp",EDGE,"E12.3.2"),sQuery(id+"F0.wireOp",EDGE,"E12.3.3"),sQuery(id+"F0.wireOp",EDGE,"E12.3.4"),sQuery(id+"F0.wireOp",EDGE,"E12.3.5"),sQuery(id+"F0.wireOp",EDGE,"E12.3.6"),sQuery(id+"F0.wireOp",EDGE,"E12.3.7"),sQuery(id+"F0.wireOp",EDGE,"E12.3.8"),sQuery(id+"F0.wireOp",EDGE,"E12.3.9"),sQuery(id+"F0.wireOp",EDGE,"E12.4.0"),sQuery(id+"F0.wireOp",EDGE,"E12.4.1"),sQuery(id+"F0.wireOp",EDGE,"E12.4.2"),sQuery(id+"F0.wireOp",EDGE,"E12.4.3"),sQuery(id+"F0.wireOp",EDGE,"E12.4.4"),sQuery(id+"F0.wireOp",EDGE,"E12.4.5"),sQuery(id+"F0.wireOp",EDGE,"E12.4.6"),sQuery(id+"F0.wireOp",EDGE,"E12.4.7"),sQuery(id+"F0.wireOp",EDGE,"E12.4.8"),sQuery(id+"F0.wireOp",EDGE,"E12.4.9"),sQuery(id+"F0.wireOp",EDGE,"E12.5.0"),sQuery(id+"F0.wireOp",EDGE,"E12.5.1"),sQuery(id+"F0.wireOp",EDGE,"E12.5.2"),sQuery(id+"F0.wireOp",EDGE,"E12.5.3"),sQuery(id+"F0.wireOp",EDGE,"E12.5.4"),sQuery(id+"F0.wireOp",EDGE,"E12.5.5"),sQuery(id+"F0.wireOp",EDGE,"E12.5.6"),sQuery(id+"F0.wireOp",EDGE,"E12.5.7"),sQuery(id+"F0.wireOp",EDGE,"E12.5.8"),sQuery(id+"F0.wireOp",EDGE,"E12.5.9"),sQuery(id+"F0.wireOp",EDGE,"E12.6.0"),sQuery(id+"F0.wireOp",EDGE,"E12.6.1"),sQuery(id+"F0.wireOp",EDGE,"E12.6.2"),sQuery(id+"F0.wireOp",EDGE,"E12.6.3"),sQuery(id+"F0.wireOp",EDGE,"E12.6.4"),sQuery(id+"F0.wireOp",EDGE,"E12.6.5"),sQuery(id+"F0.wireOp",EDGE,"E12.6.6"),sQuery(id+"F0.wireOp",EDGE,"E12.6.7"),sQuery(id+"F0.wireOp",EDGE,"E12.6.8"),sQuery(id+"F0.wireOp",EDGE,"E12.6.9"),sQuery(id+"F0.wireOp",EDGE,"E12.7.0"),sQuery(id+"F0.wireOp",EDGE,"E12.7.1"),sQuery(id+"F0.wireOp",EDGE,"E12.7.2"),sQuery(id+"F0.wireOp",EDGE,"E12.7.3"),sQuery(id+"F0.wireOp",EDGE,"E12.7.4"),sQuery(id+"F0.wireOp",EDGE,"E12.7.5"),sQuery(id+"F0.wireOp",EDGE,"E12.7.6"),sQuery(id+"F0.wireOp",EDGE,"E12.7.7"),sQuery(id+"F0.wireOp",EDGE,"E12.7.8"),sQuery(id+"F0.wireOp",EDGE,"E12.7.9"),sQuery(id+"F0.wireOp",EDGE,"E12.8.0"),sQuery(id+"F0.wireOp",EDGE,"E12.8.1"),sQuery(id+"F0.wireOp",EDGE,"E12.8.2"),sQuery(id+"F0.wireOp",EDGE,"E12.8.3"),sQuery(id+"F0.wireOp",EDGE,"E12.8.4"),sQuery(id+"F0.wireOp",EDGE,"E12.8.5"),sQuery(id+"F0.wireOp",EDGE,"E12.8.6"),sQuery(id+"F0.wireOp",EDGE,"E12.8.7"),sQuery(id+"F0.wireOp",EDGE,"E12.8.8"),sQuery(id+"F0.wireOp",EDGE,"E12.8.9"),sQuery(id+"F0.wireOp",EDGE,"E12.9.0"),sQuery(id+"F0.wireOp",EDGE,"E12.9.1"),sQuery(id+"F0.wireOp",EDGE,"E12.9.2"),sQuery(id+"F0.wireOp",EDGE,"E12.9.3"),sQuery(id+"F0.wireOp",EDGE,"E12.9.4"),sQuery(id+"F0.wireOp",EDGE,"E12.9.5"),sQuery(id+"F0.wireOp",EDGE,"E12.9.6"),sQuery(id+"F0.wireOp",EDGE,"E12.9.7"),sQuery(id+"F0.wireOp",EDGE,"E12.9.8"),sQuery(id+"F0.wireOp",EDGE,"E12.9.9"),sQuery(id+"F0.wireOp",EDGE,"E12.10.0"),sQuery(id+"F0.wireOp",EDGE,"E12.10.1"),sQuery(id+"F0.wireOp",EDGE,"E12.10.2"),sQuery(id+"F0.wireOp",EDGE,"E12.10.3"),sQuery(id+"F0.wireOp",EDGE,"E12.10.4"),sQuery(id+"F0.wireOp",EDGE,"E12.10.5"),sQuery(id+"F0.wireOp",EDGE,"E12.10.6"),sQuery(id+"F0.wireOp",EDGE,"E12.10.7"),sQuery(id+"F0.wireOp",EDGE,"E12.10.8"),sQuery(id+"F0.wireOp",EDGE,"E12.10.9"),sQuery(id+"F0.wireOp",EDGE,"E12.11.0"),sQuery(id+"F0.wireOp",EDGE,"E12.11.1"),sQuery(id+"F0.wireOp",EDGE,"E12.11.2"),sQuery(id+"F0.wireOp",EDGE,"E12.11.3"),sQuery(id+"F0.wireOp",EDGE,"E12.11.4"),sQuery(id+"F0.wireOp",EDGE,"E12.11.5"),sQuery(id+"F0.wireOp",EDGE,"E12.11.6"),sQuery(id+"F0.wireOp",EDGE,"E12.11.7"),sQuery(id+"F0.wireOp",EDGE,"E12.11.8"),sQuery(id+"F0.wireOp",EDGE,"E12.11.9"),sQuery(id+"F0.wireOp",EDGE,"E12.12.0"),sQuery(id+"F0.wireOp",EDGE,"E12.12.1"),sQuery(id+"F0.wireOp",EDGE,"E12.12.2"),sQuery(id+"F0.wireOp",EDGE,"E12.12.3"),sQuery(id+"F0.wireOp",EDGE,"E12.12.4"),sQuery(id+"F0.wireOp",EDGE,"E12.12.5"),sQuery(id+"F0.wireOp",EDGE,"E12.12.6"),sQuery(id+"F0.wireOp",EDGE,"E12.12.7"),sQuery(id+"F0.wireOp",EDGE,"E12.12.8"),sQuery(id+"F0.wireOp",EDGE,"E12.12.9"),sQuery(id+"F0.wireOp",EDGE,"E12.13.0"),sQuery(id+"F0.wireOp",EDGE,"E12.13.1"),sQuery(id+"F0.wireOp",EDGE,"E12.13.2"),sQuery(id+"F0.wireOp",EDGE,"E12.13.3"),sQuery(id+"F0.wireOp",EDGE,"E12.13.4"),sQuery(id+"F0.wireOp",EDGE,"E12.13.5"),sQuery(id+"F0.wireOp",EDGE,"E12.13.6"),sQuery(id+"F0.wireOp",EDGE,"E12.13.7"),sQuery(id+"F0.wireOp",EDGE,"E12.13.8"),sQuery(id+"F0.wireOp",EDGE,"E12.13.9"),sQuery(id+"F0.wireOp",EDGE,"E12.14.0"),sQuery(id+"F0.wireOp",EDGE,"E12.14.1"),sQuery(id+"F0.wireOp",EDGE,"E12.14.2"),sQuery(id+"F0.wireOp",EDGE,"E12.14.3"),sQuery(id+"F0.wireOp",EDGE,"E12.14.4"),sQuery(id+"F0.wireOp",EDGE,"E12.14.5"),sQuery(id+"F0.wireOp",EDGE,"E12.14.6"),sQuery(id+"F0.wireOp",EDGE,"E12.14.7"),sQuery(id+"F0.wireOp",EDGE,"E12.14.8"),sQuery(id+"F0.wireOp",EDGE,"E12.14.9"),sQuery(id+"F0.wireOp",EDGE,"E12.15.0"),sQuery(id+"F0.wireOp",EDGE,"E12.15.1"),sQuery(id+"F0.wireOp",EDGE,"E12.15.2"),sQuery(id+"F0.wireOp",EDGE,"E12.15.3"),sQuery(id+"F0.wireOp",EDGE,"E12.15.4"),sQuery(id+"F0.wireOp",EDGE,"E12.15.5"),sQuery(id+"F0.wireOp",EDGE,"E12.15.6"),sQuery(id+"F0.wireOp",EDGE,"E12.15.7"),sQuery(id+"F0.wireOp",EDGE,"E12.15.8"),sQuery(id+"F0.wireOp",EDGE,"E12.15.9"),sQuery(id+"F0.wireOp",EDGE,"E12.16.0"),sQuery(id+"F0.wireOp",EDGE,"E12.16.1"),sQuery(id+"F0.wireOp",EDGE,"E12.16.2"),sQuery(id+"F0.wireOp",EDGE,"E12.16.3"),sQuery(id+"F0.wireOp",EDGE,"E12.16.4"),sQuery(id+"F0.wireOp",EDGE,"E12.16.5"),sQuery(id+"F0.wireOp",EDGE,"E12.16.6"),sQuery(id+"F0.wireOp",EDGE,"E12.16.7"),sQuery(id+"F0.wireOp",EDGE,"E12.16.8"),sQuery(id+"F0.wireOp",EDGE,"E12.16.9"),sQuery(id+"F0.wireOp",EDGE,"E12.17.0"),sQuery(id+"F0.wireOp",EDGE,"E12.17.1"),sQuery(id+"F0.wireOp",EDGE,"E12.17.2"),sQuery(id+"F0.wireOp",EDGE,"E12.17.3"),sQuery(id+"F0.wireOp",EDGE,"E12.17.4"),sQuery(id+"F0.wireOp",EDGE,"E12.17.5"),sQuery(id+"F0.wireOp",EDGE,"E12.17.6"),sQuery(id+"F0.wireOp",EDGE,"E12.17.7"),sQuery(id+"F0.wireOp",EDGE,"E12.17.8"),sQuery(id+"F0.wireOp",EDGE,"E12.17.9"),sQuery(id+"F0.wireOp",EDGE,"E12.18.0"),sQuery(id+"F0.wireOp",EDGE,"E12.18.1"),sQuery(id+"F0.wireOp",EDGE,"E12.18.2"),sQuery(id+"F0.wireOp",EDGE,"E12.18.3"),sQuery(id+"F0.wireOp",EDGE,"E12.18.4"),sQuery(id+"F0.wireOp",EDGE,"E12.18.5"),sQuery(id+"F0.wireOp",EDGE,"E12.18.6"),sQuery(id+"F0.wireOp",EDGE,"E12.18.7"),sQuery(id+"F0.wireOp",EDGE,"E12.18.8"),sQuery(id+"F0.wireOp",EDGE,"E12.18.9"),sQuery(id+"F0.wireOp",EDGE,"E12.19.0"),sQuery(id+"F0.wireOp",EDGE,"E12.19.1"),sQuery(id+"F0.wireOp",EDGE,"E12.19.2"),sQuery(id+"F0.wireOp",EDGE,"E12.19.3"),sQuery(id+"F0.wireOp",EDGE,"E12.19.4"),sQuery(id+"F0.wireOp",EDGE,"E12.19.5"),sQuery(id+"F0.wireOp",EDGE,"E12.19.6"),sQuery(id+"F0.wireOp",EDGE,"E12.19.7"),sQuery(id+"F0.wireOp",EDGE,"E12.19.8"),sQuery(id+"F0.wireOp",EDGE,"E12.19.9"),sQuery(id+"F0.wireOp",EDGE,"E12.20.0"),sQuery(id+"F0.wireOp",EDGE,"E12.20.1"),sQuery(id+"F0.wireOp",EDGE,"E12.20.2"),sQuery(id+"F0.wireOp",EDGE,"E12.20.3"),sQuery(id+"F0.wireOp",EDGE,"E12.20.4"),sQuery(id+"F0.wireOp",EDGE,"E12.20.5"),sQuery(id+"F0.wireOp",EDGE,"E12.20.6"),sQuery(id+"F0.wireOp",EDGE,"E12.20.7"),sQuery(id+"F0.wireOp",EDGE,"E12.20.8"),sQuery(id+"F0.wireOp",EDGE,"E12.20.9"),sQuery(id+"F0.wireOp",EDGE,"E12.21.0"),sQuery(id+"F0.wireOp",EDGE,"E12.21.1"),sQuery(id+"F0.wireOp",EDGE,"E12.21.2"),sQuery(id+"F0.wireOp",EDGE,"E12.21.3"),sQuery(id+"F0.wireOp",EDGE,"E12.21.4"),sQuery(id+"F0.wireOp",EDGE,"E12.21.5"),sQuery(id+"F0.wireOp",EDGE,"E12.21.6"),sQuery(id+"F0.wireOp",EDGE,"E12.21.7"),sQuery(id+"F0.wireOp",EDGE,"E12.21.8"),sQuery(id+"F0.wireOp",EDGE,"E12.21.9"),sQuery(id+"F0.wireOp",EDGE,"E12.22.0"),sQuery(id+"F0.wireOp",EDGE,"E12.22.1"),sQuery(id+"F0.wireOp",EDGE,"E12.22.2"),sQuery(id+"F0.wireOp",EDGE,"E12.22.3"),sQuery(id+"F0.wireOp",EDGE,"E12.22.4"),sQuery(id+"F0.wireOp",EDGE,"E12.22.5"),sQuery(id+"F0.wireOp",EDGE,"E12.22.6"),sQuery(id+"F0.wireOp",EDGE,"E12.22.7"),sQuery(id+"F0.wireOp",EDGE,"E12.22.8"),sQuery(id+"F0.wireOp",EDGE,"E12.22.9"),sQuery(id+"F0.wireOp",EDGE,"E12.23.0"),sQuery(id+"F0.wireOp",EDGE,"E12.23.1"),sQuery(id+"F0.wireOp",EDGE,"E12.23.2"),sQuery(id+"F0.wireOp",EDGE,"E12.23.3"),sQuery(id+"F0.wireOp",EDGE,"E12.23.4"),sQuery(id+"F0.wireOp",EDGE,"E12.23.5"),sQuery(id+"F0.wireOp",EDGE,"E12.23.6"),sQuery(id+"F0.wireOp",EDGE,"E12.23.7"),sQuery(id+"F0.wireOp",EDGE,"E12.23.8"),sQuery(id+"F0.wireOp",EDGE,"E12.23.9"),sQuery(id+"F0.wireOp",EDGE,"E12.24.0"),sQuery(id+"F0.wireOp",EDGE,"E12.24.1"),sQuery(id+"F0.wireOp",EDGE,"E12.24.2"),sQuery(id+"F0.wireOp",EDGE,"E12.24.3"),sQuery(id+"F0.wireOp",EDGE,"E12.24.4"),sQuery(id+"F0.wireOp",EDGE,"E12.24.5"),sQuery(id+"F0.wireOp",EDGE,"E12.24.6"),sQuery(id+"F0.wireOp",EDGE,"E12.24.7"),sQuery(id+"F0.wireOp",EDGE,"E12.24.8"),sQuery(id+"F0.wireOp",EDGE,"E12.24.9"),sQuery(id+"F0.wireOp",EDGE,"E12.25.0"),sQuery(id+"F0.wireOp",EDGE,"E12.25.1"),sQuery(id+"F0.wireOp",EDGE,"E12.25.2"),sQuery(id+"F0.wireOp",EDGE,"E12.25.3"),sQuery(id+"F0.wireOp",EDGE,"E12.25.4"),sQuery(id+"F0.wireOp",EDGE,"E12.25.5"),sQuery(id+"F0.wireOp",EDGE,"E12.25.6"),sQuery(id+"F0.wireOp",EDGE,"E12.25.7"),sQuery(id+"F0.wireOp",EDGE,"E12.25.8"),sQuery(id+"F0.wireOp",EDGE,"E12.25.9"),sQuery(id+"F0.wireOp",EDGE,"E12.26.0"),sQuery(id+"F0.wireOp",EDGE,"E12.26.1"),sQuery(id+"F0.wireOp",EDGE,"E12.26.2"),sQuery(id+"F0.wireOp",EDGE,"E12.26.3"),sQuery(id+"F0.wireOp",EDGE,"E12.26.4"),sQuery(id+"F0.wireOp",EDGE,"E12.26.5"),sQuery(id+"F0.wireOp",EDGE,"E12.26.6"),sQuery(id+"F0.wireOp",EDGE,"E12.26.7"),sQuery(id+"F0.wireOp",EDGE,"E12.26.8"),sQuery(id+"F0.wireOp",EDGE,"E12.26.9"),sQuery(id+"F0.wireOp",EDGE,"E12.27.0"),sQuery(id+"F0.wireOp",EDGE,"E12.27.1"),sQuery(id+"F0.wireOp",EDGE,"E12.27.2"),sQuery(id+"F0.wireOp",EDGE,"E12.27.3"),sQuery(id+"F0.wireOp",EDGE,"E12.27.4"),sQuery(id+"F0.wireOp",EDGE,"E12.27.5"),sQuery(id+"F0.wireOp",EDGE,"E12.27.6"),sQuery(id+"F0.wireOp",EDGE,"E12.27.7"),sQuery(id+"F0.wireOp",EDGE,"E12.27.8"),sQuery(id+"F0.wireOp",EDGE,"E12.27.9"),sQuery(id+"F0.wireOp",EDGE,"E12.28.0"),sQuery(id+"F0.wireOp",EDGE,"E12.28.1"),sQuery(id+"F0.wireOp",EDGE,"E12.28.2"),sQuery(id+"F0.wireOp",EDGE,"E12.28.3"),sQuery(id+"F0.wireOp",EDGE,"E12.28.4"),sQuery(id+"F0.wireOp",EDGE,"E12.28.5"),sQuery(id+"F0.wireOp",EDGE,"E12.28.6"),sQuery(id+"F0.wireOp",EDGE,"E12.28.7"),sQuery(id+"F0.wireOp",EDGE,"E12.28.8"),sQuery(id+"F0.wireOp",EDGE,"E12.28.9"),sQuery(id+"F0.wireOp",EDGE,"E12.29.0"),sQuery(id+"F0.wireOp",EDGE,"E12.29.1"),sQuery(id+"F0.wireOp",EDGE,"E12.29.2"),sQuery(id+"F0.wireOp",EDGE,"E12.29.3"),sQuery(id+"F0.wireOp",EDGE,"E12.29.4"),sQuery(id+"F0.wireOp",EDGE,"E12.29.5"),sQuery(id+"F0.wireOp",EDGE,"E12.29.6"),sQuery(id+"F0.wireOp",EDGE,"E12.29.7"),sQuery(id+"F0.wireOp",EDGE,"E12.29.8"),sQuery(id+"F0.wireOp",EDGE,"E12.29.9"),sQuery(id+"F0.wireOp",EDGE,"E12.30.0"),sQuery(id+"F0.wireOp",EDGE,"E12.30.1"),sQuery(id+"F0.wireOp",EDGE,"E12.30.2"),sQuery(id+"F0.wireOp",EDGE,"E12.30.3"),sQuery(id+"F0.wireOp",EDGE,"E12.30.4"),sQuery(id+"F0.wireOp",EDGE,"E12.30.5"),sQuery(id+"F0.wireOp",EDGE,"E12.30.6"),sQuery(id+"F0.wireOp",EDGE,"E12.30.7"),sQuery(id+"F0.wireOp",EDGE,"E12.30.8"),sQuery(id+"F0.wireOp",EDGE,"E12.30.9"),sQuery(id+"F0.wireOp",EDGE,"E12.31.0"),sQuery(id+"F0.wireOp",EDGE,"E12.31.1"),sQuery(id+"F0.wireOp",EDGE,"E12.31.2"),sQuery(id+"F0.wireOp",EDGE,"E12.31.3"),sQuery(id+"F0.wireOp",EDGE,"E12.31.4"),sQuery(id+"F0.wireOp",EDGE,"E12.31.5"),sQuery(id+"F0.wireOp",EDGE,"E12.31.6"),sQuery(id+"F0.wireOp",EDGE,"E12.31.7"),sQuery(id+"F0.wireOp",EDGE,"E12.31.8"),sQuery(id+"F0.wireOp",EDGE,"E12.31.9"),sQuery(id+"F0.wireOp",EDGE,"E12.32.0"),sQuery(id+"F0.wireOp",EDGE,"E12.32.1"),sQuery(id+"F0.wireOp",EDGE,"E12.32.2"),sQuery(id+"F0.wireOp",EDGE,"E12.32.3"),sQuery(id+"F0.wireOp",EDGE,"E12.32.4"),sQuery(id+"F0.wireOp",EDGE,"E12.32.5"),sQuery(id+"F0.wireOp",EDGE,"E12.32.6"),sQuery(id+"F0.wireOp",EDGE,"E12.32.7"),sQuery(id+"F0.wireOp",EDGE,"E12.32.8"),sQuery(id+"F0.wireOp",EDGE,"E12.32.9"),sQuery(id+"F0.wireOp",EDGE,"E12.33.0"),sQuery(id+"F0.wireOp",EDGE,"E12.33.1"),sQuery(id+"F0.wireOp",EDGE,"E12.33.2"),sQuery(id+"F0.wireOp",EDGE,"E12.33.3"),sQuery(id+"F0.wireOp",EDGE,"E12.33.4"),sQuery(id+"F0.wireOp",EDGE,"E12.33.5"),sQuery(id+"F0.wireOp",EDGE,"E12.33.6"),sQuery(id+"F0.wireOp",EDGE,"E12.33.7"),sQuery(id+"F0.wireOp",EDGE,"E12.33.8"),sQuery(id+"F0.wireOp",EDGE,"E12.33.9"),sQuery(id+"F0.wireOp",EDGE,"E12.34.0"),sQuery(id+"F0.wireOp",EDGE,"E12.34.1"),sQuery(id+"F0.wireOp",EDGE,"E12.34.2"),sQuery(id+"F0.wireOp",EDGE,"E12.34.3"),sQuery(id+"F0.wireOp",EDGE,"E12.34.4"),sQuery(id+"F0.wireOp",EDGE,"E12.34.5"),sQuery(id+"F0.wireOp",EDGE,"E12.34.6"),sQuery(id+"F0.wireOp",EDGE,"E12.34.7"),sQuery(id+"F0.wireOp",EDGE,"E12.34.8"),sQuery(id+"F0.wireOp",EDGE,"E12.34.9"),sQuery(id+"F0.wireOp",EDGE,"E12.35.0"),sQuery(id+"F0.wireOp",EDGE,"E12.35.1"),sQuery(id+"F0.wireOp",EDGE,"E12.35.2"),sQuery(id+"F0.wireOp",EDGE,"E12.35.3"),sQuery(id+"F0.wireOp",EDGE,"E12.35.4"),sQuery(id+"F0.wireOp",EDGE,"E12.35.5"),sQuery(id+"F0.wireOp",EDGE,"E12.35.6"),sQuery(id+"F0.wireOp",EDGE,"E12.35.7"),sQuery(id+"F0.wireOp",EDGE,"E12.35.8"),sQuery(id+"F0.wireOp",EDGE,"E12.35.9"),sQuery(id+"F0.wireOp",EDGE,"E12.36.0"),sQuery(id+"F0.wireOp",EDGE,"E12.36.1"),sQuery(id+"F0.wireOp",EDGE,"E12.36.2"),sQuery(id+"F0.wireOp",EDGE,"E12.36.3"),sQuery(id+"F0.wireOp",EDGE,"E12.36.4"),sQuery(id+"F0.wireOp",EDGE,"E12.36.5"),sQuery(id+"F0.wireOp",EDGE,"E12.36.6"),sQuery(id+"F0.wireOp",EDGE,"E12.36.7"),sQuery(id+"F0.wireOp",EDGE,"E12.36.8"),sQuery(id+"F0.wireOp",EDGE,"E12.36.9"),sQuery(id+"F0.wireOp",EDGE,"E12.37.0"),sQuery(id+"F0.wireOp",EDGE,"E12.37.1"),sQuery(id+"F0.wireOp",EDGE,"E12.37.2"),sQuery(id+"F0.wireOp",EDGE,"E12.37.3"),sQuery(id+"F0.wireOp",EDGE,"E12.37.4"),sQuery(id+"F0.wireOp",EDGE,"E12.37.5"),sQuery(id+"F0.wireOp",EDGE,"E12.37.6"),sQuery(id+"F0.wireOp",EDGE,"E12.37.7"),sQuery(id+"F0.wireOp",EDGE,"E12.37.8"),sQuery(id+"F0.wireOp",EDGE,"E12.37.9"),sQuery(id+"F0.wireOp",EDGE,"E12.38.0"),sQuery(id+"F0.wireOp",EDGE,"E12.38.1"),sQuery(id+"F0.wireOp",EDGE,"E12.38.2"),sQuery(id+"F0.wireOp",EDGE,"E12.38.3"),sQuery(id+"F0.wireOp",EDGE,"E12.38.4"),sQuery(id+"F0.wireOp",EDGE,"E12.38.5"),sQuery(id+"F0.wireOp",EDGE,"E12.38.6"),sQuery(id+"F0.wireOp",EDGE,"E12.38.7"),sQuery(id+"F0.wireOp",EDGE,"E12.38.8"),sQuery(id+"F0.wireOp",EDGE,"E12.38.9"),sQuery(id+"F0.wireOp",EDGE,"E12.39.0"),sQuery(id+"F0.wireOp",EDGE,"E12.39.1"),sQuery(id+"F0.wireOp",EDGE,"E12.39.2"),sQuery(id+"F0.wireOp",EDGE,"E12.39.3"),sQuery(id+"F0.wireOp",EDGE,"E12.39.4"),sQuery(id+"F0.wireOp",EDGE,"E12.39.5"),sQuery(id+"F0.wireOp",EDGE,"E12.39.6"),sQuery(id+"F0.wireOp",EDGE,"E12.39.7"),sQuery(id+"F0.wireOp",EDGE,"E12.39.8"),sQuery(id+"F0.wireOp",EDGE,"E12.39.9"),sQuery(id+"F0.wireOp",EDGE,"E12.40.0"),sQuery(id+"F0.wireOp",EDGE,"E12.40.1"),sQuery(id+"F0.wireOp",EDGE,"E12.40.2"),sQuery(id+"F0.wireOp",EDGE,"E12.40.3"),sQuery(id+"F0.wireOp",EDGE,"E12.40.4"),sQuery(id+"F0.wireOp",EDGE,"E12.40.5"),sQuery(id+"F0.wireOp",EDGE,"E12.40.6"),sQuery(id+"F0.wireOp",EDGE,"E12.40.7"),sQuery(id+"F0.wireOp",EDGE,"E12.40.8"),sQuery(id+"F0.wireOp",EDGE,"E12.40.9"),sQuery(id+"F0.wireOp",EDGE,"E12.41.0"),sQuery(id+"F0.wireOp",EDGE,"E12.41.1"),sQuery(id+"F0.wireOp",EDGE,"E12.41.2"),sQuery(id+"F0.wireOp",EDGE,"E12.41.3"),sQuery(id+"F0.wireOp",EDGE,"E12.41.4"),sQuery(id+"F0.wireOp",EDGE,"E12.41.5"),sQuery(id+"F0.wireOp",EDGE,"E12.41.6"),sQuery(id+"F0.wireOp",EDGE,"E12.41.7"),sQuery(id+"F0.wireOp",EDGE,"E12.41.8"),sQuery(id+"F0.wireOp",EDGE,"E12.41.9"),sQuery(id+"F0.wireOp",EDGE,"E12.42.0"),sQuery(id+"F0.wireOp",EDGE,"E12.42.1"),sQuery(id+"F0.wireOp",EDGE,"E12.42.2"),sQuery(id+"F0.wireOp",EDGE,"E12.42.3"),sQuery(id+"F0.wireOp",EDGE,"E12.42.4"),sQuery(id+"F0.wireOp",EDGE,"E12.42.5"),sQuery(id+"F0.wireOp",EDGE,"E12.42.6"),sQuery(id+"F0.wireOp",EDGE,"E12.42.7"),sQuery(id+"F0.wireOp",EDGE,"E12.42.8"),sQuery(id+"F0.wireOp",EDGE,"E12.42.9"),sQuery(id+"F0.wireOp",EDGE,"E12.43.0"),sQuery(id+"F0.wireOp",EDGE,"E12.43.1"),sQuery(id+"F0.wireOp",EDGE,"E12.43.2"),sQuery(id+"F0.wireOp",EDGE,"E12.43.3"),sQuery(id+"F0.wireOp",EDGE,"E12.43.4"),sQuery(id+"F0.wireOp",EDGE,"E12.43.5"),sQuery(id+"F0.wireOp",EDGE,"E12.43.6"),sQuery(id+"F0.wireOp",EDGE,"E12.43.7"),sQuery(id+"F0.wireOp",EDGE,"E12.43.8"),sQuery(id+"F0.wireOp",EDGE,"E12.43.9"),sQuery(id+"F0.wireOp",EDGE,"E12.44.0"),sQuery(id+"F0.wireOp",EDGE,"E12.44.1"),sQuery(id+"F0.wireOp",EDGE,"E12.44.2"),sQuery(id+"F0.wireOp",EDGE,"E12.44.3"),sQuery(id+"F0.wireOp",EDGE,"E12.44.4"),sQuery(id+"F0.wireOp",EDGE,"E12.44.5"),sQuery(id+"F0.wireOp",EDGE,"E12.44.6"),sQuery(id+"F0.wireOp",EDGE,"E12.44.7"),sQuery(id+"F0.wireOp",EDGE,"E12.44.8"),sQuery(id+"F0.wireOp",EDGE,"E12.44.9"),sQuery(id+"F0.wireOp",EDGE,"E12.45.0"),sQuery(id+"F0.wireOp",EDGE,"E12.45.1"),sQuery(id+"F0.wireOp",EDGE,"E12.45.2"),sQuery(id+"F0.wireOp",EDGE,"E12.45.3"),sQuery(id+"F0.wireOp",EDGE,"E12.45.4"),sQuery(id+"F0.wireOp",EDGE,"E12.45.5"),sQuery(id+"F0.wireOp",EDGE,"E12.45.6"),sQuery(id+"F0.wireOp",EDGE,"E12.45.7"),sQuery(id+"F0.wireOp",EDGE,"E12.45.8"),sQuery(id+"F0.wireOp",EDGE,"E12.45.9"),sQuery(id+"F0.wireOp",EDGE,"E12.46.0"),sQuery(id+"F0.wireOp",EDGE,"E12.46.1"),sQuery(id+"F0.wireOp",EDGE,"E12.46.2"),sQuery(id+"F0.wireOp",EDGE,"E12.46.3"),sQuery(id+"F0.wireOp",EDGE,"E12.46.4"),sQuery(id+"F0.wireOp",EDGE,"E12.46.5"),sQuery(id+"F0.wireOp",EDGE,"E12.46.6"),sQuery(id+"F0.wireOp",EDGE,"E12.46.7"),sQuery(id+"F0.wireOp",EDGE,"E12.46.8"),sQuery(id+"F0.wireOp",EDGE,"E12.46.9"),sQuery(id+"F0.wireOp",EDGE,"E12.47.0"),sQuery(id+"F0.wireOp",EDGE,"E12.47.1"),sQuery(id+"F0.wireOp",EDGE,"E12.47.2"),sQuery(id+"F0.wireOp",EDGE,"E12.47.3"),sQuery(id+"F0.wireOp",EDGE,"E12.47.4"),sQuery(id+"F0.wireOp",EDGE,"E12.47.5"),sQuery(id+"F0.wireOp",EDGE,"E12.47.6"),sQuery(id+"F0.wireOp",EDGE,"E12.47.7"),sQuery(id+"F0.wireOp",EDGE,"E12.47.8"),sQuery(id+"F0.wireOp",EDGE,"E12.47.9"),sQuery(id+"F0.wireOp",EDGE,"E12.48.0"),sQuery(id+"F0.wireOp",EDGE,"E12.48.1"),sQuery(id+"F0.wireOp",EDGE,"E12.48.2"),sQuery(id+"F0.wireOp",EDGE,"E12.48.3"),sQuery(id+"F0.wireOp",EDGE,"E12.48.4"),sQuery(id+"F0.wireOp",EDGE,"E12.48.5"),sQuery(id+"F0.wireOp",EDGE,"E12.48.6"),sQuery(id+"F0.wireOp",EDGE,"E12.48.7"),sQuery(id+"F0.wireOp",EDGE,"E12.48.8"),sQuery(id+"F0.wireOp",EDGE,"E12.48.9"),sQuery(id+"F0.wireOp",EDGE,"E12.49.0"),sQuery(id+"F0.wireOp",EDGE,"E12.49.1"),sQuery(id+"F0.wireOp",EDGE,"E12.49.2"),sQuery(id+"F0.wireOp",EDGE,"E12.49.3"),sQuery(id+"F0.wireOp",EDGE,"E12.49.4"),sQuery(id+"F0.wireOp",EDGE,"E12.49.5"),sQuery(id+"F0.wireOp",EDGE,"E12.49.6"),sQuery(id+"F0.wireOp",EDGE,"E12.49.7"),sQuery(id+"F0.wireOp",EDGE,"E12.49.8"),sQuery(id+"F0.wireOp",EDGE,"E12.49.9"),sQuery(id+"F0.wireOp",EDGE,"E12.50.0"),sQuery(id+"F0.wireOp",EDGE,"E12.50.1"),sQuery(id+"F0.wireOp",EDGE,"E12.50.2"),sQuery(id+"F0.wireOp",EDGE,"E12.50.3"),sQuery(id+"F0.wireOp",EDGE,"E12.50.4"),sQuery(id+"F0.wireOp",EDGE,"E12.50.5"),sQuery(id+"F0.wireOp",EDGE,"E12.50.6"),sQuery(id+"F0.wireOp",EDGE,"E12.50.7"),sQuery(id+"F0.wireOp",EDGE,"E12.50.8"),sQuery(id+"F0.wireOp",EDGE,"E12.50.9"),sQuery(id+"F0.wireOp",EDGE,"E12.51.0"),sQuery(id+"F0.wireOp",EDGE,"E12.51.1"),sQuery(id+"F0.wireOp",EDGE,"E12.51.2"),sQuery(id+"F0.wireOp",EDGE,"E12.51.3"),sQuery(id+"F0.wireOp",EDGE,"E12.51.4"),sQuery(id+"F0.wireOp",EDGE,"E12.51.5"),sQuery(id+"F0.wireOp",EDGE,"E12.51.6"),sQuery(id+"F0.wireOp",EDGE,"E12.51.7"),sQuery(id+"F0.wireOp",EDGE,"E12.51.8"),sQuery(id+"F0.wireOp",EDGE,"E12.51.9"),sQuery(id+"F0.wireOp",EDGE,"E12.52.0"),sQuery(id+"F0.wireOp",EDGE,"E12.52.1"),sQuery(id+"F0.wireOp",EDGE,"E12.52.2"),sQuery(id+"F0.wireOp",EDGE,"E12.52.3"),sQuery(id+"F0.wireOp",EDGE,"E12.52.4"),sQuery(id+"F0.wireOp",EDGE,"E12.52.5"),sQuery(id+"F0.wireOp",EDGE,"E12.52.6"),sQuery(id+"F0.wireOp",EDGE,"E12.52.7"),sQuery(id+"F0.wireOp",EDGE,"E12.52.8"),sQuery(id+"F0.wireOp",EDGE,"E12.52.9"),sQuery(id+"F0.wireOp",EDGE,"E12.53.0"),sQuery(id+"F0.wireOp",EDGE,"E12.53.1"),sQuery(id+"F0.wireOp",EDGE,"E12.53.2"),sQuery(id+"F0.wireOp",EDGE,"E12.53.3"),sQuery(id+"F0.wireOp",EDGE,"E12.53.4"),sQuery(id+"F0.wireOp",EDGE,"E12.53.5"),sQuery(id+"F0.wireOp",EDGE,"E12.53.6"),sQuery(id+"F0.wireOp",EDGE,"E12.53.7"),sQuery(id+"F0.wireOp",EDGE,"E12.53.8"),sQuery(id+"F0.wireOp",EDGE,"E12.53.9"),sQuery(id+"F0.wireOp",EDGE,"E12.54.0"),sQuery(id+"F0.wireOp",EDGE,"E12.54.1"),sQuery(id+"F0.wireOp",EDGE,"E12.54.2"),sQuery(id+"F0.wireOp",EDGE,"E12.54.3"),sQuery(id+"F0.wireOp",EDGE,"E12.54.4"),sQuery(id+"F0.wireOp",EDGE,"E12.54.5"),sQuery(id+"F0.wireOp",EDGE,"E12.54.6"),sQuery(id+"F0.wireOp",EDGE,"E12.54.7"),sQuery(id+"F0.wireOp",EDGE,"E12.54.8"),sQuery(id+"F0.wireOp",EDGE,"E12.54.9"),sQuery(id+"F0.wireOp",EDGE,"E12.55.0"),sQuery(id+"F0.wireOp",EDGE,"E12.55.1"),sQuery(id+"F0.wireOp",EDGE,"E12.55.2"),sQuery(id+"F0.wireOp",EDGE,"E12.55.3"),sQuery(id+"F0.wireOp",EDGE,"E12.55.4"),sQuery(id+"F0.wireOp",EDGE,"E12.55.5"),sQuery(id+"F0.wireOp",EDGE,"E12.55.6"),sQuery(id+"F0.wireOp",EDGE,"E12.55.7"),sQuery(id+"F0.wireOp",EDGE,"E12.55.8"),sQuery(id+"F0.wireOp",EDGE,"E12.55.9"),sQuery(id+"F0.wireOp",EDGE,"E12.56.0"),sQuery(id+"F0.wireOp",EDGE,"E12.56.1"),sQuery(id+"F0.wireOp",EDGE,"E12.56.2"),sQuery(id+"F0.wireOp",EDGE,"E12.56.3"),sQuery(id+"F0.wireOp",EDGE,"E12.56.4"),sQuery(id+"F0.wireOp",EDGE,"E12.56.5"),sQuery(id+"F0.wireOp",EDGE,"E12.56.6"),sQuery(id+"F0.wireOp",EDGE,"E12.56.7"),sQuery(id+"F0.wireOp",EDGE,"E12.56.8"),sQuery(id+"F0.wireOp",EDGE,"E12.56.9"),sQuery(id+"F0.wireOp",EDGE,"E12.57.0"),sQuery(id+"F0.wireOp",EDGE,"E12.57.1"),sQuery(id+"F0.wireOp",EDGE,"E12.57.2"),sQuery(id+"F0.wireOp",EDGE,"E12.57.3"),sQuery(id+"F0.wireOp",EDGE,"E12.57.4"),sQuery(id+"F0.wireOp",EDGE,"E12.57.5"),sQuery(id+"F0.wireOp",EDGE,"E12.57.6"),sQuery(id+"F0.wireOp",EDGE,"E12.57.7"),sQuery(id+"F0.wireOp",EDGE,"E12.57.8"),sQuery(id+"F0.wireOp",EDGE,"E12.57.9"),sQuery(id+"F0.wireOp",EDGE,"E12.58.0"),sQuery(id+"F0.wireOp",EDGE,"E12.58.1"),sQuery(id+"F0.wireOp",EDGE,"E12.58.2"),sQuery(id+"F0.wireOp",EDGE,"E12.58.3"),sQuery(id+"F0.wireOp",EDGE,"E12.58.4"),sQuery(id+"F0.wireOp",EDGE,"E12.58.5"),sQuery(id+"F0.wireOp",EDGE,"E12.58.6"),sQuery(id+"F0.wireOp",EDGE,"E12.58.7"),sQuery(id+"F0.wireOp",EDGE,"E12.58.8"),sQuery(id+"F0.wireOp",EDGE,"E12.58.9"),sQuery(id+"F0.wireOp",EDGE,"E12.59.0"),sQuery(id+"F0.wireOp",EDGE,"E12.59.1"),sQuery(id+"F0.wireOp",EDGE,"E12.59.2"),sQuery(id+"F0.wireOp",EDGE,"E12.59.3"),sQuery(id+"F0.wireOp",EDGE,"E12.59.4"),sQuery(id+"F0.wireOp",EDGE,"E12.59.5"),sQuery(id+"F0.wireOp",EDGE,"E12.59.6"),sQuery(id+"F0.wireOp",EDGE,"E12.59.7"),sQuery(id+"F0.wireOp",EDGE,"E12.59.8"),sQuery(id+"F0.wireOp",EDGE,"E12.59.9"),sQuery(id+"F0.wireOp",EDGE,"E13.trimOffspring"),sQuery(id+"F0.wireOp",EDGE,"E14.trimOffspring")])]});
            hole(context, id + "F9", {"style" : HoleStyle.C_BORE, "endStyle" : HoleEndStyle.THROUGH, "holeDiameter" : 3.17 * mm, "cBoreDiameter" : 4.44 * mm, "cBoreDepth" : 3.17 * mm, "locations" : qUnion([Q0, Q1, Q2, Q3, Q4, Q5]), "scope" : qUnion([Q6]), "isTappedThrough" : true});
        }
        {
            var Q0;
            Q0=makeQuery(id+"F3.boolean.opBoolean","COPY",EDGE,{"derivedFrom":makeQuery(id+"F3.opExtrude","CAP_EDGE",EDGE,{"disambiguationData":[OSD([sQuery(id+"F2.wireOp",EDGE,"E17.1.0")])],"isStart":true})});
            var Q1;
            Q1=makeQuery(id+"F3.boolean.opBoolean","COPY",EDGE,{"derivedFrom":makeQuery(id+"F3.opExtrude","CAP_EDGE",EDGE,{"disambiguationData":[OSD([sQuery(id+"F2.wireOp",EDGE,"E15")])],"isStart":true})});
            var Q2;
            Q2=makeQuery(id+"F3.boolean.opBoolean","COPY",EDGE,{"derivedFrom":makeQuery(id+"F3.opExtrude","CAP_EDGE",EDGE,{"disambiguationData":[OSD([sQuery(id+"F2.wireOp",EDGE,"E17.7.0")])],"isStart":true})});
            var Q3;
            Q3=makeQuery(id+"F3.boolean.opBoolean","COPY",EDGE,{"derivedFrom":makeQuery(id+"F3.opExtrude","CAP_EDGE",EDGE,{"disambiguationData":[OSD([sQuery(id+"F2.wireOp",EDGE,"E17.6.0")])],"isStart":true})});
            var Q4;
            Q4=makeQuery(id+"F3.boolean.opBoolean","COPY",EDGE,{"derivedFrom":makeQuery(id+"F3.opExtrude","CAP_EDGE",EDGE,{"disambiguationData":[OSD([sQuery(id+"F2.wireOp",EDGE,"E17.5.0")])],"isStart":true})});
            var Q5;
            Q5=makeQuery(id+"F3.boolean.opBoolean","COPY",EDGE,{"derivedFrom":makeQuery(id+"F3.opExtrude","CAP_EDGE",EDGE,{"disambiguationData":[OSD([sQuery(id+"F2.wireOp",EDGE,"E17.4.0")])],"isStart":true})});
            var Q6;
            Q6=makeQuery(id+"F3.boolean.opBoolean","COPY",EDGE,{"derivedFrom":makeQuery(id+"F3.opExtrude","CAP_EDGE",EDGE,{"disambiguationData":[OSD([sQuery(id+"F2.wireOp",EDGE,"E17.3.0")])],"isStart":true})});
            var Q7;
            Q7=makeQuery(id+"F3.boolean.opBoolean","COPY",EDGE,{"derivedFrom":makeQuery(id+"F3.opExtrude","CAP_EDGE",EDGE,{"disambiguationData":[OSD([sQuery(id+"F2.wireOp",EDGE,"E17.2.0")])],"isStart":true})});
            var Q8;
            Q8=makeQuery(id+"F3.boolean.opBoolean","INTERSECT",EDGE,{"derivedFrom":[makeQuery(id+"F1.opExtrude","CAP_FACE",FACE,{"disambiguationData":[OSD([sQuery(id+"F0.wireOp",EDGE,"E0"),sQuery(id+"F0.wireOp",EDGE,"E2"),sQuery(id+"F0.wireOp",EDGE,"E3"),sQuery(id+"F0.wireOp",EDGE,"E4.trimOffspring"),sQuery(id+"F0.wireOp",EDGE,"E5.MirrorCS"),sQuery(id+"F0.wireOp",EDGE,"E6.MirrorCS"),sQuery(id+"F0.wireOp",EDGE,"E7.MirrorCS"),sQuery(id+"F0.wireOp",EDGE,"E8.filletArc"),sQuery(id+"F0.wireOp",EDGE,"E9.filletArc"),sQuery(id+"F0.wireOp",EDGE,"E10.filletArc"),sQuery(id+"F0.wireOp",EDGE,"E11.filletArc"),sQuery(id+"F0.wireOp",EDGE,"E12.1.0"),sQuery(id+"F0.wireOp",EDGE,"E12.1.1"),sQuery(id+"F0.wireOp",EDGE,"E12.1.2"),sQuery(id+"F0.wireOp",EDGE,"E12.1.3"),sQuery(id+"F0.wireOp",EDGE,"E12.1.4"),sQuery(id+"F0.wireOp",EDGE,"E12.1.5"),sQuery(id+"F0.wireOp",EDGE,"E12.1.6"),sQuery(id+"F0.wireOp",EDGE,"E12.1.7"),sQuery(id+"F0.wireOp",EDGE,"E12.1.8"),sQuery(id+"F0.wireOp",EDGE,"E12.1.9"),sQuery(id+"F0.wireOp",EDGE,"E12.2.0"),sQuery(id+"F0.wireOp",EDGE,"E12.2.1"),sQuery(id+"F0.wireOp",EDGE,"E12.2.2"),sQuery(id+"F0.wireOp",EDGE,"E12.2.3"),sQuery(id+"F0.wireOp",EDGE,"E12.2.4"),sQuery(id+"F0.wireOp",EDGE,"E12.2.5"),sQuery(id+"F0.wireOp",EDGE,"E12.2.6"),sQuery(id+"F0.wireOp",EDGE,"E12.2.7"),sQuery(id+"F0.wireOp",EDGE,"E12.2.8"),sQuery(id+"F0.wireOp",EDGE,"E12.2.9"),sQuery(id+"F0.wireOp",EDGE,"E12.3.0"),sQuery(id+"F0.wireOp",EDGE,"E12.3.1"),sQuery(id+"F0.wireOp",EDGE,"E12.3.2"),sQuery(id+"F0.wireOp",EDGE,"E12.3.3"),sQuery(id+"F0.wireOp",EDGE,"E12.3.4"),sQuery(id+"F0.wireOp",EDGE,"E12.3.5"),sQuery(id+"F0.wireOp",EDGE,"E12.3.6"),sQuery(id+"F0.wireOp",EDGE,"E12.3.7"),sQuery(id+"F0.wireOp",EDGE,"E12.3.8"),sQuery(id+"F0.wireOp",EDGE,"E12.3.9"),sQuery(id+"F0.wireOp",EDGE,"E12.4.0"),sQuery(id+"F0.wireOp",EDGE,"E12.4.1"),sQuery(id+"F0.wireOp",EDGE,"E12.4.2"),sQuery(id+"F0.wireOp",EDGE,"E12.4.3"),sQuery(id+"F0.wireOp",EDGE,"E12.4.4"),sQuery(id+"F0.wireOp",EDGE,"E12.4.5"),sQuery(id+"F0.wireOp",EDGE,"E12.4.6"),sQuery(id+"F0.wireOp",EDGE,"E12.4.7"),sQuery(id+"F0.wireOp",EDGE,"E12.4.8"),sQuery(id+"F0.wireOp",EDGE,"E12.4.9"),sQuery(id+"F0.wireOp",EDGE,"E12.5.0"),sQuery(id+"F0.wireOp",EDGE,"E12.5.1"),sQuery(id+"F0.wireOp",EDGE,"E12.5.2"),sQuery(id+"F0.wireOp",EDGE,"E12.5.3"),sQuery(id+"F0.wireOp",EDGE,"E12.5.4"),sQuery(id+"F0.wireOp",EDGE,"E12.5.5"),sQuery(id+"F0.wireOp",EDGE,"E12.5.6"),sQuery(id+"F0.wireOp",EDGE,"E12.5.7"),sQuery(id+"F0.wireOp",EDGE,"E12.5.8"),sQuery(id+"F0.wireOp",EDGE,"E12.5.9"),sQuery(id+"F0.wireOp",EDGE,"E12.6.0"),sQuery(id+"F0.wireOp",EDGE,"E12.6.1"),sQuery(id+"F0.wireOp",EDGE,"E12.6.2"),sQuery(id+"F0.wireOp",EDGE,"E12.6.3"),sQuery(id+"F0.wireOp",EDGE,"E12.6.4"),sQuery(id+"F0.wireOp",EDGE,"E12.6.5"),sQuery(id+"F0.wireOp",EDGE,"E12.6.6"),sQuery(id+"F0.wireOp",EDGE,"E12.6.7"),sQuery(id+"F0.wireOp",EDGE,"E12.6.8"),sQuery(id+"F0.wireOp",EDGE,"E12.6.9"),sQuery(id+"F0.wireOp",EDGE,"E12.7.0"),sQuery(id+"F0.wireOp",EDGE,"E12.7.1"),sQuery(id+"F0.wireOp",EDGE,"E12.7.2"),sQuery(id+"F0.wireOp",EDGE,"E12.7.3"),sQuery(id+"F0.wireOp",EDGE,"E12.7.4"),sQuery(id+"F0.wireOp",EDGE,"E12.7.5"),sQuery(id+"F0.wireOp",EDGE,"E12.7.6"),sQuery(id+"F0.wireOp",EDGE,"E12.7.7"),sQuery(id+"F0.wireOp",EDGE,"E12.7.8"),sQuery(id+"F0.wireOp",EDGE,"E12.7.9"),sQuery(id+"F0.wireOp",EDGE,"E12.8.0"),sQuery(id+"F0.wireOp",EDGE,"E12.8.1"),sQuery(id+"F0.wireOp",EDGE,"E12.8.2"),sQuery(id+"F0.wireOp",EDGE,"E12.8.3"),sQuery(id+"F0.wireOp",EDGE,"E12.8.4"),sQuery(id+"F0.wireOp",EDGE,"E12.8.5"),sQuery(id+"F0.wireOp",EDGE,"E12.8.6"),sQuery(id+"F0.wireOp",EDGE,"E12.8.7"),sQuery(id+"F0.wireOp",EDGE,"E12.8.8"),sQuery(id+"F0.wireOp",EDGE,"E12.8.9"),sQuery(id+"F0.wireOp",EDGE,"E12.9.0"),sQuery(id+"F0.wireOp",EDGE,"E12.9.1"),sQuery(id+"F0.wireOp",EDGE,"E12.9.2"),sQuery(id+"F0.wireOp",EDGE,"E12.9.3"),sQuery(id+"F0.wireOp",EDGE,"E12.9.4"),sQuery(id+"F0.wireOp",EDGE,"E12.9.5"),sQuery(id+"F0.wireOp",EDGE,"E12.9.6"),sQuery(id+"F0.wireOp",EDGE,"E12.9.7"),sQuery(id+"F0.wireOp",EDGE,"E12.9.8"),sQuery(id+"F0.wireOp",EDGE,"E12.9.9"),sQuery(id+"F0.wireOp",EDGE,"E12.10.0"),sQuery(id+"F0.wireOp",EDGE,"E12.10.1"),sQuery(id+"F0.wireOp",EDGE,"E12.10.2"),sQuery(id+"F0.wireOp",EDGE,"E12.10.3"),sQuery(id+"F0.wireOp",EDGE,"E12.10.4"),sQuery(id+"F0.wireOp",EDGE,"E12.10.5"),sQuery(id+"F0.wireOp",EDGE,"E12.10.6"),sQuery(id+"F0.wireOp",EDGE,"E12.10.7"),sQuery(id+"F0.wireOp",EDGE,"E12.10.8"),sQuery(id+"F0.wireOp",EDGE,"E12.10.9"),sQuery(id+"F0.wireOp",EDGE,"E12.11.0"),sQuery(id+"F0.wireOp",EDGE,"E12.11.1"),sQuery(id+"F0.wireOp",EDGE,"E12.11.2"),sQuery(id+"F0.wireOp",EDGE,"E12.11.3"),sQuery(id+"F0.wireOp",EDGE,"E12.11.4"),sQuery(id+"F0.wireOp",EDGE,"E12.11.5"),sQuery(id+"F0.wireOp",EDGE,"E12.11.6"),sQuery(id+"F0.wireOp",EDGE,"E12.11.7"),sQuery(id+"F0.wireOp",EDGE,"E12.11.8"),sQuery(id+"F0.wireOp",EDGE,"E12.11.9"),sQuery(id+"F0.wireOp",EDGE,"E12.12.0"),sQuery(id+"F0.wireOp",EDGE,"E12.12.1"),sQuery(id+"F0.wireOp",EDGE,"E12.12.2"),sQuery(id+"F0.wireOp",EDGE,"E12.12.3"),sQuery(id+"F0.wireOp",EDGE,"E12.12.4"),sQuery(id+"F0.wireOp",EDGE,"E12.12.5"),sQuery(id+"F0.wireOp",EDGE,"E12.12.6"),sQuery(id+"F0.wireOp",EDGE,"E12.12.7"),sQuery(id+"F0.wireOp",EDGE,"E12.12.8"),sQuery(id+"F0.wireOp",EDGE,"E12.12.9"),sQuery(id+"F0.wireOp",EDGE,"E12.13.0"),sQuery(id+"F0.wireOp",EDGE,"E12.13.1"),sQuery(id+"F0.wireOp",EDGE,"E12.13.2"),sQuery(id+"F0.wireOp",EDGE,"E12.13.3"),sQuery(id+"F0.wireOp",EDGE,"E12.13.4"),sQuery(id+"F0.wireOp",EDGE,"E12.13.5"),sQuery(id+"F0.wireOp",EDGE,"E12.13.6"),sQuery(id+"F0.wireOp",EDGE,"E12.13.7"),sQuery(id+"F0.wireOp",EDGE,"E12.13.8"),sQuery(id+"F0.wireOp",EDGE,"E12.13.9"),sQuery(id+"F0.wireOp",EDGE,"E12.14.0"),sQuery(id+"F0.wireOp",EDGE,"E12.14.1"),sQuery(id+"F0.wireOp",EDGE,"E12.14.2"),sQuery(id+"F0.wireOp",EDGE,"E12.14.3"),sQuery(id+"F0.wireOp",EDGE,"E12.14.4"),sQuery(id+"F0.wireOp",EDGE,"E12.14.5"),sQuery(id+"F0.wireOp",EDGE,"E12.14.6"),sQuery(id+"F0.wireOp",EDGE,"E12.14.7"),sQuery(id+"F0.wireOp",EDGE,"E12.14.8"),sQuery(id+"F0.wireOp",EDGE,"E12.14.9"),sQuery(id+"F0.wireOp",EDGE,"E12.15.0"),sQuery(id+"F0.wireOp",EDGE,"E12.15.1"),sQuery(id+"F0.wireOp",EDGE,"E12.15.2"),sQuery(id+"F0.wireOp",EDGE,"E12.15.3"),sQuery(id+"F0.wireOp",EDGE,"E12.15.4"),sQuery(id+"F0.wireOp",EDGE,"E12.15.5"),sQuery(id+"F0.wireOp",EDGE,"E12.15.6"),sQuery(id+"F0.wireOp",EDGE,"E12.15.7"),sQuery(id+"F0.wireOp",EDGE,"E12.15.8"),sQuery(id+"F0.wireOp",EDGE,"E12.15.9"),sQuery(id+"F0.wireOp",EDGE,"E12.16.0"),sQuery(id+"F0.wireOp",EDGE,"E12.16.1"),sQuery(id+"F0.wireOp",EDGE,"E12.16.2"),sQuery(id+"F0.wireOp",EDGE,"E12.16.3"),sQuery(id+"F0.wireOp",EDGE,"E12.16.4"),sQuery(id+"F0.wireOp",EDGE,"E12.16.5"),sQuery(id+"F0.wireOp",EDGE,"E12.16.6"),sQuery(id+"F0.wireOp",EDGE,"E12.16.7"),sQuery(id+"F0.wireOp",EDGE,"E12.16.8"),sQuery(id+"F0.wireOp",EDGE,"E12.16.9"),sQuery(id+"F0.wireOp",EDGE,"E12.17.0"),sQuery(id+"F0.wireOp",EDGE,"E12.17.1"),sQuery(id+"F0.wireOp",EDGE,"E12.17.2"),sQuery(id+"F0.wireOp",EDGE,"E12.17.3"),sQuery(id+"F0.wireOp",EDGE,"E12.17.4"),sQuery(id+"F0.wireOp",EDGE,"E12.17.5"),sQuery(id+"F0.wireOp",EDGE,"E12.17.6"),sQuery(id+"F0.wireOp",EDGE,"E12.17.7"),sQuery(id+"F0.wireOp",EDGE,"E12.17.8"),sQuery(id+"F0.wireOp",EDGE,"E12.17.9"),sQuery(id+"F0.wireOp",EDGE,"E12.18.0"),sQuery(id+"F0.wireOp",EDGE,"E12.18.1"),sQuery(id+"F0.wireOp",EDGE,"E12.18.2"),sQuery(id+"F0.wireOp",EDGE,"E12.18.3"),sQuery(id+"F0.wireOp",EDGE,"E12.18.4"),sQuery(id+"F0.wireOp",EDGE,"E12.18.5"),sQuery(id+"F0.wireOp",EDGE,"E12.18.6"),sQuery(id+"F0.wireOp",EDGE,"E12.18.7"),sQuery(id+"F0.wireOp",EDGE,"E12.18.8"),sQuery(id+"F0.wireOp",EDGE,"E12.18.9"),sQuery(id+"F0.wireOp",EDGE,"E12.19.0"),sQuery(id+"F0.wireOp",EDGE,"E12.19.1"),sQuery(id+"F0.wireOp",EDGE,"E12.19.2"),sQuery(id+"F0.wireOp",EDGE,"E12.19.3"),sQuery(id+"F0.wireOp",EDGE,"E12.19.4"),sQuery(id+"F0.wireOp",EDGE,"E12.19.5"),sQuery(id+"F0.wireOp",EDGE,"E12.19.6"),sQuery(id+"F0.wireOp",EDGE,"E12.19.7"),sQuery(id+"F0.wireOp",EDGE,"E12.19.8"),sQuery(id+"F0.wireOp",EDGE,"E12.19.9"),sQuery(id+"F0.wireOp",EDGE,"E12.20.0"),sQuery(id+"F0.wireOp",EDGE,"E12.20.1"),sQuery(id+"F0.wireOp",EDGE,"E12.20.2"),sQuery(id+"F0.wireOp",EDGE,"E12.20.3"),sQuery(id+"F0.wireOp",EDGE,"E12.20.4"),sQuery(id+"F0.wireOp",EDGE,"E12.20.5"),sQuery(id+"F0.wireOp",EDGE,"E12.20.6"),sQuery(id+"F0.wireOp",EDGE,"E12.20.7"),sQuery(id+"F0.wireOp",EDGE,"E12.20.8"),sQuery(id+"F0.wireOp",EDGE,"E12.20.9"),sQuery(id+"F0.wireOp",EDGE,"E12.21.0"),sQuery(id+"F0.wireOp",EDGE,"E12.21.1"),sQuery(id+"F0.wireOp",EDGE,"E12.21.2"),sQuery(id+"F0.wireOp",EDGE,"E12.21.3"),sQuery(id+"F0.wireOp",EDGE,"E12.21.4"),sQuery(id+"F0.wireOp",EDGE,"E12.21.5"),sQuery(id+"F0.wireOp",EDGE,"E12.21.6"),sQuery(id+"F0.wireOp",EDGE,"E12.21.7"),sQuery(id+"F0.wireOp",EDGE,"E12.21.8"),sQuery(id+"F0.wireOp",EDGE,"E12.21.9"),sQuery(id+"F0.wireOp",EDGE,"E12.22.0"),sQuery(id+"F0.wireOp",EDGE,"E12.22.1"),sQuery(id+"F0.wireOp",EDGE,"E12.22.2"),sQuery(id+"F0.wireOp",EDGE,"E12.22.3"),sQuery(id+"F0.wireOp",EDGE,"E12.22.4"),sQuery(id+"F0.wireOp",EDGE,"E12.22.5"),sQuery(id+"F0.wireOp",EDGE,"E12.22.6"),sQuery(id+"F0.wireOp",EDGE,"E12.22.7"),sQuery(id+"F0.wireOp",EDGE,"E12.22.8"),sQuery(id+"F0.wireOp",EDGE,"E12.22.9"),sQuery(id+"F0.wireOp",EDGE,"E12.23.0"),sQuery(id+"F0.wireOp",EDGE,"E12.23.1"),sQuery(id+"F0.wireOp",EDGE,"E12.23.2"),sQuery(id+"F0.wireOp",EDGE,"E12.23.3"),sQuery(id+"F0.wireOp",EDGE,"E12.23.4"),sQuery(id+"F0.wireOp",EDGE,"E12.23.5"),sQuery(id+"F0.wireOp",EDGE,"E12.23.6"),sQuery(id+"F0.wireOp",EDGE,"E12.23.7"),sQuery(id+"F0.wireOp",EDGE,"E12.23.8"),sQuery(id+"F0.wireOp",EDGE,"E12.23.9"),sQuery(id+"F0.wireOp",EDGE,"E12.24.0"),sQuery(id+"F0.wireOp",EDGE,"E12.24.1"),sQuery(id+"F0.wireOp",EDGE,"E12.24.2"),sQuery(id+"F0.wireOp",EDGE,"E12.24.3"),sQuery(id+"F0.wireOp",EDGE,"E12.24.4"),sQuery(id+"F0.wireOp",EDGE,"E12.24.5"),sQuery(id+"F0.wireOp",EDGE,"E12.24.6"),sQuery(id+"F0.wireOp",EDGE,"E12.24.7"),sQuery(id+"F0.wireOp",EDGE,"E12.24.8"),sQuery(id+"F0.wireOp",EDGE,"E12.24.9"),sQuery(id+"F0.wireOp",EDGE,"E12.25.0"),sQuery(id+"F0.wireOp",EDGE,"E12.25.1"),sQuery(id+"F0.wireOp",EDGE,"E12.25.2"),sQuery(id+"F0.wireOp",EDGE,"E12.25.3"),sQuery(id+"F0.wireOp",EDGE,"E12.25.4"),sQuery(id+"F0.wireOp",EDGE,"E12.25.5"),sQuery(id+"F0.wireOp",EDGE,"E12.25.6"),sQuery(id+"F0.wireOp",EDGE,"E12.25.7"),sQuery(id+"F0.wireOp",EDGE,"E12.25.8"),sQuery(id+"F0.wireOp",EDGE,"E12.25.9"),sQuery(id+"F0.wireOp",EDGE,"E12.26.0"),sQuery(id+"F0.wireOp",EDGE,"E12.26.1"),sQuery(id+"F0.wireOp",EDGE,"E12.26.2"),sQuery(id+"F0.wireOp",EDGE,"E12.26.3"),sQuery(id+"F0.wireOp",EDGE,"E12.26.4"),sQuery(id+"F0.wireOp",EDGE,"E12.26.5"),sQuery(id+"F0.wireOp",EDGE,"E12.26.6"),sQuery(id+"F0.wireOp",EDGE,"E12.26.7"),sQuery(id+"F0.wireOp",EDGE,"E12.26.8"),sQuery(id+"F0.wireOp",EDGE,"E12.26.9"),sQuery(id+"F0.wireOp",EDGE,"E12.27.0"),sQuery(id+"F0.wireOp",EDGE,"E12.27.1"),sQuery(id+"F0.wireOp",EDGE,"E12.27.2"),sQuery(id+"F0.wireOp",EDGE,"E12.27.3"),sQuery(id+"F0.wireOp",EDGE,"E12.27.4"),sQuery(id+"F0.wireOp",EDGE,"E12.27.5"),sQuery(id+"F0.wireOp",EDGE,"E12.27.6"),sQuery(id+"F0.wireOp",EDGE,"E12.27.7"),sQuery(id+"F0.wireOp",EDGE,"E12.27.8"),sQuery(id+"F0.wireOp",EDGE,"E12.27.9"),sQuery(id+"F0.wireOp",EDGE,"E12.28.0"),sQuery(id+"F0.wireOp",EDGE,"E12.28.1"),sQuery(id+"F0.wireOp",EDGE,"E12.28.2"),sQuery(id+"F0.wireOp",EDGE,"E12.28.3"),sQuery(id+"F0.wireOp",EDGE,"E12.28.4"),sQuery(id+"F0.wireOp",EDGE,"E12.28.5"),sQuery(id+"F0.wireOp",EDGE,"E12.28.6"),sQuery(id+"F0.wireOp",EDGE,"E12.28.7"),sQuery(id+"F0.wireOp",EDGE,"E12.28.8"),sQuery(id+"F0.wireOp",EDGE,"E12.28.9"),sQuery(id+"F0.wireOp",EDGE,"E12.29.0"),sQuery(id+"F0.wireOp",EDGE,"E12.29.1"),sQuery(id+"F0.wireOp",EDGE,"E12.29.2"),sQuery(id+"F0.wireOp",EDGE,"E12.29.3"),sQuery(id+"F0.wireOp",EDGE,"E12.29.4"),sQuery(id+"F0.wireOp",EDGE,"E12.29.5"),sQuery(id+"F0.wireOp",EDGE,"E12.29.6"),sQuery(id+"F0.wireOp",EDGE,"E12.29.7"),sQuery(id+"F0.wireOp",EDGE,"E12.29.8"),sQuery(id+"F0.wireOp",EDGE,"E12.29.9"),sQuery(id+"F0.wireOp",EDGE,"E12.30.0"),sQuery(id+"F0.wireOp",EDGE,"E12.30.1"),sQuery(id+"F0.wireOp",EDGE,"E12.30.2"),sQuery(id+"F0.wireOp",EDGE,"E12.30.3"),sQuery(id+"F0.wireOp",EDGE,"E12.30.4"),sQuery(id+"F0.wireOp",EDGE,"E12.30.5"),sQuery(id+"F0.wireOp",EDGE,"E12.30.6"),sQuery(id+"F0.wireOp",EDGE,"E12.30.7"),sQuery(id+"F0.wireOp",EDGE,"E12.30.8"),sQuery(id+"F0.wireOp",EDGE,"E12.30.9"),sQuery(id+"F0.wireOp",EDGE,"E12.31.0"),sQuery(id+"F0.wireOp",EDGE,"E12.31.1"),sQuery(id+"F0.wireOp",EDGE,"E12.31.2"),sQuery(id+"F0.wireOp",EDGE,"E12.31.3"),sQuery(id+"F0.wireOp",EDGE,"E12.31.4"),sQuery(id+"F0.wireOp",EDGE,"E12.31.5"),sQuery(id+"F0.wireOp",EDGE,"E12.31.6"),sQuery(id+"F0.wireOp",EDGE,"E12.31.7"),sQuery(id+"F0.wireOp",EDGE,"E12.31.8"),sQuery(id+"F0.wireOp",EDGE,"E12.31.9"),sQuery(id+"F0.wireOp",EDGE,"E12.32.0"),sQuery(id+"F0.wireOp",EDGE,"E12.32.1"),sQuery(id+"F0.wireOp",EDGE,"E12.32.2"),sQuery(id+"F0.wireOp",EDGE,"E12.32.3"),sQuery(id+"F0.wireOp",EDGE,"E12.32.4"),sQuery(id+"F0.wireOp",EDGE,"E12.32.5"),sQuery(id+"F0.wireOp",EDGE,"E12.32.6"),sQuery(id+"F0.wireOp",EDGE,"E12.32.7"),sQuery(id+"F0.wireOp",EDGE,"E12.32.8"),sQuery(id+"F0.wireOp",EDGE,"E12.32.9"),sQuery(id+"F0.wireOp",EDGE,"E12.33.0"),sQuery(id+"F0.wireOp",EDGE,"E12.33.1"),sQuery(id+"F0.wireOp",EDGE,"E12.33.2"),sQuery(id+"F0.wireOp",EDGE,"E12.33.3"),sQuery(id+"F0.wireOp",EDGE,"E12.33.4"),sQuery(id+"F0.wireOp",EDGE,"E12.33.5"),sQuery(id+"F0.wireOp",EDGE,"E12.33.6"),sQuery(id+"F0.wireOp",EDGE,"E12.33.7"),sQuery(id+"F0.wireOp",EDGE,"E12.33.8"),sQuery(id+"F0.wireOp",EDGE,"E12.33.9"),sQuery(id+"F0.wireOp",EDGE,"E12.34.0"),sQuery(id+"F0.wireOp",EDGE,"E12.34.1"),sQuery(id+"F0.wireOp",EDGE,"E12.34.2"),sQuery(id+"F0.wireOp",EDGE,"E12.34.3"),sQuery(id+"F0.wireOp",EDGE,"E12.34.4"),sQuery(id+"F0.wireOp",EDGE,"E12.34.5"),sQuery(id+"F0.wireOp",EDGE,"E12.34.6"),sQuery(id+"F0.wireOp",EDGE,"E12.34.7"),sQuery(id+"F0.wireOp",EDGE,"E12.34.8"),sQuery(id+"F0.wireOp",EDGE,"E12.34.9"),sQuery(id+"F0.wireOp",EDGE,"E12.35.0"),sQuery(id+"F0.wireOp",EDGE,"E12.35.1"),sQuery(id+"F0.wireOp",EDGE,"E12.35.2"),sQuery(id+"F0.wireOp",EDGE,"E12.35.3"),sQuery(id+"F0.wireOp",EDGE,"E12.35.4"),sQuery(id+"F0.wireOp",EDGE,"E12.35.5"),sQuery(id+"F0.wireOp",EDGE,"E12.35.6"),sQuery(id+"F0.wireOp",EDGE,"E12.35.7"),sQuery(id+"F0.wireOp",EDGE,"E12.35.8"),sQuery(id+"F0.wireOp",EDGE,"E12.35.9"),sQuery(id+"F0.wireOp",EDGE,"E12.36.0"),sQuery(id+"F0.wireOp",EDGE,"E12.36.1"),sQuery(id+"F0.wireOp",EDGE,"E12.36.2"),sQuery(id+"F0.wireOp",EDGE,"E12.36.3"),sQuery(id+"F0.wireOp",EDGE,"E12.36.4"),sQuery(id+"F0.wireOp",EDGE,"E12.36.5"),sQuery(id+"F0.wireOp",EDGE,"E12.36.6"),sQuery(id+"F0.wireOp",EDGE,"E12.36.7"),sQuery(id+"F0.wireOp",EDGE,"E12.36.8"),sQuery(id+"F0.wireOp",EDGE,"E12.36.9"),sQuery(id+"F0.wireOp",EDGE,"E12.37.0"),sQuery(id+"F0.wireOp",EDGE,"E12.37.1"),sQuery(id+"F0.wireOp",EDGE,"E12.37.2"),sQuery(id+"F0.wireOp",EDGE,"E12.37.3"),sQuery(id+"F0.wireOp",EDGE,"E12.37.4"),sQuery(id+"F0.wireOp",EDGE,"E12.37.5"),sQuery(id+"F0.wireOp",EDGE,"E12.37.6"),sQuery(id+"F0.wireOp",EDGE,"E12.37.7"),sQuery(id+"F0.wireOp",EDGE,"E12.37.8"),sQuery(id+"F0.wireOp",EDGE,"E12.37.9"),sQuery(id+"F0.wireOp",EDGE,"E12.38.0"),sQuery(id+"F0.wireOp",EDGE,"E12.38.1"),sQuery(id+"F0.wireOp",EDGE,"E12.38.2"),sQuery(id+"F0.wireOp",EDGE,"E12.38.3"),sQuery(id+"F0.wireOp",EDGE,"E12.38.4"),sQuery(id+"F0.wireOp",EDGE,"E12.38.5"),sQuery(id+"F0.wireOp",EDGE,"E12.38.6"),sQuery(id+"F0.wireOp",EDGE,"E12.38.7"),sQuery(id+"F0.wireOp",EDGE,"E12.38.8"),sQuery(id+"F0.wireOp",EDGE,"E12.38.9"),sQuery(id+"F0.wireOp",EDGE,"E12.39.0"),sQuery(id+"F0.wireOp",EDGE,"E12.39.1"),sQuery(id+"F0.wireOp",EDGE,"E12.39.2"),sQuery(id+"F0.wireOp",EDGE,"E12.39.3"),sQuery(id+"F0.wireOp",EDGE,"E12.39.4"),sQuery(id+"F0.wireOp",EDGE,"E12.39.5"),sQuery(id+"F0.wireOp",EDGE,"E12.39.6"),sQuery(id+"F0.wireOp",EDGE,"E12.39.7"),sQuery(id+"F0.wireOp",EDGE,"E12.39.8"),sQuery(id+"F0.wireOp",EDGE,"E12.39.9"),sQuery(id+"F0.wireOp",EDGE,"E12.40.0"),sQuery(id+"F0.wireOp",EDGE,"E12.40.1"),sQuery(id+"F0.wireOp",EDGE,"E12.40.2"),sQuery(id+"F0.wireOp",EDGE,"E12.40.3"),sQuery(id+"F0.wireOp",EDGE,"E12.40.4"),sQuery(id+"F0.wireOp",EDGE,"E12.40.5"),sQuery(id+"F0.wireOp",EDGE,"E12.40.6"),sQuery(id+"F0.wireOp",EDGE,"E12.40.7"),sQuery(id+"F0.wireOp",EDGE,"E12.40.8"),sQuery(id+"F0.wireOp",EDGE,"E12.40.9"),sQuery(id+"F0.wireOp",EDGE,"E12.41.0"),sQuery(id+"F0.wireOp",EDGE,"E12.41.1"),sQuery(id+"F0.wireOp",EDGE,"E12.41.2"),sQuery(id+"F0.wireOp",EDGE,"E12.41.3"),sQuery(id+"F0.wireOp",EDGE,"E12.41.4"),sQuery(id+"F0.wireOp",EDGE,"E12.41.5"),sQuery(id+"F0.wireOp",EDGE,"E12.41.6"),sQuery(id+"F0.wireOp",EDGE,"E12.41.7"),sQuery(id+"F0.wireOp",EDGE,"E12.41.8"),sQuery(id+"F0.wireOp",EDGE,"E12.41.9"),sQuery(id+"F0.wireOp",EDGE,"E12.42.0"),sQuery(id+"F0.wireOp",EDGE,"E12.42.1"),sQuery(id+"F0.wireOp",EDGE,"E12.42.2"),sQuery(id+"F0.wireOp",EDGE,"E12.42.3"),sQuery(id+"F0.wireOp",EDGE,"E12.42.4"),sQuery(id+"F0.wireOp",EDGE,"E12.42.5"),sQuery(id+"F0.wireOp",EDGE,"E12.42.6"),sQuery(id+"F0.wireOp",EDGE,"E12.42.7"),sQuery(id+"F0.wireOp",EDGE,"E12.42.8"),sQuery(id+"F0.wireOp",EDGE,"E12.42.9"),sQuery(id+"F0.wireOp",EDGE,"E12.43.0"),sQuery(id+"F0.wireOp",EDGE,"E12.43.1"),sQuery(id+"F0.wireOp",EDGE,"E12.43.2"),sQuery(id+"F0.wireOp",EDGE,"E12.43.3"),sQuery(id+"F0.wireOp",EDGE,"E12.43.4"),sQuery(id+"F0.wireOp",EDGE,"E12.43.5"),sQuery(id+"F0.wireOp",EDGE,"E12.43.6"),sQuery(id+"F0.wireOp",EDGE,"E12.43.7"),sQuery(id+"F0.wireOp",EDGE,"E12.43.8"),sQuery(id+"F0.wireOp",EDGE,"E12.43.9"),sQuery(id+"F0.wireOp",EDGE,"E12.44.0"),sQuery(id+"F0.wireOp",EDGE,"E12.44.1"),sQuery(id+"F0.wireOp",EDGE,"E12.44.2"),sQuery(id+"F0.wireOp",EDGE,"E12.44.3"),sQuery(id+"F0.wireOp",EDGE,"E12.44.4"),sQuery(id+"F0.wireOp",EDGE,"E12.44.5"),sQuery(id+"F0.wireOp",EDGE,"E12.44.6"),sQuery(id+"F0.wireOp",EDGE,"E12.44.7"),sQuery(id+"F0.wireOp",EDGE,"E12.44.8"),sQuery(id+"F0.wireOp",EDGE,"E12.44.9"),sQuery(id+"F0.wireOp",EDGE,"E12.45.0"),sQuery(id+"F0.wireOp",EDGE,"E12.45.1"),sQuery(id+"F0.wireOp",EDGE,"E12.45.2"),sQuery(id+"F0.wireOp",EDGE,"E12.45.3"),sQuery(id+"F0.wireOp",EDGE,"E12.45.4"),sQuery(id+"F0.wireOp",EDGE,"E12.45.5"),sQuery(id+"F0.wireOp",EDGE,"E12.45.6"),sQuery(id+"F0.wireOp",EDGE,"E12.45.7"),sQuery(id+"F0.wireOp",EDGE,"E12.45.8"),sQuery(id+"F0.wireOp",EDGE,"E12.45.9"),sQuery(id+"F0.wireOp",EDGE,"E12.46.0"),sQuery(id+"F0.wireOp",EDGE,"E12.46.1"),sQuery(id+"F0.wireOp",EDGE,"E12.46.2"),sQuery(id+"F0.wireOp",EDGE,"E12.46.3"),sQuery(id+"F0.wireOp",EDGE,"E12.46.4"),sQuery(id+"F0.wireOp",EDGE,"E12.46.5"),sQuery(id+"F0.wireOp",EDGE,"E12.46.6"),sQuery(id+"F0.wireOp",EDGE,"E12.46.7"),sQuery(id+"F0.wireOp",EDGE,"E12.46.8"),sQuery(id+"F0.wireOp",EDGE,"E12.46.9"),sQuery(id+"F0.wireOp",EDGE,"E12.47.0"),sQuery(id+"F0.wireOp",EDGE,"E12.47.1"),sQuery(id+"F0.wireOp",EDGE,"E12.47.2"),sQuery(id+"F0.wireOp",EDGE,"E12.47.3"),sQuery(id+"F0.wireOp",EDGE,"E12.47.4"),sQuery(id+"F0.wireOp",EDGE,"E12.47.5"),sQuery(id+"F0.wireOp",EDGE,"E12.47.6"),sQuery(id+"F0.wireOp",EDGE,"E12.47.7"),sQuery(id+"F0.wireOp",EDGE,"E12.47.8"),sQuery(id+"F0.wireOp",EDGE,"E12.47.9"),sQuery(id+"F0.wireOp",EDGE,"E12.48.0"),sQuery(id+"F0.wireOp",EDGE,"E12.48.1"),sQuery(id+"F0.wireOp",EDGE,"E12.48.2"),sQuery(id+"F0.wireOp",EDGE,"E12.48.3"),sQuery(id+"F0.wireOp",EDGE,"E12.48.4"),sQuery(id+"F0.wireOp",EDGE,"E12.48.5"),sQuery(id+"F0.wireOp",EDGE,"E12.48.6"),sQuery(id+"F0.wireOp",EDGE,"E12.48.7"),sQuery(id+"F0.wireOp",EDGE,"E12.48.8"),sQuery(id+"F0.wireOp",EDGE,"E12.48.9"),sQuery(id+"F0.wireOp",EDGE,"E12.49.0"),sQuery(id+"F0.wireOp",EDGE,"E12.49.1"),sQuery(id+"F0.wireOp",EDGE,"E12.49.2"),sQuery(id+"F0.wireOp",EDGE,"E12.49.3"),sQuery(id+"F0.wireOp",EDGE,"E12.49.4"),sQuery(id+"F0.wireOp",EDGE,"E12.49.5"),sQuery(id+"F0.wireOp",EDGE,"E12.49.6"),sQuery(id+"F0.wireOp",EDGE,"E12.49.7"),sQuery(id+"F0.wireOp",EDGE,"E12.49.8"),sQuery(id+"F0.wireOp",EDGE,"E12.49.9"),sQuery(id+"F0.wireOp",EDGE,"E12.50.0"),sQuery(id+"F0.wireOp",EDGE,"E12.50.1"),sQuery(id+"F0.wireOp",EDGE,"E12.50.2"),sQuery(id+"F0.wireOp",EDGE,"E12.50.3"),sQuery(id+"F0.wireOp",EDGE,"E12.50.4"),sQuery(id+"F0.wireOp",EDGE,"E12.50.5"),sQuery(id+"F0.wireOp",EDGE,"E12.50.6"),sQuery(id+"F0.wireOp",EDGE,"E12.50.7"),sQuery(id+"F0.wireOp",EDGE,"E12.50.8"),sQuery(id+"F0.wireOp",EDGE,"E12.50.9"),sQuery(id+"F0.wireOp",EDGE,"E12.51.0"),sQuery(id+"F0.wireOp",EDGE,"E12.51.1"),sQuery(id+"F0.wireOp",EDGE,"E12.51.2"),sQuery(id+"F0.wireOp",EDGE,"E12.51.3"),sQuery(id+"F0.wireOp",EDGE,"E12.51.4"),sQuery(id+"F0.wireOp",EDGE,"E12.51.5"),sQuery(id+"F0.wireOp",EDGE,"E12.51.6"),sQuery(id+"F0.wireOp",EDGE,"E12.51.7"),sQuery(id+"F0.wireOp",EDGE,"E12.51.8"),sQuery(id+"F0.wireOp",EDGE,"E12.51.9"),sQuery(id+"F0.wireOp",EDGE,"E12.52.0"),sQuery(id+"F0.wireOp",EDGE,"E12.52.1"),sQuery(id+"F0.wireOp",EDGE,"E12.52.2"),sQuery(id+"F0.wireOp",EDGE,"E12.52.3"),sQuery(id+"F0.wireOp",EDGE,"E12.52.4"),sQuery(id+"F0.wireOp",EDGE,"E12.52.5"),sQuery(id+"F0.wireOp",EDGE,"E12.52.6"),sQuery(id+"F0.wireOp",EDGE,"E12.52.7"),sQuery(id+"F0.wireOp",EDGE,"E12.52.8"),sQuery(id+"F0.wireOp",EDGE,"E12.52.9"),sQuery(id+"F0.wireOp",EDGE,"E12.53.0"),sQuery(id+"F0.wireOp",EDGE,"E12.53.1"),sQuery(id+"F0.wireOp",EDGE,"E12.53.2"),sQuery(id+"F0.wireOp",EDGE,"E12.53.3"),sQuery(id+"F0.wireOp",EDGE,"E12.53.4"),sQuery(id+"F0.wireOp",EDGE,"E12.53.5"),sQuery(id+"F0.wireOp",EDGE,"E12.53.6"),sQuery(id+"F0.wireOp",EDGE,"E12.53.7"),sQuery(id+"F0.wireOp",EDGE,"E12.53.8"),sQuery(id+"F0.wireOp",EDGE,"E12.53.9"),sQuery(id+"F0.wireOp",EDGE,"E12.54.0"),sQuery(id+"F0.wireOp",EDGE,"E12.54.1"),sQuery(id+"F0.wireOp",EDGE,"E12.54.2"),sQuery(id+"F0.wireOp",EDGE,"E12.54.3"),sQuery(id+"F0.wireOp",EDGE,"E12.54.4"),sQuery(id+"F0.wireOp",EDGE,"E12.54.5"),sQuery(id+"F0.wireOp",EDGE,"E12.54.6"),sQuery(id+"F0.wireOp",EDGE,"E12.54.7"),sQuery(id+"F0.wireOp",EDGE,"E12.54.8"),sQuery(id+"F0.wireOp",EDGE,"E12.54.9"),sQuery(id+"F0.wireOp",EDGE,"E12.55.0"),sQuery(id+"F0.wireOp",EDGE,"E12.55.1"),sQuery(id+"F0.wireOp",EDGE,"E12.55.2"),sQuery(id+"F0.wireOp",EDGE,"E12.55.3"),sQuery(id+"F0.wireOp",EDGE,"E12.55.4"),sQuery(id+"F0.wireOp",EDGE,"E12.55.5"),sQuery(id+"F0.wireOp",EDGE,"E12.55.6"),sQuery(id+"F0.wireOp",EDGE,"E12.55.7"),sQuery(id+"F0.wireOp",EDGE,"E12.55.8"),sQuery(id+"F0.wireOp",EDGE,"E12.55.9"),sQuery(id+"F0.wireOp",EDGE,"E12.56.0"),sQuery(id+"F0.wireOp",EDGE,"E12.56.1"),sQuery(id+"F0.wireOp",EDGE,"E12.56.2"),sQuery(id+"F0.wireOp",EDGE,"E12.56.3"),sQuery(id+"F0.wireOp",EDGE,"E12.56.4"),sQuery(id+"F0.wireOp",EDGE,"E12.56.5"),sQuery(id+"F0.wireOp",EDGE,"E12.56.6"),sQuery(id+"F0.wireOp",EDGE,"E12.56.7"),sQuery(id+"F0.wireOp",EDGE,"E12.56.8"),sQuery(id+"F0.wireOp",EDGE,"E12.56.9"),sQuery(id+"F0.wireOp",EDGE,"E12.57.0"),sQuery(id+"F0.wireOp",EDGE,"E12.57.1"),sQuery(id+"F0.wireOp",EDGE,"E12.57.2"),sQuery(id+"F0.wireOp",EDGE,"E12.57.3"),sQuery(id+"F0.wireOp",EDGE,"E12.57.4"),sQuery(id+"F0.wireOp",EDGE,"E12.57.5"),sQuery(id+"F0.wireOp",EDGE,"E12.57.6"),sQuery(id+"F0.wireOp",EDGE,"E12.57.7"),sQuery(id+"F0.wireOp",EDGE,"E12.57.8"),sQuery(id+"F0.wireOp",EDGE,"E12.57.9"),sQuery(id+"F0.wireOp",EDGE,"E12.58.0"),sQuery(id+"F0.wireOp",EDGE,"E12.58.1"),sQuery(id+"F0.wireOp",EDGE,"E12.58.2"),sQuery(id+"F0.wireOp",EDGE,"E12.58.3"),sQuery(id+"F0.wireOp",EDGE,"E12.58.4"),sQuery(id+"F0.wireOp",EDGE,"E12.58.5"),sQuery(id+"F0.wireOp",EDGE,"E12.58.6"),sQuery(id+"F0.wireOp",EDGE,"E12.58.7"),sQuery(id+"F0.wireOp",EDGE,"E12.58.8"),sQuery(id+"F0.wireOp",EDGE,"E12.58.9"),sQuery(id+"F0.wireOp",EDGE,"E12.59.0"),sQuery(id+"F0.wireOp",EDGE,"E12.59.1"),sQuery(id+"F0.wireOp",EDGE,"E12.59.2"),sQuery(id+"F0.wireOp",EDGE,"E12.59.3"),sQuery(id+"F0.wireOp",EDGE,"E12.59.4"),sQuery(id+"F0.wireOp",EDGE,"E12.59.5"),sQuery(id+"F0.wireOp",EDGE,"E12.59.6"),sQuery(id+"F0.wireOp",EDGE,"E12.59.7"),sQuery(id+"F0.wireOp",EDGE,"E12.59.8"),sQuery(id+"F0.wireOp",EDGE,"E12.59.9"),sQuery(id+"F0.wireOp",EDGE,"E13.trimOffspring"),sQuery(id+"F0.wireOp",EDGE,"E14.trimOffspring")])],"isStart":true}),makeQuery(id+"F3.opExtrude","SWEPT_FACE",FACE,{"disambiguationData":[OSD([sQuery(id+"F2.wireOp",EDGE,"E17.2.0")])]})]});
            var Q9;
            Q9=makeQuery(id+"F3.boolean.opBoolean","INTERSECT",EDGE,{"derivedFrom":[makeQuery(id+"F1.opExtrude","CAP_FACE",FACE,{"disambiguationData":[OSD([sQuery(id+"F0.wireOp",EDGE,"E0"),sQuery(id+"F0.wireOp",EDGE,"E2"),sQuery(id+"F0.wireOp",EDGE,"E3"),sQuery(id+"F0.wireOp",EDGE,"E4.trimOffspring"),sQuery(id+"F0.wireOp",EDGE,"E5.MirrorCS"),sQuery(id+"F0.wireOp",EDGE,"E6.MirrorCS"),sQuery(id+"F0.wireOp",EDGE,"E7.MirrorCS"),sQuery(id+"F0.wireOp",EDGE,"E8.filletArc"),sQuery(id+"F0.wireOp",EDGE,"E9.filletArc"),sQuery(id+"F0.wireOp",EDGE,"E10.filletArc"),sQuery(id+"F0.wireOp",EDGE,"E11.filletArc"),sQuery(id+"F0.wireOp",EDGE,"E12.1.0"),sQuery(id+"F0.wireOp",EDGE,"E12.1.1"),sQuery(id+"F0.wireOp",EDGE,"E12.1.2"),sQuery(id+"F0.wireOp",EDGE,"E12.1.3"),sQuery(id+"F0.wireOp",EDGE,"E12.1.4"),sQuery(id+"F0.wireOp",EDGE,"E12.1.5"),sQuery(id+"F0.wireOp",EDGE,"E12.1.6"),sQuery(id+"F0.wireOp",EDGE,"E12.1.7"),sQuery(id+"F0.wireOp",EDGE,"E12.1.8"),sQuery(id+"F0.wireOp",EDGE,"E12.1.9"),sQuery(id+"F0.wireOp",EDGE,"E12.2.0"),sQuery(id+"F0.wireOp",EDGE,"E12.2.1"),sQuery(id+"F0.wireOp",EDGE,"E12.2.2"),sQuery(id+"F0.wireOp",EDGE,"E12.2.3"),sQuery(id+"F0.wireOp",EDGE,"E12.2.4"),sQuery(id+"F0.wireOp",EDGE,"E12.2.5"),sQuery(id+"F0.wireOp",EDGE,"E12.2.6"),sQuery(id+"F0.wireOp",EDGE,"E12.2.7"),sQuery(id+"F0.wireOp",EDGE,"E12.2.8"),sQuery(id+"F0.wireOp",EDGE,"E12.2.9"),sQuery(id+"F0.wireOp",EDGE,"E12.3.0"),sQuery(id+"F0.wireOp",EDGE,"E12.3.1"),sQuery(id+"F0.wireOp",EDGE,"E12.3.2"),sQuery(id+"F0.wireOp",EDGE,"E12.3.3"),sQuery(id+"F0.wireOp",EDGE,"E12.3.4"),sQuery(id+"F0.wireOp",EDGE,"E12.3.5"),sQuery(id+"F0.wireOp",EDGE,"E12.3.6"),sQuery(id+"F0.wireOp",EDGE,"E12.3.7"),sQuery(id+"F0.wireOp",EDGE,"E12.3.8"),sQuery(id+"F0.wireOp",EDGE,"E12.3.9"),sQuery(id+"F0.wireOp",EDGE,"E12.4.0"),sQuery(id+"F0.wireOp",EDGE,"E12.4.1"),sQuery(id+"F0.wireOp",EDGE,"E12.4.2"),sQuery(id+"F0.wireOp",EDGE,"E12.4.3"),sQuery(id+"F0.wireOp",EDGE,"E12.4.4"),sQuery(id+"F0.wireOp",EDGE,"E12.4.5"),sQuery(id+"F0.wireOp",EDGE,"E12.4.6"),sQuery(id+"F0.wireOp",EDGE,"E12.4.7"),sQuery(id+"F0.wireOp",EDGE,"E12.4.8"),sQuery(id+"F0.wireOp",EDGE,"E12.4.9"),sQuery(id+"F0.wireOp",EDGE,"E12.5.0"),sQuery(id+"F0.wireOp",EDGE,"E12.5.1"),sQuery(id+"F0.wireOp",EDGE,"E12.5.2"),sQuery(id+"F0.wireOp",EDGE,"E12.5.3"),sQuery(id+"F0.wireOp",EDGE,"E12.5.4"),sQuery(id+"F0.wireOp",EDGE,"E12.5.5"),sQuery(id+"F0.wireOp",EDGE,"E12.5.6"),sQuery(id+"F0.wireOp",EDGE,"E12.5.7"),sQuery(id+"F0.wireOp",EDGE,"E12.5.8"),sQuery(id+"F0.wireOp",EDGE,"E12.5.9"),sQuery(id+"F0.wireOp",EDGE,"E12.6.0"),sQuery(id+"F0.wireOp",EDGE,"E12.6.1"),sQuery(id+"F0.wireOp",EDGE,"E12.6.2"),sQuery(id+"F0.wireOp",EDGE,"E12.6.3"),sQuery(id+"F0.wireOp",EDGE,"E12.6.4"),sQuery(id+"F0.wireOp",EDGE,"E12.6.5"),sQuery(id+"F0.wireOp",EDGE,"E12.6.6"),sQuery(id+"F0.wireOp",EDGE,"E12.6.7"),sQuery(id+"F0.wireOp",EDGE,"E12.6.8"),sQuery(id+"F0.wireOp",EDGE,"E12.6.9"),sQuery(id+"F0.wireOp",EDGE,"E12.7.0"),sQuery(id+"F0.wireOp",EDGE,"E12.7.1"),sQuery(id+"F0.wireOp",EDGE,"E12.7.2"),sQuery(id+"F0.wireOp",EDGE,"E12.7.3"),sQuery(id+"F0.wireOp",EDGE,"E12.7.4"),sQuery(id+"F0.wireOp",EDGE,"E12.7.5"),sQuery(id+"F0.wireOp",EDGE,"E12.7.6"),sQuery(id+"F0.wireOp",EDGE,"E12.7.7"),sQuery(id+"F0.wireOp",EDGE,"E12.7.8"),sQuery(id+"F0.wireOp",EDGE,"E12.7.9"),sQuery(id+"F0.wireOp",EDGE,"E12.8.0"),sQuery(id+"F0.wireOp",EDGE,"E12.8.1"),sQuery(id+"F0.wireOp",EDGE,"E12.8.2"),sQuery(id+"F0.wireOp",EDGE,"E12.8.3"),sQuery(id+"F0.wireOp",EDGE,"E12.8.4"),sQuery(id+"F0.wireOp",EDGE,"E12.8.5"),sQuery(id+"F0.wireOp",EDGE,"E12.8.6"),sQuery(id+"F0.wireOp",EDGE,"E12.8.7"),sQuery(id+"F0.wireOp",EDGE,"E12.8.8"),sQuery(id+"F0.wireOp",EDGE,"E12.8.9"),sQuery(id+"F0.wireOp",EDGE,"E12.9.0"),sQuery(id+"F0.wireOp",EDGE,"E12.9.1"),sQuery(id+"F0.wireOp",EDGE,"E12.9.2"),sQuery(id+"F0.wireOp",EDGE,"E12.9.3"),sQuery(id+"F0.wireOp",EDGE,"E12.9.4"),sQuery(id+"F0.wireOp",EDGE,"E12.9.5"),sQuery(id+"F0.wireOp",EDGE,"E12.9.6"),sQuery(id+"F0.wireOp",EDGE,"E12.9.7"),sQuery(id+"F0.wireOp",EDGE,"E12.9.8"),sQuery(id+"F0.wireOp",EDGE,"E12.9.9"),sQuery(id+"F0.wireOp",EDGE,"E12.10.0"),sQuery(id+"F0.wireOp",EDGE,"E12.10.1"),sQuery(id+"F0.wireOp",EDGE,"E12.10.2"),sQuery(id+"F0.wireOp",EDGE,"E12.10.3"),sQuery(id+"F0.wireOp",EDGE,"E12.10.4"),sQuery(id+"F0.wireOp",EDGE,"E12.10.5"),sQuery(id+"F0.wireOp",EDGE,"E12.10.6"),sQuery(id+"F0.wireOp",EDGE,"E12.10.7"),sQuery(id+"F0.wireOp",EDGE,"E12.10.8"),sQuery(id+"F0.wireOp",EDGE,"E12.10.9"),sQuery(id+"F0.wireOp",EDGE,"E12.11.0"),sQuery(id+"F0.wireOp",EDGE,"E12.11.1"),sQuery(id+"F0.wireOp",EDGE,"E12.11.2"),sQuery(id+"F0.wireOp",EDGE,"E12.11.3"),sQuery(id+"F0.wireOp",EDGE,"E12.11.4"),sQuery(id+"F0.wireOp",EDGE,"E12.11.5"),sQuery(id+"F0.wireOp",EDGE,"E12.11.6"),sQuery(id+"F0.wireOp",EDGE,"E12.11.7"),sQuery(id+"F0.wireOp",EDGE,"E12.11.8"),sQuery(id+"F0.wireOp",EDGE,"E12.11.9"),sQuery(id+"F0.wireOp",EDGE,"E12.12.0"),sQuery(id+"F0.wireOp",EDGE,"E12.12.1"),sQuery(id+"F0.wireOp",EDGE,"E12.12.2"),sQuery(id+"F0.wireOp",EDGE,"E12.12.3"),sQuery(id+"F0.wireOp",EDGE,"E12.12.4"),sQuery(id+"F0.wireOp",EDGE,"E12.12.5"),sQuery(id+"F0.wireOp",EDGE,"E12.12.6"),sQuery(id+"F0.wireOp",EDGE,"E12.12.7"),sQuery(id+"F0.wireOp",EDGE,"E12.12.8"),sQuery(id+"F0.wireOp",EDGE,"E12.12.9"),sQuery(id+"F0.wireOp",EDGE,"E12.13.0"),sQuery(id+"F0.wireOp",EDGE,"E12.13.1"),sQuery(id+"F0.wireOp",EDGE,"E12.13.2"),sQuery(id+"F0.wireOp",EDGE,"E12.13.3"),sQuery(id+"F0.wireOp",EDGE,"E12.13.4"),sQuery(id+"F0.wireOp",EDGE,"E12.13.5"),sQuery(id+"F0.wireOp",EDGE,"E12.13.6"),sQuery(id+"F0.wireOp",EDGE,"E12.13.7"),sQuery(id+"F0.wireOp",EDGE,"E12.13.8"),sQuery(id+"F0.wireOp",EDGE,"E12.13.9"),sQuery(id+"F0.wireOp",EDGE,"E12.14.0"),sQuery(id+"F0.wireOp",EDGE,"E12.14.1"),sQuery(id+"F0.wireOp",EDGE,"E12.14.2"),sQuery(id+"F0.wireOp",EDGE,"E12.14.3"),sQuery(id+"F0.wireOp",EDGE,"E12.14.4"),sQuery(id+"F0.wireOp",EDGE,"E12.14.5"),sQuery(id+"F0.wireOp",EDGE,"E12.14.6"),sQuery(id+"F0.wireOp",EDGE,"E12.14.7"),sQuery(id+"F0.wireOp",EDGE,"E12.14.8"),sQuery(id+"F0.wireOp",EDGE,"E12.14.9"),sQuery(id+"F0.wireOp",EDGE,"E12.15.0"),sQuery(id+"F0.wireOp",EDGE,"E12.15.1"),sQuery(id+"F0.wireOp",EDGE,"E12.15.2"),sQuery(id+"F0.wireOp",EDGE,"E12.15.3"),sQuery(id+"F0.wireOp",EDGE,"E12.15.4"),sQuery(id+"F0.wireOp",EDGE,"E12.15.5"),sQuery(id+"F0.wireOp",EDGE,"E12.15.6"),sQuery(id+"F0.wireOp",EDGE,"E12.15.7"),sQuery(id+"F0.wireOp",EDGE,"E12.15.8"),sQuery(id+"F0.wireOp",EDGE,"E12.15.9"),sQuery(id+"F0.wireOp",EDGE,"E12.16.0"),sQuery(id+"F0.wireOp",EDGE,"E12.16.1"),sQuery(id+"F0.wireOp",EDGE,"E12.16.2"),sQuery(id+"F0.wireOp",EDGE,"E12.16.3"),sQuery(id+"F0.wireOp",EDGE,"E12.16.4"),sQuery(id+"F0.wireOp",EDGE,"E12.16.5"),sQuery(id+"F0.wireOp",EDGE,"E12.16.6"),sQuery(id+"F0.wireOp",EDGE,"E12.16.7"),sQuery(id+"F0.wireOp",EDGE,"E12.16.8"),sQuery(id+"F0.wireOp",EDGE,"E12.16.9"),sQuery(id+"F0.wireOp",EDGE,"E12.17.0"),sQuery(id+"F0.wireOp",EDGE,"E12.17.1"),sQuery(id+"F0.wireOp",EDGE,"E12.17.2"),sQuery(id+"F0.wireOp",EDGE,"E12.17.3"),sQuery(id+"F0.wireOp",EDGE,"E12.17.4"),sQuery(id+"F0.wireOp",EDGE,"E12.17.5"),sQuery(id+"F0.wireOp",EDGE,"E12.17.6"),sQuery(id+"F0.wireOp",EDGE,"E12.17.7"),sQuery(id+"F0.wireOp",EDGE,"E12.17.8"),sQuery(id+"F0.wireOp",EDGE,"E12.17.9"),sQuery(id+"F0.wireOp",EDGE,"E12.18.0"),sQuery(id+"F0.wireOp",EDGE,"E12.18.1"),sQuery(id+"F0.wireOp",EDGE,"E12.18.2"),sQuery(id+"F0.wireOp",EDGE,"E12.18.3"),sQuery(id+"F0.wireOp",EDGE,"E12.18.4"),sQuery(id+"F0.wireOp",EDGE,"E12.18.5"),sQuery(id+"F0.wireOp",EDGE,"E12.18.6"),sQuery(id+"F0.wireOp",EDGE,"E12.18.7"),sQuery(id+"F0.wireOp",EDGE,"E12.18.8"),sQuery(id+"F0.wireOp",EDGE,"E12.18.9"),sQuery(id+"F0.wireOp",EDGE,"E12.19.0"),sQuery(id+"F0.wireOp",EDGE,"E12.19.1"),sQuery(id+"F0.wireOp",EDGE,"E12.19.2"),sQuery(id+"F0.wireOp",EDGE,"E12.19.3"),sQuery(id+"F0.wireOp",EDGE,"E12.19.4"),sQuery(id+"F0.wireOp",EDGE,"E12.19.5"),sQuery(id+"F0.wireOp",EDGE,"E12.19.6"),sQuery(id+"F0.wireOp",EDGE,"E12.19.7"),sQuery(id+"F0.wireOp",EDGE,"E12.19.8"),sQuery(id+"F0.wireOp",EDGE,"E12.19.9"),sQuery(id+"F0.wireOp",EDGE,"E12.20.0"),sQuery(id+"F0.wireOp",EDGE,"E12.20.1"),sQuery(id+"F0.wireOp",EDGE,"E12.20.2"),sQuery(id+"F0.wireOp",EDGE,"E12.20.3"),sQuery(id+"F0.wireOp",EDGE,"E12.20.4"),sQuery(id+"F0.wireOp",EDGE,"E12.20.5"),sQuery(id+"F0.wireOp",EDGE,"E12.20.6"),sQuery(id+"F0.wireOp",EDGE,"E12.20.7"),sQuery(id+"F0.wireOp",EDGE,"E12.20.8"),sQuery(id+"F0.wireOp",EDGE,"E12.20.9"),sQuery(id+"F0.wireOp",EDGE,"E12.21.0"),sQuery(id+"F0.wireOp",EDGE,"E12.21.1"),sQuery(id+"F0.wireOp",EDGE,"E12.21.2"),sQuery(id+"F0.wireOp",EDGE,"E12.21.3"),sQuery(id+"F0.wireOp",EDGE,"E12.21.4"),sQuery(id+"F0.wireOp",EDGE,"E12.21.5"),sQuery(id+"F0.wireOp",EDGE,"E12.21.6"),sQuery(id+"F0.wireOp",EDGE,"E12.21.7"),sQuery(id+"F0.wireOp",EDGE,"E12.21.8"),sQuery(id+"F0.wireOp",EDGE,"E12.21.9"),sQuery(id+"F0.wireOp",EDGE,"E12.22.0"),sQuery(id+"F0.wireOp",EDGE,"E12.22.1"),sQuery(id+"F0.wireOp",EDGE,"E12.22.2"),sQuery(id+"F0.wireOp",EDGE,"E12.22.3"),sQuery(id+"F0.wireOp",EDGE,"E12.22.4"),sQuery(id+"F0.wireOp",EDGE,"E12.22.5"),sQuery(id+"F0.wireOp",EDGE,"E12.22.6"),sQuery(id+"F0.wireOp",EDGE,"E12.22.7"),sQuery(id+"F0.wireOp",EDGE,"E12.22.8"),sQuery(id+"F0.wireOp",EDGE,"E12.22.9"),sQuery(id+"F0.wireOp",EDGE,"E12.23.0"),sQuery(id+"F0.wireOp",EDGE,"E12.23.1"),sQuery(id+"F0.wireOp",EDGE,"E12.23.2"),sQuery(id+"F0.wireOp",EDGE,"E12.23.3"),sQuery(id+"F0.wireOp",EDGE,"E12.23.4"),sQuery(id+"F0.wireOp",EDGE,"E12.23.5"),sQuery(id+"F0.wireOp",EDGE,"E12.23.6"),sQuery(id+"F0.wireOp",EDGE,"E12.23.7"),sQuery(id+"F0.wireOp",EDGE,"E12.23.8"),sQuery(id+"F0.wireOp",EDGE,"E12.23.9"),sQuery(id+"F0.wireOp",EDGE,"E12.24.0"),sQuery(id+"F0.wireOp",EDGE,"E12.24.1"),sQuery(id+"F0.wireOp",EDGE,"E12.24.2"),sQuery(id+"F0.wireOp",EDGE,"E12.24.3"),sQuery(id+"F0.wireOp",EDGE,"E12.24.4"),sQuery(id+"F0.wireOp",EDGE,"E12.24.5"),sQuery(id+"F0.wireOp",EDGE,"E12.24.6"),sQuery(id+"F0.wireOp",EDGE,"E12.24.7"),sQuery(id+"F0.wireOp",EDGE,"E12.24.8"),sQuery(id+"F0.wireOp",EDGE,"E12.24.9"),sQuery(id+"F0.wireOp",EDGE,"E12.25.0"),sQuery(id+"F0.wireOp",EDGE,"E12.25.1"),sQuery(id+"F0.wireOp",EDGE,"E12.25.2"),sQuery(id+"F0.wireOp",EDGE,"E12.25.3"),sQuery(id+"F0.wireOp",EDGE,"E12.25.4"),sQuery(id+"F0.wireOp",EDGE,"E12.25.5"),sQuery(id+"F0.wireOp",EDGE,"E12.25.6"),sQuery(id+"F0.wireOp",EDGE,"E12.25.7"),sQuery(id+"F0.wireOp",EDGE,"E12.25.8"),sQuery(id+"F0.wireOp",EDGE,"E12.25.9"),sQuery(id+"F0.wireOp",EDGE,"E12.26.0"),sQuery(id+"F0.wireOp",EDGE,"E12.26.1"),sQuery(id+"F0.wireOp",EDGE,"E12.26.2"),sQuery(id+"F0.wireOp",EDGE,"E12.26.3"),sQuery(id+"F0.wireOp",EDGE,"E12.26.4"),sQuery(id+"F0.wireOp",EDGE,"E12.26.5"),sQuery(id+"F0.wireOp",EDGE,"E12.26.6"),sQuery(id+"F0.wireOp",EDGE,"E12.26.7"),sQuery(id+"F0.wireOp",EDGE,"E12.26.8"),sQuery(id+"F0.wireOp",EDGE,"E12.26.9"),sQuery(id+"F0.wireOp",EDGE,"E12.27.0"),sQuery(id+"F0.wireOp",EDGE,"E12.27.1"),sQuery(id+"F0.wireOp",EDGE,"E12.27.2"),sQuery(id+"F0.wireOp",EDGE,"E12.27.3"),sQuery(id+"F0.wireOp",EDGE,"E12.27.4"),sQuery(id+"F0.wireOp",EDGE,"E12.27.5"),sQuery(id+"F0.wireOp",EDGE,"E12.27.6"),sQuery(id+"F0.wireOp",EDGE,"E12.27.7"),sQuery(id+"F0.wireOp",EDGE,"E12.27.8"),sQuery(id+"F0.wireOp",EDGE,"E12.27.9"),sQuery(id+"F0.wireOp",EDGE,"E12.28.0"),sQuery(id+"F0.wireOp",EDGE,"E12.28.1"),sQuery(id+"F0.wireOp",EDGE,"E12.28.2"),sQuery(id+"F0.wireOp",EDGE,"E12.28.3"),sQuery(id+"F0.wireOp",EDGE,"E12.28.4"),sQuery(id+"F0.wireOp",EDGE,"E12.28.5"),sQuery(id+"F0.wireOp",EDGE,"E12.28.6"),sQuery(id+"F0.wireOp",EDGE,"E12.28.7"),sQuery(id+"F0.wireOp",EDGE,"E12.28.8"),sQuery(id+"F0.wireOp",EDGE,"E12.28.9"),sQuery(id+"F0.wireOp",EDGE,"E12.29.0"),sQuery(id+"F0.wireOp",EDGE,"E12.29.1"),sQuery(id+"F0.wireOp",EDGE,"E12.29.2"),sQuery(id+"F0.wireOp",EDGE,"E12.29.3"),sQuery(id+"F0.wireOp",EDGE,"E12.29.4"),sQuery(id+"F0.wireOp",EDGE,"E12.29.5"),sQuery(id+"F0.wireOp",EDGE,"E12.29.6"),sQuery(id+"F0.wireOp",EDGE,"E12.29.7"),sQuery(id+"F0.wireOp",EDGE,"E12.29.8"),sQuery(id+"F0.wireOp",EDGE,"E12.29.9"),sQuery(id+"F0.wireOp",EDGE,"E12.30.0"),sQuery(id+"F0.wireOp",EDGE,"E12.30.1"),sQuery(id+"F0.wireOp",EDGE,"E12.30.2"),sQuery(id+"F0.wireOp",EDGE,"E12.30.3"),sQuery(id+"F0.wireOp",EDGE,"E12.30.4"),sQuery(id+"F0.wireOp",EDGE,"E12.30.5"),sQuery(id+"F0.wireOp",EDGE,"E12.30.6"),sQuery(id+"F0.wireOp",EDGE,"E12.30.7"),sQuery(id+"F0.wireOp",EDGE,"E12.30.8"),sQuery(id+"F0.wireOp",EDGE,"E12.30.9"),sQuery(id+"F0.wireOp",EDGE,"E12.31.0"),sQuery(id+"F0.wireOp",EDGE,"E12.31.1"),sQuery(id+"F0.wireOp",EDGE,"E12.31.2"),sQuery(id+"F0.wireOp",EDGE,"E12.31.3"),sQuery(id+"F0.wireOp",EDGE,"E12.31.4"),sQuery(id+"F0.wireOp",EDGE,"E12.31.5"),sQuery(id+"F0.wireOp",EDGE,"E12.31.6"),sQuery(id+"F0.wireOp",EDGE,"E12.31.7"),sQuery(id+"F0.wireOp",EDGE,"E12.31.8"),sQuery(id+"F0.wireOp",EDGE,"E12.31.9"),sQuery(id+"F0.wireOp",EDGE,"E12.32.0"),sQuery(id+"F0.wireOp",EDGE,"E12.32.1"),sQuery(id+"F0.wireOp",EDGE,"E12.32.2"),sQuery(id+"F0.wireOp",EDGE,"E12.32.3"),sQuery(id+"F0.wireOp",EDGE,"E12.32.4"),sQuery(id+"F0.wireOp",EDGE,"E12.32.5"),sQuery(id+"F0.wireOp",EDGE,"E12.32.6"),sQuery(id+"F0.wireOp",EDGE,"E12.32.7"),sQuery(id+"F0.wireOp",EDGE,"E12.32.8"),sQuery(id+"F0.wireOp",EDGE,"E12.32.9"),sQuery(id+"F0.wireOp",EDGE,"E12.33.0"),sQuery(id+"F0.wireOp",EDGE,"E12.33.1"),sQuery(id+"F0.wireOp",EDGE,"E12.33.2"),sQuery(id+"F0.wireOp",EDGE,"E12.33.3"),sQuery(id+"F0.wireOp",EDGE,"E12.33.4"),sQuery(id+"F0.wireOp",EDGE,"E12.33.5"),sQuery(id+"F0.wireOp",EDGE,"E12.33.6"),sQuery(id+"F0.wireOp",EDGE,"E12.33.7"),sQuery(id+"F0.wireOp",EDGE,"E12.33.8"),sQuery(id+"F0.wireOp",EDGE,"E12.33.9"),sQuery(id+"F0.wireOp",EDGE,"E12.34.0"),sQuery(id+"F0.wireOp",EDGE,"E12.34.1"),sQuery(id+"F0.wireOp",EDGE,"E12.34.2"),sQuery(id+"F0.wireOp",EDGE,"E12.34.3"),sQuery(id+"F0.wireOp",EDGE,"E12.34.4"),sQuery(id+"F0.wireOp",EDGE,"E12.34.5"),sQuery(id+"F0.wireOp",EDGE,"E12.34.6"),sQuery(id+"F0.wireOp",EDGE,"E12.34.7"),sQuery(id+"F0.wireOp",EDGE,"E12.34.8"),sQuery(id+"F0.wireOp",EDGE,"E12.34.9"),sQuery(id+"F0.wireOp",EDGE,"E12.35.0"),sQuery(id+"F0.wireOp",EDGE,"E12.35.1"),sQuery(id+"F0.wireOp",EDGE,"E12.35.2"),sQuery(id+"F0.wireOp",EDGE,"E12.35.3"),sQuery(id+"F0.wireOp",EDGE,"E12.35.4"),sQuery(id+"F0.wireOp",EDGE,"E12.35.5"),sQuery(id+"F0.wireOp",EDGE,"E12.35.6"),sQuery(id+"F0.wireOp",EDGE,"E12.35.7"),sQuery(id+"F0.wireOp",EDGE,"E12.35.8"),sQuery(id+"F0.wireOp",EDGE,"E12.35.9"),sQuery(id+"F0.wireOp",EDGE,"E12.36.0"),sQuery(id+"F0.wireOp",EDGE,"E12.36.1"),sQuery(id+"F0.wireOp",EDGE,"E12.36.2"),sQuery(id+"F0.wireOp",EDGE,"E12.36.3"),sQuery(id+"F0.wireOp",EDGE,"E12.36.4"),sQuery(id+"F0.wireOp",EDGE,"E12.36.5"),sQuery(id+"F0.wireOp",EDGE,"E12.36.6"),sQuery(id+"F0.wireOp",EDGE,"E12.36.7"),sQuery(id+"F0.wireOp",EDGE,"E12.36.8"),sQuery(id+"F0.wireOp",EDGE,"E12.36.9"),sQuery(id+"F0.wireOp",EDGE,"E12.37.0"),sQuery(id+"F0.wireOp",EDGE,"E12.37.1"),sQuery(id+"F0.wireOp",EDGE,"E12.37.2"),sQuery(id+"F0.wireOp",EDGE,"E12.37.3"),sQuery(id+"F0.wireOp",EDGE,"E12.37.4"),sQuery(id+"F0.wireOp",EDGE,"E12.37.5"),sQuery(id+"F0.wireOp",EDGE,"E12.37.6"),sQuery(id+"F0.wireOp",EDGE,"E12.37.7"),sQuery(id+"F0.wireOp",EDGE,"E12.37.8"),sQuery(id+"F0.wireOp",EDGE,"E12.37.9"),sQuery(id+"F0.wireOp",EDGE,"E12.38.0"),sQuery(id+"F0.wireOp",EDGE,"E12.38.1"),sQuery(id+"F0.wireOp",EDGE,"E12.38.2"),sQuery(id+"F0.wireOp",EDGE,"E12.38.3"),sQuery(id+"F0.wireOp",EDGE,"E12.38.4"),sQuery(id+"F0.wireOp",EDGE,"E12.38.5"),sQuery(id+"F0.wireOp",EDGE,"E12.38.6"),sQuery(id+"F0.wireOp",EDGE,"E12.38.7"),sQuery(id+"F0.wireOp",EDGE,"E12.38.8"),sQuery(id+"F0.wireOp",EDGE,"E12.38.9"),sQuery(id+"F0.wireOp",EDGE,"E12.39.0"),sQuery(id+"F0.wireOp",EDGE,"E12.39.1"),sQuery(id+"F0.wireOp",EDGE,"E12.39.2"),sQuery(id+"F0.wireOp",EDGE,"E12.39.3"),sQuery(id+"F0.wireOp",EDGE,"E12.39.4"),sQuery(id+"F0.wireOp",EDGE,"E12.39.5"),sQuery(id+"F0.wireOp",EDGE,"E12.39.6"),sQuery(id+"F0.wireOp",EDGE,"E12.39.7"),sQuery(id+"F0.wireOp",EDGE,"E12.39.8"),sQuery(id+"F0.wireOp",EDGE,"E12.39.9"),sQuery(id+"F0.wireOp",EDGE,"E12.40.0"),sQuery(id+"F0.wireOp",EDGE,"E12.40.1"),sQuery(id+"F0.wireOp",EDGE,"E12.40.2"),sQuery(id+"F0.wireOp",EDGE,"E12.40.3"),sQuery(id+"F0.wireOp",EDGE,"E12.40.4"),sQuery(id+"F0.wireOp",EDGE,"E12.40.5"),sQuery(id+"F0.wireOp",EDGE,"E12.40.6"),sQuery(id+"F0.wireOp",EDGE,"E12.40.7"),sQuery(id+"F0.wireOp",EDGE,"E12.40.8"),sQuery(id+"F0.wireOp",EDGE,"E12.40.9"),sQuery(id+"F0.wireOp",EDGE,"E12.41.0"),sQuery(id+"F0.wireOp",EDGE,"E12.41.1"),sQuery(id+"F0.wireOp",EDGE,"E12.41.2"),sQuery(id+"F0.wireOp",EDGE,"E12.41.3"),sQuery(id+"F0.wireOp",EDGE,"E12.41.4"),sQuery(id+"F0.wireOp",EDGE,"E12.41.5"),sQuery(id+"F0.wireOp",EDGE,"E12.41.6"),sQuery(id+"F0.wireOp",EDGE,"E12.41.7"),sQuery(id+"F0.wireOp",EDGE,"E12.41.8"),sQuery(id+"F0.wireOp",EDGE,"E12.41.9"),sQuery(id+"F0.wireOp",EDGE,"E12.42.0"),sQuery(id+"F0.wireOp",EDGE,"E12.42.1"),sQuery(id+"F0.wireOp",EDGE,"E12.42.2"),sQuery(id+"F0.wireOp",EDGE,"E12.42.3"),sQuery(id+"F0.wireOp",EDGE,"E12.42.4"),sQuery(id+"F0.wireOp",EDGE,"E12.42.5"),sQuery(id+"F0.wireOp",EDGE,"E12.42.6"),sQuery(id+"F0.wireOp",EDGE,"E12.42.7"),sQuery(id+"F0.wireOp",EDGE,"E12.42.8"),sQuery(id+"F0.wireOp",EDGE,"E12.42.9"),sQuery(id+"F0.wireOp",EDGE,"E12.43.0"),sQuery(id+"F0.wireOp",EDGE,"E12.43.1"),sQuery(id+"F0.wireOp",EDGE,"E12.43.2"),sQuery(id+"F0.wireOp",EDGE,"E12.43.3"),sQuery(id+"F0.wireOp",EDGE,"E12.43.4"),sQuery(id+"F0.wireOp",EDGE,"E12.43.5"),sQuery(id+"F0.wireOp",EDGE,"E12.43.6"),sQuery(id+"F0.wireOp",EDGE,"E12.43.7"),sQuery(id+"F0.wireOp",EDGE,"E12.43.8"),sQuery(id+"F0.wireOp",EDGE,"E12.43.9"),sQuery(id+"F0.wireOp",EDGE,"E12.44.0"),sQuery(id+"F0.wireOp",EDGE,"E12.44.1"),sQuery(id+"F0.wireOp",EDGE,"E12.44.2"),sQuery(id+"F0.wireOp",EDGE,"E12.44.3"),sQuery(id+"F0.wireOp",EDGE,"E12.44.4"),sQuery(id+"F0.wireOp",EDGE,"E12.44.5"),sQuery(id+"F0.wireOp",EDGE,"E12.44.6"),sQuery(id+"F0.wireOp",EDGE,"E12.44.7"),sQuery(id+"F0.wireOp",EDGE,"E12.44.8"),sQuery(id+"F0.wireOp",EDGE,"E12.44.9"),sQuery(id+"F0.wireOp",EDGE,"E12.45.0"),sQuery(id+"F0.wireOp",EDGE,"E12.45.1"),sQuery(id+"F0.wireOp",EDGE,"E12.45.2"),sQuery(id+"F0.wireOp",EDGE,"E12.45.3"),sQuery(id+"F0.wireOp",EDGE,"E12.45.4"),sQuery(id+"F0.wireOp",EDGE,"E12.45.5"),sQuery(id+"F0.wireOp",EDGE,"E12.45.6"),sQuery(id+"F0.wireOp",EDGE,"E12.45.7"),sQuery(id+"F0.wireOp",EDGE,"E12.45.8"),sQuery(id+"F0.wireOp",EDGE,"E12.45.9"),sQuery(id+"F0.wireOp",EDGE,"E12.46.0"),sQuery(id+"F0.wireOp",EDGE,"E12.46.1"),sQuery(id+"F0.wireOp",EDGE,"E12.46.2"),sQuery(id+"F0.wireOp",EDGE,"E12.46.3"),sQuery(id+"F0.wireOp",EDGE,"E12.46.4"),sQuery(id+"F0.wireOp",EDGE,"E12.46.5"),sQuery(id+"F0.wireOp",EDGE,"E12.46.6"),sQuery(id+"F0.wireOp",EDGE,"E12.46.7"),sQuery(id+"F0.wireOp",EDGE,"E12.46.8"),sQuery(id+"F0.wireOp",EDGE,"E12.46.9"),sQuery(id+"F0.wireOp",EDGE,"E12.47.0"),sQuery(id+"F0.wireOp",EDGE,"E12.47.1"),sQuery(id+"F0.wireOp",EDGE,"E12.47.2"),sQuery(id+"F0.wireOp",EDGE,"E12.47.3"),sQuery(id+"F0.wireOp",EDGE,"E12.47.4"),sQuery(id+"F0.wireOp",EDGE,"E12.47.5"),sQuery(id+"F0.wireOp",EDGE,"E12.47.6"),sQuery(id+"F0.wireOp",EDGE,"E12.47.7"),sQuery(id+"F0.wireOp",EDGE,"E12.47.8"),sQuery(id+"F0.wireOp",EDGE,"E12.47.9"),sQuery(id+"F0.wireOp",EDGE,"E12.48.0"),sQuery(id+"F0.wireOp",EDGE,"E12.48.1"),sQuery(id+"F0.wireOp",EDGE,"E12.48.2"),sQuery(id+"F0.wireOp",EDGE,"E12.48.3"),sQuery(id+"F0.wireOp",EDGE,"E12.48.4"),sQuery(id+"F0.wireOp",EDGE,"E12.48.5"),sQuery(id+"F0.wireOp",EDGE,"E12.48.6"),sQuery(id+"F0.wireOp",EDGE,"E12.48.7"),sQuery(id+"F0.wireOp",EDGE,"E12.48.8"),sQuery(id+"F0.wireOp",EDGE,"E12.48.9"),sQuery(id+"F0.wireOp",EDGE,"E12.49.0"),sQuery(id+"F0.wireOp",EDGE,"E12.49.1"),sQuery(id+"F0.wireOp",EDGE,"E12.49.2"),sQuery(id+"F0.wireOp",EDGE,"E12.49.3"),sQuery(id+"F0.wireOp",EDGE,"E12.49.4"),sQuery(id+"F0.wireOp",EDGE,"E12.49.5"),sQuery(id+"F0.wireOp",EDGE,"E12.49.6"),sQuery(id+"F0.wireOp",EDGE,"E12.49.7"),sQuery(id+"F0.wireOp",EDGE,"E12.49.8"),sQuery(id+"F0.wireOp",EDGE,"E12.49.9"),sQuery(id+"F0.wireOp",EDGE,"E12.50.0"),sQuery(id+"F0.wireOp",EDGE,"E12.50.1"),sQuery(id+"F0.wireOp",EDGE,"E12.50.2"),sQuery(id+"F0.wireOp",EDGE,"E12.50.3"),sQuery(id+"F0.wireOp",EDGE,"E12.50.4"),sQuery(id+"F0.wireOp",EDGE,"E12.50.5"),sQuery(id+"F0.wireOp",EDGE,"E12.50.6"),sQuery(id+"F0.wireOp",EDGE,"E12.50.7"),sQuery(id+"F0.wireOp",EDGE,"E12.50.8"),sQuery(id+"F0.wireOp",EDGE,"E12.50.9"),sQuery(id+"F0.wireOp",EDGE,"E12.51.0"),sQuery(id+"F0.wireOp",EDGE,"E12.51.1"),sQuery(id+"F0.wireOp",EDGE,"E12.51.2"),sQuery(id+"F0.wireOp",EDGE,"E12.51.3"),sQuery(id+"F0.wireOp",EDGE,"E12.51.4"),sQuery(id+"F0.wireOp",EDGE,"E12.51.5"),sQuery(id+"F0.wireOp",EDGE,"E12.51.6"),sQuery(id+"F0.wireOp",EDGE,"E12.51.7"),sQuery(id+"F0.wireOp",EDGE,"E12.51.8"),sQuery(id+"F0.wireOp",EDGE,"E12.51.9"),sQuery(id+"F0.wireOp",EDGE,"E12.52.0"),sQuery(id+"F0.wireOp",EDGE,"E12.52.1"),sQuery(id+"F0.wireOp",EDGE,"E12.52.2"),sQuery(id+"F0.wireOp",EDGE,"E12.52.3"),sQuery(id+"F0.wireOp",EDGE,"E12.52.4"),sQuery(id+"F0.wireOp",EDGE,"E12.52.5"),sQuery(id+"F0.wireOp",EDGE,"E12.52.6"),sQuery(id+"F0.wireOp",EDGE,"E12.52.7"),sQuery(id+"F0.wireOp",EDGE,"E12.52.8"),sQuery(id+"F0.wireOp",EDGE,"E12.52.9"),sQuery(id+"F0.wireOp",EDGE,"E12.53.0"),sQuery(id+"F0.wireOp",EDGE,"E12.53.1"),sQuery(id+"F0.wireOp",EDGE,"E12.53.2"),sQuery(id+"F0.wireOp",EDGE,"E12.53.3"),sQuery(id+"F0.wireOp",EDGE,"E12.53.4"),sQuery(id+"F0.wireOp",EDGE,"E12.53.5"),sQuery(id+"F0.wireOp",EDGE,"E12.53.6"),sQuery(id+"F0.wireOp",EDGE,"E12.53.7"),sQuery(id+"F0.wireOp",EDGE,"E12.53.8"),sQuery(id+"F0.wireOp",EDGE,"E12.53.9"),sQuery(id+"F0.wireOp",EDGE,"E12.54.0"),sQuery(id+"F0.wireOp",EDGE,"E12.54.1"),sQuery(id+"F0.wireOp",EDGE,"E12.54.2"),sQuery(id+"F0.wireOp",EDGE,"E12.54.3"),sQuery(id+"F0.wireOp",EDGE,"E12.54.4"),sQuery(id+"F0.wireOp",EDGE,"E12.54.5"),sQuery(id+"F0.wireOp",EDGE,"E12.54.6"),sQuery(id+"F0.wireOp",EDGE,"E12.54.7"),sQuery(id+"F0.wireOp",EDGE,"E12.54.8"),sQuery(id+"F0.wireOp",EDGE,"E12.54.9"),sQuery(id+"F0.wireOp",EDGE,"E12.55.0"),sQuery(id+"F0.wireOp",EDGE,"E12.55.1"),sQuery(id+"F0.wireOp",EDGE,"E12.55.2"),sQuery(id+"F0.wireOp",EDGE,"E12.55.3"),sQuery(id+"F0.wireOp",EDGE,"E12.55.4"),sQuery(id+"F0.wireOp",EDGE,"E12.55.5"),sQuery(id+"F0.wireOp",EDGE,"E12.55.6"),sQuery(id+"F0.wireOp",EDGE,"E12.55.7"),sQuery(id+"F0.wireOp",EDGE,"E12.55.8"),sQuery(id+"F0.wireOp",EDGE,"E12.55.9"),sQuery(id+"F0.wireOp",EDGE,"E12.56.0"),sQuery(id+"F0.wireOp",EDGE,"E12.56.1"),sQuery(id+"F0.wireOp",EDGE,"E12.56.2"),sQuery(id+"F0.wireOp",EDGE,"E12.56.3"),sQuery(id+"F0.wireOp",EDGE,"E12.56.4"),sQuery(id+"F0.wireOp",EDGE,"E12.56.5"),sQuery(id+"F0.wireOp",EDGE,"E12.56.6"),sQuery(id+"F0.wireOp",EDGE,"E12.56.7"),sQuery(id+"F0.wireOp",EDGE,"E12.56.8"),sQuery(id+"F0.wireOp",EDGE,"E12.56.9"),sQuery(id+"F0.wireOp",EDGE,"E12.57.0"),sQuery(id+"F0.wireOp",EDGE,"E12.57.1"),sQuery(id+"F0.wireOp",EDGE,"E12.57.2"),sQuery(id+"F0.wireOp",EDGE,"E12.57.3"),sQuery(id+"F0.wireOp",EDGE,"E12.57.4"),sQuery(id+"F0.wireOp",EDGE,"E12.57.5"),sQuery(id+"F0.wireOp",EDGE,"E12.57.6"),sQuery(id+"F0.wireOp",EDGE,"E12.57.7"),sQuery(id+"F0.wireOp",EDGE,"E12.57.8"),sQuery(id+"F0.wireOp",EDGE,"E12.57.9"),sQuery(id+"F0.wireOp",EDGE,"E12.58.0"),sQuery(id+"F0.wireOp",EDGE,"E12.58.1"),sQuery(id+"F0.wireOp",EDGE,"E12.58.2"),sQuery(id+"F0.wireOp",EDGE,"E12.58.3"),sQuery(id+"F0.wireOp",EDGE,"E12.58.4"),sQuery(id+"F0.wireOp",EDGE,"E12.58.5"),sQuery(id+"F0.wireOp",EDGE,"E12.58.6"),sQuery(id+"F0.wireOp",EDGE,"E12.58.7"),sQuery(id+"F0.wireOp",EDGE,"E12.58.8"),sQuery(id+"F0.wireOp",EDGE,"E12.58.9"),sQuery(id+"F0.wireOp",EDGE,"E12.59.0"),sQuery(id+"F0.wireOp",EDGE,"E12.59.1"),sQuery(id+"F0.wireOp",EDGE,"E12.59.2"),sQuery(id+"F0.wireOp",EDGE,"E12.59.3"),sQuery(id+"F0.wireOp",EDGE,"E12.59.4"),sQuery(id+"F0.wireOp",EDGE,"E12.59.5"),sQuery(id+"F0.wireOp",EDGE,"E12.59.6"),sQuery(id+"F0.wireOp",EDGE,"E12.59.7"),sQuery(id+"F0.wireOp",EDGE,"E12.59.8"),sQuery(id+"F0.wireOp",EDGE,"E12.59.9"),sQuery(id+"F0.wireOp",EDGE,"E13.trimOffspring"),sQuery(id+"F0.wireOp",EDGE,"E14.trimOffspring")])],"isStart":true}),makeQuery(id+"F3.opExtrude","SWEPT_FACE",FACE,{"disambiguationData":[OSD([sQuery(id+"F2.wireOp",EDGE,"E17.1.0")])]})]});
            var Q10;
            Q10=makeQuery(id+"F3.boolean.opBoolean","INTERSECT",EDGE,{"derivedFrom":[makeQuery(id+"F1.opExtrude","CAP_FACE",FACE,{"disambiguationData":[OSD([sQuery(id+"F0.wireOp",EDGE,"E0"),sQuery(id+"F0.wireOp",EDGE,"E2"),sQuery(id+"F0.wireOp",EDGE,"E3"),sQuery(id+"F0.wireOp",EDGE,"E4.trimOffspring"),sQuery(id+"F0.wireOp",EDGE,"E5.MirrorCS"),sQuery(id+"F0.wireOp",EDGE,"E6.MirrorCS"),sQuery(id+"F0.wireOp",EDGE,"E7.MirrorCS"),sQuery(id+"F0.wireOp",EDGE,"E8.filletArc"),sQuery(id+"F0.wireOp",EDGE,"E9.filletArc"),sQuery(id+"F0.wireOp",EDGE,"E10.filletArc"),sQuery(id+"F0.wireOp",EDGE,"E11.filletArc"),sQuery(id+"F0.wireOp",EDGE,"E12.1.0"),sQuery(id+"F0.wireOp",EDGE,"E12.1.1"),sQuery(id+"F0.wireOp",EDGE,"E12.1.2"),sQuery(id+"F0.wireOp",EDGE,"E12.1.3"),sQuery(id+"F0.wireOp",EDGE,"E12.1.4"),sQuery(id+"F0.wireOp",EDGE,"E12.1.5"),sQuery(id+"F0.wireOp",EDGE,"E12.1.6"),sQuery(id+"F0.wireOp",EDGE,"E12.1.7"),sQuery(id+"F0.wireOp",EDGE,"E12.1.8"),sQuery(id+"F0.wireOp",EDGE,"E12.1.9"),sQuery(id+"F0.wireOp",EDGE,"E12.2.0"),sQuery(id+"F0.wireOp",EDGE,"E12.2.1"),sQuery(id+"F0.wireOp",EDGE,"E12.2.2"),sQuery(id+"F0.wireOp",EDGE,"E12.2.3"),sQuery(id+"F0.wireOp",EDGE,"E12.2.4"),sQuery(id+"F0.wireOp",EDGE,"E12.2.5"),sQuery(id+"F0.wireOp",EDGE,"E12.2.6"),sQuery(id+"F0.wireOp",EDGE,"E12.2.7"),sQuery(id+"F0.wireOp",EDGE,"E12.2.8"),sQuery(id+"F0.wireOp",EDGE,"E12.2.9"),sQuery(id+"F0.wireOp",EDGE,"E12.3.0"),sQuery(id+"F0.wireOp",EDGE,"E12.3.1"),sQuery(id+"F0.wireOp",EDGE,"E12.3.2"),sQuery(id+"F0.wireOp",EDGE,"E12.3.3"),sQuery(id+"F0.wireOp",EDGE,"E12.3.4"),sQuery(id+"F0.wireOp",EDGE,"E12.3.5"),sQuery(id+"F0.wireOp",EDGE,"E12.3.6"),sQuery(id+"F0.wireOp",EDGE,"E12.3.7"),sQuery(id+"F0.wireOp",EDGE,"E12.3.8"),sQuery(id+"F0.wireOp",EDGE,"E12.3.9"),sQuery(id+"F0.wireOp",EDGE,"E12.4.0"),sQuery(id+"F0.wireOp",EDGE,"E12.4.1"),sQuery(id+"F0.wireOp",EDGE,"E12.4.2"),sQuery(id+"F0.wireOp",EDGE,"E12.4.3"),sQuery(id+"F0.wireOp",EDGE,"E12.4.4"),sQuery(id+"F0.wireOp",EDGE,"E12.4.5"),sQuery(id+"F0.wireOp",EDGE,"E12.4.6"),sQuery(id+"F0.wireOp",EDGE,"E12.4.7"),sQuery(id+"F0.wireOp",EDGE,"E12.4.8"),sQuery(id+"F0.wireOp",EDGE,"E12.4.9"),sQuery(id+"F0.wireOp",EDGE,"E12.5.0"),sQuery(id+"F0.wireOp",EDGE,"E12.5.1"),sQuery(id+"F0.wireOp",EDGE,"E12.5.2"),sQuery(id+"F0.wireOp",EDGE,"E12.5.3"),sQuery(id+"F0.wireOp",EDGE,"E12.5.4"),sQuery(id+"F0.wireOp",EDGE,"E12.5.5"),sQuery(id+"F0.wireOp",EDGE,"E12.5.6"),sQuery(id+"F0.wireOp",EDGE,"E12.5.7"),sQuery(id+"F0.wireOp",EDGE,"E12.5.8"),sQuery(id+"F0.wireOp",EDGE,"E12.5.9"),sQuery(id+"F0.wireOp",EDGE,"E12.6.0"),sQuery(id+"F0.wireOp",EDGE,"E12.6.1"),sQuery(id+"F0.wireOp",EDGE,"E12.6.2"),sQuery(id+"F0.wireOp",EDGE,"E12.6.3"),sQuery(id+"F0.wireOp",EDGE,"E12.6.4"),sQuery(id+"F0.wireOp",EDGE,"E12.6.5"),sQuery(id+"F0.wireOp",EDGE,"E12.6.6"),sQuery(id+"F0.wireOp",EDGE,"E12.6.7"),sQuery(id+"F0.wireOp",EDGE,"E12.6.8"),sQuery(id+"F0.wireOp",EDGE,"E12.6.9"),sQuery(id+"F0.wireOp",EDGE,"E12.7.0"),sQuery(id+"F0.wireOp",EDGE,"E12.7.1"),sQuery(id+"F0.wireOp",EDGE,"E12.7.2"),sQuery(id+"F0.wireOp",EDGE,"E12.7.3"),sQuery(id+"F0.wireOp",EDGE,"E12.7.4"),sQuery(id+"F0.wireOp",EDGE,"E12.7.5"),sQuery(id+"F0.wireOp",EDGE,"E12.7.6"),sQuery(id+"F0.wireOp",EDGE,"E12.7.7"),sQuery(id+"F0.wireOp",EDGE,"E12.7.8"),sQuery(id+"F0.wireOp",EDGE,"E12.7.9"),sQuery(id+"F0.wireOp",EDGE,"E12.8.0"),sQuery(id+"F0.wireOp",EDGE,"E12.8.1"),sQuery(id+"F0.wireOp",EDGE,"E12.8.2"),sQuery(id+"F0.wireOp",EDGE,"E12.8.3"),sQuery(id+"F0.wireOp",EDGE,"E12.8.4"),sQuery(id+"F0.wireOp",EDGE,"E12.8.5"),sQuery(id+"F0.wireOp",EDGE,"E12.8.6"),sQuery(id+"F0.wireOp",EDGE,"E12.8.7"),sQuery(id+"F0.wireOp",EDGE,"E12.8.8"),sQuery(id+"F0.wireOp",EDGE,"E12.8.9"),sQuery(id+"F0.wireOp",EDGE,"E12.9.0"),sQuery(id+"F0.wireOp",EDGE,"E12.9.1"),sQuery(id+"F0.wireOp",EDGE,"E12.9.2"),sQuery(id+"F0.wireOp",EDGE,"E12.9.3"),sQuery(id+"F0.wireOp",EDGE,"E12.9.4"),sQuery(id+"F0.wireOp",EDGE,"E12.9.5"),sQuery(id+"F0.wireOp",EDGE,"E12.9.6"),sQuery(id+"F0.wireOp",EDGE,"E12.9.7"),sQuery(id+"F0.wireOp",EDGE,"E12.9.8"),sQuery(id+"F0.wireOp",EDGE,"E12.9.9"),sQuery(id+"F0.wireOp",EDGE,"E12.10.0"),sQuery(id+"F0.wireOp",EDGE,"E12.10.1"),sQuery(id+"F0.wireOp",EDGE,"E12.10.2"),sQuery(id+"F0.wireOp",EDGE,"E12.10.3"),sQuery(id+"F0.wireOp",EDGE,"E12.10.4"),sQuery(id+"F0.wireOp",EDGE,"E12.10.5"),sQuery(id+"F0.wireOp",EDGE,"E12.10.6"),sQuery(id+"F0.wireOp",EDGE,"E12.10.7"),sQuery(id+"F0.wireOp",EDGE,"E12.10.8"),sQuery(id+"F0.wireOp",EDGE,"E12.10.9"),sQuery(id+"F0.wireOp",EDGE,"E12.11.0"),sQuery(id+"F0.wireOp",EDGE,"E12.11.1"),sQuery(id+"F0.wireOp",EDGE,"E12.11.2"),sQuery(id+"F0.wireOp",EDGE,"E12.11.3"),sQuery(id+"F0.wireOp",EDGE,"E12.11.4"),sQuery(id+"F0.wireOp",EDGE,"E12.11.5"),sQuery(id+"F0.wireOp",EDGE,"E12.11.6"),sQuery(id+"F0.wireOp",EDGE,"E12.11.7"),sQuery(id+"F0.wireOp",EDGE,"E12.11.8"),sQuery(id+"F0.wireOp",EDGE,"E12.11.9"),sQuery(id+"F0.wireOp",EDGE,"E12.12.0"),sQuery(id+"F0.wireOp",EDGE,"E12.12.1"),sQuery(id+"F0.wireOp",EDGE,"E12.12.2"),sQuery(id+"F0.wireOp",EDGE,"E12.12.3"),sQuery(id+"F0.wireOp",EDGE,"E12.12.4"),sQuery(id+"F0.wireOp",EDGE,"E12.12.5"),sQuery(id+"F0.wireOp",EDGE,"E12.12.6"),sQuery(id+"F0.wireOp",EDGE,"E12.12.7"),sQuery(id+"F0.wireOp",EDGE,"E12.12.8"),sQuery(id+"F0.wireOp",EDGE,"E12.12.9"),sQuery(id+"F0.wireOp",EDGE,"E12.13.0"),sQuery(id+"F0.wireOp",EDGE,"E12.13.1"),sQuery(id+"F0.wireOp",EDGE,"E12.13.2"),sQuery(id+"F0.wireOp",EDGE,"E12.13.3"),sQuery(id+"F0.wireOp",EDGE,"E12.13.4"),sQuery(id+"F0.wireOp",EDGE,"E12.13.5"),sQuery(id+"F0.wireOp",EDGE,"E12.13.6"),sQuery(id+"F0.wireOp",EDGE,"E12.13.7"),sQuery(id+"F0.wireOp",EDGE,"E12.13.8"),sQuery(id+"F0.wireOp",EDGE,"E12.13.9"),sQuery(id+"F0.wireOp",EDGE,"E12.14.0"),sQuery(id+"F0.wireOp",EDGE,"E12.14.1"),sQuery(id+"F0.wireOp",EDGE,"E12.14.2"),sQuery(id+"F0.wireOp",EDGE,"E12.14.3"),sQuery(id+"F0.wireOp",EDGE,"E12.14.4"),sQuery(id+"F0.wireOp",EDGE,"E12.14.5"),sQuery(id+"F0.wireOp",EDGE,"E12.14.6"),sQuery(id+"F0.wireOp",EDGE,"E12.14.7"),sQuery(id+"F0.wireOp",EDGE,"E12.14.8"),sQuery(id+"F0.wireOp",EDGE,"E12.14.9"),sQuery(id+"F0.wireOp",EDGE,"E12.15.0"),sQuery(id+"F0.wireOp",EDGE,"E12.15.1"),sQuery(id+"F0.wireOp",EDGE,"E12.15.2"),sQuery(id+"F0.wireOp",EDGE,"E12.15.3"),sQuery(id+"F0.wireOp",EDGE,"E12.15.4"),sQuery(id+"F0.wireOp",EDGE,"E12.15.5"),sQuery(id+"F0.wireOp",EDGE,"E12.15.6"),sQuery(id+"F0.wireOp",EDGE,"E12.15.7"),sQuery(id+"F0.wireOp",EDGE,"E12.15.8"),sQuery(id+"F0.wireOp",EDGE,"E12.15.9"),sQuery(id+"F0.wireOp",EDGE,"E12.16.0"),sQuery(id+"F0.wireOp",EDGE,"E12.16.1"),sQuery(id+"F0.wireOp",EDGE,"E12.16.2"),sQuery(id+"F0.wireOp",EDGE,"E12.16.3"),sQuery(id+"F0.wireOp",EDGE,"E12.16.4"),sQuery(id+"F0.wireOp",EDGE,"E12.16.5"),sQuery(id+"F0.wireOp",EDGE,"E12.16.6"),sQuery(id+"F0.wireOp",EDGE,"E12.16.7"),sQuery(id+"F0.wireOp",EDGE,"E12.16.8"),sQuery(id+"F0.wireOp",EDGE,"E12.16.9"),sQuery(id+"F0.wireOp",EDGE,"E12.17.0"),sQuery(id+"F0.wireOp",EDGE,"E12.17.1"),sQuery(id+"F0.wireOp",EDGE,"E12.17.2"),sQuery(id+"F0.wireOp",EDGE,"E12.17.3"),sQuery(id+"F0.wireOp",EDGE,"E12.17.4"),sQuery(id+"F0.wireOp",EDGE,"E12.17.5"),sQuery(id+"F0.wireOp",EDGE,"E12.17.6"),sQuery(id+"F0.wireOp",EDGE,"E12.17.7"),sQuery(id+"F0.wireOp",EDGE,"E12.17.8"),sQuery(id+"F0.wireOp",EDGE,"E12.17.9"),sQuery(id+"F0.wireOp",EDGE,"E12.18.0"),sQuery(id+"F0.wireOp",EDGE,"E12.18.1"),sQuery(id+"F0.wireOp",EDGE,"E12.18.2"),sQuery(id+"F0.wireOp",EDGE,"E12.18.3"),sQuery(id+"F0.wireOp",EDGE,"E12.18.4"),sQuery(id+"F0.wireOp",EDGE,"E12.18.5"),sQuery(id+"F0.wireOp",EDGE,"E12.18.6"),sQuery(id+"F0.wireOp",EDGE,"E12.18.7"),sQuery(id+"F0.wireOp",EDGE,"E12.18.8"),sQuery(id+"F0.wireOp",EDGE,"E12.18.9"),sQuery(id+"F0.wireOp",EDGE,"E12.19.0"),sQuery(id+"F0.wireOp",EDGE,"E12.19.1"),sQuery(id+"F0.wireOp",EDGE,"E12.19.2"),sQuery(id+"F0.wireOp",EDGE,"E12.19.3"),sQuery(id+"F0.wireOp",EDGE,"E12.19.4"),sQuery(id+"F0.wireOp",EDGE,"E12.19.5"),sQuery(id+"F0.wireOp",EDGE,"E12.19.6"),sQuery(id+"F0.wireOp",EDGE,"E12.19.7"),sQuery(id+"F0.wireOp",EDGE,"E12.19.8"),sQuery(id+"F0.wireOp",EDGE,"E12.19.9"),sQuery(id+"F0.wireOp",EDGE,"E12.20.0"),sQuery(id+"F0.wireOp",EDGE,"E12.20.1"),sQuery(id+"F0.wireOp",EDGE,"E12.20.2"),sQuery(id+"F0.wireOp",EDGE,"E12.20.3"),sQuery(id+"F0.wireOp",EDGE,"E12.20.4"),sQuery(id+"F0.wireOp",EDGE,"E12.20.5"),sQuery(id+"F0.wireOp",EDGE,"E12.20.6"),sQuery(id+"F0.wireOp",EDGE,"E12.20.7"),sQuery(id+"F0.wireOp",EDGE,"E12.20.8"),sQuery(id+"F0.wireOp",EDGE,"E12.20.9"),sQuery(id+"F0.wireOp",EDGE,"E12.21.0"),sQuery(id+"F0.wireOp",EDGE,"E12.21.1"),sQuery(id+"F0.wireOp",EDGE,"E12.21.2"),sQuery(id+"F0.wireOp",EDGE,"E12.21.3"),sQuery(id+"F0.wireOp",EDGE,"E12.21.4"),sQuery(id+"F0.wireOp",EDGE,"E12.21.5"),sQuery(id+"F0.wireOp",EDGE,"E12.21.6"),sQuery(id+"F0.wireOp",EDGE,"E12.21.7"),sQuery(id+"F0.wireOp",EDGE,"E12.21.8"),sQuery(id+"F0.wireOp",EDGE,"E12.21.9"),sQuery(id+"F0.wireOp",EDGE,"E12.22.0"),sQuery(id+"F0.wireOp",EDGE,"E12.22.1"),sQuery(id+"F0.wireOp",EDGE,"E12.22.2"),sQuery(id+"F0.wireOp",EDGE,"E12.22.3"),sQuery(id+"F0.wireOp",EDGE,"E12.22.4"),sQuery(id+"F0.wireOp",EDGE,"E12.22.5"),sQuery(id+"F0.wireOp",EDGE,"E12.22.6"),sQuery(id+"F0.wireOp",EDGE,"E12.22.7"),sQuery(id+"F0.wireOp",EDGE,"E12.22.8"),sQuery(id+"F0.wireOp",EDGE,"E12.22.9"),sQuery(id+"F0.wireOp",EDGE,"E12.23.0"),sQuery(id+"F0.wireOp",EDGE,"E12.23.1"),sQuery(id+"F0.wireOp",EDGE,"E12.23.2"),sQuery(id+"F0.wireOp",EDGE,"E12.23.3"),sQuery(id+"F0.wireOp",EDGE,"E12.23.4"),sQuery(id+"F0.wireOp",EDGE,"E12.23.5"),sQuery(id+"F0.wireOp",EDGE,"E12.23.6"),sQuery(id+"F0.wireOp",EDGE,"E12.23.7"),sQuery(id+"F0.wireOp",EDGE,"E12.23.8"),sQuery(id+"F0.wireOp",EDGE,"E12.23.9"),sQuery(id+"F0.wireOp",EDGE,"E12.24.0"),sQuery(id+"F0.wireOp",EDGE,"E12.24.1"),sQuery(id+"F0.wireOp",EDGE,"E12.24.2"),sQuery(id+"F0.wireOp",EDGE,"E12.24.3"),sQuery(id+"F0.wireOp",EDGE,"E12.24.4"),sQuery(id+"F0.wireOp",EDGE,"E12.24.5"),sQuery(id+"F0.wireOp",EDGE,"E12.24.6"),sQuery(id+"F0.wireOp",EDGE,"E12.24.7"),sQuery(id+"F0.wireOp",EDGE,"E12.24.8"),sQuery(id+"F0.wireOp",EDGE,"E12.24.9"),sQuery(id+"F0.wireOp",EDGE,"E12.25.0"),sQuery(id+"F0.wireOp",EDGE,"E12.25.1"),sQuery(id+"F0.wireOp",EDGE,"E12.25.2"),sQuery(id+"F0.wireOp",EDGE,"E12.25.3"),sQuery(id+"F0.wireOp",EDGE,"E12.25.4"),sQuery(id+"F0.wireOp",EDGE,"E12.25.5"),sQuery(id+"F0.wireOp",EDGE,"E12.25.6"),sQuery(id+"F0.wireOp",EDGE,"E12.25.7"),sQuery(id+"F0.wireOp",EDGE,"E12.25.8"),sQuery(id+"F0.wireOp",EDGE,"E12.25.9"),sQuery(id+"F0.wireOp",EDGE,"E12.26.0"),sQuery(id+"F0.wireOp",EDGE,"E12.26.1"),sQuery(id+"F0.wireOp",EDGE,"E12.26.2"),sQuery(id+"F0.wireOp",EDGE,"E12.26.3"),sQuery(id+"F0.wireOp",EDGE,"E12.26.4"),sQuery(id+"F0.wireOp",EDGE,"E12.26.5"),sQuery(id+"F0.wireOp",EDGE,"E12.26.6"),sQuery(id+"F0.wireOp",EDGE,"E12.26.7"),sQuery(id+"F0.wireOp",EDGE,"E12.26.8"),sQuery(id+"F0.wireOp",EDGE,"E12.26.9"),sQuery(id+"F0.wireOp",EDGE,"E12.27.0"),sQuery(id+"F0.wireOp",EDGE,"E12.27.1"),sQuery(id+"F0.wireOp",EDGE,"E12.27.2"),sQuery(id+"F0.wireOp",EDGE,"E12.27.3"),sQuery(id+"F0.wireOp",EDGE,"E12.27.4"),sQuery(id+"F0.wireOp",EDGE,"E12.27.5"),sQuery(id+"F0.wireOp",EDGE,"E12.27.6"),sQuery(id+"F0.wireOp",EDGE,"E12.27.7"),sQuery(id+"F0.wireOp",EDGE,"E12.27.8"),sQuery(id+"F0.wireOp",EDGE,"E12.27.9"),sQuery(id+"F0.wireOp",EDGE,"E12.28.0"),sQuery(id+"F0.wireOp",EDGE,"E12.28.1"),sQuery(id+"F0.wireOp",EDGE,"E12.28.2"),sQuery(id+"F0.wireOp",EDGE,"E12.28.3"),sQuery(id+"F0.wireOp",EDGE,"E12.28.4"),sQuery(id+"F0.wireOp",EDGE,"E12.28.5"),sQuery(id+"F0.wireOp",EDGE,"E12.28.6"),sQuery(id+"F0.wireOp",EDGE,"E12.28.7"),sQuery(id+"F0.wireOp",EDGE,"E12.28.8"),sQuery(id+"F0.wireOp",EDGE,"E12.28.9"),sQuery(id+"F0.wireOp",EDGE,"E12.29.0"),sQuery(id+"F0.wireOp",EDGE,"E12.29.1"),sQuery(id+"F0.wireOp",EDGE,"E12.29.2"),sQuery(id+"F0.wireOp",EDGE,"E12.29.3"),sQuery(id+"F0.wireOp",EDGE,"E12.29.4"),sQuery(id+"F0.wireOp",EDGE,"E12.29.5"),sQuery(id+"F0.wireOp",EDGE,"E12.29.6"),sQuery(id+"F0.wireOp",EDGE,"E12.29.7"),sQuery(id+"F0.wireOp",EDGE,"E12.29.8"),sQuery(id+"F0.wireOp",EDGE,"E12.29.9"),sQuery(id+"F0.wireOp",EDGE,"E12.30.0"),sQuery(id+"F0.wireOp",EDGE,"E12.30.1"),sQuery(id+"F0.wireOp",EDGE,"E12.30.2"),sQuery(id+"F0.wireOp",EDGE,"E12.30.3"),sQuery(id+"F0.wireOp",EDGE,"E12.30.4"),sQuery(id+"F0.wireOp",EDGE,"E12.30.5"),sQuery(id+"F0.wireOp",EDGE,"E12.30.6"),sQuery(id+"F0.wireOp",EDGE,"E12.30.7"),sQuery(id+"F0.wireOp",EDGE,"E12.30.8"),sQuery(id+"F0.wireOp",EDGE,"E12.30.9"),sQuery(id+"F0.wireOp",EDGE,"E12.31.0"),sQuery(id+"F0.wireOp",EDGE,"E12.31.1"),sQuery(id+"F0.wireOp",EDGE,"E12.31.2"),sQuery(id+"F0.wireOp",EDGE,"E12.31.3"),sQuery(id+"F0.wireOp",EDGE,"E12.31.4"),sQuery(id+"F0.wireOp",EDGE,"E12.31.5"),sQuery(id+"F0.wireOp",EDGE,"E12.31.6"),sQuery(id+"F0.wireOp",EDGE,"E12.31.7"),sQuery(id+"F0.wireOp",EDGE,"E12.31.8"),sQuery(id+"F0.wireOp",EDGE,"E12.31.9"),sQuery(id+"F0.wireOp",EDGE,"E12.32.0"),sQuery(id+"F0.wireOp",EDGE,"E12.32.1"),sQuery(id+"F0.wireOp",EDGE,"E12.32.2"),sQuery(id+"F0.wireOp",EDGE,"E12.32.3"),sQuery(id+"F0.wireOp",EDGE,"E12.32.4"),sQuery(id+"F0.wireOp",EDGE,"E12.32.5"),sQuery(id+"F0.wireOp",EDGE,"E12.32.6"),sQuery(id+"F0.wireOp",EDGE,"E12.32.7"),sQuery(id+"F0.wireOp",EDGE,"E12.32.8"),sQuery(id+"F0.wireOp",EDGE,"E12.32.9"),sQuery(id+"F0.wireOp",EDGE,"E12.33.0"),sQuery(id+"F0.wireOp",EDGE,"E12.33.1"),sQuery(id+"F0.wireOp",EDGE,"E12.33.2"),sQuery(id+"F0.wireOp",EDGE,"E12.33.3"),sQuery(id+"F0.wireOp",EDGE,"E12.33.4"),sQuery(id+"F0.wireOp",EDGE,"E12.33.5"),sQuery(id+"F0.wireOp",EDGE,"E12.33.6"),sQuery(id+"F0.wireOp",EDGE,"E12.33.7"),sQuery(id+"F0.wireOp",EDGE,"E12.33.8"),sQuery(id+"F0.wireOp",EDGE,"E12.33.9"),sQuery(id+"F0.wireOp",EDGE,"E12.34.0"),sQuery(id+"F0.wireOp",EDGE,"E12.34.1"),sQuery(id+"F0.wireOp",EDGE,"E12.34.2"),sQuery(id+"F0.wireOp",EDGE,"E12.34.3"),sQuery(id+"F0.wireOp",EDGE,"E12.34.4"),sQuery(id+"F0.wireOp",EDGE,"E12.34.5"),sQuery(id+"F0.wireOp",EDGE,"E12.34.6"),sQuery(id+"F0.wireOp",EDGE,"E12.34.7"),sQuery(id+"F0.wireOp",EDGE,"E12.34.8"),sQuery(id+"F0.wireOp",EDGE,"E12.34.9"),sQuery(id+"F0.wireOp",EDGE,"E12.35.0"),sQuery(id+"F0.wireOp",EDGE,"E12.35.1"),sQuery(id+"F0.wireOp",EDGE,"E12.35.2"),sQuery(id+"F0.wireOp",EDGE,"E12.35.3"),sQuery(id+"F0.wireOp",EDGE,"E12.35.4"),sQuery(id+"F0.wireOp",EDGE,"E12.35.5"),sQuery(id+"F0.wireOp",EDGE,"E12.35.6"),sQuery(id+"F0.wireOp",EDGE,"E12.35.7"),sQuery(id+"F0.wireOp",EDGE,"E12.35.8"),sQuery(id+"F0.wireOp",EDGE,"E12.35.9"),sQuery(id+"F0.wireOp",EDGE,"E12.36.0"),sQuery(id+"F0.wireOp",EDGE,"E12.36.1"),sQuery(id+"F0.wireOp",EDGE,"E12.36.2"),sQuery(id+"F0.wireOp",EDGE,"E12.36.3"),sQuery(id+"F0.wireOp",EDGE,"E12.36.4"),sQuery(id+"F0.wireOp",EDGE,"E12.36.5"),sQuery(id+"F0.wireOp",EDGE,"E12.36.6"),sQuery(id+"F0.wireOp",EDGE,"E12.36.7"),sQuery(id+"F0.wireOp",EDGE,"E12.36.8"),sQuery(id+"F0.wireOp",EDGE,"E12.36.9"),sQuery(id+"F0.wireOp",EDGE,"E12.37.0"),sQuery(id+"F0.wireOp",EDGE,"E12.37.1"),sQuery(id+"F0.wireOp",EDGE,"E12.37.2"),sQuery(id+"F0.wireOp",EDGE,"E12.37.3"),sQuery(id+"F0.wireOp",EDGE,"E12.37.4"),sQuery(id+"F0.wireOp",EDGE,"E12.37.5"),sQuery(id+"F0.wireOp",EDGE,"E12.37.6"),sQuery(id+"F0.wireOp",EDGE,"E12.37.7"),sQuery(id+"F0.wireOp",EDGE,"E12.37.8"),sQuery(id+"F0.wireOp",EDGE,"E12.37.9"),sQuery(id+"F0.wireOp",EDGE,"E12.38.0"),sQuery(id+"F0.wireOp",EDGE,"E12.38.1"),sQuery(id+"F0.wireOp",EDGE,"E12.38.2"),sQuery(id+"F0.wireOp",EDGE,"E12.38.3"),sQuery(id+"F0.wireOp",EDGE,"E12.38.4"),sQuery(id+"F0.wireOp",EDGE,"E12.38.5"),sQuery(id+"F0.wireOp",EDGE,"E12.38.6"),sQuery(id+"F0.wireOp",EDGE,"E12.38.7"),sQuery(id+"F0.wireOp",EDGE,"E12.38.8"),sQuery(id+"F0.wireOp",EDGE,"E12.38.9"),sQuery(id+"F0.wireOp",EDGE,"E12.39.0"),sQuery(id+"F0.wireOp",EDGE,"E12.39.1"),sQuery(id+"F0.wireOp",EDGE,"E12.39.2"),sQuery(id+"F0.wireOp",EDGE,"E12.39.3"),sQuery(id+"F0.wireOp",EDGE,"E12.39.4"),sQuery(id+"F0.wireOp",EDGE,"E12.39.5"),sQuery(id+"F0.wireOp",EDGE,"E12.39.6"),sQuery(id+"F0.wireOp",EDGE,"E12.39.7"),sQuery(id+"F0.wireOp",EDGE,"E12.39.8"),sQuery(id+"F0.wireOp",EDGE,"E12.39.9"),sQuery(id+"F0.wireOp",EDGE,"E12.40.0"),sQuery(id+"F0.wireOp",EDGE,"E12.40.1"),sQuery(id+"F0.wireOp",EDGE,"E12.40.2"),sQuery(id+"F0.wireOp",EDGE,"E12.40.3"),sQuery(id+"F0.wireOp",EDGE,"E12.40.4"),sQuery(id+"F0.wireOp",EDGE,"E12.40.5"),sQuery(id+"F0.wireOp",EDGE,"E12.40.6"),sQuery(id+"F0.wireOp",EDGE,"E12.40.7"),sQuery(id+"F0.wireOp",EDGE,"E12.40.8"),sQuery(id+"F0.wireOp",EDGE,"E12.40.9"),sQuery(id+"F0.wireOp",EDGE,"E12.41.0"),sQuery(id+"F0.wireOp",EDGE,"E12.41.1"),sQuery(id+"F0.wireOp",EDGE,"E12.41.2"),sQuery(id+"F0.wireOp",EDGE,"E12.41.3"),sQuery(id+"F0.wireOp",EDGE,"E12.41.4"),sQuery(id+"F0.wireOp",EDGE,"E12.41.5"),sQuery(id+"F0.wireOp",EDGE,"E12.41.6"),sQuery(id+"F0.wireOp",EDGE,"E12.41.7"),sQuery(id+"F0.wireOp",EDGE,"E12.41.8"),sQuery(id+"F0.wireOp",EDGE,"E12.41.9"),sQuery(id+"F0.wireOp",EDGE,"E12.42.0"),sQuery(id+"F0.wireOp",EDGE,"E12.42.1"),sQuery(id+"F0.wireOp",EDGE,"E12.42.2"),sQuery(id+"F0.wireOp",EDGE,"E12.42.3"),sQuery(id+"F0.wireOp",EDGE,"E12.42.4"),sQuery(id+"F0.wireOp",EDGE,"E12.42.5"),sQuery(id+"F0.wireOp",EDGE,"E12.42.6"),sQuery(id+"F0.wireOp",EDGE,"E12.42.7"),sQuery(id+"F0.wireOp",EDGE,"E12.42.8"),sQuery(id+"F0.wireOp",EDGE,"E12.42.9"),sQuery(id+"F0.wireOp",EDGE,"E12.43.0"),sQuery(id+"F0.wireOp",EDGE,"E12.43.1"),sQuery(id+"F0.wireOp",EDGE,"E12.43.2"),sQuery(id+"F0.wireOp",EDGE,"E12.43.3"),sQuery(id+"F0.wireOp",EDGE,"E12.43.4"),sQuery(id+"F0.wireOp",EDGE,"E12.43.5"),sQuery(id+"F0.wireOp",EDGE,"E12.43.6"),sQuery(id+"F0.wireOp",EDGE,"E12.43.7"),sQuery(id+"F0.wireOp",EDGE,"E12.43.8"),sQuery(id+"F0.wireOp",EDGE,"E12.43.9"),sQuery(id+"F0.wireOp",EDGE,"E12.44.0"),sQuery(id+"F0.wireOp",EDGE,"E12.44.1"),sQuery(id+"F0.wireOp",EDGE,"E12.44.2"),sQuery(id+"F0.wireOp",EDGE,"E12.44.3"),sQuery(id+"F0.wireOp",EDGE,"E12.44.4"),sQuery(id+"F0.wireOp",EDGE,"E12.44.5"),sQuery(id+"F0.wireOp",EDGE,"E12.44.6"),sQuery(id+"F0.wireOp",EDGE,"E12.44.7"),sQuery(id+"F0.wireOp",EDGE,"E12.44.8"),sQuery(id+"F0.wireOp",EDGE,"E12.44.9"),sQuery(id+"F0.wireOp",EDGE,"E12.45.0"),sQuery(id+"F0.wireOp",EDGE,"E12.45.1"),sQuery(id+"F0.wireOp",EDGE,"E12.45.2"),sQuery(id+"F0.wireOp",EDGE,"E12.45.3"),sQuery(id+"F0.wireOp",EDGE,"E12.45.4"),sQuery(id+"F0.wireOp",EDGE,"E12.45.5"),sQuery(id+"F0.wireOp",EDGE,"E12.45.6"),sQuery(id+"F0.wireOp",EDGE,"E12.45.7"),sQuery(id+"F0.wireOp",EDGE,"E12.45.8"),sQuery(id+"F0.wireOp",EDGE,"E12.45.9"),sQuery(id+"F0.wireOp",EDGE,"E12.46.0"),sQuery(id+"F0.wireOp",EDGE,"E12.46.1"),sQuery(id+"F0.wireOp",EDGE,"E12.46.2"),sQuery(id+"F0.wireOp",EDGE,"E12.46.3"),sQuery(id+"F0.wireOp",EDGE,"E12.46.4"),sQuery(id+"F0.wireOp",EDGE,"E12.46.5"),sQuery(id+"F0.wireOp",EDGE,"E12.46.6"),sQuery(id+"F0.wireOp",EDGE,"E12.46.7"),sQuery(id+"F0.wireOp",EDGE,"E12.46.8"),sQuery(id+"F0.wireOp",EDGE,"E12.46.9"),sQuery(id+"F0.wireOp",EDGE,"E12.47.0"),sQuery(id+"F0.wireOp",EDGE,"E12.47.1"),sQuery(id+"F0.wireOp",EDGE,"E12.47.2"),sQuery(id+"F0.wireOp",EDGE,"E12.47.3"),sQuery(id+"F0.wireOp",EDGE,"E12.47.4"),sQuery(id+"F0.wireOp",EDGE,"E12.47.5"),sQuery(id+"F0.wireOp",EDGE,"E12.47.6"),sQuery(id+"F0.wireOp",EDGE,"E12.47.7"),sQuery(id+"F0.wireOp",EDGE,"E12.47.8"),sQuery(id+"F0.wireOp",EDGE,"E12.47.9"),sQuery(id+"F0.wireOp",EDGE,"E12.48.0"),sQuery(id+"F0.wireOp",EDGE,"E12.48.1"),sQuery(id+"F0.wireOp",EDGE,"E12.48.2"),sQuery(id+"F0.wireOp",EDGE,"E12.48.3"),sQuery(id+"F0.wireOp",EDGE,"E12.48.4"),sQuery(id+"F0.wireOp",EDGE,"E12.48.5"),sQuery(id+"F0.wireOp",EDGE,"E12.48.6"),sQuery(id+"F0.wireOp",EDGE,"E12.48.7"),sQuery(id+"F0.wireOp",EDGE,"E12.48.8"),sQuery(id+"F0.wireOp",EDGE,"E12.48.9"),sQuery(id+"F0.wireOp",EDGE,"E12.49.0"),sQuery(id+"F0.wireOp",EDGE,"E12.49.1"),sQuery(id+"F0.wireOp",EDGE,"E12.49.2"),sQuery(id+"F0.wireOp",EDGE,"E12.49.3"),sQuery(id+"F0.wireOp",EDGE,"E12.49.4"),sQuery(id+"F0.wireOp",EDGE,"E12.49.5"),sQuery(id+"F0.wireOp",EDGE,"E12.49.6"),sQuery(id+"F0.wireOp",EDGE,"E12.49.7"),sQuery(id+"F0.wireOp",EDGE,"E12.49.8"),sQuery(id+"F0.wireOp",EDGE,"E12.49.9"),sQuery(id+"F0.wireOp",EDGE,"E12.50.0"),sQuery(id+"F0.wireOp",EDGE,"E12.50.1"),sQuery(id+"F0.wireOp",EDGE,"E12.50.2"),sQuery(id+"F0.wireOp",EDGE,"E12.50.3"),sQuery(id+"F0.wireOp",EDGE,"E12.50.4"),sQuery(id+"F0.wireOp",EDGE,"E12.50.5"),sQuery(id+"F0.wireOp",EDGE,"E12.50.6"),sQuery(id+"F0.wireOp",EDGE,"E12.50.7"),sQuery(id+"F0.wireOp",EDGE,"E12.50.8"),sQuery(id+"F0.wireOp",EDGE,"E12.50.9"),sQuery(id+"F0.wireOp",EDGE,"E12.51.0"),sQuery(id+"F0.wireOp",EDGE,"E12.51.1"),sQuery(id+"F0.wireOp",EDGE,"E12.51.2"),sQuery(id+"F0.wireOp",EDGE,"E12.51.3"),sQuery(id+"F0.wireOp",EDGE,"E12.51.4"),sQuery(id+"F0.wireOp",EDGE,"E12.51.5"),sQuery(id+"F0.wireOp",EDGE,"E12.51.6"),sQuery(id+"F0.wireOp",EDGE,"E12.51.7"),sQuery(id+"F0.wireOp",EDGE,"E12.51.8"),sQuery(id+"F0.wireOp",EDGE,"E12.51.9"),sQuery(id+"F0.wireOp",EDGE,"E12.52.0"),sQuery(id+"F0.wireOp",EDGE,"E12.52.1"),sQuery(id+"F0.wireOp",EDGE,"E12.52.2"),sQuery(id+"F0.wireOp",EDGE,"E12.52.3"),sQuery(id+"F0.wireOp",EDGE,"E12.52.4"),sQuery(id+"F0.wireOp",EDGE,"E12.52.5"),sQuery(id+"F0.wireOp",EDGE,"E12.52.6"),sQuery(id+"F0.wireOp",EDGE,"E12.52.7"),sQuery(id+"F0.wireOp",EDGE,"E12.52.8"),sQuery(id+"F0.wireOp",EDGE,"E12.52.9"),sQuery(id+"F0.wireOp",EDGE,"E12.53.0"),sQuery(id+"F0.wireOp",EDGE,"E12.53.1"),sQuery(id+"F0.wireOp",EDGE,"E12.53.2"),sQuery(id+"F0.wireOp",EDGE,"E12.53.3"),sQuery(id+"F0.wireOp",EDGE,"E12.53.4"),sQuery(id+"F0.wireOp",EDGE,"E12.53.5"),sQuery(id+"F0.wireOp",EDGE,"E12.53.6"),sQuery(id+"F0.wireOp",EDGE,"E12.53.7"),sQuery(id+"F0.wireOp",EDGE,"E12.53.8"),sQuery(id+"F0.wireOp",EDGE,"E12.53.9"),sQuery(id+"F0.wireOp",EDGE,"E12.54.0"),sQuery(id+"F0.wireOp",EDGE,"E12.54.1"),sQuery(id+"F0.wireOp",EDGE,"E12.54.2"),sQuery(id+"F0.wireOp",EDGE,"E12.54.3"),sQuery(id+"F0.wireOp",EDGE,"E12.54.4"),sQuery(id+"F0.wireOp",EDGE,"E12.54.5"),sQuery(id+"F0.wireOp",EDGE,"E12.54.6"),sQuery(id+"F0.wireOp",EDGE,"E12.54.7"),sQuery(id+"F0.wireOp",EDGE,"E12.54.8"),sQuery(id+"F0.wireOp",EDGE,"E12.54.9"),sQuery(id+"F0.wireOp",EDGE,"E12.55.0"),sQuery(id+"F0.wireOp",EDGE,"E12.55.1"),sQuery(id+"F0.wireOp",EDGE,"E12.55.2"),sQuery(id+"F0.wireOp",EDGE,"E12.55.3"),sQuery(id+"F0.wireOp",EDGE,"E12.55.4"),sQuery(id+"F0.wireOp",EDGE,"E12.55.5"),sQuery(id+"F0.wireOp",EDGE,"E12.55.6"),sQuery(id+"F0.wireOp",EDGE,"E12.55.7"),sQuery(id+"F0.wireOp",EDGE,"E12.55.8"),sQuery(id+"F0.wireOp",EDGE,"E12.55.9"),sQuery(id+"F0.wireOp",EDGE,"E12.56.0"),sQuery(id+"F0.wireOp",EDGE,"E12.56.1"),sQuery(id+"F0.wireOp",EDGE,"E12.56.2"),sQuery(id+"F0.wireOp",EDGE,"E12.56.3"),sQuery(id+"F0.wireOp",EDGE,"E12.56.4"),sQuery(id+"F0.wireOp",EDGE,"E12.56.5"),sQuery(id+"F0.wireOp",EDGE,"E12.56.6"),sQuery(id+"F0.wireOp",EDGE,"E12.56.7"),sQuery(id+"F0.wireOp",EDGE,"E12.56.8"),sQuery(id+"F0.wireOp",EDGE,"E12.56.9"),sQuery(id+"F0.wireOp",EDGE,"E12.57.0"),sQuery(id+"F0.wireOp",EDGE,"E12.57.1"),sQuery(id+"F0.wireOp",EDGE,"E12.57.2"),sQuery(id+"F0.wireOp",EDGE,"E12.57.3"),sQuery(id+"F0.wireOp",EDGE,"E12.57.4"),sQuery(id+"F0.wireOp",EDGE,"E12.57.5"),sQuery(id+"F0.wireOp",EDGE,"E12.57.6"),sQuery(id+"F0.wireOp",EDGE,"E12.57.7"),sQuery(id+"F0.wireOp",EDGE,"E12.57.8"),sQuery(id+"F0.wireOp",EDGE,"E12.57.9"),sQuery(id+"F0.wireOp",EDGE,"E12.58.0"),sQuery(id+"F0.wireOp",EDGE,"E12.58.1"),sQuery(id+"F0.wireOp",EDGE,"E12.58.2"),sQuery(id+"F0.wireOp",EDGE,"E12.58.3"),sQuery(id+"F0.wireOp",EDGE,"E12.58.4"),sQuery(id+"F0.wireOp",EDGE,"E12.58.5"),sQuery(id+"F0.wireOp",EDGE,"E12.58.6"),sQuery(id+"F0.wireOp",EDGE,"E12.58.7"),sQuery(id+"F0.wireOp",EDGE,"E12.58.8"),sQuery(id+"F0.wireOp",EDGE,"E12.58.9"),sQuery(id+"F0.wireOp",EDGE,"E12.59.0"),sQuery(id+"F0.wireOp",EDGE,"E12.59.1"),sQuery(id+"F0.wireOp",EDGE,"E12.59.2"),sQuery(id+"F0.wireOp",EDGE,"E12.59.3"),sQuery(id+"F0.wireOp",EDGE,"E12.59.4"),sQuery(id+"F0.wireOp",EDGE,"E12.59.5"),sQuery(id+"F0.wireOp",EDGE,"E12.59.6"),sQuery(id+"F0.wireOp",EDGE,"E12.59.7"),sQuery(id+"F0.wireOp",EDGE,"E12.59.8"),sQuery(id+"F0.wireOp",EDGE,"E12.59.9"),sQuery(id+"F0.wireOp",EDGE,"E13.trimOffspring"),sQuery(id+"F0.wireOp",EDGE,"E14.trimOffspring")])],"isStart":true}),makeQuery(id+"F3.opExtrude","SWEPT_FACE",FACE,{"disambiguationData":[OSD([sQuery(id+"F2.wireOp",EDGE,"E15")])]})]});
            var Q11;
            Q11=makeQuery(id+"F3.boolean.opBoolean","INTERSECT",EDGE,{"derivedFrom":[makeQuery(id+"F1.opExtrude","CAP_FACE",FACE,{"disambiguationData":[OSD([sQuery(id+"F0.wireOp",EDGE,"E0"),sQuery(id+"F0.wireOp",EDGE,"E2"),sQuery(id+"F0.wireOp",EDGE,"E3"),sQuery(id+"F0.wireOp",EDGE,"E4.trimOffspring"),sQuery(id+"F0.wireOp",EDGE,"E5.MirrorCS"),sQuery(id+"F0.wireOp",EDGE,"E6.MirrorCS"),sQuery(id+"F0.wireOp",EDGE,"E7.MirrorCS"),sQuery(id+"F0.wireOp",EDGE,"E8.filletArc"),sQuery(id+"F0.wireOp",EDGE,"E9.filletArc"),sQuery(id+"F0.wireOp",EDGE,"E10.filletArc"),sQuery(id+"F0.wireOp",EDGE,"E11.filletArc"),sQuery(id+"F0.wireOp",EDGE,"E12.1.0"),sQuery(id+"F0.wireOp",EDGE,"E12.1.1"),sQuery(id+"F0.wireOp",EDGE,"E12.1.2"),sQuery(id+"F0.wireOp",EDGE,"E12.1.3"),sQuery(id+"F0.wireOp",EDGE,"E12.1.4"),sQuery(id+"F0.wireOp",EDGE,"E12.1.5"),sQuery(id+"F0.wireOp",EDGE,"E12.1.6"),sQuery(id+"F0.wireOp",EDGE,"E12.1.7"),sQuery(id+"F0.wireOp",EDGE,"E12.1.8"),sQuery(id+"F0.wireOp",EDGE,"E12.1.9"),sQuery(id+"F0.wireOp",EDGE,"E12.2.0"),sQuery(id+"F0.wireOp",EDGE,"E12.2.1"),sQuery(id+"F0.wireOp",EDGE,"E12.2.2"),sQuery(id+"F0.wireOp",EDGE,"E12.2.3"),sQuery(id+"F0.wireOp",EDGE,"E12.2.4"),sQuery(id+"F0.wireOp",EDGE,"E12.2.5"),sQuery(id+"F0.wireOp",EDGE,"E12.2.6"),sQuery(id+"F0.wireOp",EDGE,"E12.2.7"),sQuery(id+"F0.wireOp",EDGE,"E12.2.8"),sQuery(id+"F0.wireOp",EDGE,"E12.2.9"),sQuery(id+"F0.wireOp",EDGE,"E12.3.0"),sQuery(id+"F0.wireOp",EDGE,"E12.3.1"),sQuery(id+"F0.wireOp",EDGE,"E12.3.2"),sQuery(id+"F0.wireOp",EDGE,"E12.3.3"),sQuery(id+"F0.wireOp",EDGE,"E12.3.4"),sQuery(id+"F0.wireOp",EDGE,"E12.3.5"),sQuery(id+"F0.wireOp",EDGE,"E12.3.6"),sQuery(id+"F0.wireOp",EDGE,"E12.3.7"),sQuery(id+"F0.wireOp",EDGE,"E12.3.8"),sQuery(id+"F0.wireOp",EDGE,"E12.3.9"),sQuery(id+"F0.wireOp",EDGE,"E12.4.0"),sQuery(id+"F0.wireOp",EDGE,"E12.4.1"),sQuery(id+"F0.wireOp",EDGE,"E12.4.2"),sQuery(id+"F0.wireOp",EDGE,"E12.4.3"),sQuery(id+"F0.wireOp",EDGE,"E12.4.4"),sQuery(id+"F0.wireOp",EDGE,"E12.4.5"),sQuery(id+"F0.wireOp",EDGE,"E12.4.6"),sQuery(id+"F0.wireOp",EDGE,"E12.4.7"),sQuery(id+"F0.wireOp",EDGE,"E12.4.8"),sQuery(id+"F0.wireOp",EDGE,"E12.4.9"),sQuery(id+"F0.wireOp",EDGE,"E12.5.0"),sQuery(id+"F0.wireOp",EDGE,"E12.5.1"),sQuery(id+"F0.wireOp",EDGE,"E12.5.2"),sQuery(id+"F0.wireOp",EDGE,"E12.5.3"),sQuery(id+"F0.wireOp",EDGE,"E12.5.4"),sQuery(id+"F0.wireOp",EDGE,"E12.5.5"),sQuery(id+"F0.wireOp",EDGE,"E12.5.6"),sQuery(id+"F0.wireOp",EDGE,"E12.5.7"),sQuery(id+"F0.wireOp",EDGE,"E12.5.8"),sQuery(id+"F0.wireOp",EDGE,"E12.5.9"),sQuery(id+"F0.wireOp",EDGE,"E12.6.0"),sQuery(id+"F0.wireOp",EDGE,"E12.6.1"),sQuery(id+"F0.wireOp",EDGE,"E12.6.2"),sQuery(id+"F0.wireOp",EDGE,"E12.6.3"),sQuery(id+"F0.wireOp",EDGE,"E12.6.4"),sQuery(id+"F0.wireOp",EDGE,"E12.6.5"),sQuery(id+"F0.wireOp",EDGE,"E12.6.6"),sQuery(id+"F0.wireOp",EDGE,"E12.6.7"),sQuery(id+"F0.wireOp",EDGE,"E12.6.8"),sQuery(id+"F0.wireOp",EDGE,"E12.6.9"),sQuery(id+"F0.wireOp",EDGE,"E12.7.0"),sQuery(id+"F0.wireOp",EDGE,"E12.7.1"),sQuery(id+"F0.wireOp",EDGE,"E12.7.2"),sQuery(id+"F0.wireOp",EDGE,"E12.7.3"),sQuery(id+"F0.wireOp",EDGE,"E12.7.4"),sQuery(id+"F0.wireOp",EDGE,"E12.7.5"),sQuery(id+"F0.wireOp",EDGE,"E12.7.6"),sQuery(id+"F0.wireOp",EDGE,"E12.7.7"),sQuery(id+"F0.wireOp",EDGE,"E12.7.8"),sQuery(id+"F0.wireOp",EDGE,"E12.7.9"),sQuery(id+"F0.wireOp",EDGE,"E12.8.0"),sQuery(id+"F0.wireOp",EDGE,"E12.8.1"),sQuery(id+"F0.wireOp",EDGE,"E12.8.2"),sQuery(id+"F0.wireOp",EDGE,"E12.8.3"),sQuery(id+"F0.wireOp",EDGE,"E12.8.4"),sQuery(id+"F0.wireOp",EDGE,"E12.8.5"),sQuery(id+"F0.wireOp",EDGE,"E12.8.6"),sQuery(id+"F0.wireOp",EDGE,"E12.8.7"),sQuery(id+"F0.wireOp",EDGE,"E12.8.8"),sQuery(id+"F0.wireOp",EDGE,"E12.8.9"),sQuery(id+"F0.wireOp",EDGE,"E12.9.0"),sQuery(id+"F0.wireOp",EDGE,"E12.9.1"),sQuery(id+"F0.wireOp",EDGE,"E12.9.2"),sQuery(id+"F0.wireOp",EDGE,"E12.9.3"),sQuery(id+"F0.wireOp",EDGE,"E12.9.4"),sQuery(id+"F0.wireOp",EDGE,"E12.9.5"),sQuery(id+"F0.wireOp",EDGE,"E12.9.6"),sQuery(id+"F0.wireOp",EDGE,"E12.9.7"),sQuery(id+"F0.wireOp",EDGE,"E12.9.8"),sQuery(id+"F0.wireOp",EDGE,"E12.9.9"),sQuery(id+"F0.wireOp",EDGE,"E12.10.0"),sQuery(id+"F0.wireOp",EDGE,"E12.10.1"),sQuery(id+"F0.wireOp",EDGE,"E12.10.2"),sQuery(id+"F0.wireOp",EDGE,"E12.10.3"),sQuery(id+"F0.wireOp",EDGE,"E12.10.4"),sQuery(id+"F0.wireOp",EDGE,"E12.10.5"),sQuery(id+"F0.wireOp",EDGE,"E12.10.6"),sQuery(id+"F0.wireOp",EDGE,"E12.10.7"),sQuery(id+"F0.wireOp",EDGE,"E12.10.8"),sQuery(id+"F0.wireOp",EDGE,"E12.10.9"),sQuery(id+"F0.wireOp",EDGE,"E12.11.0"),sQuery(id+"F0.wireOp",EDGE,"E12.11.1"),sQuery(id+"F0.wireOp",EDGE,"E12.11.2"),sQuery(id+"F0.wireOp",EDGE,"E12.11.3"),sQuery(id+"F0.wireOp",EDGE,"E12.11.4"),sQuery(id+"F0.wireOp",EDGE,"E12.11.5"),sQuery(id+"F0.wireOp",EDGE,"E12.11.6"),sQuery(id+"F0.wireOp",EDGE,"E12.11.7"),sQuery(id+"F0.wireOp",EDGE,"E12.11.8"),sQuery(id+"F0.wireOp",EDGE,"E12.11.9"),sQuery(id+"F0.wireOp",EDGE,"E12.12.0"),sQuery(id+"F0.wireOp",EDGE,"E12.12.1"),sQuery(id+"F0.wireOp",EDGE,"E12.12.2"),sQuery(id+"F0.wireOp",EDGE,"E12.12.3"),sQuery(id+"F0.wireOp",EDGE,"E12.12.4"),sQuery(id+"F0.wireOp",EDGE,"E12.12.5"),sQuery(id+"F0.wireOp",EDGE,"E12.12.6"),sQuery(id+"F0.wireOp",EDGE,"E12.12.7"),sQuery(id+"F0.wireOp",EDGE,"E12.12.8"),sQuery(id+"F0.wireOp",EDGE,"E12.12.9"),sQuery(id+"F0.wireOp",EDGE,"E12.13.0"),sQuery(id+"F0.wireOp",EDGE,"E12.13.1"),sQuery(id+"F0.wireOp",EDGE,"E12.13.2"),sQuery(id+"F0.wireOp",EDGE,"E12.13.3"),sQuery(id+"F0.wireOp",EDGE,"E12.13.4"),sQuery(id+"F0.wireOp",EDGE,"E12.13.5"),sQuery(id+"F0.wireOp",EDGE,"E12.13.6"),sQuery(id+"F0.wireOp",EDGE,"E12.13.7"),sQuery(id+"F0.wireOp",EDGE,"E12.13.8"),sQuery(id+"F0.wireOp",EDGE,"E12.13.9"),sQuery(id+"F0.wireOp",EDGE,"E12.14.0"),sQuery(id+"F0.wireOp",EDGE,"E12.14.1"),sQuery(id+"F0.wireOp",EDGE,"E12.14.2"),sQuery(id+"F0.wireOp",EDGE,"E12.14.3"),sQuery(id+"F0.wireOp",EDGE,"E12.14.4"),sQuery(id+"F0.wireOp",EDGE,"E12.14.5"),sQuery(id+"F0.wireOp",EDGE,"E12.14.6"),sQuery(id+"F0.wireOp",EDGE,"E12.14.7"),sQuery(id+"F0.wireOp",EDGE,"E12.14.8"),sQuery(id+"F0.wireOp",EDGE,"E12.14.9"),sQuery(id+"F0.wireOp",EDGE,"E12.15.0"),sQuery(id+"F0.wireOp",EDGE,"E12.15.1"),sQuery(id+"F0.wireOp",EDGE,"E12.15.2"),sQuery(id+"F0.wireOp",EDGE,"E12.15.3"),sQuery(id+"F0.wireOp",EDGE,"E12.15.4"),sQuery(id+"F0.wireOp",EDGE,"E12.15.5"),sQuery(id+"F0.wireOp",EDGE,"E12.15.6"),sQuery(id+"F0.wireOp",EDGE,"E12.15.7"),sQuery(id+"F0.wireOp",EDGE,"E12.15.8"),sQuery(id+"F0.wireOp",EDGE,"E12.15.9"),sQuery(id+"F0.wireOp",EDGE,"E12.16.0"),sQuery(id+"F0.wireOp",EDGE,"E12.16.1"),sQuery(id+"F0.wireOp",EDGE,"E12.16.2"),sQuery(id+"F0.wireOp",EDGE,"E12.16.3"),sQuery(id+"F0.wireOp",EDGE,"E12.16.4"),sQuery(id+"F0.wireOp",EDGE,"E12.16.5"),sQuery(id+"F0.wireOp",EDGE,"E12.16.6"),sQuery(id+"F0.wireOp",EDGE,"E12.16.7"),sQuery(id+"F0.wireOp",EDGE,"E12.16.8"),sQuery(id+"F0.wireOp",EDGE,"E12.16.9"),sQuery(id+"F0.wireOp",EDGE,"E12.17.0"),sQuery(id+"F0.wireOp",EDGE,"E12.17.1"),sQuery(id+"F0.wireOp",EDGE,"E12.17.2"),sQuery(id+"F0.wireOp",EDGE,"E12.17.3"),sQuery(id+"F0.wireOp",EDGE,"E12.17.4"),sQuery(id+"F0.wireOp",EDGE,"E12.17.5"),sQuery(id+"F0.wireOp",EDGE,"E12.17.6"),sQuery(id+"F0.wireOp",EDGE,"E12.17.7"),sQuery(id+"F0.wireOp",EDGE,"E12.17.8"),sQuery(id+"F0.wireOp",EDGE,"E12.17.9"),sQuery(id+"F0.wireOp",EDGE,"E12.18.0"),sQuery(id+"F0.wireOp",EDGE,"E12.18.1"),sQuery(id+"F0.wireOp",EDGE,"E12.18.2"),sQuery(id+"F0.wireOp",EDGE,"E12.18.3"),sQuery(id+"F0.wireOp",EDGE,"E12.18.4"),sQuery(id+"F0.wireOp",EDGE,"E12.18.5"),sQuery(id+"F0.wireOp",EDGE,"E12.18.6"),sQuery(id+"F0.wireOp",EDGE,"E12.18.7"),sQuery(id+"F0.wireOp",EDGE,"E12.18.8"),sQuery(id+"F0.wireOp",EDGE,"E12.18.9"),sQuery(id+"F0.wireOp",EDGE,"E12.19.0"),sQuery(id+"F0.wireOp",EDGE,"E12.19.1"),sQuery(id+"F0.wireOp",EDGE,"E12.19.2"),sQuery(id+"F0.wireOp",EDGE,"E12.19.3"),sQuery(id+"F0.wireOp",EDGE,"E12.19.4"),sQuery(id+"F0.wireOp",EDGE,"E12.19.5"),sQuery(id+"F0.wireOp",EDGE,"E12.19.6"),sQuery(id+"F0.wireOp",EDGE,"E12.19.7"),sQuery(id+"F0.wireOp",EDGE,"E12.19.8"),sQuery(id+"F0.wireOp",EDGE,"E12.19.9"),sQuery(id+"F0.wireOp",EDGE,"E12.20.0"),sQuery(id+"F0.wireOp",EDGE,"E12.20.1"),sQuery(id+"F0.wireOp",EDGE,"E12.20.2"),sQuery(id+"F0.wireOp",EDGE,"E12.20.3"),sQuery(id+"F0.wireOp",EDGE,"E12.20.4"),sQuery(id+"F0.wireOp",EDGE,"E12.20.5"),sQuery(id+"F0.wireOp",EDGE,"E12.20.6"),sQuery(id+"F0.wireOp",EDGE,"E12.20.7"),sQuery(id+"F0.wireOp",EDGE,"E12.20.8"),sQuery(id+"F0.wireOp",EDGE,"E12.20.9"),sQuery(id+"F0.wireOp",EDGE,"E12.21.0"),sQuery(id+"F0.wireOp",EDGE,"E12.21.1"),sQuery(id+"F0.wireOp",EDGE,"E12.21.2"),sQuery(id+"F0.wireOp",EDGE,"E12.21.3"),sQuery(id+"F0.wireOp",EDGE,"E12.21.4"),sQuery(id+"F0.wireOp",EDGE,"E12.21.5"),sQuery(id+"F0.wireOp",EDGE,"E12.21.6"),sQuery(id+"F0.wireOp",EDGE,"E12.21.7"),sQuery(id+"F0.wireOp",EDGE,"E12.21.8"),sQuery(id+"F0.wireOp",EDGE,"E12.21.9"),sQuery(id+"F0.wireOp",EDGE,"E12.22.0"),sQuery(id+"F0.wireOp",EDGE,"E12.22.1"),sQuery(id+"F0.wireOp",EDGE,"E12.22.2"),sQuery(id+"F0.wireOp",EDGE,"E12.22.3"),sQuery(id+"F0.wireOp",EDGE,"E12.22.4"),sQuery(id+"F0.wireOp",EDGE,"E12.22.5"),sQuery(id+"F0.wireOp",EDGE,"E12.22.6"),sQuery(id+"F0.wireOp",EDGE,"E12.22.7"),sQuery(id+"F0.wireOp",EDGE,"E12.22.8"),sQuery(id+"F0.wireOp",EDGE,"E12.22.9"),sQuery(id+"F0.wireOp",EDGE,"E12.23.0"),sQuery(id+"F0.wireOp",EDGE,"E12.23.1"),sQuery(id+"F0.wireOp",EDGE,"E12.23.2"),sQuery(id+"F0.wireOp",EDGE,"E12.23.3"),sQuery(id+"F0.wireOp",EDGE,"E12.23.4"),sQuery(id+"F0.wireOp",EDGE,"E12.23.5"),sQuery(id+"F0.wireOp",EDGE,"E12.23.6"),sQuery(id+"F0.wireOp",EDGE,"E12.23.7"),sQuery(id+"F0.wireOp",EDGE,"E12.23.8"),sQuery(id+"F0.wireOp",EDGE,"E12.23.9"),sQuery(id+"F0.wireOp",EDGE,"E12.24.0"),sQuery(id+"F0.wireOp",EDGE,"E12.24.1"),sQuery(id+"F0.wireOp",EDGE,"E12.24.2"),sQuery(id+"F0.wireOp",EDGE,"E12.24.3"),sQuery(id+"F0.wireOp",EDGE,"E12.24.4"),sQuery(id+"F0.wireOp",EDGE,"E12.24.5"),sQuery(id+"F0.wireOp",EDGE,"E12.24.6"),sQuery(id+"F0.wireOp",EDGE,"E12.24.7"),sQuery(id+"F0.wireOp",EDGE,"E12.24.8"),sQuery(id+"F0.wireOp",EDGE,"E12.24.9"),sQuery(id+"F0.wireOp",EDGE,"E12.25.0"),sQuery(id+"F0.wireOp",EDGE,"E12.25.1"),sQuery(id+"F0.wireOp",EDGE,"E12.25.2"),sQuery(id+"F0.wireOp",EDGE,"E12.25.3"),sQuery(id+"F0.wireOp",EDGE,"E12.25.4"),sQuery(id+"F0.wireOp",EDGE,"E12.25.5"),sQuery(id+"F0.wireOp",EDGE,"E12.25.6"),sQuery(id+"F0.wireOp",EDGE,"E12.25.7"),sQuery(id+"F0.wireOp",EDGE,"E12.25.8"),sQuery(id+"F0.wireOp",EDGE,"E12.25.9"),sQuery(id+"F0.wireOp",EDGE,"E12.26.0"),sQuery(id+"F0.wireOp",EDGE,"E12.26.1"),sQuery(id+"F0.wireOp",EDGE,"E12.26.2"),sQuery(id+"F0.wireOp",EDGE,"E12.26.3"),sQuery(id+"F0.wireOp",EDGE,"E12.26.4"),sQuery(id+"F0.wireOp",EDGE,"E12.26.5"),sQuery(id+"F0.wireOp",EDGE,"E12.26.6"),sQuery(id+"F0.wireOp",EDGE,"E12.26.7"),sQuery(id+"F0.wireOp",EDGE,"E12.26.8"),sQuery(id+"F0.wireOp",EDGE,"E12.26.9"),sQuery(id+"F0.wireOp",EDGE,"E12.27.0"),sQuery(id+"F0.wireOp",EDGE,"E12.27.1"),sQuery(id+"F0.wireOp",EDGE,"E12.27.2"),sQuery(id+"F0.wireOp",EDGE,"E12.27.3"),sQuery(id+"F0.wireOp",EDGE,"E12.27.4"),sQuery(id+"F0.wireOp",EDGE,"E12.27.5"),sQuery(id+"F0.wireOp",EDGE,"E12.27.6"),sQuery(id+"F0.wireOp",EDGE,"E12.27.7"),sQuery(id+"F0.wireOp",EDGE,"E12.27.8"),sQuery(id+"F0.wireOp",EDGE,"E12.27.9"),sQuery(id+"F0.wireOp",EDGE,"E12.28.0"),sQuery(id+"F0.wireOp",EDGE,"E12.28.1"),sQuery(id+"F0.wireOp",EDGE,"E12.28.2"),sQuery(id+"F0.wireOp",EDGE,"E12.28.3"),sQuery(id+"F0.wireOp",EDGE,"E12.28.4"),sQuery(id+"F0.wireOp",EDGE,"E12.28.5"),sQuery(id+"F0.wireOp",EDGE,"E12.28.6"),sQuery(id+"F0.wireOp",EDGE,"E12.28.7"),sQuery(id+"F0.wireOp",EDGE,"E12.28.8"),sQuery(id+"F0.wireOp",EDGE,"E12.28.9"),sQuery(id+"F0.wireOp",EDGE,"E12.29.0"),sQuery(id+"F0.wireOp",EDGE,"E12.29.1"),sQuery(id+"F0.wireOp",EDGE,"E12.29.2"),sQuery(id+"F0.wireOp",EDGE,"E12.29.3"),sQuery(id+"F0.wireOp",EDGE,"E12.29.4"),sQuery(id+"F0.wireOp",EDGE,"E12.29.5"),sQuery(id+"F0.wireOp",EDGE,"E12.29.6"),sQuery(id+"F0.wireOp",EDGE,"E12.29.7"),sQuery(id+"F0.wireOp",EDGE,"E12.29.8"),sQuery(id+"F0.wireOp",EDGE,"E12.29.9"),sQuery(id+"F0.wireOp",EDGE,"E12.30.0"),sQuery(id+"F0.wireOp",EDGE,"E12.30.1"),sQuery(id+"F0.wireOp",EDGE,"E12.30.2"),sQuery(id+"F0.wireOp",EDGE,"E12.30.3"),sQuery(id+"F0.wireOp",EDGE,"E12.30.4"),sQuery(id+"F0.wireOp",EDGE,"E12.30.5"),sQuery(id+"F0.wireOp",EDGE,"E12.30.6"),sQuery(id+"F0.wireOp",EDGE,"E12.30.7"),sQuery(id+"F0.wireOp",EDGE,"E12.30.8"),sQuery(id+"F0.wireOp",EDGE,"E12.30.9"),sQuery(id+"F0.wireOp",EDGE,"E12.31.0"),sQuery(id+"F0.wireOp",EDGE,"E12.31.1"),sQuery(id+"F0.wireOp",EDGE,"E12.31.2"),sQuery(id+"F0.wireOp",EDGE,"E12.31.3"),sQuery(id+"F0.wireOp",EDGE,"E12.31.4"),sQuery(id+"F0.wireOp",EDGE,"E12.31.5"),sQuery(id+"F0.wireOp",EDGE,"E12.31.6"),sQuery(id+"F0.wireOp",EDGE,"E12.31.7"),sQuery(id+"F0.wireOp",EDGE,"E12.31.8"),sQuery(id+"F0.wireOp",EDGE,"E12.31.9"),sQuery(id+"F0.wireOp",EDGE,"E12.32.0"),sQuery(id+"F0.wireOp",EDGE,"E12.32.1"),sQuery(id+"F0.wireOp",EDGE,"E12.32.2"),sQuery(id+"F0.wireOp",EDGE,"E12.32.3"),sQuery(id+"F0.wireOp",EDGE,"E12.32.4"),sQuery(id+"F0.wireOp",EDGE,"E12.32.5"),sQuery(id+"F0.wireOp",EDGE,"E12.32.6"),sQuery(id+"F0.wireOp",EDGE,"E12.32.7"),sQuery(id+"F0.wireOp",EDGE,"E12.32.8"),sQuery(id+"F0.wireOp",EDGE,"E12.32.9"),sQuery(id+"F0.wireOp",EDGE,"E12.33.0"),sQuery(id+"F0.wireOp",EDGE,"E12.33.1"),sQuery(id+"F0.wireOp",EDGE,"E12.33.2"),sQuery(id+"F0.wireOp",EDGE,"E12.33.3"),sQuery(id+"F0.wireOp",EDGE,"E12.33.4"),sQuery(id+"F0.wireOp",EDGE,"E12.33.5"),sQuery(id+"F0.wireOp",EDGE,"E12.33.6"),sQuery(id+"F0.wireOp",EDGE,"E12.33.7"),sQuery(id+"F0.wireOp",EDGE,"E12.33.8"),sQuery(id+"F0.wireOp",EDGE,"E12.33.9"),sQuery(id+"F0.wireOp",EDGE,"E12.34.0"),sQuery(id+"F0.wireOp",EDGE,"E12.34.1"),sQuery(id+"F0.wireOp",EDGE,"E12.34.2"),sQuery(id+"F0.wireOp",EDGE,"E12.34.3"),sQuery(id+"F0.wireOp",EDGE,"E12.34.4"),sQuery(id+"F0.wireOp",EDGE,"E12.34.5"),sQuery(id+"F0.wireOp",EDGE,"E12.34.6"),sQuery(id+"F0.wireOp",EDGE,"E12.34.7"),sQuery(id+"F0.wireOp",EDGE,"E12.34.8"),sQuery(id+"F0.wireOp",EDGE,"E12.34.9"),sQuery(id+"F0.wireOp",EDGE,"E12.35.0"),sQuery(id+"F0.wireOp",EDGE,"E12.35.1"),sQuery(id+"F0.wireOp",EDGE,"E12.35.2"),sQuery(id+"F0.wireOp",EDGE,"E12.35.3"),sQuery(id+"F0.wireOp",EDGE,"E12.35.4"),sQuery(id+"F0.wireOp",EDGE,"E12.35.5"),sQuery(id+"F0.wireOp",EDGE,"E12.35.6"),sQuery(id+"F0.wireOp",EDGE,"E12.35.7"),sQuery(id+"F0.wireOp",EDGE,"E12.35.8"),sQuery(id+"F0.wireOp",EDGE,"E12.35.9"),sQuery(id+"F0.wireOp",EDGE,"E12.36.0"),sQuery(id+"F0.wireOp",EDGE,"E12.36.1"),sQuery(id+"F0.wireOp",EDGE,"E12.36.2"),sQuery(id+"F0.wireOp",EDGE,"E12.36.3"),sQuery(id+"F0.wireOp",EDGE,"E12.36.4"),sQuery(id+"F0.wireOp",EDGE,"E12.36.5"),sQuery(id+"F0.wireOp",EDGE,"E12.36.6"),sQuery(id+"F0.wireOp",EDGE,"E12.36.7"),sQuery(id+"F0.wireOp",EDGE,"E12.36.8"),sQuery(id+"F0.wireOp",EDGE,"E12.36.9"),sQuery(id+"F0.wireOp",EDGE,"E12.37.0"),sQuery(id+"F0.wireOp",EDGE,"E12.37.1"),sQuery(id+"F0.wireOp",EDGE,"E12.37.2"),sQuery(id+"F0.wireOp",EDGE,"E12.37.3"),sQuery(id+"F0.wireOp",EDGE,"E12.37.4"),sQuery(id+"F0.wireOp",EDGE,"E12.37.5"),sQuery(id+"F0.wireOp",EDGE,"E12.37.6"),sQuery(id+"F0.wireOp",EDGE,"E12.37.7"),sQuery(id+"F0.wireOp",EDGE,"E12.37.8"),sQuery(id+"F0.wireOp",EDGE,"E12.37.9"),sQuery(id+"F0.wireOp",EDGE,"E12.38.0"),sQuery(id+"F0.wireOp",EDGE,"E12.38.1"),sQuery(id+"F0.wireOp",EDGE,"E12.38.2"),sQuery(id+"F0.wireOp",EDGE,"E12.38.3"),sQuery(id+"F0.wireOp",EDGE,"E12.38.4"),sQuery(id+"F0.wireOp",EDGE,"E12.38.5"),sQuery(id+"F0.wireOp",EDGE,"E12.38.6"),sQuery(id+"F0.wireOp",EDGE,"E12.38.7"),sQuery(id+"F0.wireOp",EDGE,"E12.38.8"),sQuery(id+"F0.wireOp",EDGE,"E12.38.9"),sQuery(id+"F0.wireOp",EDGE,"E12.39.0"),sQuery(id+"F0.wireOp",EDGE,"E12.39.1"),sQuery(id+"F0.wireOp",EDGE,"E12.39.2"),sQuery(id+"F0.wireOp",EDGE,"E12.39.3"),sQuery(id+"F0.wireOp",EDGE,"E12.39.4"),sQuery(id+"F0.wireOp",EDGE,"E12.39.5"),sQuery(id+"F0.wireOp",EDGE,"E12.39.6"),sQuery(id+"F0.wireOp",EDGE,"E12.39.7"),sQuery(id+"F0.wireOp",EDGE,"E12.39.8"),sQuery(id+"F0.wireOp",EDGE,"E12.39.9"),sQuery(id+"F0.wireOp",EDGE,"E12.40.0"),sQuery(id+"F0.wireOp",EDGE,"E12.40.1"),sQuery(id+"F0.wireOp",EDGE,"E12.40.2"),sQuery(id+"F0.wireOp",EDGE,"E12.40.3"),sQuery(id+"F0.wireOp",EDGE,"E12.40.4"),sQuery(id+"F0.wireOp",EDGE,"E12.40.5"),sQuery(id+"F0.wireOp",EDGE,"E12.40.6"),sQuery(id+"F0.wireOp",EDGE,"E12.40.7"),sQuery(id+"F0.wireOp",EDGE,"E12.40.8"),sQuery(id+"F0.wireOp",EDGE,"E12.40.9"),sQuery(id+"F0.wireOp",EDGE,"E12.41.0"),sQuery(id+"F0.wireOp",EDGE,"E12.41.1"),sQuery(id+"F0.wireOp",EDGE,"E12.41.2"),sQuery(id+"F0.wireOp",EDGE,"E12.41.3"),sQuery(id+"F0.wireOp",EDGE,"E12.41.4"),sQuery(id+"F0.wireOp",EDGE,"E12.41.5"),sQuery(id+"F0.wireOp",EDGE,"E12.41.6"),sQuery(id+"F0.wireOp",EDGE,"E12.41.7"),sQuery(id+"F0.wireOp",EDGE,"E12.41.8"),sQuery(id+"F0.wireOp",EDGE,"E12.41.9"),sQuery(id+"F0.wireOp",EDGE,"E12.42.0"),sQuery(id+"F0.wireOp",EDGE,"E12.42.1"),sQuery(id+"F0.wireOp",EDGE,"E12.42.2"),sQuery(id+"F0.wireOp",EDGE,"E12.42.3"),sQuery(id+"F0.wireOp",EDGE,"E12.42.4"),sQuery(id+"F0.wireOp",EDGE,"E12.42.5"),sQuery(id+"F0.wireOp",EDGE,"E12.42.6"),sQuery(id+"F0.wireOp",EDGE,"E12.42.7"),sQuery(id+"F0.wireOp",EDGE,"E12.42.8"),sQuery(id+"F0.wireOp",EDGE,"E12.42.9"),sQuery(id+"F0.wireOp",EDGE,"E12.43.0"),sQuery(id+"F0.wireOp",EDGE,"E12.43.1"),sQuery(id+"F0.wireOp",EDGE,"E12.43.2"),sQuery(id+"F0.wireOp",EDGE,"E12.43.3"),sQuery(id+"F0.wireOp",EDGE,"E12.43.4"),sQuery(id+"F0.wireOp",EDGE,"E12.43.5"),sQuery(id+"F0.wireOp",EDGE,"E12.43.6"),sQuery(id+"F0.wireOp",EDGE,"E12.43.7"),sQuery(id+"F0.wireOp",EDGE,"E12.43.8"),sQuery(id+"F0.wireOp",EDGE,"E12.43.9"),sQuery(id+"F0.wireOp",EDGE,"E12.44.0"),sQuery(id+"F0.wireOp",EDGE,"E12.44.1"),sQuery(id+"F0.wireOp",EDGE,"E12.44.2"),sQuery(id+"F0.wireOp",EDGE,"E12.44.3"),sQuery(id+"F0.wireOp",EDGE,"E12.44.4"),sQuery(id+"F0.wireOp",EDGE,"E12.44.5"),sQuery(id+"F0.wireOp",EDGE,"E12.44.6"),sQuery(id+"F0.wireOp",EDGE,"E12.44.7"),sQuery(id+"F0.wireOp",EDGE,"E12.44.8"),sQuery(id+"F0.wireOp",EDGE,"E12.44.9"),sQuery(id+"F0.wireOp",EDGE,"E12.45.0"),sQuery(id+"F0.wireOp",EDGE,"E12.45.1"),sQuery(id+"F0.wireOp",EDGE,"E12.45.2"),sQuery(id+"F0.wireOp",EDGE,"E12.45.3"),sQuery(id+"F0.wireOp",EDGE,"E12.45.4"),sQuery(id+"F0.wireOp",EDGE,"E12.45.5"),sQuery(id+"F0.wireOp",EDGE,"E12.45.6"),sQuery(id+"F0.wireOp",EDGE,"E12.45.7"),sQuery(id+"F0.wireOp",EDGE,"E12.45.8"),sQuery(id+"F0.wireOp",EDGE,"E12.45.9"),sQuery(id+"F0.wireOp",EDGE,"E12.46.0"),sQuery(id+"F0.wireOp",EDGE,"E12.46.1"),sQuery(id+"F0.wireOp",EDGE,"E12.46.2"),sQuery(id+"F0.wireOp",EDGE,"E12.46.3"),sQuery(id+"F0.wireOp",EDGE,"E12.46.4"),sQuery(id+"F0.wireOp",EDGE,"E12.46.5"),sQuery(id+"F0.wireOp",EDGE,"E12.46.6"),sQuery(id+"F0.wireOp",EDGE,"E12.46.7"),sQuery(id+"F0.wireOp",EDGE,"E12.46.8"),sQuery(id+"F0.wireOp",EDGE,"E12.46.9"),sQuery(id+"F0.wireOp",EDGE,"E12.47.0"),sQuery(id+"F0.wireOp",EDGE,"E12.47.1"),sQuery(id+"F0.wireOp",EDGE,"E12.47.2"),sQuery(id+"F0.wireOp",EDGE,"E12.47.3"),sQuery(id+"F0.wireOp",EDGE,"E12.47.4"),sQuery(id+"F0.wireOp",EDGE,"E12.47.5"),sQuery(id+"F0.wireOp",EDGE,"E12.47.6"),sQuery(id+"F0.wireOp",EDGE,"E12.47.7"),sQuery(id+"F0.wireOp",EDGE,"E12.47.8"),sQuery(id+"F0.wireOp",EDGE,"E12.47.9"),sQuery(id+"F0.wireOp",EDGE,"E12.48.0"),sQuery(id+"F0.wireOp",EDGE,"E12.48.1"),sQuery(id+"F0.wireOp",EDGE,"E12.48.2"),sQuery(id+"F0.wireOp",EDGE,"E12.48.3"),sQuery(id+"F0.wireOp",EDGE,"E12.48.4"),sQuery(id+"F0.wireOp",EDGE,"E12.48.5"),sQuery(id+"F0.wireOp",EDGE,"E12.48.6"),sQuery(id+"F0.wireOp",EDGE,"E12.48.7"),sQuery(id+"F0.wireOp",EDGE,"E12.48.8"),sQuery(id+"F0.wireOp",EDGE,"E12.48.9"),sQuery(id+"F0.wireOp",EDGE,"E12.49.0"),sQuery(id+"F0.wireOp",EDGE,"E12.49.1"),sQuery(id+"F0.wireOp",EDGE,"E12.49.2"),sQuery(id+"F0.wireOp",EDGE,"E12.49.3"),sQuery(id+"F0.wireOp",EDGE,"E12.49.4"),sQuery(id+"F0.wireOp",EDGE,"E12.49.5"),sQuery(id+"F0.wireOp",EDGE,"E12.49.6"),sQuery(id+"F0.wireOp",EDGE,"E12.49.7"),sQuery(id+"F0.wireOp",EDGE,"E12.49.8"),sQuery(id+"F0.wireOp",EDGE,"E12.49.9"),sQuery(id+"F0.wireOp",EDGE,"E12.50.0"),sQuery(id+"F0.wireOp",EDGE,"E12.50.1"),sQuery(id+"F0.wireOp",EDGE,"E12.50.2"),sQuery(id+"F0.wireOp",EDGE,"E12.50.3"),sQuery(id+"F0.wireOp",EDGE,"E12.50.4"),sQuery(id+"F0.wireOp",EDGE,"E12.50.5"),sQuery(id+"F0.wireOp",EDGE,"E12.50.6"),sQuery(id+"F0.wireOp",EDGE,"E12.50.7"),sQuery(id+"F0.wireOp",EDGE,"E12.50.8"),sQuery(id+"F0.wireOp",EDGE,"E12.50.9"),sQuery(id+"F0.wireOp",EDGE,"E12.51.0"),sQuery(id+"F0.wireOp",EDGE,"E12.51.1"),sQuery(id+"F0.wireOp",EDGE,"E12.51.2"),sQuery(id+"F0.wireOp",EDGE,"E12.51.3"),sQuery(id+"F0.wireOp",EDGE,"E12.51.4"),sQuery(id+"F0.wireOp",EDGE,"E12.51.5"),sQuery(id+"F0.wireOp",EDGE,"E12.51.6"),sQuery(id+"F0.wireOp",EDGE,"E12.51.7"),sQuery(id+"F0.wireOp",EDGE,"E12.51.8"),sQuery(id+"F0.wireOp",EDGE,"E12.51.9"),sQuery(id+"F0.wireOp",EDGE,"E12.52.0"),sQuery(id+"F0.wireOp",EDGE,"E12.52.1"),sQuery(id+"F0.wireOp",EDGE,"E12.52.2"),sQuery(id+"F0.wireOp",EDGE,"E12.52.3"),sQuery(id+"F0.wireOp",EDGE,"E12.52.4"),sQuery(id+"F0.wireOp",EDGE,"E12.52.5"),sQuery(id+"F0.wireOp",EDGE,"E12.52.6"),sQuery(id+"F0.wireOp",EDGE,"E12.52.7"),sQuery(id+"F0.wireOp",EDGE,"E12.52.8"),sQuery(id+"F0.wireOp",EDGE,"E12.52.9"),sQuery(id+"F0.wireOp",EDGE,"E12.53.0"),sQuery(id+"F0.wireOp",EDGE,"E12.53.1"),sQuery(id+"F0.wireOp",EDGE,"E12.53.2"),sQuery(id+"F0.wireOp",EDGE,"E12.53.3"),sQuery(id+"F0.wireOp",EDGE,"E12.53.4"),sQuery(id+"F0.wireOp",EDGE,"E12.53.5"),sQuery(id+"F0.wireOp",EDGE,"E12.53.6"),sQuery(id+"F0.wireOp",EDGE,"E12.53.7"),sQuery(id+"F0.wireOp",EDGE,"E12.53.8"),sQuery(id+"F0.wireOp",EDGE,"E12.53.9"),sQuery(id+"F0.wireOp",EDGE,"E12.54.0"),sQuery(id+"F0.wireOp",EDGE,"E12.54.1"),sQuery(id+"F0.wireOp",EDGE,"E12.54.2"),sQuery(id+"F0.wireOp",EDGE,"E12.54.3"),sQuery(id+"F0.wireOp",EDGE,"E12.54.4"),sQuery(id+"F0.wireOp",EDGE,"E12.54.5"),sQuery(id+"F0.wireOp",EDGE,"E12.54.6"),sQuery(id+"F0.wireOp",EDGE,"E12.54.7"),sQuery(id+"F0.wireOp",EDGE,"E12.54.8"),sQuery(id+"F0.wireOp",EDGE,"E12.54.9"),sQuery(id+"F0.wireOp",EDGE,"E12.55.0"),sQuery(id+"F0.wireOp",EDGE,"E12.55.1"),sQuery(id+"F0.wireOp",EDGE,"E12.55.2"),sQuery(id+"F0.wireOp",EDGE,"E12.55.3"),sQuery(id+"F0.wireOp",EDGE,"E12.55.4"),sQuery(id+"F0.wireOp",EDGE,"E12.55.5"),sQuery(id+"F0.wireOp",EDGE,"E12.55.6"),sQuery(id+"F0.wireOp",EDGE,"E12.55.7"),sQuery(id+"F0.wireOp",EDGE,"E12.55.8"),sQuery(id+"F0.wireOp",EDGE,"E12.55.9"),sQuery(id+"F0.wireOp",EDGE,"E12.56.0"),sQuery(id+"F0.wireOp",EDGE,"E12.56.1"),sQuery(id+"F0.wireOp",EDGE,"E12.56.2"),sQuery(id+"F0.wireOp",EDGE,"E12.56.3"),sQuery(id+"F0.wireOp",EDGE,"E12.56.4"),sQuery(id+"F0.wireOp",EDGE,"E12.56.5"),sQuery(id+"F0.wireOp",EDGE,"E12.56.6"),sQuery(id+"F0.wireOp",EDGE,"E12.56.7"),sQuery(id+"F0.wireOp",EDGE,"E12.56.8"),sQuery(id+"F0.wireOp",EDGE,"E12.56.9"),sQuery(id+"F0.wireOp",EDGE,"E12.57.0"),sQuery(id+"F0.wireOp",EDGE,"E12.57.1"),sQuery(id+"F0.wireOp",EDGE,"E12.57.2"),sQuery(id+"F0.wireOp",EDGE,"E12.57.3"),sQuery(id+"F0.wireOp",EDGE,"E12.57.4"),sQuery(id+"F0.wireOp",EDGE,"E12.57.5"),sQuery(id+"F0.wireOp",EDGE,"E12.57.6"),sQuery(id+"F0.wireOp",EDGE,"E12.57.7"),sQuery(id+"F0.wireOp",EDGE,"E12.57.8"),sQuery(id+"F0.wireOp",EDGE,"E12.57.9"),sQuery(id+"F0.wireOp",EDGE,"E12.58.0"),sQuery(id+"F0.wireOp",EDGE,"E12.58.1"),sQuery(id+"F0.wireOp",EDGE,"E12.58.2"),sQuery(id+"F0.wireOp",EDGE,"E12.58.3"),sQuery(id+"F0.wireOp",EDGE,"E12.58.4"),sQuery(id+"F0.wireOp",EDGE,"E12.58.5"),sQuery(id+"F0.wireOp",EDGE,"E12.58.6"),sQuery(id+"F0.wireOp",EDGE,"E12.58.7"),sQuery(id+"F0.wireOp",EDGE,"E12.58.8"),sQuery(id+"F0.wireOp",EDGE,"E12.58.9"),sQuery(id+"F0.wireOp",EDGE,"E12.59.0"),sQuery(id+"F0.wireOp",EDGE,"E12.59.1"),sQuery(id+"F0.wireOp",EDGE,"E12.59.2"),sQuery(id+"F0.wireOp",EDGE,"E12.59.3"),sQuery(id+"F0.wireOp",EDGE,"E12.59.4"),sQuery(id+"F0.wireOp",EDGE,"E12.59.5"),sQuery(id+"F0.wireOp",EDGE,"E12.59.6"),sQuery(id+"F0.wireOp",EDGE,"E12.59.7"),sQuery(id+"F0.wireOp",EDGE,"E12.59.8"),sQuery(id+"F0.wireOp",EDGE,"E12.59.9"),sQuery(id+"F0.wireOp",EDGE,"E13.trimOffspring"),sQuery(id+"F0.wireOp",EDGE,"E14.trimOffspring")])],"isStart":true}),makeQuery(id+"F3.opExtrude","SWEPT_FACE",FACE,{"disambiguationData":[OSD([sQuery(id+"F2.wireOp",EDGE,"E17.7.0")])]})]});
            var Q12;
            Q12=makeQuery(id+"F3.boolean.opBoolean","INTERSECT",EDGE,{"derivedFrom":[makeQuery(id+"F1.opExtrude","CAP_FACE",FACE,{"disambiguationData":[OSD([sQuery(id+"F0.wireOp",EDGE,"E0"),sQuery(id+"F0.wireOp",EDGE,"E2"),sQuery(id+"F0.wireOp",EDGE,"E3"),sQuery(id+"F0.wireOp",EDGE,"E4.trimOffspring"),sQuery(id+"F0.wireOp",EDGE,"E5.MirrorCS"),sQuery(id+"F0.wireOp",EDGE,"E6.MirrorCS"),sQuery(id+"F0.wireOp",EDGE,"E7.MirrorCS"),sQuery(id+"F0.wireOp",EDGE,"E8.filletArc"),sQuery(id+"F0.wireOp",EDGE,"E9.filletArc"),sQuery(id+"F0.wireOp",EDGE,"E10.filletArc"),sQuery(id+"F0.wireOp",EDGE,"E11.filletArc"),sQuery(id+"F0.wireOp",EDGE,"E12.1.0"),sQuery(id+"F0.wireOp",EDGE,"E12.1.1"),sQuery(id+"F0.wireOp",EDGE,"E12.1.2"),sQuery(id+"F0.wireOp",EDGE,"E12.1.3"),sQuery(id+"F0.wireOp",EDGE,"E12.1.4"),sQuery(id+"F0.wireOp",EDGE,"E12.1.5"),sQuery(id+"F0.wireOp",EDGE,"E12.1.6"),sQuery(id+"F0.wireOp",EDGE,"E12.1.7"),sQuery(id+"F0.wireOp",EDGE,"E12.1.8"),sQuery(id+"F0.wireOp",EDGE,"E12.1.9"),sQuery(id+"F0.wireOp",EDGE,"E12.2.0"),sQuery(id+"F0.wireOp",EDGE,"E12.2.1"),sQuery(id+"F0.wireOp",EDGE,"E12.2.2"),sQuery(id+"F0.wireOp",EDGE,"E12.2.3"),sQuery(id+"F0.wireOp",EDGE,"E12.2.4"),sQuery(id+"F0.wireOp",EDGE,"E12.2.5"),sQuery(id+"F0.wireOp",EDGE,"E12.2.6"),sQuery(id+"F0.wireOp",EDGE,"E12.2.7"),sQuery(id+"F0.wireOp",EDGE,"E12.2.8"),sQuery(id+"F0.wireOp",EDGE,"E12.2.9"),sQuery(id+"F0.wireOp",EDGE,"E12.3.0"),sQuery(id+"F0.wireOp",EDGE,"E12.3.1"),sQuery(id+"F0.wireOp",EDGE,"E12.3.2"),sQuery(id+"F0.wireOp",EDGE,"E12.3.3"),sQuery(id+"F0.wireOp",EDGE,"E12.3.4"),sQuery(id+"F0.wireOp",EDGE,"E12.3.5"),sQuery(id+"F0.wireOp",EDGE,"E12.3.6"),sQuery(id+"F0.wireOp",EDGE,"E12.3.7"),sQuery(id+"F0.wireOp",EDGE,"E12.3.8"),sQuery(id+"F0.wireOp",EDGE,"E12.3.9"),sQuery(id+"F0.wireOp",EDGE,"E12.4.0"),sQuery(id+"F0.wireOp",EDGE,"E12.4.1"),sQuery(id+"F0.wireOp",EDGE,"E12.4.2"),sQuery(id+"F0.wireOp",EDGE,"E12.4.3"),sQuery(id+"F0.wireOp",EDGE,"E12.4.4"),sQuery(id+"F0.wireOp",EDGE,"E12.4.5"),sQuery(id+"F0.wireOp",EDGE,"E12.4.6"),sQuery(id+"F0.wireOp",EDGE,"E12.4.7"),sQuery(id+"F0.wireOp",EDGE,"E12.4.8"),sQuery(id+"F0.wireOp",EDGE,"E12.4.9"),sQuery(id+"F0.wireOp",EDGE,"E12.5.0"),sQuery(id+"F0.wireOp",EDGE,"E12.5.1"),sQuery(id+"F0.wireOp",EDGE,"E12.5.2"),sQuery(id+"F0.wireOp",EDGE,"E12.5.3"),sQuery(id+"F0.wireOp",EDGE,"E12.5.4"),sQuery(id+"F0.wireOp",EDGE,"E12.5.5"),sQuery(id+"F0.wireOp",EDGE,"E12.5.6"),sQuery(id+"F0.wireOp",EDGE,"E12.5.7"),sQuery(id+"F0.wireOp",EDGE,"E12.5.8"),sQuery(id+"F0.wireOp",EDGE,"E12.5.9"),sQuery(id+"F0.wireOp",EDGE,"E12.6.0"),sQuery(id+"F0.wireOp",EDGE,"E12.6.1"),sQuery(id+"F0.wireOp",EDGE,"E12.6.2"),sQuery(id+"F0.wireOp",EDGE,"E12.6.3"),sQuery(id+"F0.wireOp",EDGE,"E12.6.4"),sQuery(id+"F0.wireOp",EDGE,"E12.6.5"),sQuery(id+"F0.wireOp",EDGE,"E12.6.6"),sQuery(id+"F0.wireOp",EDGE,"E12.6.7"),sQuery(id+"F0.wireOp",EDGE,"E12.6.8"),sQuery(id+"F0.wireOp",EDGE,"E12.6.9"),sQuery(id+"F0.wireOp",EDGE,"E12.7.0"),sQuery(id+"F0.wireOp",EDGE,"E12.7.1"),sQuery(id+"F0.wireOp",EDGE,"E12.7.2"),sQuery(id+"F0.wireOp",EDGE,"E12.7.3"),sQuery(id+"F0.wireOp",EDGE,"E12.7.4"),sQuery(id+"F0.wireOp",EDGE,"E12.7.5"),sQuery(id+"F0.wireOp",EDGE,"E12.7.6"),sQuery(id+"F0.wireOp",EDGE,"E12.7.7"),sQuery(id+"F0.wireOp",EDGE,"E12.7.8"),sQuery(id+"F0.wireOp",EDGE,"E12.7.9"),sQuery(id+"F0.wireOp",EDGE,"E12.8.0"),sQuery(id+"F0.wireOp",EDGE,"E12.8.1"),sQuery(id+"F0.wireOp",EDGE,"E12.8.2"),sQuery(id+"F0.wireOp",EDGE,"E12.8.3"),sQuery(id+"F0.wireOp",EDGE,"E12.8.4"),sQuery(id+"F0.wireOp",EDGE,"E12.8.5"),sQuery(id+"F0.wireOp",EDGE,"E12.8.6"),sQuery(id+"F0.wireOp",EDGE,"E12.8.7"),sQuery(id+"F0.wireOp",EDGE,"E12.8.8"),sQuery(id+"F0.wireOp",EDGE,"E12.8.9"),sQuery(id+"F0.wireOp",EDGE,"E12.9.0"),sQuery(id+"F0.wireOp",EDGE,"E12.9.1"),sQuery(id+"F0.wireOp",EDGE,"E12.9.2"),sQuery(id+"F0.wireOp",EDGE,"E12.9.3"),sQuery(id+"F0.wireOp",EDGE,"E12.9.4"),sQuery(id+"F0.wireOp",EDGE,"E12.9.5"),sQuery(id+"F0.wireOp",EDGE,"E12.9.6"),sQuery(id+"F0.wireOp",EDGE,"E12.9.7"),sQuery(id+"F0.wireOp",EDGE,"E12.9.8"),sQuery(id+"F0.wireOp",EDGE,"E12.9.9"),sQuery(id+"F0.wireOp",EDGE,"E12.10.0"),sQuery(id+"F0.wireOp",EDGE,"E12.10.1"),sQuery(id+"F0.wireOp",EDGE,"E12.10.2"),sQuery(id+"F0.wireOp",EDGE,"E12.10.3"),sQuery(id+"F0.wireOp",EDGE,"E12.10.4"),sQuery(id+"F0.wireOp",EDGE,"E12.10.5"),sQuery(id+"F0.wireOp",EDGE,"E12.10.6"),sQuery(id+"F0.wireOp",EDGE,"E12.10.7"),sQuery(id+"F0.wireOp",EDGE,"E12.10.8"),sQuery(id+"F0.wireOp",EDGE,"E12.10.9"),sQuery(id+"F0.wireOp",EDGE,"E12.11.0"),sQuery(id+"F0.wireOp",EDGE,"E12.11.1"),sQuery(id+"F0.wireOp",EDGE,"E12.11.2"),sQuery(id+"F0.wireOp",EDGE,"E12.11.3"),sQuery(id+"F0.wireOp",EDGE,"E12.11.4"),sQuery(id+"F0.wireOp",EDGE,"E12.11.5"),sQuery(id+"F0.wireOp",EDGE,"E12.11.6"),sQuery(id+"F0.wireOp",EDGE,"E12.11.7"),sQuery(id+"F0.wireOp",EDGE,"E12.11.8"),sQuery(id+"F0.wireOp",EDGE,"E12.11.9"),sQuery(id+"F0.wireOp",EDGE,"E12.12.0"),sQuery(id+"F0.wireOp",EDGE,"E12.12.1"),sQuery(id+"F0.wireOp",EDGE,"E12.12.2"),sQuery(id+"F0.wireOp",EDGE,"E12.12.3"),sQuery(id+"F0.wireOp",EDGE,"E12.12.4"),sQuery(id+"F0.wireOp",EDGE,"E12.12.5"),sQuery(id+"F0.wireOp",EDGE,"E12.12.6"),sQuery(id+"F0.wireOp",EDGE,"E12.12.7"),sQuery(id+"F0.wireOp",EDGE,"E12.12.8"),sQuery(id+"F0.wireOp",EDGE,"E12.12.9"),sQuery(id+"F0.wireOp",EDGE,"E12.13.0"),sQuery(id+"F0.wireOp",EDGE,"E12.13.1"),sQuery(id+"F0.wireOp",EDGE,"E12.13.2"),sQuery(id+"F0.wireOp",EDGE,"E12.13.3"),sQuery(id+"F0.wireOp",EDGE,"E12.13.4"),sQuery(id+"F0.wireOp",EDGE,"E12.13.5"),sQuery(id+"F0.wireOp",EDGE,"E12.13.6"),sQuery(id+"F0.wireOp",EDGE,"E12.13.7"),sQuery(id+"F0.wireOp",EDGE,"E12.13.8"),sQuery(id+"F0.wireOp",EDGE,"E12.13.9"),sQuery(id+"F0.wireOp",EDGE,"E12.14.0"),sQuery(id+"F0.wireOp",EDGE,"E12.14.1"),sQuery(id+"F0.wireOp",EDGE,"E12.14.2"),sQuery(id+"F0.wireOp",EDGE,"E12.14.3"),sQuery(id+"F0.wireOp",EDGE,"E12.14.4"),sQuery(id+"F0.wireOp",EDGE,"E12.14.5"),sQuery(id+"F0.wireOp",EDGE,"E12.14.6"),sQuery(id+"F0.wireOp",EDGE,"E12.14.7"),sQuery(id+"F0.wireOp",EDGE,"E12.14.8"),sQuery(id+"F0.wireOp",EDGE,"E12.14.9"),sQuery(id+"F0.wireOp",EDGE,"E12.15.0"),sQuery(id+"F0.wireOp",EDGE,"E12.15.1"),sQuery(id+"F0.wireOp",EDGE,"E12.15.2"),sQuery(id+"F0.wireOp",EDGE,"E12.15.3"),sQuery(id+"F0.wireOp",EDGE,"E12.15.4"),sQuery(id+"F0.wireOp",EDGE,"E12.15.5"),sQuery(id+"F0.wireOp",EDGE,"E12.15.6"),sQuery(id+"F0.wireOp",EDGE,"E12.15.7"),sQuery(id+"F0.wireOp",EDGE,"E12.15.8"),sQuery(id+"F0.wireOp",EDGE,"E12.15.9"),sQuery(id+"F0.wireOp",EDGE,"E12.16.0"),sQuery(id+"F0.wireOp",EDGE,"E12.16.1"),sQuery(id+"F0.wireOp",EDGE,"E12.16.2"),sQuery(id+"F0.wireOp",EDGE,"E12.16.3"),sQuery(id+"F0.wireOp",EDGE,"E12.16.4"),sQuery(id+"F0.wireOp",EDGE,"E12.16.5"),sQuery(id+"F0.wireOp",EDGE,"E12.16.6"),sQuery(id+"F0.wireOp",EDGE,"E12.16.7"),sQuery(id+"F0.wireOp",EDGE,"E12.16.8"),sQuery(id+"F0.wireOp",EDGE,"E12.16.9"),sQuery(id+"F0.wireOp",EDGE,"E12.17.0"),sQuery(id+"F0.wireOp",EDGE,"E12.17.1"),sQuery(id+"F0.wireOp",EDGE,"E12.17.2"),sQuery(id+"F0.wireOp",EDGE,"E12.17.3"),sQuery(id+"F0.wireOp",EDGE,"E12.17.4"),sQuery(id+"F0.wireOp",EDGE,"E12.17.5"),sQuery(id+"F0.wireOp",EDGE,"E12.17.6"),sQuery(id+"F0.wireOp",EDGE,"E12.17.7"),sQuery(id+"F0.wireOp",EDGE,"E12.17.8"),sQuery(id+"F0.wireOp",EDGE,"E12.17.9"),sQuery(id+"F0.wireOp",EDGE,"E12.18.0"),sQuery(id+"F0.wireOp",EDGE,"E12.18.1"),sQuery(id+"F0.wireOp",EDGE,"E12.18.2"),sQuery(id+"F0.wireOp",EDGE,"E12.18.3"),sQuery(id+"F0.wireOp",EDGE,"E12.18.4"),sQuery(id+"F0.wireOp",EDGE,"E12.18.5"),sQuery(id+"F0.wireOp",EDGE,"E12.18.6"),sQuery(id+"F0.wireOp",EDGE,"E12.18.7"),sQuery(id+"F0.wireOp",EDGE,"E12.18.8"),sQuery(id+"F0.wireOp",EDGE,"E12.18.9"),sQuery(id+"F0.wireOp",EDGE,"E12.19.0"),sQuery(id+"F0.wireOp",EDGE,"E12.19.1"),sQuery(id+"F0.wireOp",EDGE,"E12.19.2"),sQuery(id+"F0.wireOp",EDGE,"E12.19.3"),sQuery(id+"F0.wireOp",EDGE,"E12.19.4"),sQuery(id+"F0.wireOp",EDGE,"E12.19.5"),sQuery(id+"F0.wireOp",EDGE,"E12.19.6"),sQuery(id+"F0.wireOp",EDGE,"E12.19.7"),sQuery(id+"F0.wireOp",EDGE,"E12.19.8"),sQuery(id+"F0.wireOp",EDGE,"E12.19.9"),sQuery(id+"F0.wireOp",EDGE,"E12.20.0"),sQuery(id+"F0.wireOp",EDGE,"E12.20.1"),sQuery(id+"F0.wireOp",EDGE,"E12.20.2"),sQuery(id+"F0.wireOp",EDGE,"E12.20.3"),sQuery(id+"F0.wireOp",EDGE,"E12.20.4"),sQuery(id+"F0.wireOp",EDGE,"E12.20.5"),sQuery(id+"F0.wireOp",EDGE,"E12.20.6"),sQuery(id+"F0.wireOp",EDGE,"E12.20.7"),sQuery(id+"F0.wireOp",EDGE,"E12.20.8"),sQuery(id+"F0.wireOp",EDGE,"E12.20.9"),sQuery(id+"F0.wireOp",EDGE,"E12.21.0"),sQuery(id+"F0.wireOp",EDGE,"E12.21.1"),sQuery(id+"F0.wireOp",EDGE,"E12.21.2"),sQuery(id+"F0.wireOp",EDGE,"E12.21.3"),sQuery(id+"F0.wireOp",EDGE,"E12.21.4"),sQuery(id+"F0.wireOp",EDGE,"E12.21.5"),sQuery(id+"F0.wireOp",EDGE,"E12.21.6"),sQuery(id+"F0.wireOp",EDGE,"E12.21.7"),sQuery(id+"F0.wireOp",EDGE,"E12.21.8"),sQuery(id+"F0.wireOp",EDGE,"E12.21.9"),sQuery(id+"F0.wireOp",EDGE,"E12.22.0"),sQuery(id+"F0.wireOp",EDGE,"E12.22.1"),sQuery(id+"F0.wireOp",EDGE,"E12.22.2"),sQuery(id+"F0.wireOp",EDGE,"E12.22.3"),sQuery(id+"F0.wireOp",EDGE,"E12.22.4"),sQuery(id+"F0.wireOp",EDGE,"E12.22.5"),sQuery(id+"F0.wireOp",EDGE,"E12.22.6"),sQuery(id+"F0.wireOp",EDGE,"E12.22.7"),sQuery(id+"F0.wireOp",EDGE,"E12.22.8"),sQuery(id+"F0.wireOp",EDGE,"E12.22.9"),sQuery(id+"F0.wireOp",EDGE,"E12.23.0"),sQuery(id+"F0.wireOp",EDGE,"E12.23.1"),sQuery(id+"F0.wireOp",EDGE,"E12.23.2"),sQuery(id+"F0.wireOp",EDGE,"E12.23.3"),sQuery(id+"F0.wireOp",EDGE,"E12.23.4"),sQuery(id+"F0.wireOp",EDGE,"E12.23.5"),sQuery(id+"F0.wireOp",EDGE,"E12.23.6"),sQuery(id+"F0.wireOp",EDGE,"E12.23.7"),sQuery(id+"F0.wireOp",EDGE,"E12.23.8"),sQuery(id+"F0.wireOp",EDGE,"E12.23.9"),sQuery(id+"F0.wireOp",EDGE,"E12.24.0"),sQuery(id+"F0.wireOp",EDGE,"E12.24.1"),sQuery(id+"F0.wireOp",EDGE,"E12.24.2"),sQuery(id+"F0.wireOp",EDGE,"E12.24.3"),sQuery(id+"F0.wireOp",EDGE,"E12.24.4"),sQuery(id+"F0.wireOp",EDGE,"E12.24.5"),sQuery(id+"F0.wireOp",EDGE,"E12.24.6"),sQuery(id+"F0.wireOp",EDGE,"E12.24.7"),sQuery(id+"F0.wireOp",EDGE,"E12.24.8"),sQuery(id+"F0.wireOp",EDGE,"E12.24.9"),sQuery(id+"F0.wireOp",EDGE,"E12.25.0"),sQuery(id+"F0.wireOp",EDGE,"E12.25.1"),sQuery(id+"F0.wireOp",EDGE,"E12.25.2"),sQuery(id+"F0.wireOp",EDGE,"E12.25.3"),sQuery(id+"F0.wireOp",EDGE,"E12.25.4"),sQuery(id+"F0.wireOp",EDGE,"E12.25.5"),sQuery(id+"F0.wireOp",EDGE,"E12.25.6"),sQuery(id+"F0.wireOp",EDGE,"E12.25.7"),sQuery(id+"F0.wireOp",EDGE,"E12.25.8"),sQuery(id+"F0.wireOp",EDGE,"E12.25.9"),sQuery(id+"F0.wireOp",EDGE,"E12.26.0"),sQuery(id+"F0.wireOp",EDGE,"E12.26.1"),sQuery(id+"F0.wireOp",EDGE,"E12.26.2"),sQuery(id+"F0.wireOp",EDGE,"E12.26.3"),sQuery(id+"F0.wireOp",EDGE,"E12.26.4"),sQuery(id+"F0.wireOp",EDGE,"E12.26.5"),sQuery(id+"F0.wireOp",EDGE,"E12.26.6"),sQuery(id+"F0.wireOp",EDGE,"E12.26.7"),sQuery(id+"F0.wireOp",EDGE,"E12.26.8"),sQuery(id+"F0.wireOp",EDGE,"E12.26.9"),sQuery(id+"F0.wireOp",EDGE,"E12.27.0"),sQuery(id+"F0.wireOp",EDGE,"E12.27.1"),sQuery(id+"F0.wireOp",EDGE,"E12.27.2"),sQuery(id+"F0.wireOp",EDGE,"E12.27.3"),sQuery(id+"F0.wireOp",EDGE,"E12.27.4"),sQuery(id+"F0.wireOp",EDGE,"E12.27.5"),sQuery(id+"F0.wireOp",EDGE,"E12.27.6"),sQuery(id+"F0.wireOp",EDGE,"E12.27.7"),sQuery(id+"F0.wireOp",EDGE,"E12.27.8"),sQuery(id+"F0.wireOp",EDGE,"E12.27.9"),sQuery(id+"F0.wireOp",EDGE,"E12.28.0"),sQuery(id+"F0.wireOp",EDGE,"E12.28.1"),sQuery(id+"F0.wireOp",EDGE,"E12.28.2"),sQuery(id+"F0.wireOp",EDGE,"E12.28.3"),sQuery(id+"F0.wireOp",EDGE,"E12.28.4"),sQuery(id+"F0.wireOp",EDGE,"E12.28.5"),sQuery(id+"F0.wireOp",EDGE,"E12.28.6"),sQuery(id+"F0.wireOp",EDGE,"E12.28.7"),sQuery(id+"F0.wireOp",EDGE,"E12.28.8"),sQuery(id+"F0.wireOp",EDGE,"E12.28.9"),sQuery(id+"F0.wireOp",EDGE,"E12.29.0"),sQuery(id+"F0.wireOp",EDGE,"E12.29.1"),sQuery(id+"F0.wireOp",EDGE,"E12.29.2"),sQuery(id+"F0.wireOp",EDGE,"E12.29.3"),sQuery(id+"F0.wireOp",EDGE,"E12.29.4"),sQuery(id+"F0.wireOp",EDGE,"E12.29.5"),sQuery(id+"F0.wireOp",EDGE,"E12.29.6"),sQuery(id+"F0.wireOp",EDGE,"E12.29.7"),sQuery(id+"F0.wireOp",EDGE,"E12.29.8"),sQuery(id+"F0.wireOp",EDGE,"E12.29.9"),sQuery(id+"F0.wireOp",EDGE,"E12.30.0"),sQuery(id+"F0.wireOp",EDGE,"E12.30.1"),sQuery(id+"F0.wireOp",EDGE,"E12.30.2"),sQuery(id+"F0.wireOp",EDGE,"E12.30.3"),sQuery(id+"F0.wireOp",EDGE,"E12.30.4"),sQuery(id+"F0.wireOp",EDGE,"E12.30.5"),sQuery(id+"F0.wireOp",EDGE,"E12.30.6"),sQuery(id+"F0.wireOp",EDGE,"E12.30.7"),sQuery(id+"F0.wireOp",EDGE,"E12.30.8"),sQuery(id+"F0.wireOp",EDGE,"E12.30.9"),sQuery(id+"F0.wireOp",EDGE,"E12.31.0"),sQuery(id+"F0.wireOp",EDGE,"E12.31.1"),sQuery(id+"F0.wireOp",EDGE,"E12.31.2"),sQuery(id+"F0.wireOp",EDGE,"E12.31.3"),sQuery(id+"F0.wireOp",EDGE,"E12.31.4"),sQuery(id+"F0.wireOp",EDGE,"E12.31.5"),sQuery(id+"F0.wireOp",EDGE,"E12.31.6"),sQuery(id+"F0.wireOp",EDGE,"E12.31.7"),sQuery(id+"F0.wireOp",EDGE,"E12.31.8"),sQuery(id+"F0.wireOp",EDGE,"E12.31.9"),sQuery(id+"F0.wireOp",EDGE,"E12.32.0"),sQuery(id+"F0.wireOp",EDGE,"E12.32.1"),sQuery(id+"F0.wireOp",EDGE,"E12.32.2"),sQuery(id+"F0.wireOp",EDGE,"E12.32.3"),sQuery(id+"F0.wireOp",EDGE,"E12.32.4"),sQuery(id+"F0.wireOp",EDGE,"E12.32.5"),sQuery(id+"F0.wireOp",EDGE,"E12.32.6"),sQuery(id+"F0.wireOp",EDGE,"E12.32.7"),sQuery(id+"F0.wireOp",EDGE,"E12.32.8"),sQuery(id+"F0.wireOp",EDGE,"E12.32.9"),sQuery(id+"F0.wireOp",EDGE,"E12.33.0"),sQuery(id+"F0.wireOp",EDGE,"E12.33.1"),sQuery(id+"F0.wireOp",EDGE,"E12.33.2"),sQuery(id+"F0.wireOp",EDGE,"E12.33.3"),sQuery(id+"F0.wireOp",EDGE,"E12.33.4"),sQuery(id+"F0.wireOp",EDGE,"E12.33.5"),sQuery(id+"F0.wireOp",EDGE,"E12.33.6"),sQuery(id+"F0.wireOp",EDGE,"E12.33.7"),sQuery(id+"F0.wireOp",EDGE,"E12.33.8"),sQuery(id+"F0.wireOp",EDGE,"E12.33.9"),sQuery(id+"F0.wireOp",EDGE,"E12.34.0"),sQuery(id+"F0.wireOp",EDGE,"E12.34.1"),sQuery(id+"F0.wireOp",EDGE,"E12.34.2"),sQuery(id+"F0.wireOp",EDGE,"E12.34.3"),sQuery(id+"F0.wireOp",EDGE,"E12.34.4"),sQuery(id+"F0.wireOp",EDGE,"E12.34.5"),sQuery(id+"F0.wireOp",EDGE,"E12.34.6"),sQuery(id+"F0.wireOp",EDGE,"E12.34.7"),sQuery(id+"F0.wireOp",EDGE,"E12.34.8"),sQuery(id+"F0.wireOp",EDGE,"E12.34.9"),sQuery(id+"F0.wireOp",EDGE,"E12.35.0"),sQuery(id+"F0.wireOp",EDGE,"E12.35.1"),sQuery(id+"F0.wireOp",EDGE,"E12.35.2"),sQuery(id+"F0.wireOp",EDGE,"E12.35.3"),sQuery(id+"F0.wireOp",EDGE,"E12.35.4"),sQuery(id+"F0.wireOp",EDGE,"E12.35.5"),sQuery(id+"F0.wireOp",EDGE,"E12.35.6"),sQuery(id+"F0.wireOp",EDGE,"E12.35.7"),sQuery(id+"F0.wireOp",EDGE,"E12.35.8"),sQuery(id+"F0.wireOp",EDGE,"E12.35.9"),sQuery(id+"F0.wireOp",EDGE,"E12.36.0"),sQuery(id+"F0.wireOp",EDGE,"E12.36.1"),sQuery(id+"F0.wireOp",EDGE,"E12.36.2"),sQuery(id+"F0.wireOp",EDGE,"E12.36.3"),sQuery(id+"F0.wireOp",EDGE,"E12.36.4"),sQuery(id+"F0.wireOp",EDGE,"E12.36.5"),sQuery(id+"F0.wireOp",EDGE,"E12.36.6"),sQuery(id+"F0.wireOp",EDGE,"E12.36.7"),sQuery(id+"F0.wireOp",EDGE,"E12.36.8"),sQuery(id+"F0.wireOp",EDGE,"E12.36.9"),sQuery(id+"F0.wireOp",EDGE,"E12.37.0"),sQuery(id+"F0.wireOp",EDGE,"E12.37.1"),sQuery(id+"F0.wireOp",EDGE,"E12.37.2"),sQuery(id+"F0.wireOp",EDGE,"E12.37.3"),sQuery(id+"F0.wireOp",EDGE,"E12.37.4"),sQuery(id+"F0.wireOp",EDGE,"E12.37.5"),sQuery(id+"F0.wireOp",EDGE,"E12.37.6"),sQuery(id+"F0.wireOp",EDGE,"E12.37.7"),sQuery(id+"F0.wireOp",EDGE,"E12.37.8"),sQuery(id+"F0.wireOp",EDGE,"E12.37.9"),sQuery(id+"F0.wireOp",EDGE,"E12.38.0"),sQuery(id+"F0.wireOp",EDGE,"E12.38.1"),sQuery(id+"F0.wireOp",EDGE,"E12.38.2"),sQuery(id+"F0.wireOp",EDGE,"E12.38.3"),sQuery(id+"F0.wireOp",EDGE,"E12.38.4"),sQuery(id+"F0.wireOp",EDGE,"E12.38.5"),sQuery(id+"F0.wireOp",EDGE,"E12.38.6"),sQuery(id+"F0.wireOp",EDGE,"E12.38.7"),sQuery(id+"F0.wireOp",EDGE,"E12.38.8"),sQuery(id+"F0.wireOp",EDGE,"E12.38.9"),sQuery(id+"F0.wireOp",EDGE,"E12.39.0"),sQuery(id+"F0.wireOp",EDGE,"E12.39.1"),sQuery(id+"F0.wireOp",EDGE,"E12.39.2"),sQuery(id+"F0.wireOp",EDGE,"E12.39.3"),sQuery(id+"F0.wireOp",EDGE,"E12.39.4"),sQuery(id+"F0.wireOp",EDGE,"E12.39.5"),sQuery(id+"F0.wireOp",EDGE,"E12.39.6"),sQuery(id+"F0.wireOp",EDGE,"E12.39.7"),sQuery(id+"F0.wireOp",EDGE,"E12.39.8"),sQuery(id+"F0.wireOp",EDGE,"E12.39.9"),sQuery(id+"F0.wireOp",EDGE,"E12.40.0"),sQuery(id+"F0.wireOp",EDGE,"E12.40.1"),sQuery(id+"F0.wireOp",EDGE,"E12.40.2"),sQuery(id+"F0.wireOp",EDGE,"E12.40.3"),sQuery(id+"F0.wireOp",EDGE,"E12.40.4"),sQuery(id+"F0.wireOp",EDGE,"E12.40.5"),sQuery(id+"F0.wireOp",EDGE,"E12.40.6"),sQuery(id+"F0.wireOp",EDGE,"E12.40.7"),sQuery(id+"F0.wireOp",EDGE,"E12.40.8"),sQuery(id+"F0.wireOp",EDGE,"E12.40.9"),sQuery(id+"F0.wireOp",EDGE,"E12.41.0"),sQuery(id+"F0.wireOp",EDGE,"E12.41.1"),sQuery(id+"F0.wireOp",EDGE,"E12.41.2"),sQuery(id+"F0.wireOp",EDGE,"E12.41.3"),sQuery(id+"F0.wireOp",EDGE,"E12.41.4"),sQuery(id+"F0.wireOp",EDGE,"E12.41.5"),sQuery(id+"F0.wireOp",EDGE,"E12.41.6"),sQuery(id+"F0.wireOp",EDGE,"E12.41.7"),sQuery(id+"F0.wireOp",EDGE,"E12.41.8"),sQuery(id+"F0.wireOp",EDGE,"E12.41.9"),sQuery(id+"F0.wireOp",EDGE,"E12.42.0"),sQuery(id+"F0.wireOp",EDGE,"E12.42.1"),sQuery(id+"F0.wireOp",EDGE,"E12.42.2"),sQuery(id+"F0.wireOp",EDGE,"E12.42.3"),sQuery(id+"F0.wireOp",EDGE,"E12.42.4"),sQuery(id+"F0.wireOp",EDGE,"E12.42.5"),sQuery(id+"F0.wireOp",EDGE,"E12.42.6"),sQuery(id+"F0.wireOp",EDGE,"E12.42.7"),sQuery(id+"F0.wireOp",EDGE,"E12.42.8"),sQuery(id+"F0.wireOp",EDGE,"E12.42.9"),sQuery(id+"F0.wireOp",EDGE,"E12.43.0"),sQuery(id+"F0.wireOp",EDGE,"E12.43.1"),sQuery(id+"F0.wireOp",EDGE,"E12.43.2"),sQuery(id+"F0.wireOp",EDGE,"E12.43.3"),sQuery(id+"F0.wireOp",EDGE,"E12.43.4"),sQuery(id+"F0.wireOp",EDGE,"E12.43.5"),sQuery(id+"F0.wireOp",EDGE,"E12.43.6"),sQuery(id+"F0.wireOp",EDGE,"E12.43.7"),sQuery(id+"F0.wireOp",EDGE,"E12.43.8"),sQuery(id+"F0.wireOp",EDGE,"E12.43.9"),sQuery(id+"F0.wireOp",EDGE,"E12.44.0"),sQuery(id+"F0.wireOp",EDGE,"E12.44.1"),sQuery(id+"F0.wireOp",EDGE,"E12.44.2"),sQuery(id+"F0.wireOp",EDGE,"E12.44.3"),sQuery(id+"F0.wireOp",EDGE,"E12.44.4"),sQuery(id+"F0.wireOp",EDGE,"E12.44.5"),sQuery(id+"F0.wireOp",EDGE,"E12.44.6"),sQuery(id+"F0.wireOp",EDGE,"E12.44.7"),sQuery(id+"F0.wireOp",EDGE,"E12.44.8"),sQuery(id+"F0.wireOp",EDGE,"E12.44.9"),sQuery(id+"F0.wireOp",EDGE,"E12.45.0"),sQuery(id+"F0.wireOp",EDGE,"E12.45.1"),sQuery(id+"F0.wireOp",EDGE,"E12.45.2"),sQuery(id+"F0.wireOp",EDGE,"E12.45.3"),sQuery(id+"F0.wireOp",EDGE,"E12.45.4"),sQuery(id+"F0.wireOp",EDGE,"E12.45.5"),sQuery(id+"F0.wireOp",EDGE,"E12.45.6"),sQuery(id+"F0.wireOp",EDGE,"E12.45.7"),sQuery(id+"F0.wireOp",EDGE,"E12.45.8"),sQuery(id+"F0.wireOp",EDGE,"E12.45.9"),sQuery(id+"F0.wireOp",EDGE,"E12.46.0"),sQuery(id+"F0.wireOp",EDGE,"E12.46.1"),sQuery(id+"F0.wireOp",EDGE,"E12.46.2"),sQuery(id+"F0.wireOp",EDGE,"E12.46.3"),sQuery(id+"F0.wireOp",EDGE,"E12.46.4"),sQuery(id+"F0.wireOp",EDGE,"E12.46.5"),sQuery(id+"F0.wireOp",EDGE,"E12.46.6"),sQuery(id+"F0.wireOp",EDGE,"E12.46.7"),sQuery(id+"F0.wireOp",EDGE,"E12.46.8"),sQuery(id+"F0.wireOp",EDGE,"E12.46.9"),sQuery(id+"F0.wireOp",EDGE,"E12.47.0"),sQuery(id+"F0.wireOp",EDGE,"E12.47.1"),sQuery(id+"F0.wireOp",EDGE,"E12.47.2"),sQuery(id+"F0.wireOp",EDGE,"E12.47.3"),sQuery(id+"F0.wireOp",EDGE,"E12.47.4"),sQuery(id+"F0.wireOp",EDGE,"E12.47.5"),sQuery(id+"F0.wireOp",EDGE,"E12.47.6"),sQuery(id+"F0.wireOp",EDGE,"E12.47.7"),sQuery(id+"F0.wireOp",EDGE,"E12.47.8"),sQuery(id+"F0.wireOp",EDGE,"E12.47.9"),sQuery(id+"F0.wireOp",EDGE,"E12.48.0"),sQuery(id+"F0.wireOp",EDGE,"E12.48.1"),sQuery(id+"F0.wireOp",EDGE,"E12.48.2"),sQuery(id+"F0.wireOp",EDGE,"E12.48.3"),sQuery(id+"F0.wireOp",EDGE,"E12.48.4"),sQuery(id+"F0.wireOp",EDGE,"E12.48.5"),sQuery(id+"F0.wireOp",EDGE,"E12.48.6"),sQuery(id+"F0.wireOp",EDGE,"E12.48.7"),sQuery(id+"F0.wireOp",EDGE,"E12.48.8"),sQuery(id+"F0.wireOp",EDGE,"E12.48.9"),sQuery(id+"F0.wireOp",EDGE,"E12.49.0"),sQuery(id+"F0.wireOp",EDGE,"E12.49.1"),sQuery(id+"F0.wireOp",EDGE,"E12.49.2"),sQuery(id+"F0.wireOp",EDGE,"E12.49.3"),sQuery(id+"F0.wireOp",EDGE,"E12.49.4"),sQuery(id+"F0.wireOp",EDGE,"E12.49.5"),sQuery(id+"F0.wireOp",EDGE,"E12.49.6"),sQuery(id+"F0.wireOp",EDGE,"E12.49.7"),sQuery(id+"F0.wireOp",EDGE,"E12.49.8"),sQuery(id+"F0.wireOp",EDGE,"E12.49.9"),sQuery(id+"F0.wireOp",EDGE,"E12.50.0"),sQuery(id+"F0.wireOp",EDGE,"E12.50.1"),sQuery(id+"F0.wireOp",EDGE,"E12.50.2"),sQuery(id+"F0.wireOp",EDGE,"E12.50.3"),sQuery(id+"F0.wireOp",EDGE,"E12.50.4"),sQuery(id+"F0.wireOp",EDGE,"E12.50.5"),sQuery(id+"F0.wireOp",EDGE,"E12.50.6"),sQuery(id+"F0.wireOp",EDGE,"E12.50.7"),sQuery(id+"F0.wireOp",EDGE,"E12.50.8"),sQuery(id+"F0.wireOp",EDGE,"E12.50.9"),sQuery(id+"F0.wireOp",EDGE,"E12.51.0"),sQuery(id+"F0.wireOp",EDGE,"E12.51.1"),sQuery(id+"F0.wireOp",EDGE,"E12.51.2"),sQuery(id+"F0.wireOp",EDGE,"E12.51.3"),sQuery(id+"F0.wireOp",EDGE,"E12.51.4"),sQuery(id+"F0.wireOp",EDGE,"E12.51.5"),sQuery(id+"F0.wireOp",EDGE,"E12.51.6"),sQuery(id+"F0.wireOp",EDGE,"E12.51.7"),sQuery(id+"F0.wireOp",EDGE,"E12.51.8"),sQuery(id+"F0.wireOp",EDGE,"E12.51.9"),sQuery(id+"F0.wireOp",EDGE,"E12.52.0"),sQuery(id+"F0.wireOp",EDGE,"E12.52.1"),sQuery(id+"F0.wireOp",EDGE,"E12.52.2"),sQuery(id+"F0.wireOp",EDGE,"E12.52.3"),sQuery(id+"F0.wireOp",EDGE,"E12.52.4"),sQuery(id+"F0.wireOp",EDGE,"E12.52.5"),sQuery(id+"F0.wireOp",EDGE,"E12.52.6"),sQuery(id+"F0.wireOp",EDGE,"E12.52.7"),sQuery(id+"F0.wireOp",EDGE,"E12.52.8"),sQuery(id+"F0.wireOp",EDGE,"E12.52.9"),sQuery(id+"F0.wireOp",EDGE,"E12.53.0"),sQuery(id+"F0.wireOp",EDGE,"E12.53.1"),sQuery(id+"F0.wireOp",EDGE,"E12.53.2"),sQuery(id+"F0.wireOp",EDGE,"E12.53.3"),sQuery(id+"F0.wireOp",EDGE,"E12.53.4"),sQuery(id+"F0.wireOp",EDGE,"E12.53.5"),sQuery(id+"F0.wireOp",EDGE,"E12.53.6"),sQuery(id+"F0.wireOp",EDGE,"E12.53.7"),sQuery(id+"F0.wireOp",EDGE,"E12.53.8"),sQuery(id+"F0.wireOp",EDGE,"E12.53.9"),sQuery(id+"F0.wireOp",EDGE,"E12.54.0"),sQuery(id+"F0.wireOp",EDGE,"E12.54.1"),sQuery(id+"F0.wireOp",EDGE,"E12.54.2"),sQuery(id+"F0.wireOp",EDGE,"E12.54.3"),sQuery(id+"F0.wireOp",EDGE,"E12.54.4"),sQuery(id+"F0.wireOp",EDGE,"E12.54.5"),sQuery(id+"F0.wireOp",EDGE,"E12.54.6"),sQuery(id+"F0.wireOp",EDGE,"E12.54.7"),sQuery(id+"F0.wireOp",EDGE,"E12.54.8"),sQuery(id+"F0.wireOp",EDGE,"E12.54.9"),sQuery(id+"F0.wireOp",EDGE,"E12.55.0"),sQuery(id+"F0.wireOp",EDGE,"E12.55.1"),sQuery(id+"F0.wireOp",EDGE,"E12.55.2"),sQuery(id+"F0.wireOp",EDGE,"E12.55.3"),sQuery(id+"F0.wireOp",EDGE,"E12.55.4"),sQuery(id+"F0.wireOp",EDGE,"E12.55.5"),sQuery(id+"F0.wireOp",EDGE,"E12.55.6"),sQuery(id+"F0.wireOp",EDGE,"E12.55.7"),sQuery(id+"F0.wireOp",EDGE,"E12.55.8"),sQuery(id+"F0.wireOp",EDGE,"E12.55.9"),sQuery(id+"F0.wireOp",EDGE,"E12.56.0"),sQuery(id+"F0.wireOp",EDGE,"E12.56.1"),sQuery(id+"F0.wireOp",EDGE,"E12.56.2"),sQuery(id+"F0.wireOp",EDGE,"E12.56.3"),sQuery(id+"F0.wireOp",EDGE,"E12.56.4"),sQuery(id+"F0.wireOp",EDGE,"E12.56.5"),sQuery(id+"F0.wireOp",EDGE,"E12.56.6"),sQuery(id+"F0.wireOp",EDGE,"E12.56.7"),sQuery(id+"F0.wireOp",EDGE,"E12.56.8"),sQuery(id+"F0.wireOp",EDGE,"E12.56.9"),sQuery(id+"F0.wireOp",EDGE,"E12.57.0"),sQuery(id+"F0.wireOp",EDGE,"E12.57.1"),sQuery(id+"F0.wireOp",EDGE,"E12.57.2"),sQuery(id+"F0.wireOp",EDGE,"E12.57.3"),sQuery(id+"F0.wireOp",EDGE,"E12.57.4"),sQuery(id+"F0.wireOp",EDGE,"E12.57.5"),sQuery(id+"F0.wireOp",EDGE,"E12.57.6"),sQuery(id+"F0.wireOp",EDGE,"E12.57.7"),sQuery(id+"F0.wireOp",EDGE,"E12.57.8"),sQuery(id+"F0.wireOp",EDGE,"E12.57.9"),sQuery(id+"F0.wireOp",EDGE,"E12.58.0"),sQuery(id+"F0.wireOp",EDGE,"E12.58.1"),sQuery(id+"F0.wireOp",EDGE,"E12.58.2"),sQuery(id+"F0.wireOp",EDGE,"E12.58.3"),sQuery(id+"F0.wireOp",EDGE,"E12.58.4"),sQuery(id+"F0.wireOp",EDGE,"E12.58.5"),sQuery(id+"F0.wireOp",EDGE,"E12.58.6"),sQuery(id+"F0.wireOp",EDGE,"E12.58.7"),sQuery(id+"F0.wireOp",EDGE,"E12.58.8"),sQuery(id+"F0.wireOp",EDGE,"E12.58.9"),sQuery(id+"F0.wireOp",EDGE,"E12.59.0"),sQuery(id+"F0.wireOp",EDGE,"E12.59.1"),sQuery(id+"F0.wireOp",EDGE,"E12.59.2"),sQuery(id+"F0.wireOp",EDGE,"E12.59.3"),sQuery(id+"F0.wireOp",EDGE,"E12.59.4"),sQuery(id+"F0.wireOp",EDGE,"E12.59.5"),sQuery(id+"F0.wireOp",EDGE,"E12.59.6"),sQuery(id+"F0.wireOp",EDGE,"E12.59.7"),sQuery(id+"F0.wireOp",EDGE,"E12.59.8"),sQuery(id+"F0.wireOp",EDGE,"E12.59.9"),sQuery(id+"F0.wireOp",EDGE,"E13.trimOffspring"),sQuery(id+"F0.wireOp",EDGE,"E14.trimOffspring")])],"isStart":true}),makeQuery(id+"F3.opExtrude","SWEPT_FACE",FACE,{"disambiguationData":[OSD([sQuery(id+"F2.wireOp",EDGE,"E17.6.0")])]})]});
            var Q13;
            Q13=makeQuery(id+"F3.boolean.opBoolean","INTERSECT",EDGE,{"derivedFrom":[makeQuery(id+"F1.opExtrude","CAP_FACE",FACE,{"disambiguationData":[OSD([sQuery(id+"F0.wireOp",EDGE,"E0"),sQuery(id+"F0.wireOp",EDGE,"E2"),sQuery(id+"F0.wireOp",EDGE,"E3"),sQuery(id+"F0.wireOp",EDGE,"E4.trimOffspring"),sQuery(id+"F0.wireOp",EDGE,"E5.MirrorCS"),sQuery(id+"F0.wireOp",EDGE,"E6.MirrorCS"),sQuery(id+"F0.wireOp",EDGE,"E7.MirrorCS"),sQuery(id+"F0.wireOp",EDGE,"E8.filletArc"),sQuery(id+"F0.wireOp",EDGE,"E9.filletArc"),sQuery(id+"F0.wireOp",EDGE,"E10.filletArc"),sQuery(id+"F0.wireOp",EDGE,"E11.filletArc"),sQuery(id+"F0.wireOp",EDGE,"E12.1.0"),sQuery(id+"F0.wireOp",EDGE,"E12.1.1"),sQuery(id+"F0.wireOp",EDGE,"E12.1.2"),sQuery(id+"F0.wireOp",EDGE,"E12.1.3"),sQuery(id+"F0.wireOp",EDGE,"E12.1.4"),sQuery(id+"F0.wireOp",EDGE,"E12.1.5"),sQuery(id+"F0.wireOp",EDGE,"E12.1.6"),sQuery(id+"F0.wireOp",EDGE,"E12.1.7"),sQuery(id+"F0.wireOp",EDGE,"E12.1.8"),sQuery(id+"F0.wireOp",EDGE,"E12.1.9"),sQuery(id+"F0.wireOp",EDGE,"E12.2.0"),sQuery(id+"F0.wireOp",EDGE,"E12.2.1"),sQuery(id+"F0.wireOp",EDGE,"E12.2.2"),sQuery(id+"F0.wireOp",EDGE,"E12.2.3"),sQuery(id+"F0.wireOp",EDGE,"E12.2.4"),sQuery(id+"F0.wireOp",EDGE,"E12.2.5"),sQuery(id+"F0.wireOp",EDGE,"E12.2.6"),sQuery(id+"F0.wireOp",EDGE,"E12.2.7"),sQuery(id+"F0.wireOp",EDGE,"E12.2.8"),sQuery(id+"F0.wireOp",EDGE,"E12.2.9"),sQuery(id+"F0.wireOp",EDGE,"E12.3.0"),sQuery(id+"F0.wireOp",EDGE,"E12.3.1"),sQuery(id+"F0.wireOp",EDGE,"E12.3.2"),sQuery(id+"F0.wireOp",EDGE,"E12.3.3"),sQuery(id+"F0.wireOp",EDGE,"E12.3.4"),sQuery(id+"F0.wireOp",EDGE,"E12.3.5"),sQuery(id+"F0.wireOp",EDGE,"E12.3.6"),sQuery(id+"F0.wireOp",EDGE,"E12.3.7"),sQuery(id+"F0.wireOp",EDGE,"E12.3.8"),sQuery(id+"F0.wireOp",EDGE,"E12.3.9"),sQuery(id+"F0.wireOp",EDGE,"E12.4.0"),sQuery(id+"F0.wireOp",EDGE,"E12.4.1"),sQuery(id+"F0.wireOp",EDGE,"E12.4.2"),sQuery(id+"F0.wireOp",EDGE,"E12.4.3"),sQuery(id+"F0.wireOp",EDGE,"E12.4.4"),sQuery(id+"F0.wireOp",EDGE,"E12.4.5"),sQuery(id+"F0.wireOp",EDGE,"E12.4.6"),sQuery(id+"F0.wireOp",EDGE,"E12.4.7"),sQuery(id+"F0.wireOp",EDGE,"E12.4.8"),sQuery(id+"F0.wireOp",EDGE,"E12.4.9"),sQuery(id+"F0.wireOp",EDGE,"E12.5.0"),sQuery(id+"F0.wireOp",EDGE,"E12.5.1"),sQuery(id+"F0.wireOp",EDGE,"E12.5.2"),sQuery(id+"F0.wireOp",EDGE,"E12.5.3"),sQuery(id+"F0.wireOp",EDGE,"E12.5.4"),sQuery(id+"F0.wireOp",EDGE,"E12.5.5"),sQuery(id+"F0.wireOp",EDGE,"E12.5.6"),sQuery(id+"F0.wireOp",EDGE,"E12.5.7"),sQuery(id+"F0.wireOp",EDGE,"E12.5.8"),sQuery(id+"F0.wireOp",EDGE,"E12.5.9"),sQuery(id+"F0.wireOp",EDGE,"E12.6.0"),sQuery(id+"F0.wireOp",EDGE,"E12.6.1"),sQuery(id+"F0.wireOp",EDGE,"E12.6.2"),sQuery(id+"F0.wireOp",EDGE,"E12.6.3"),sQuery(id+"F0.wireOp",EDGE,"E12.6.4"),sQuery(id+"F0.wireOp",EDGE,"E12.6.5"),sQuery(id+"F0.wireOp",EDGE,"E12.6.6"),sQuery(id+"F0.wireOp",EDGE,"E12.6.7"),sQuery(id+"F0.wireOp",EDGE,"E12.6.8"),sQuery(id+"F0.wireOp",EDGE,"E12.6.9"),sQuery(id+"F0.wireOp",EDGE,"E12.7.0"),sQuery(id+"F0.wireOp",EDGE,"E12.7.1"),sQuery(id+"F0.wireOp",EDGE,"E12.7.2"),sQuery(id+"F0.wireOp",EDGE,"E12.7.3"),sQuery(id+"F0.wireOp",EDGE,"E12.7.4"),sQuery(id+"F0.wireOp",EDGE,"E12.7.5"),sQuery(id+"F0.wireOp",EDGE,"E12.7.6"),sQuery(id+"F0.wireOp",EDGE,"E12.7.7"),sQuery(id+"F0.wireOp",EDGE,"E12.7.8"),sQuery(id+"F0.wireOp",EDGE,"E12.7.9"),sQuery(id+"F0.wireOp",EDGE,"E12.8.0"),sQuery(id+"F0.wireOp",EDGE,"E12.8.1"),sQuery(id+"F0.wireOp",EDGE,"E12.8.2"),sQuery(id+"F0.wireOp",EDGE,"E12.8.3"),sQuery(id+"F0.wireOp",EDGE,"E12.8.4"),sQuery(id+"F0.wireOp",EDGE,"E12.8.5"),sQuery(id+"F0.wireOp",EDGE,"E12.8.6"),sQuery(id+"F0.wireOp",EDGE,"E12.8.7"),sQuery(id+"F0.wireOp",EDGE,"E12.8.8"),sQuery(id+"F0.wireOp",EDGE,"E12.8.9"),sQuery(id+"F0.wireOp",EDGE,"E12.9.0"),sQuery(id+"F0.wireOp",EDGE,"E12.9.1"),sQuery(id+"F0.wireOp",EDGE,"E12.9.2"),sQuery(id+"F0.wireOp",EDGE,"E12.9.3"),sQuery(id+"F0.wireOp",EDGE,"E12.9.4"),sQuery(id+"F0.wireOp",EDGE,"E12.9.5"),sQuery(id+"F0.wireOp",EDGE,"E12.9.6"),sQuery(id+"F0.wireOp",EDGE,"E12.9.7"),sQuery(id+"F0.wireOp",EDGE,"E12.9.8"),sQuery(id+"F0.wireOp",EDGE,"E12.9.9"),sQuery(id+"F0.wireOp",EDGE,"E12.10.0"),sQuery(id+"F0.wireOp",EDGE,"E12.10.1"),sQuery(id+"F0.wireOp",EDGE,"E12.10.2"),sQuery(id+"F0.wireOp",EDGE,"E12.10.3"),sQuery(id+"F0.wireOp",EDGE,"E12.10.4"),sQuery(id+"F0.wireOp",EDGE,"E12.10.5"),sQuery(id+"F0.wireOp",EDGE,"E12.10.6"),sQuery(id+"F0.wireOp",EDGE,"E12.10.7"),sQuery(id+"F0.wireOp",EDGE,"E12.10.8"),sQuery(id+"F0.wireOp",EDGE,"E12.10.9"),sQuery(id+"F0.wireOp",EDGE,"E12.11.0"),sQuery(id+"F0.wireOp",EDGE,"E12.11.1"),sQuery(id+"F0.wireOp",EDGE,"E12.11.2"),sQuery(id+"F0.wireOp",EDGE,"E12.11.3"),sQuery(id+"F0.wireOp",EDGE,"E12.11.4"),sQuery(id+"F0.wireOp",EDGE,"E12.11.5"),sQuery(id+"F0.wireOp",EDGE,"E12.11.6"),sQuery(id+"F0.wireOp",EDGE,"E12.11.7"),sQuery(id+"F0.wireOp",EDGE,"E12.11.8"),sQuery(id+"F0.wireOp",EDGE,"E12.11.9"),sQuery(id+"F0.wireOp",EDGE,"E12.12.0"),sQuery(id+"F0.wireOp",EDGE,"E12.12.1"),sQuery(id+"F0.wireOp",EDGE,"E12.12.2"),sQuery(id+"F0.wireOp",EDGE,"E12.12.3"),sQuery(id+"F0.wireOp",EDGE,"E12.12.4"),sQuery(id+"F0.wireOp",EDGE,"E12.12.5"),sQuery(id+"F0.wireOp",EDGE,"E12.12.6"),sQuery(id+"F0.wireOp",EDGE,"E12.12.7"),sQuery(id+"F0.wireOp",EDGE,"E12.12.8"),sQuery(id+"F0.wireOp",EDGE,"E12.12.9"),sQuery(id+"F0.wireOp",EDGE,"E12.13.0"),sQuery(id+"F0.wireOp",EDGE,"E12.13.1"),sQuery(id+"F0.wireOp",EDGE,"E12.13.2"),sQuery(id+"F0.wireOp",EDGE,"E12.13.3"),sQuery(id+"F0.wireOp",EDGE,"E12.13.4"),sQuery(id+"F0.wireOp",EDGE,"E12.13.5"),sQuery(id+"F0.wireOp",EDGE,"E12.13.6"),sQuery(id+"F0.wireOp",EDGE,"E12.13.7"),sQuery(id+"F0.wireOp",EDGE,"E12.13.8"),sQuery(id+"F0.wireOp",EDGE,"E12.13.9"),sQuery(id+"F0.wireOp",EDGE,"E12.14.0"),sQuery(id+"F0.wireOp",EDGE,"E12.14.1"),sQuery(id+"F0.wireOp",EDGE,"E12.14.2"),sQuery(id+"F0.wireOp",EDGE,"E12.14.3"),sQuery(id+"F0.wireOp",EDGE,"E12.14.4"),sQuery(id+"F0.wireOp",EDGE,"E12.14.5"),sQuery(id+"F0.wireOp",EDGE,"E12.14.6"),sQuery(id+"F0.wireOp",EDGE,"E12.14.7"),sQuery(id+"F0.wireOp",EDGE,"E12.14.8"),sQuery(id+"F0.wireOp",EDGE,"E12.14.9"),sQuery(id+"F0.wireOp",EDGE,"E12.15.0"),sQuery(id+"F0.wireOp",EDGE,"E12.15.1"),sQuery(id+"F0.wireOp",EDGE,"E12.15.2"),sQuery(id+"F0.wireOp",EDGE,"E12.15.3"),sQuery(id+"F0.wireOp",EDGE,"E12.15.4"),sQuery(id+"F0.wireOp",EDGE,"E12.15.5"),sQuery(id+"F0.wireOp",EDGE,"E12.15.6"),sQuery(id+"F0.wireOp",EDGE,"E12.15.7"),sQuery(id+"F0.wireOp",EDGE,"E12.15.8"),sQuery(id+"F0.wireOp",EDGE,"E12.15.9"),sQuery(id+"F0.wireOp",EDGE,"E12.16.0"),sQuery(id+"F0.wireOp",EDGE,"E12.16.1"),sQuery(id+"F0.wireOp",EDGE,"E12.16.2"),sQuery(id+"F0.wireOp",EDGE,"E12.16.3"),sQuery(id+"F0.wireOp",EDGE,"E12.16.4"),sQuery(id+"F0.wireOp",EDGE,"E12.16.5"),sQuery(id+"F0.wireOp",EDGE,"E12.16.6"),sQuery(id+"F0.wireOp",EDGE,"E12.16.7"),sQuery(id+"F0.wireOp",EDGE,"E12.16.8"),sQuery(id+"F0.wireOp",EDGE,"E12.16.9"),sQuery(id+"F0.wireOp",EDGE,"E12.17.0"),sQuery(id+"F0.wireOp",EDGE,"E12.17.1"),sQuery(id+"F0.wireOp",EDGE,"E12.17.2"),sQuery(id+"F0.wireOp",EDGE,"E12.17.3"),sQuery(id+"F0.wireOp",EDGE,"E12.17.4"),sQuery(id+"F0.wireOp",EDGE,"E12.17.5"),sQuery(id+"F0.wireOp",EDGE,"E12.17.6"),sQuery(id+"F0.wireOp",EDGE,"E12.17.7"),sQuery(id+"F0.wireOp",EDGE,"E12.17.8"),sQuery(id+"F0.wireOp",EDGE,"E12.17.9"),sQuery(id+"F0.wireOp",EDGE,"E12.18.0"),sQuery(id+"F0.wireOp",EDGE,"E12.18.1"),sQuery(id+"F0.wireOp",EDGE,"E12.18.2"),sQuery(id+"F0.wireOp",EDGE,"E12.18.3"),sQuery(id+"F0.wireOp",EDGE,"E12.18.4"),sQuery(id+"F0.wireOp",EDGE,"E12.18.5"),sQuery(id+"F0.wireOp",EDGE,"E12.18.6"),sQuery(id+"F0.wireOp",EDGE,"E12.18.7"),sQuery(id+"F0.wireOp",EDGE,"E12.18.8"),sQuery(id+"F0.wireOp",EDGE,"E12.18.9"),sQuery(id+"F0.wireOp",EDGE,"E12.19.0"),sQuery(id+"F0.wireOp",EDGE,"E12.19.1"),sQuery(id+"F0.wireOp",EDGE,"E12.19.2"),sQuery(id+"F0.wireOp",EDGE,"E12.19.3"),sQuery(id+"F0.wireOp",EDGE,"E12.19.4"),sQuery(id+"F0.wireOp",EDGE,"E12.19.5"),sQuery(id+"F0.wireOp",EDGE,"E12.19.6"),sQuery(id+"F0.wireOp",EDGE,"E12.19.7"),sQuery(id+"F0.wireOp",EDGE,"E12.19.8"),sQuery(id+"F0.wireOp",EDGE,"E12.19.9"),sQuery(id+"F0.wireOp",EDGE,"E12.20.0"),sQuery(id+"F0.wireOp",EDGE,"E12.20.1"),sQuery(id+"F0.wireOp",EDGE,"E12.20.2"),sQuery(id+"F0.wireOp",EDGE,"E12.20.3"),sQuery(id+"F0.wireOp",EDGE,"E12.20.4"),sQuery(id+"F0.wireOp",EDGE,"E12.20.5"),sQuery(id+"F0.wireOp",EDGE,"E12.20.6"),sQuery(id+"F0.wireOp",EDGE,"E12.20.7"),sQuery(id+"F0.wireOp",EDGE,"E12.20.8"),sQuery(id+"F0.wireOp",EDGE,"E12.20.9"),sQuery(id+"F0.wireOp",EDGE,"E12.21.0"),sQuery(id+"F0.wireOp",EDGE,"E12.21.1"),sQuery(id+"F0.wireOp",EDGE,"E12.21.2"),sQuery(id+"F0.wireOp",EDGE,"E12.21.3"),sQuery(id+"F0.wireOp",EDGE,"E12.21.4"),sQuery(id+"F0.wireOp",EDGE,"E12.21.5"),sQuery(id+"F0.wireOp",EDGE,"E12.21.6"),sQuery(id+"F0.wireOp",EDGE,"E12.21.7"),sQuery(id+"F0.wireOp",EDGE,"E12.21.8"),sQuery(id+"F0.wireOp",EDGE,"E12.21.9"),sQuery(id+"F0.wireOp",EDGE,"E12.22.0"),sQuery(id+"F0.wireOp",EDGE,"E12.22.1"),sQuery(id+"F0.wireOp",EDGE,"E12.22.2"),sQuery(id+"F0.wireOp",EDGE,"E12.22.3"),sQuery(id+"F0.wireOp",EDGE,"E12.22.4"),sQuery(id+"F0.wireOp",EDGE,"E12.22.5"),sQuery(id+"F0.wireOp",EDGE,"E12.22.6"),sQuery(id+"F0.wireOp",EDGE,"E12.22.7"),sQuery(id+"F0.wireOp",EDGE,"E12.22.8"),sQuery(id+"F0.wireOp",EDGE,"E12.22.9"),sQuery(id+"F0.wireOp",EDGE,"E12.23.0"),sQuery(id+"F0.wireOp",EDGE,"E12.23.1"),sQuery(id+"F0.wireOp",EDGE,"E12.23.2"),sQuery(id+"F0.wireOp",EDGE,"E12.23.3"),sQuery(id+"F0.wireOp",EDGE,"E12.23.4"),sQuery(id+"F0.wireOp",EDGE,"E12.23.5"),sQuery(id+"F0.wireOp",EDGE,"E12.23.6"),sQuery(id+"F0.wireOp",EDGE,"E12.23.7"),sQuery(id+"F0.wireOp",EDGE,"E12.23.8"),sQuery(id+"F0.wireOp",EDGE,"E12.23.9"),sQuery(id+"F0.wireOp",EDGE,"E12.24.0"),sQuery(id+"F0.wireOp",EDGE,"E12.24.1"),sQuery(id+"F0.wireOp",EDGE,"E12.24.2"),sQuery(id+"F0.wireOp",EDGE,"E12.24.3"),sQuery(id+"F0.wireOp",EDGE,"E12.24.4"),sQuery(id+"F0.wireOp",EDGE,"E12.24.5"),sQuery(id+"F0.wireOp",EDGE,"E12.24.6"),sQuery(id+"F0.wireOp",EDGE,"E12.24.7"),sQuery(id+"F0.wireOp",EDGE,"E12.24.8"),sQuery(id+"F0.wireOp",EDGE,"E12.24.9"),sQuery(id+"F0.wireOp",EDGE,"E12.25.0"),sQuery(id+"F0.wireOp",EDGE,"E12.25.1"),sQuery(id+"F0.wireOp",EDGE,"E12.25.2"),sQuery(id+"F0.wireOp",EDGE,"E12.25.3"),sQuery(id+"F0.wireOp",EDGE,"E12.25.4"),sQuery(id+"F0.wireOp",EDGE,"E12.25.5"),sQuery(id+"F0.wireOp",EDGE,"E12.25.6"),sQuery(id+"F0.wireOp",EDGE,"E12.25.7"),sQuery(id+"F0.wireOp",EDGE,"E12.25.8"),sQuery(id+"F0.wireOp",EDGE,"E12.25.9"),sQuery(id+"F0.wireOp",EDGE,"E12.26.0"),sQuery(id+"F0.wireOp",EDGE,"E12.26.1"),sQuery(id+"F0.wireOp",EDGE,"E12.26.2"),sQuery(id+"F0.wireOp",EDGE,"E12.26.3"),sQuery(id+"F0.wireOp",EDGE,"E12.26.4"),sQuery(id+"F0.wireOp",EDGE,"E12.26.5"),sQuery(id+"F0.wireOp",EDGE,"E12.26.6"),sQuery(id+"F0.wireOp",EDGE,"E12.26.7"),sQuery(id+"F0.wireOp",EDGE,"E12.26.8"),sQuery(id+"F0.wireOp",EDGE,"E12.26.9"),sQuery(id+"F0.wireOp",EDGE,"E12.27.0"),sQuery(id+"F0.wireOp",EDGE,"E12.27.1"),sQuery(id+"F0.wireOp",EDGE,"E12.27.2"),sQuery(id+"F0.wireOp",EDGE,"E12.27.3"),sQuery(id+"F0.wireOp",EDGE,"E12.27.4"),sQuery(id+"F0.wireOp",EDGE,"E12.27.5"),sQuery(id+"F0.wireOp",EDGE,"E12.27.6"),sQuery(id+"F0.wireOp",EDGE,"E12.27.7"),sQuery(id+"F0.wireOp",EDGE,"E12.27.8"),sQuery(id+"F0.wireOp",EDGE,"E12.27.9"),sQuery(id+"F0.wireOp",EDGE,"E12.28.0"),sQuery(id+"F0.wireOp",EDGE,"E12.28.1"),sQuery(id+"F0.wireOp",EDGE,"E12.28.2"),sQuery(id+"F0.wireOp",EDGE,"E12.28.3"),sQuery(id+"F0.wireOp",EDGE,"E12.28.4"),sQuery(id+"F0.wireOp",EDGE,"E12.28.5"),sQuery(id+"F0.wireOp",EDGE,"E12.28.6"),sQuery(id+"F0.wireOp",EDGE,"E12.28.7"),sQuery(id+"F0.wireOp",EDGE,"E12.28.8"),sQuery(id+"F0.wireOp",EDGE,"E12.28.9"),sQuery(id+"F0.wireOp",EDGE,"E12.29.0"),sQuery(id+"F0.wireOp",EDGE,"E12.29.1"),sQuery(id+"F0.wireOp",EDGE,"E12.29.2"),sQuery(id+"F0.wireOp",EDGE,"E12.29.3"),sQuery(id+"F0.wireOp",EDGE,"E12.29.4"),sQuery(id+"F0.wireOp",EDGE,"E12.29.5"),sQuery(id+"F0.wireOp",EDGE,"E12.29.6"),sQuery(id+"F0.wireOp",EDGE,"E12.29.7"),sQuery(id+"F0.wireOp",EDGE,"E12.29.8"),sQuery(id+"F0.wireOp",EDGE,"E12.29.9"),sQuery(id+"F0.wireOp",EDGE,"E12.30.0"),sQuery(id+"F0.wireOp",EDGE,"E12.30.1"),sQuery(id+"F0.wireOp",EDGE,"E12.30.2"),sQuery(id+"F0.wireOp",EDGE,"E12.30.3"),sQuery(id+"F0.wireOp",EDGE,"E12.30.4"),sQuery(id+"F0.wireOp",EDGE,"E12.30.5"),sQuery(id+"F0.wireOp",EDGE,"E12.30.6"),sQuery(id+"F0.wireOp",EDGE,"E12.30.7"),sQuery(id+"F0.wireOp",EDGE,"E12.30.8"),sQuery(id+"F0.wireOp",EDGE,"E12.30.9"),sQuery(id+"F0.wireOp",EDGE,"E12.31.0"),sQuery(id+"F0.wireOp",EDGE,"E12.31.1"),sQuery(id+"F0.wireOp",EDGE,"E12.31.2"),sQuery(id+"F0.wireOp",EDGE,"E12.31.3"),sQuery(id+"F0.wireOp",EDGE,"E12.31.4"),sQuery(id+"F0.wireOp",EDGE,"E12.31.5"),sQuery(id+"F0.wireOp",EDGE,"E12.31.6"),sQuery(id+"F0.wireOp",EDGE,"E12.31.7"),sQuery(id+"F0.wireOp",EDGE,"E12.31.8"),sQuery(id+"F0.wireOp",EDGE,"E12.31.9"),sQuery(id+"F0.wireOp",EDGE,"E12.32.0"),sQuery(id+"F0.wireOp",EDGE,"E12.32.1"),sQuery(id+"F0.wireOp",EDGE,"E12.32.2"),sQuery(id+"F0.wireOp",EDGE,"E12.32.3"),sQuery(id+"F0.wireOp",EDGE,"E12.32.4"),sQuery(id+"F0.wireOp",EDGE,"E12.32.5"),sQuery(id+"F0.wireOp",EDGE,"E12.32.6"),sQuery(id+"F0.wireOp",EDGE,"E12.32.7"),sQuery(id+"F0.wireOp",EDGE,"E12.32.8"),sQuery(id+"F0.wireOp",EDGE,"E12.32.9"),sQuery(id+"F0.wireOp",EDGE,"E12.33.0"),sQuery(id+"F0.wireOp",EDGE,"E12.33.1"),sQuery(id+"F0.wireOp",EDGE,"E12.33.2"),sQuery(id+"F0.wireOp",EDGE,"E12.33.3"),sQuery(id+"F0.wireOp",EDGE,"E12.33.4"),sQuery(id+"F0.wireOp",EDGE,"E12.33.5"),sQuery(id+"F0.wireOp",EDGE,"E12.33.6"),sQuery(id+"F0.wireOp",EDGE,"E12.33.7"),sQuery(id+"F0.wireOp",EDGE,"E12.33.8"),sQuery(id+"F0.wireOp",EDGE,"E12.33.9"),sQuery(id+"F0.wireOp",EDGE,"E12.34.0"),sQuery(id+"F0.wireOp",EDGE,"E12.34.1"),sQuery(id+"F0.wireOp",EDGE,"E12.34.2"),sQuery(id+"F0.wireOp",EDGE,"E12.34.3"),sQuery(id+"F0.wireOp",EDGE,"E12.34.4"),sQuery(id+"F0.wireOp",EDGE,"E12.34.5"),sQuery(id+"F0.wireOp",EDGE,"E12.34.6"),sQuery(id+"F0.wireOp",EDGE,"E12.34.7"),sQuery(id+"F0.wireOp",EDGE,"E12.34.8"),sQuery(id+"F0.wireOp",EDGE,"E12.34.9"),sQuery(id+"F0.wireOp",EDGE,"E12.35.0"),sQuery(id+"F0.wireOp",EDGE,"E12.35.1"),sQuery(id+"F0.wireOp",EDGE,"E12.35.2"),sQuery(id+"F0.wireOp",EDGE,"E12.35.3"),sQuery(id+"F0.wireOp",EDGE,"E12.35.4"),sQuery(id+"F0.wireOp",EDGE,"E12.35.5"),sQuery(id+"F0.wireOp",EDGE,"E12.35.6"),sQuery(id+"F0.wireOp",EDGE,"E12.35.7"),sQuery(id+"F0.wireOp",EDGE,"E12.35.8"),sQuery(id+"F0.wireOp",EDGE,"E12.35.9"),sQuery(id+"F0.wireOp",EDGE,"E12.36.0"),sQuery(id+"F0.wireOp",EDGE,"E12.36.1"),sQuery(id+"F0.wireOp",EDGE,"E12.36.2"),sQuery(id+"F0.wireOp",EDGE,"E12.36.3"),sQuery(id+"F0.wireOp",EDGE,"E12.36.4"),sQuery(id+"F0.wireOp",EDGE,"E12.36.5"),sQuery(id+"F0.wireOp",EDGE,"E12.36.6"),sQuery(id+"F0.wireOp",EDGE,"E12.36.7"),sQuery(id+"F0.wireOp",EDGE,"E12.36.8"),sQuery(id+"F0.wireOp",EDGE,"E12.36.9"),sQuery(id+"F0.wireOp",EDGE,"E12.37.0"),sQuery(id+"F0.wireOp",EDGE,"E12.37.1"),sQuery(id+"F0.wireOp",EDGE,"E12.37.2"),sQuery(id+"F0.wireOp",EDGE,"E12.37.3"),sQuery(id+"F0.wireOp",EDGE,"E12.37.4"),sQuery(id+"F0.wireOp",EDGE,"E12.37.5"),sQuery(id+"F0.wireOp",EDGE,"E12.37.6"),sQuery(id+"F0.wireOp",EDGE,"E12.37.7"),sQuery(id+"F0.wireOp",EDGE,"E12.37.8"),sQuery(id+"F0.wireOp",EDGE,"E12.37.9"),sQuery(id+"F0.wireOp",EDGE,"E12.38.0"),sQuery(id+"F0.wireOp",EDGE,"E12.38.1"),sQuery(id+"F0.wireOp",EDGE,"E12.38.2"),sQuery(id+"F0.wireOp",EDGE,"E12.38.3"),sQuery(id+"F0.wireOp",EDGE,"E12.38.4"),sQuery(id+"F0.wireOp",EDGE,"E12.38.5"),sQuery(id+"F0.wireOp",EDGE,"E12.38.6"),sQuery(id+"F0.wireOp",EDGE,"E12.38.7"),sQuery(id+"F0.wireOp",EDGE,"E12.38.8"),sQuery(id+"F0.wireOp",EDGE,"E12.38.9"),sQuery(id+"F0.wireOp",EDGE,"E12.39.0"),sQuery(id+"F0.wireOp",EDGE,"E12.39.1"),sQuery(id+"F0.wireOp",EDGE,"E12.39.2"),sQuery(id+"F0.wireOp",EDGE,"E12.39.3"),sQuery(id+"F0.wireOp",EDGE,"E12.39.4"),sQuery(id+"F0.wireOp",EDGE,"E12.39.5"),sQuery(id+"F0.wireOp",EDGE,"E12.39.6"),sQuery(id+"F0.wireOp",EDGE,"E12.39.7"),sQuery(id+"F0.wireOp",EDGE,"E12.39.8"),sQuery(id+"F0.wireOp",EDGE,"E12.39.9"),sQuery(id+"F0.wireOp",EDGE,"E12.40.0"),sQuery(id+"F0.wireOp",EDGE,"E12.40.1"),sQuery(id+"F0.wireOp",EDGE,"E12.40.2"),sQuery(id+"F0.wireOp",EDGE,"E12.40.3"),sQuery(id+"F0.wireOp",EDGE,"E12.40.4"),sQuery(id+"F0.wireOp",EDGE,"E12.40.5"),sQuery(id+"F0.wireOp",EDGE,"E12.40.6"),sQuery(id+"F0.wireOp",EDGE,"E12.40.7"),sQuery(id+"F0.wireOp",EDGE,"E12.40.8"),sQuery(id+"F0.wireOp",EDGE,"E12.40.9"),sQuery(id+"F0.wireOp",EDGE,"E12.41.0"),sQuery(id+"F0.wireOp",EDGE,"E12.41.1"),sQuery(id+"F0.wireOp",EDGE,"E12.41.2"),sQuery(id+"F0.wireOp",EDGE,"E12.41.3"),sQuery(id+"F0.wireOp",EDGE,"E12.41.4"),sQuery(id+"F0.wireOp",EDGE,"E12.41.5"),sQuery(id+"F0.wireOp",EDGE,"E12.41.6"),sQuery(id+"F0.wireOp",EDGE,"E12.41.7"),sQuery(id+"F0.wireOp",EDGE,"E12.41.8"),sQuery(id+"F0.wireOp",EDGE,"E12.41.9"),sQuery(id+"F0.wireOp",EDGE,"E12.42.0"),sQuery(id+"F0.wireOp",EDGE,"E12.42.1"),sQuery(id+"F0.wireOp",EDGE,"E12.42.2"),sQuery(id+"F0.wireOp",EDGE,"E12.42.3"),sQuery(id+"F0.wireOp",EDGE,"E12.42.4"),sQuery(id+"F0.wireOp",EDGE,"E12.42.5"),sQuery(id+"F0.wireOp",EDGE,"E12.42.6"),sQuery(id+"F0.wireOp",EDGE,"E12.42.7"),sQuery(id+"F0.wireOp",EDGE,"E12.42.8"),sQuery(id+"F0.wireOp",EDGE,"E12.42.9"),sQuery(id+"F0.wireOp",EDGE,"E12.43.0"),sQuery(id+"F0.wireOp",EDGE,"E12.43.1"),sQuery(id+"F0.wireOp",EDGE,"E12.43.2"),sQuery(id+"F0.wireOp",EDGE,"E12.43.3"),sQuery(id+"F0.wireOp",EDGE,"E12.43.4"),sQuery(id+"F0.wireOp",EDGE,"E12.43.5"),sQuery(id+"F0.wireOp",EDGE,"E12.43.6"),sQuery(id+"F0.wireOp",EDGE,"E12.43.7"),sQuery(id+"F0.wireOp",EDGE,"E12.43.8"),sQuery(id+"F0.wireOp",EDGE,"E12.43.9"),sQuery(id+"F0.wireOp",EDGE,"E12.44.0"),sQuery(id+"F0.wireOp",EDGE,"E12.44.1"),sQuery(id+"F0.wireOp",EDGE,"E12.44.2"),sQuery(id+"F0.wireOp",EDGE,"E12.44.3"),sQuery(id+"F0.wireOp",EDGE,"E12.44.4"),sQuery(id+"F0.wireOp",EDGE,"E12.44.5"),sQuery(id+"F0.wireOp",EDGE,"E12.44.6"),sQuery(id+"F0.wireOp",EDGE,"E12.44.7"),sQuery(id+"F0.wireOp",EDGE,"E12.44.8"),sQuery(id+"F0.wireOp",EDGE,"E12.44.9"),sQuery(id+"F0.wireOp",EDGE,"E12.45.0"),sQuery(id+"F0.wireOp",EDGE,"E12.45.1"),sQuery(id+"F0.wireOp",EDGE,"E12.45.2"),sQuery(id+"F0.wireOp",EDGE,"E12.45.3"),sQuery(id+"F0.wireOp",EDGE,"E12.45.4"),sQuery(id+"F0.wireOp",EDGE,"E12.45.5"),sQuery(id+"F0.wireOp",EDGE,"E12.45.6"),sQuery(id+"F0.wireOp",EDGE,"E12.45.7"),sQuery(id+"F0.wireOp",EDGE,"E12.45.8"),sQuery(id+"F0.wireOp",EDGE,"E12.45.9"),sQuery(id+"F0.wireOp",EDGE,"E12.46.0"),sQuery(id+"F0.wireOp",EDGE,"E12.46.1"),sQuery(id+"F0.wireOp",EDGE,"E12.46.2"),sQuery(id+"F0.wireOp",EDGE,"E12.46.3"),sQuery(id+"F0.wireOp",EDGE,"E12.46.4"),sQuery(id+"F0.wireOp",EDGE,"E12.46.5"),sQuery(id+"F0.wireOp",EDGE,"E12.46.6"),sQuery(id+"F0.wireOp",EDGE,"E12.46.7"),sQuery(id+"F0.wireOp",EDGE,"E12.46.8"),sQuery(id+"F0.wireOp",EDGE,"E12.46.9"),sQuery(id+"F0.wireOp",EDGE,"E12.47.0"),sQuery(id+"F0.wireOp",EDGE,"E12.47.1"),sQuery(id+"F0.wireOp",EDGE,"E12.47.2"),sQuery(id+"F0.wireOp",EDGE,"E12.47.3"),sQuery(id+"F0.wireOp",EDGE,"E12.47.4"),sQuery(id+"F0.wireOp",EDGE,"E12.47.5"),sQuery(id+"F0.wireOp",EDGE,"E12.47.6"),sQuery(id+"F0.wireOp",EDGE,"E12.47.7"),sQuery(id+"F0.wireOp",EDGE,"E12.47.8"),sQuery(id+"F0.wireOp",EDGE,"E12.47.9"),sQuery(id+"F0.wireOp",EDGE,"E12.48.0"),sQuery(id+"F0.wireOp",EDGE,"E12.48.1"),sQuery(id+"F0.wireOp",EDGE,"E12.48.2"),sQuery(id+"F0.wireOp",EDGE,"E12.48.3"),sQuery(id+"F0.wireOp",EDGE,"E12.48.4"),sQuery(id+"F0.wireOp",EDGE,"E12.48.5"),sQuery(id+"F0.wireOp",EDGE,"E12.48.6"),sQuery(id+"F0.wireOp",EDGE,"E12.48.7"),sQuery(id+"F0.wireOp",EDGE,"E12.48.8"),sQuery(id+"F0.wireOp",EDGE,"E12.48.9"),sQuery(id+"F0.wireOp",EDGE,"E12.49.0"),sQuery(id+"F0.wireOp",EDGE,"E12.49.1"),sQuery(id+"F0.wireOp",EDGE,"E12.49.2"),sQuery(id+"F0.wireOp",EDGE,"E12.49.3"),sQuery(id+"F0.wireOp",EDGE,"E12.49.4"),sQuery(id+"F0.wireOp",EDGE,"E12.49.5"),sQuery(id+"F0.wireOp",EDGE,"E12.49.6"),sQuery(id+"F0.wireOp",EDGE,"E12.49.7"),sQuery(id+"F0.wireOp",EDGE,"E12.49.8"),sQuery(id+"F0.wireOp",EDGE,"E12.49.9"),sQuery(id+"F0.wireOp",EDGE,"E12.50.0"),sQuery(id+"F0.wireOp",EDGE,"E12.50.1"),sQuery(id+"F0.wireOp",EDGE,"E12.50.2"),sQuery(id+"F0.wireOp",EDGE,"E12.50.3"),sQuery(id+"F0.wireOp",EDGE,"E12.50.4"),sQuery(id+"F0.wireOp",EDGE,"E12.50.5"),sQuery(id+"F0.wireOp",EDGE,"E12.50.6"),sQuery(id+"F0.wireOp",EDGE,"E12.50.7"),sQuery(id+"F0.wireOp",EDGE,"E12.50.8"),sQuery(id+"F0.wireOp",EDGE,"E12.50.9"),sQuery(id+"F0.wireOp",EDGE,"E12.51.0"),sQuery(id+"F0.wireOp",EDGE,"E12.51.1"),sQuery(id+"F0.wireOp",EDGE,"E12.51.2"),sQuery(id+"F0.wireOp",EDGE,"E12.51.3"),sQuery(id+"F0.wireOp",EDGE,"E12.51.4"),sQuery(id+"F0.wireOp",EDGE,"E12.51.5"),sQuery(id+"F0.wireOp",EDGE,"E12.51.6"),sQuery(id+"F0.wireOp",EDGE,"E12.51.7"),sQuery(id+"F0.wireOp",EDGE,"E12.51.8"),sQuery(id+"F0.wireOp",EDGE,"E12.51.9"),sQuery(id+"F0.wireOp",EDGE,"E12.52.0"),sQuery(id+"F0.wireOp",EDGE,"E12.52.1"),sQuery(id+"F0.wireOp",EDGE,"E12.52.2"),sQuery(id+"F0.wireOp",EDGE,"E12.52.3"),sQuery(id+"F0.wireOp",EDGE,"E12.52.4"),sQuery(id+"F0.wireOp",EDGE,"E12.52.5"),sQuery(id+"F0.wireOp",EDGE,"E12.52.6"),sQuery(id+"F0.wireOp",EDGE,"E12.52.7"),sQuery(id+"F0.wireOp",EDGE,"E12.52.8"),sQuery(id+"F0.wireOp",EDGE,"E12.52.9"),sQuery(id+"F0.wireOp",EDGE,"E12.53.0"),sQuery(id+"F0.wireOp",EDGE,"E12.53.1"),sQuery(id+"F0.wireOp",EDGE,"E12.53.2"),sQuery(id+"F0.wireOp",EDGE,"E12.53.3"),sQuery(id+"F0.wireOp",EDGE,"E12.53.4"),sQuery(id+"F0.wireOp",EDGE,"E12.53.5"),sQuery(id+"F0.wireOp",EDGE,"E12.53.6"),sQuery(id+"F0.wireOp",EDGE,"E12.53.7"),sQuery(id+"F0.wireOp",EDGE,"E12.53.8"),sQuery(id+"F0.wireOp",EDGE,"E12.53.9"),sQuery(id+"F0.wireOp",EDGE,"E12.54.0"),sQuery(id+"F0.wireOp",EDGE,"E12.54.1"),sQuery(id+"F0.wireOp",EDGE,"E12.54.2"),sQuery(id+"F0.wireOp",EDGE,"E12.54.3"),sQuery(id+"F0.wireOp",EDGE,"E12.54.4"),sQuery(id+"F0.wireOp",EDGE,"E12.54.5"),sQuery(id+"F0.wireOp",EDGE,"E12.54.6"),sQuery(id+"F0.wireOp",EDGE,"E12.54.7"),sQuery(id+"F0.wireOp",EDGE,"E12.54.8"),sQuery(id+"F0.wireOp",EDGE,"E12.54.9"),sQuery(id+"F0.wireOp",EDGE,"E12.55.0"),sQuery(id+"F0.wireOp",EDGE,"E12.55.1"),sQuery(id+"F0.wireOp",EDGE,"E12.55.2"),sQuery(id+"F0.wireOp",EDGE,"E12.55.3"),sQuery(id+"F0.wireOp",EDGE,"E12.55.4"),sQuery(id+"F0.wireOp",EDGE,"E12.55.5"),sQuery(id+"F0.wireOp",EDGE,"E12.55.6"),sQuery(id+"F0.wireOp",EDGE,"E12.55.7"),sQuery(id+"F0.wireOp",EDGE,"E12.55.8"),sQuery(id+"F0.wireOp",EDGE,"E12.55.9"),sQuery(id+"F0.wireOp",EDGE,"E12.56.0"),sQuery(id+"F0.wireOp",EDGE,"E12.56.1"),sQuery(id+"F0.wireOp",EDGE,"E12.56.2"),sQuery(id+"F0.wireOp",EDGE,"E12.56.3"),sQuery(id+"F0.wireOp",EDGE,"E12.56.4"),sQuery(id+"F0.wireOp",EDGE,"E12.56.5"),sQuery(id+"F0.wireOp",EDGE,"E12.56.6"),sQuery(id+"F0.wireOp",EDGE,"E12.56.7"),sQuery(id+"F0.wireOp",EDGE,"E12.56.8"),sQuery(id+"F0.wireOp",EDGE,"E12.56.9"),sQuery(id+"F0.wireOp",EDGE,"E12.57.0"),sQuery(id+"F0.wireOp",EDGE,"E12.57.1"),sQuery(id+"F0.wireOp",EDGE,"E12.57.2"),sQuery(id+"F0.wireOp",EDGE,"E12.57.3"),sQuery(id+"F0.wireOp",EDGE,"E12.57.4"),sQuery(id+"F0.wireOp",EDGE,"E12.57.5"),sQuery(id+"F0.wireOp",EDGE,"E12.57.6"),sQuery(id+"F0.wireOp",EDGE,"E12.57.7"),sQuery(id+"F0.wireOp",EDGE,"E12.57.8"),sQuery(id+"F0.wireOp",EDGE,"E12.57.9"),sQuery(id+"F0.wireOp",EDGE,"E12.58.0"),sQuery(id+"F0.wireOp",EDGE,"E12.58.1"),sQuery(id+"F0.wireOp",EDGE,"E12.58.2"),sQuery(id+"F0.wireOp",EDGE,"E12.58.3"),sQuery(id+"F0.wireOp",EDGE,"E12.58.4"),sQuery(id+"F0.wireOp",EDGE,"E12.58.5"),sQuery(id+"F0.wireOp",EDGE,"E12.58.6"),sQuery(id+"F0.wireOp",EDGE,"E12.58.7"),sQuery(id+"F0.wireOp",EDGE,"E12.58.8"),sQuery(id+"F0.wireOp",EDGE,"E12.58.9"),sQuery(id+"F0.wireOp",EDGE,"E12.59.0"),sQuery(id+"F0.wireOp",EDGE,"E12.59.1"),sQuery(id+"F0.wireOp",EDGE,"E12.59.2"),sQuery(id+"F0.wireOp",EDGE,"E12.59.3"),sQuery(id+"F0.wireOp",EDGE,"E12.59.4"),sQuery(id+"F0.wireOp",EDGE,"E12.59.5"),sQuery(id+"F0.wireOp",EDGE,"E12.59.6"),sQuery(id+"F0.wireOp",EDGE,"E12.59.7"),sQuery(id+"F0.wireOp",EDGE,"E12.59.8"),sQuery(id+"F0.wireOp",EDGE,"E12.59.9"),sQuery(id+"F0.wireOp",EDGE,"E13.trimOffspring"),sQuery(id+"F0.wireOp",EDGE,"E14.trimOffspring")])],"isStart":true}),makeQuery(id+"F3.opExtrude","SWEPT_FACE",FACE,{"disambiguationData":[OSD([sQuery(id+"F2.wireOp",EDGE,"E17.5.0")])]})]});
            var Q14;
            Q14=makeQuery(id+"F3.boolean.opBoolean","INTERSECT",EDGE,{"derivedFrom":[makeQuery(id+"F1.opExtrude","CAP_FACE",FACE,{"disambiguationData":[OSD([sQuery(id+"F0.wireOp",EDGE,"E0"),sQuery(id+"F0.wireOp",EDGE,"E2"),sQuery(id+"F0.wireOp",EDGE,"E3"),sQuery(id+"F0.wireOp",EDGE,"E4.trimOffspring"),sQuery(id+"F0.wireOp",EDGE,"E5.MirrorCS"),sQuery(id+"F0.wireOp",EDGE,"E6.MirrorCS"),sQuery(id+"F0.wireOp",EDGE,"E7.MirrorCS"),sQuery(id+"F0.wireOp",EDGE,"E8.filletArc"),sQuery(id+"F0.wireOp",EDGE,"E9.filletArc"),sQuery(id+"F0.wireOp",EDGE,"E10.filletArc"),sQuery(id+"F0.wireOp",EDGE,"E11.filletArc"),sQuery(id+"F0.wireOp",EDGE,"E12.1.0"),sQuery(id+"F0.wireOp",EDGE,"E12.1.1"),sQuery(id+"F0.wireOp",EDGE,"E12.1.2"),sQuery(id+"F0.wireOp",EDGE,"E12.1.3"),sQuery(id+"F0.wireOp",EDGE,"E12.1.4"),sQuery(id+"F0.wireOp",EDGE,"E12.1.5"),sQuery(id+"F0.wireOp",EDGE,"E12.1.6"),sQuery(id+"F0.wireOp",EDGE,"E12.1.7"),sQuery(id+"F0.wireOp",EDGE,"E12.1.8"),sQuery(id+"F0.wireOp",EDGE,"E12.1.9"),sQuery(id+"F0.wireOp",EDGE,"E12.2.0"),sQuery(id+"F0.wireOp",EDGE,"E12.2.1"),sQuery(id+"F0.wireOp",EDGE,"E12.2.2"),sQuery(id+"F0.wireOp",EDGE,"E12.2.3"),sQuery(id+"F0.wireOp",EDGE,"E12.2.4"),sQuery(id+"F0.wireOp",EDGE,"E12.2.5"),sQuery(id+"F0.wireOp",EDGE,"E12.2.6"),sQuery(id+"F0.wireOp",EDGE,"E12.2.7"),sQuery(id+"F0.wireOp",EDGE,"E12.2.8"),sQuery(id+"F0.wireOp",EDGE,"E12.2.9"),sQuery(id+"F0.wireOp",EDGE,"E12.3.0"),sQuery(id+"F0.wireOp",EDGE,"E12.3.1"),sQuery(id+"F0.wireOp",EDGE,"E12.3.2"),sQuery(id+"F0.wireOp",EDGE,"E12.3.3"),sQuery(id+"F0.wireOp",EDGE,"E12.3.4"),sQuery(id+"F0.wireOp",EDGE,"E12.3.5"),sQuery(id+"F0.wireOp",EDGE,"E12.3.6"),sQuery(id+"F0.wireOp",EDGE,"E12.3.7"),sQuery(id+"F0.wireOp",EDGE,"E12.3.8"),sQuery(id+"F0.wireOp",EDGE,"E12.3.9"),sQuery(id+"F0.wireOp",EDGE,"E12.4.0"),sQuery(id+"F0.wireOp",EDGE,"E12.4.1"),sQuery(id+"F0.wireOp",EDGE,"E12.4.2"),sQuery(id+"F0.wireOp",EDGE,"E12.4.3"),sQuery(id+"F0.wireOp",EDGE,"E12.4.4"),sQuery(id+"F0.wireOp",EDGE,"E12.4.5"),sQuery(id+"F0.wireOp",EDGE,"E12.4.6"),sQuery(id+"F0.wireOp",EDGE,"E12.4.7"),sQuery(id+"F0.wireOp",EDGE,"E12.4.8"),sQuery(id+"F0.wireOp",EDGE,"E12.4.9"),sQuery(id+"F0.wireOp",EDGE,"E12.5.0"),sQuery(id+"F0.wireOp",EDGE,"E12.5.1"),sQuery(id+"F0.wireOp",EDGE,"E12.5.2"),sQuery(id+"F0.wireOp",EDGE,"E12.5.3"),sQuery(id+"F0.wireOp",EDGE,"E12.5.4"),sQuery(id+"F0.wireOp",EDGE,"E12.5.5"),sQuery(id+"F0.wireOp",EDGE,"E12.5.6"),sQuery(id+"F0.wireOp",EDGE,"E12.5.7"),sQuery(id+"F0.wireOp",EDGE,"E12.5.8"),sQuery(id+"F0.wireOp",EDGE,"E12.5.9"),sQuery(id+"F0.wireOp",EDGE,"E12.6.0"),sQuery(id+"F0.wireOp",EDGE,"E12.6.1"),sQuery(id+"F0.wireOp",EDGE,"E12.6.2"),sQuery(id+"F0.wireOp",EDGE,"E12.6.3"),sQuery(id+"F0.wireOp",EDGE,"E12.6.4"),sQuery(id+"F0.wireOp",EDGE,"E12.6.5"),sQuery(id+"F0.wireOp",EDGE,"E12.6.6"),sQuery(id+"F0.wireOp",EDGE,"E12.6.7"),sQuery(id+"F0.wireOp",EDGE,"E12.6.8"),sQuery(id+"F0.wireOp",EDGE,"E12.6.9"),sQuery(id+"F0.wireOp",EDGE,"E12.7.0"),sQuery(id+"F0.wireOp",EDGE,"E12.7.1"),sQuery(id+"F0.wireOp",EDGE,"E12.7.2"),sQuery(id+"F0.wireOp",EDGE,"E12.7.3"),sQuery(id+"F0.wireOp",EDGE,"E12.7.4"),sQuery(id+"F0.wireOp",EDGE,"E12.7.5"),sQuery(id+"F0.wireOp",EDGE,"E12.7.6"),sQuery(id+"F0.wireOp",EDGE,"E12.7.7"),sQuery(id+"F0.wireOp",EDGE,"E12.7.8"),sQuery(id+"F0.wireOp",EDGE,"E12.7.9"),sQuery(id+"F0.wireOp",EDGE,"E12.8.0"),sQuery(id+"F0.wireOp",EDGE,"E12.8.1"),sQuery(id+"F0.wireOp",EDGE,"E12.8.2"),sQuery(id+"F0.wireOp",EDGE,"E12.8.3"),sQuery(id+"F0.wireOp",EDGE,"E12.8.4"),sQuery(id+"F0.wireOp",EDGE,"E12.8.5"),sQuery(id+"F0.wireOp",EDGE,"E12.8.6"),sQuery(id+"F0.wireOp",EDGE,"E12.8.7"),sQuery(id+"F0.wireOp",EDGE,"E12.8.8"),sQuery(id+"F0.wireOp",EDGE,"E12.8.9"),sQuery(id+"F0.wireOp",EDGE,"E12.9.0"),sQuery(id+"F0.wireOp",EDGE,"E12.9.1"),sQuery(id+"F0.wireOp",EDGE,"E12.9.2"),sQuery(id+"F0.wireOp",EDGE,"E12.9.3"),sQuery(id+"F0.wireOp",EDGE,"E12.9.4"),sQuery(id+"F0.wireOp",EDGE,"E12.9.5"),sQuery(id+"F0.wireOp",EDGE,"E12.9.6"),sQuery(id+"F0.wireOp",EDGE,"E12.9.7"),sQuery(id+"F0.wireOp",EDGE,"E12.9.8"),sQuery(id+"F0.wireOp",EDGE,"E12.9.9"),sQuery(id+"F0.wireOp",EDGE,"E12.10.0"),sQuery(id+"F0.wireOp",EDGE,"E12.10.1"),sQuery(id+"F0.wireOp",EDGE,"E12.10.2"),sQuery(id+"F0.wireOp",EDGE,"E12.10.3"),sQuery(id+"F0.wireOp",EDGE,"E12.10.4"),sQuery(id+"F0.wireOp",EDGE,"E12.10.5"),sQuery(id+"F0.wireOp",EDGE,"E12.10.6"),sQuery(id+"F0.wireOp",EDGE,"E12.10.7"),sQuery(id+"F0.wireOp",EDGE,"E12.10.8"),sQuery(id+"F0.wireOp",EDGE,"E12.10.9"),sQuery(id+"F0.wireOp",EDGE,"E12.11.0"),sQuery(id+"F0.wireOp",EDGE,"E12.11.1"),sQuery(id+"F0.wireOp",EDGE,"E12.11.2"),sQuery(id+"F0.wireOp",EDGE,"E12.11.3"),sQuery(id+"F0.wireOp",EDGE,"E12.11.4"),sQuery(id+"F0.wireOp",EDGE,"E12.11.5"),sQuery(id+"F0.wireOp",EDGE,"E12.11.6"),sQuery(id+"F0.wireOp",EDGE,"E12.11.7"),sQuery(id+"F0.wireOp",EDGE,"E12.11.8"),sQuery(id+"F0.wireOp",EDGE,"E12.11.9"),sQuery(id+"F0.wireOp",EDGE,"E12.12.0"),sQuery(id+"F0.wireOp",EDGE,"E12.12.1"),sQuery(id+"F0.wireOp",EDGE,"E12.12.2"),sQuery(id+"F0.wireOp",EDGE,"E12.12.3"),sQuery(id+"F0.wireOp",EDGE,"E12.12.4"),sQuery(id+"F0.wireOp",EDGE,"E12.12.5"),sQuery(id+"F0.wireOp",EDGE,"E12.12.6"),sQuery(id+"F0.wireOp",EDGE,"E12.12.7"),sQuery(id+"F0.wireOp",EDGE,"E12.12.8"),sQuery(id+"F0.wireOp",EDGE,"E12.12.9"),sQuery(id+"F0.wireOp",EDGE,"E12.13.0"),sQuery(id+"F0.wireOp",EDGE,"E12.13.1"),sQuery(id+"F0.wireOp",EDGE,"E12.13.2"),sQuery(id+"F0.wireOp",EDGE,"E12.13.3"),sQuery(id+"F0.wireOp",EDGE,"E12.13.4"),sQuery(id+"F0.wireOp",EDGE,"E12.13.5"),sQuery(id+"F0.wireOp",EDGE,"E12.13.6"),sQuery(id+"F0.wireOp",EDGE,"E12.13.7"),sQuery(id+"F0.wireOp",EDGE,"E12.13.8"),sQuery(id+"F0.wireOp",EDGE,"E12.13.9"),sQuery(id+"F0.wireOp",EDGE,"E12.14.0"),sQuery(id+"F0.wireOp",EDGE,"E12.14.1"),sQuery(id+"F0.wireOp",EDGE,"E12.14.2"),sQuery(id+"F0.wireOp",EDGE,"E12.14.3"),sQuery(id+"F0.wireOp",EDGE,"E12.14.4"),sQuery(id+"F0.wireOp",EDGE,"E12.14.5"),sQuery(id+"F0.wireOp",EDGE,"E12.14.6"),sQuery(id+"F0.wireOp",EDGE,"E12.14.7"),sQuery(id+"F0.wireOp",EDGE,"E12.14.8"),sQuery(id+"F0.wireOp",EDGE,"E12.14.9"),sQuery(id+"F0.wireOp",EDGE,"E12.15.0"),sQuery(id+"F0.wireOp",EDGE,"E12.15.1"),sQuery(id+"F0.wireOp",EDGE,"E12.15.2"),sQuery(id+"F0.wireOp",EDGE,"E12.15.3"),sQuery(id+"F0.wireOp",EDGE,"E12.15.4"),sQuery(id+"F0.wireOp",EDGE,"E12.15.5"),sQuery(id+"F0.wireOp",EDGE,"E12.15.6"),sQuery(id+"F0.wireOp",EDGE,"E12.15.7"),sQuery(id+"F0.wireOp",EDGE,"E12.15.8"),sQuery(id+"F0.wireOp",EDGE,"E12.15.9"),sQuery(id+"F0.wireOp",EDGE,"E12.16.0"),sQuery(id+"F0.wireOp",EDGE,"E12.16.1"),sQuery(id+"F0.wireOp",EDGE,"E12.16.2"),sQuery(id+"F0.wireOp",EDGE,"E12.16.3"),sQuery(id+"F0.wireOp",EDGE,"E12.16.4"),sQuery(id+"F0.wireOp",EDGE,"E12.16.5"),sQuery(id+"F0.wireOp",EDGE,"E12.16.6"),sQuery(id+"F0.wireOp",EDGE,"E12.16.7"),sQuery(id+"F0.wireOp",EDGE,"E12.16.8"),sQuery(id+"F0.wireOp",EDGE,"E12.16.9"),sQuery(id+"F0.wireOp",EDGE,"E12.17.0"),sQuery(id+"F0.wireOp",EDGE,"E12.17.1"),sQuery(id+"F0.wireOp",EDGE,"E12.17.2"),sQuery(id+"F0.wireOp",EDGE,"E12.17.3"),sQuery(id+"F0.wireOp",EDGE,"E12.17.4"),sQuery(id+"F0.wireOp",EDGE,"E12.17.5"),sQuery(id+"F0.wireOp",EDGE,"E12.17.6"),sQuery(id+"F0.wireOp",EDGE,"E12.17.7"),sQuery(id+"F0.wireOp",EDGE,"E12.17.8"),sQuery(id+"F0.wireOp",EDGE,"E12.17.9"),sQuery(id+"F0.wireOp",EDGE,"E12.18.0"),sQuery(id+"F0.wireOp",EDGE,"E12.18.1"),sQuery(id+"F0.wireOp",EDGE,"E12.18.2"),sQuery(id+"F0.wireOp",EDGE,"E12.18.3"),sQuery(id+"F0.wireOp",EDGE,"E12.18.4"),sQuery(id+"F0.wireOp",EDGE,"E12.18.5"),sQuery(id+"F0.wireOp",EDGE,"E12.18.6"),sQuery(id+"F0.wireOp",EDGE,"E12.18.7"),sQuery(id+"F0.wireOp",EDGE,"E12.18.8"),sQuery(id+"F0.wireOp",EDGE,"E12.18.9"),sQuery(id+"F0.wireOp",EDGE,"E12.19.0"),sQuery(id+"F0.wireOp",EDGE,"E12.19.1"),sQuery(id+"F0.wireOp",EDGE,"E12.19.2"),sQuery(id+"F0.wireOp",EDGE,"E12.19.3"),sQuery(id+"F0.wireOp",EDGE,"E12.19.4"),sQuery(id+"F0.wireOp",EDGE,"E12.19.5"),sQuery(id+"F0.wireOp",EDGE,"E12.19.6"),sQuery(id+"F0.wireOp",EDGE,"E12.19.7"),sQuery(id+"F0.wireOp",EDGE,"E12.19.8"),sQuery(id+"F0.wireOp",EDGE,"E12.19.9"),sQuery(id+"F0.wireOp",EDGE,"E12.20.0"),sQuery(id+"F0.wireOp",EDGE,"E12.20.1"),sQuery(id+"F0.wireOp",EDGE,"E12.20.2"),sQuery(id+"F0.wireOp",EDGE,"E12.20.3"),sQuery(id+"F0.wireOp",EDGE,"E12.20.4"),sQuery(id+"F0.wireOp",EDGE,"E12.20.5"),sQuery(id+"F0.wireOp",EDGE,"E12.20.6"),sQuery(id+"F0.wireOp",EDGE,"E12.20.7"),sQuery(id+"F0.wireOp",EDGE,"E12.20.8"),sQuery(id+"F0.wireOp",EDGE,"E12.20.9"),sQuery(id+"F0.wireOp",EDGE,"E12.21.0"),sQuery(id+"F0.wireOp",EDGE,"E12.21.1"),sQuery(id+"F0.wireOp",EDGE,"E12.21.2"),sQuery(id+"F0.wireOp",EDGE,"E12.21.3"),sQuery(id+"F0.wireOp",EDGE,"E12.21.4"),sQuery(id+"F0.wireOp",EDGE,"E12.21.5"),sQuery(id+"F0.wireOp",EDGE,"E12.21.6"),sQuery(id+"F0.wireOp",EDGE,"E12.21.7"),sQuery(id+"F0.wireOp",EDGE,"E12.21.8"),sQuery(id+"F0.wireOp",EDGE,"E12.21.9"),sQuery(id+"F0.wireOp",EDGE,"E12.22.0"),sQuery(id+"F0.wireOp",EDGE,"E12.22.1"),sQuery(id+"F0.wireOp",EDGE,"E12.22.2"),sQuery(id+"F0.wireOp",EDGE,"E12.22.3"),sQuery(id+"F0.wireOp",EDGE,"E12.22.4"),sQuery(id+"F0.wireOp",EDGE,"E12.22.5"),sQuery(id+"F0.wireOp",EDGE,"E12.22.6"),sQuery(id+"F0.wireOp",EDGE,"E12.22.7"),sQuery(id+"F0.wireOp",EDGE,"E12.22.8"),sQuery(id+"F0.wireOp",EDGE,"E12.22.9"),sQuery(id+"F0.wireOp",EDGE,"E12.23.0"),sQuery(id+"F0.wireOp",EDGE,"E12.23.1"),sQuery(id+"F0.wireOp",EDGE,"E12.23.2"),sQuery(id+"F0.wireOp",EDGE,"E12.23.3"),sQuery(id+"F0.wireOp",EDGE,"E12.23.4"),sQuery(id+"F0.wireOp",EDGE,"E12.23.5"),sQuery(id+"F0.wireOp",EDGE,"E12.23.6"),sQuery(id+"F0.wireOp",EDGE,"E12.23.7"),sQuery(id+"F0.wireOp",EDGE,"E12.23.8"),sQuery(id+"F0.wireOp",EDGE,"E12.23.9"),sQuery(id+"F0.wireOp",EDGE,"E12.24.0"),sQuery(id+"F0.wireOp",EDGE,"E12.24.1"),sQuery(id+"F0.wireOp",EDGE,"E12.24.2"),sQuery(id+"F0.wireOp",EDGE,"E12.24.3"),sQuery(id+"F0.wireOp",EDGE,"E12.24.4"),sQuery(id+"F0.wireOp",EDGE,"E12.24.5"),sQuery(id+"F0.wireOp",EDGE,"E12.24.6"),sQuery(id+"F0.wireOp",EDGE,"E12.24.7"),sQuery(id+"F0.wireOp",EDGE,"E12.24.8"),sQuery(id+"F0.wireOp",EDGE,"E12.24.9"),sQuery(id+"F0.wireOp",EDGE,"E12.25.0"),sQuery(id+"F0.wireOp",EDGE,"E12.25.1"),sQuery(id+"F0.wireOp",EDGE,"E12.25.2"),sQuery(id+"F0.wireOp",EDGE,"E12.25.3"),sQuery(id+"F0.wireOp",EDGE,"E12.25.4"),sQuery(id+"F0.wireOp",EDGE,"E12.25.5"),sQuery(id+"F0.wireOp",EDGE,"E12.25.6"),sQuery(id+"F0.wireOp",EDGE,"E12.25.7"),sQuery(id+"F0.wireOp",EDGE,"E12.25.8"),sQuery(id+"F0.wireOp",EDGE,"E12.25.9"),sQuery(id+"F0.wireOp",EDGE,"E12.26.0"),sQuery(id+"F0.wireOp",EDGE,"E12.26.1"),sQuery(id+"F0.wireOp",EDGE,"E12.26.2"),sQuery(id+"F0.wireOp",EDGE,"E12.26.3"),sQuery(id+"F0.wireOp",EDGE,"E12.26.4"),sQuery(id+"F0.wireOp",EDGE,"E12.26.5"),sQuery(id+"F0.wireOp",EDGE,"E12.26.6"),sQuery(id+"F0.wireOp",EDGE,"E12.26.7"),sQuery(id+"F0.wireOp",EDGE,"E12.26.8"),sQuery(id+"F0.wireOp",EDGE,"E12.26.9"),sQuery(id+"F0.wireOp",EDGE,"E12.27.0"),sQuery(id+"F0.wireOp",EDGE,"E12.27.1"),sQuery(id+"F0.wireOp",EDGE,"E12.27.2"),sQuery(id+"F0.wireOp",EDGE,"E12.27.3"),sQuery(id+"F0.wireOp",EDGE,"E12.27.4"),sQuery(id+"F0.wireOp",EDGE,"E12.27.5"),sQuery(id+"F0.wireOp",EDGE,"E12.27.6"),sQuery(id+"F0.wireOp",EDGE,"E12.27.7"),sQuery(id+"F0.wireOp",EDGE,"E12.27.8"),sQuery(id+"F0.wireOp",EDGE,"E12.27.9"),sQuery(id+"F0.wireOp",EDGE,"E12.28.0"),sQuery(id+"F0.wireOp",EDGE,"E12.28.1"),sQuery(id+"F0.wireOp",EDGE,"E12.28.2"),sQuery(id+"F0.wireOp",EDGE,"E12.28.3"),sQuery(id+"F0.wireOp",EDGE,"E12.28.4"),sQuery(id+"F0.wireOp",EDGE,"E12.28.5"),sQuery(id+"F0.wireOp",EDGE,"E12.28.6"),sQuery(id+"F0.wireOp",EDGE,"E12.28.7"),sQuery(id+"F0.wireOp",EDGE,"E12.28.8"),sQuery(id+"F0.wireOp",EDGE,"E12.28.9"),sQuery(id+"F0.wireOp",EDGE,"E12.29.0"),sQuery(id+"F0.wireOp",EDGE,"E12.29.1"),sQuery(id+"F0.wireOp",EDGE,"E12.29.2"),sQuery(id+"F0.wireOp",EDGE,"E12.29.3"),sQuery(id+"F0.wireOp",EDGE,"E12.29.4"),sQuery(id+"F0.wireOp",EDGE,"E12.29.5"),sQuery(id+"F0.wireOp",EDGE,"E12.29.6"),sQuery(id+"F0.wireOp",EDGE,"E12.29.7"),sQuery(id+"F0.wireOp",EDGE,"E12.29.8"),sQuery(id+"F0.wireOp",EDGE,"E12.29.9"),sQuery(id+"F0.wireOp",EDGE,"E12.30.0"),sQuery(id+"F0.wireOp",EDGE,"E12.30.1"),sQuery(id+"F0.wireOp",EDGE,"E12.30.2"),sQuery(id+"F0.wireOp",EDGE,"E12.30.3"),sQuery(id+"F0.wireOp",EDGE,"E12.30.4"),sQuery(id+"F0.wireOp",EDGE,"E12.30.5"),sQuery(id+"F0.wireOp",EDGE,"E12.30.6"),sQuery(id+"F0.wireOp",EDGE,"E12.30.7"),sQuery(id+"F0.wireOp",EDGE,"E12.30.8"),sQuery(id+"F0.wireOp",EDGE,"E12.30.9"),sQuery(id+"F0.wireOp",EDGE,"E12.31.0"),sQuery(id+"F0.wireOp",EDGE,"E12.31.1"),sQuery(id+"F0.wireOp",EDGE,"E12.31.2"),sQuery(id+"F0.wireOp",EDGE,"E12.31.3"),sQuery(id+"F0.wireOp",EDGE,"E12.31.4"),sQuery(id+"F0.wireOp",EDGE,"E12.31.5"),sQuery(id+"F0.wireOp",EDGE,"E12.31.6"),sQuery(id+"F0.wireOp",EDGE,"E12.31.7"),sQuery(id+"F0.wireOp",EDGE,"E12.31.8"),sQuery(id+"F0.wireOp",EDGE,"E12.31.9"),sQuery(id+"F0.wireOp",EDGE,"E12.32.0"),sQuery(id+"F0.wireOp",EDGE,"E12.32.1"),sQuery(id+"F0.wireOp",EDGE,"E12.32.2"),sQuery(id+"F0.wireOp",EDGE,"E12.32.3"),sQuery(id+"F0.wireOp",EDGE,"E12.32.4"),sQuery(id+"F0.wireOp",EDGE,"E12.32.5"),sQuery(id+"F0.wireOp",EDGE,"E12.32.6"),sQuery(id+"F0.wireOp",EDGE,"E12.32.7"),sQuery(id+"F0.wireOp",EDGE,"E12.32.8"),sQuery(id+"F0.wireOp",EDGE,"E12.32.9"),sQuery(id+"F0.wireOp",EDGE,"E12.33.0"),sQuery(id+"F0.wireOp",EDGE,"E12.33.1"),sQuery(id+"F0.wireOp",EDGE,"E12.33.2"),sQuery(id+"F0.wireOp",EDGE,"E12.33.3"),sQuery(id+"F0.wireOp",EDGE,"E12.33.4"),sQuery(id+"F0.wireOp",EDGE,"E12.33.5"),sQuery(id+"F0.wireOp",EDGE,"E12.33.6"),sQuery(id+"F0.wireOp",EDGE,"E12.33.7"),sQuery(id+"F0.wireOp",EDGE,"E12.33.8"),sQuery(id+"F0.wireOp",EDGE,"E12.33.9"),sQuery(id+"F0.wireOp",EDGE,"E12.34.0"),sQuery(id+"F0.wireOp",EDGE,"E12.34.1"),sQuery(id+"F0.wireOp",EDGE,"E12.34.2"),sQuery(id+"F0.wireOp",EDGE,"E12.34.3"),sQuery(id+"F0.wireOp",EDGE,"E12.34.4"),sQuery(id+"F0.wireOp",EDGE,"E12.34.5"),sQuery(id+"F0.wireOp",EDGE,"E12.34.6"),sQuery(id+"F0.wireOp",EDGE,"E12.34.7"),sQuery(id+"F0.wireOp",EDGE,"E12.34.8"),sQuery(id+"F0.wireOp",EDGE,"E12.34.9"),sQuery(id+"F0.wireOp",EDGE,"E12.35.0"),sQuery(id+"F0.wireOp",EDGE,"E12.35.1"),sQuery(id+"F0.wireOp",EDGE,"E12.35.2"),sQuery(id+"F0.wireOp",EDGE,"E12.35.3"),sQuery(id+"F0.wireOp",EDGE,"E12.35.4"),sQuery(id+"F0.wireOp",EDGE,"E12.35.5"),sQuery(id+"F0.wireOp",EDGE,"E12.35.6"),sQuery(id+"F0.wireOp",EDGE,"E12.35.7"),sQuery(id+"F0.wireOp",EDGE,"E12.35.8"),sQuery(id+"F0.wireOp",EDGE,"E12.35.9"),sQuery(id+"F0.wireOp",EDGE,"E12.36.0"),sQuery(id+"F0.wireOp",EDGE,"E12.36.1"),sQuery(id+"F0.wireOp",EDGE,"E12.36.2"),sQuery(id+"F0.wireOp",EDGE,"E12.36.3"),sQuery(id+"F0.wireOp",EDGE,"E12.36.4"),sQuery(id+"F0.wireOp",EDGE,"E12.36.5"),sQuery(id+"F0.wireOp",EDGE,"E12.36.6"),sQuery(id+"F0.wireOp",EDGE,"E12.36.7"),sQuery(id+"F0.wireOp",EDGE,"E12.36.8"),sQuery(id+"F0.wireOp",EDGE,"E12.36.9"),sQuery(id+"F0.wireOp",EDGE,"E12.37.0"),sQuery(id+"F0.wireOp",EDGE,"E12.37.1"),sQuery(id+"F0.wireOp",EDGE,"E12.37.2"),sQuery(id+"F0.wireOp",EDGE,"E12.37.3"),sQuery(id+"F0.wireOp",EDGE,"E12.37.4"),sQuery(id+"F0.wireOp",EDGE,"E12.37.5"),sQuery(id+"F0.wireOp",EDGE,"E12.37.6"),sQuery(id+"F0.wireOp",EDGE,"E12.37.7"),sQuery(id+"F0.wireOp",EDGE,"E12.37.8"),sQuery(id+"F0.wireOp",EDGE,"E12.37.9"),sQuery(id+"F0.wireOp",EDGE,"E12.38.0"),sQuery(id+"F0.wireOp",EDGE,"E12.38.1"),sQuery(id+"F0.wireOp",EDGE,"E12.38.2"),sQuery(id+"F0.wireOp",EDGE,"E12.38.3"),sQuery(id+"F0.wireOp",EDGE,"E12.38.4"),sQuery(id+"F0.wireOp",EDGE,"E12.38.5"),sQuery(id+"F0.wireOp",EDGE,"E12.38.6"),sQuery(id+"F0.wireOp",EDGE,"E12.38.7"),sQuery(id+"F0.wireOp",EDGE,"E12.38.8"),sQuery(id+"F0.wireOp",EDGE,"E12.38.9"),sQuery(id+"F0.wireOp",EDGE,"E12.39.0"),sQuery(id+"F0.wireOp",EDGE,"E12.39.1"),sQuery(id+"F0.wireOp",EDGE,"E12.39.2"),sQuery(id+"F0.wireOp",EDGE,"E12.39.3"),sQuery(id+"F0.wireOp",EDGE,"E12.39.4"),sQuery(id+"F0.wireOp",EDGE,"E12.39.5"),sQuery(id+"F0.wireOp",EDGE,"E12.39.6"),sQuery(id+"F0.wireOp",EDGE,"E12.39.7"),sQuery(id+"F0.wireOp",EDGE,"E12.39.8"),sQuery(id+"F0.wireOp",EDGE,"E12.39.9"),sQuery(id+"F0.wireOp",EDGE,"E12.40.0"),sQuery(id+"F0.wireOp",EDGE,"E12.40.1"),sQuery(id+"F0.wireOp",EDGE,"E12.40.2"),sQuery(id+"F0.wireOp",EDGE,"E12.40.3"),sQuery(id+"F0.wireOp",EDGE,"E12.40.4"),sQuery(id+"F0.wireOp",EDGE,"E12.40.5"),sQuery(id+"F0.wireOp",EDGE,"E12.40.6"),sQuery(id+"F0.wireOp",EDGE,"E12.40.7"),sQuery(id+"F0.wireOp",EDGE,"E12.40.8"),sQuery(id+"F0.wireOp",EDGE,"E12.40.9"),sQuery(id+"F0.wireOp",EDGE,"E12.41.0"),sQuery(id+"F0.wireOp",EDGE,"E12.41.1"),sQuery(id+"F0.wireOp",EDGE,"E12.41.2"),sQuery(id+"F0.wireOp",EDGE,"E12.41.3"),sQuery(id+"F0.wireOp",EDGE,"E12.41.4"),sQuery(id+"F0.wireOp",EDGE,"E12.41.5"),sQuery(id+"F0.wireOp",EDGE,"E12.41.6"),sQuery(id+"F0.wireOp",EDGE,"E12.41.7"),sQuery(id+"F0.wireOp",EDGE,"E12.41.8"),sQuery(id+"F0.wireOp",EDGE,"E12.41.9"),sQuery(id+"F0.wireOp",EDGE,"E12.42.0"),sQuery(id+"F0.wireOp",EDGE,"E12.42.1"),sQuery(id+"F0.wireOp",EDGE,"E12.42.2"),sQuery(id+"F0.wireOp",EDGE,"E12.42.3"),sQuery(id+"F0.wireOp",EDGE,"E12.42.4"),sQuery(id+"F0.wireOp",EDGE,"E12.42.5"),sQuery(id+"F0.wireOp",EDGE,"E12.42.6"),sQuery(id+"F0.wireOp",EDGE,"E12.42.7"),sQuery(id+"F0.wireOp",EDGE,"E12.42.8"),sQuery(id+"F0.wireOp",EDGE,"E12.42.9"),sQuery(id+"F0.wireOp",EDGE,"E12.43.0"),sQuery(id+"F0.wireOp",EDGE,"E12.43.1"),sQuery(id+"F0.wireOp",EDGE,"E12.43.2"),sQuery(id+"F0.wireOp",EDGE,"E12.43.3"),sQuery(id+"F0.wireOp",EDGE,"E12.43.4"),sQuery(id+"F0.wireOp",EDGE,"E12.43.5"),sQuery(id+"F0.wireOp",EDGE,"E12.43.6"),sQuery(id+"F0.wireOp",EDGE,"E12.43.7"),sQuery(id+"F0.wireOp",EDGE,"E12.43.8"),sQuery(id+"F0.wireOp",EDGE,"E12.43.9"),sQuery(id+"F0.wireOp",EDGE,"E12.44.0"),sQuery(id+"F0.wireOp",EDGE,"E12.44.1"),sQuery(id+"F0.wireOp",EDGE,"E12.44.2"),sQuery(id+"F0.wireOp",EDGE,"E12.44.3"),sQuery(id+"F0.wireOp",EDGE,"E12.44.4"),sQuery(id+"F0.wireOp",EDGE,"E12.44.5"),sQuery(id+"F0.wireOp",EDGE,"E12.44.6"),sQuery(id+"F0.wireOp",EDGE,"E12.44.7"),sQuery(id+"F0.wireOp",EDGE,"E12.44.8"),sQuery(id+"F0.wireOp",EDGE,"E12.44.9"),sQuery(id+"F0.wireOp",EDGE,"E12.45.0"),sQuery(id+"F0.wireOp",EDGE,"E12.45.1"),sQuery(id+"F0.wireOp",EDGE,"E12.45.2"),sQuery(id+"F0.wireOp",EDGE,"E12.45.3"),sQuery(id+"F0.wireOp",EDGE,"E12.45.4"),sQuery(id+"F0.wireOp",EDGE,"E12.45.5"),sQuery(id+"F0.wireOp",EDGE,"E12.45.6"),sQuery(id+"F0.wireOp",EDGE,"E12.45.7"),sQuery(id+"F0.wireOp",EDGE,"E12.45.8"),sQuery(id+"F0.wireOp",EDGE,"E12.45.9"),sQuery(id+"F0.wireOp",EDGE,"E12.46.0"),sQuery(id+"F0.wireOp",EDGE,"E12.46.1"),sQuery(id+"F0.wireOp",EDGE,"E12.46.2"),sQuery(id+"F0.wireOp",EDGE,"E12.46.3"),sQuery(id+"F0.wireOp",EDGE,"E12.46.4"),sQuery(id+"F0.wireOp",EDGE,"E12.46.5"),sQuery(id+"F0.wireOp",EDGE,"E12.46.6"),sQuery(id+"F0.wireOp",EDGE,"E12.46.7"),sQuery(id+"F0.wireOp",EDGE,"E12.46.8"),sQuery(id+"F0.wireOp",EDGE,"E12.46.9"),sQuery(id+"F0.wireOp",EDGE,"E12.47.0"),sQuery(id+"F0.wireOp",EDGE,"E12.47.1"),sQuery(id+"F0.wireOp",EDGE,"E12.47.2"),sQuery(id+"F0.wireOp",EDGE,"E12.47.3"),sQuery(id+"F0.wireOp",EDGE,"E12.47.4"),sQuery(id+"F0.wireOp",EDGE,"E12.47.5"),sQuery(id+"F0.wireOp",EDGE,"E12.47.6"),sQuery(id+"F0.wireOp",EDGE,"E12.47.7"),sQuery(id+"F0.wireOp",EDGE,"E12.47.8"),sQuery(id+"F0.wireOp",EDGE,"E12.47.9"),sQuery(id+"F0.wireOp",EDGE,"E12.48.0"),sQuery(id+"F0.wireOp",EDGE,"E12.48.1"),sQuery(id+"F0.wireOp",EDGE,"E12.48.2"),sQuery(id+"F0.wireOp",EDGE,"E12.48.3"),sQuery(id+"F0.wireOp",EDGE,"E12.48.4"),sQuery(id+"F0.wireOp",EDGE,"E12.48.5"),sQuery(id+"F0.wireOp",EDGE,"E12.48.6"),sQuery(id+"F0.wireOp",EDGE,"E12.48.7"),sQuery(id+"F0.wireOp",EDGE,"E12.48.8"),sQuery(id+"F0.wireOp",EDGE,"E12.48.9"),sQuery(id+"F0.wireOp",EDGE,"E12.49.0"),sQuery(id+"F0.wireOp",EDGE,"E12.49.1"),sQuery(id+"F0.wireOp",EDGE,"E12.49.2"),sQuery(id+"F0.wireOp",EDGE,"E12.49.3"),sQuery(id+"F0.wireOp",EDGE,"E12.49.4"),sQuery(id+"F0.wireOp",EDGE,"E12.49.5"),sQuery(id+"F0.wireOp",EDGE,"E12.49.6"),sQuery(id+"F0.wireOp",EDGE,"E12.49.7"),sQuery(id+"F0.wireOp",EDGE,"E12.49.8"),sQuery(id+"F0.wireOp",EDGE,"E12.49.9"),sQuery(id+"F0.wireOp",EDGE,"E12.50.0"),sQuery(id+"F0.wireOp",EDGE,"E12.50.1"),sQuery(id+"F0.wireOp",EDGE,"E12.50.2"),sQuery(id+"F0.wireOp",EDGE,"E12.50.3"),sQuery(id+"F0.wireOp",EDGE,"E12.50.4"),sQuery(id+"F0.wireOp",EDGE,"E12.50.5"),sQuery(id+"F0.wireOp",EDGE,"E12.50.6"),sQuery(id+"F0.wireOp",EDGE,"E12.50.7"),sQuery(id+"F0.wireOp",EDGE,"E12.50.8"),sQuery(id+"F0.wireOp",EDGE,"E12.50.9"),sQuery(id+"F0.wireOp",EDGE,"E12.51.0"),sQuery(id+"F0.wireOp",EDGE,"E12.51.1"),sQuery(id+"F0.wireOp",EDGE,"E12.51.2"),sQuery(id+"F0.wireOp",EDGE,"E12.51.3"),sQuery(id+"F0.wireOp",EDGE,"E12.51.4"),sQuery(id+"F0.wireOp",EDGE,"E12.51.5"),sQuery(id+"F0.wireOp",EDGE,"E12.51.6"),sQuery(id+"F0.wireOp",EDGE,"E12.51.7"),sQuery(id+"F0.wireOp",EDGE,"E12.51.8"),sQuery(id+"F0.wireOp",EDGE,"E12.51.9"),sQuery(id+"F0.wireOp",EDGE,"E12.52.0"),sQuery(id+"F0.wireOp",EDGE,"E12.52.1"),sQuery(id+"F0.wireOp",EDGE,"E12.52.2"),sQuery(id+"F0.wireOp",EDGE,"E12.52.3"),sQuery(id+"F0.wireOp",EDGE,"E12.52.4"),sQuery(id+"F0.wireOp",EDGE,"E12.52.5"),sQuery(id+"F0.wireOp",EDGE,"E12.52.6"),sQuery(id+"F0.wireOp",EDGE,"E12.52.7"),sQuery(id+"F0.wireOp",EDGE,"E12.52.8"),sQuery(id+"F0.wireOp",EDGE,"E12.52.9"),sQuery(id+"F0.wireOp",EDGE,"E12.53.0"),sQuery(id+"F0.wireOp",EDGE,"E12.53.1"),sQuery(id+"F0.wireOp",EDGE,"E12.53.2"),sQuery(id+"F0.wireOp",EDGE,"E12.53.3"),sQuery(id+"F0.wireOp",EDGE,"E12.53.4"),sQuery(id+"F0.wireOp",EDGE,"E12.53.5"),sQuery(id+"F0.wireOp",EDGE,"E12.53.6"),sQuery(id+"F0.wireOp",EDGE,"E12.53.7"),sQuery(id+"F0.wireOp",EDGE,"E12.53.8"),sQuery(id+"F0.wireOp",EDGE,"E12.53.9"),sQuery(id+"F0.wireOp",EDGE,"E12.54.0"),sQuery(id+"F0.wireOp",EDGE,"E12.54.1"),sQuery(id+"F0.wireOp",EDGE,"E12.54.2"),sQuery(id+"F0.wireOp",EDGE,"E12.54.3"),sQuery(id+"F0.wireOp",EDGE,"E12.54.4"),sQuery(id+"F0.wireOp",EDGE,"E12.54.5"),sQuery(id+"F0.wireOp",EDGE,"E12.54.6"),sQuery(id+"F0.wireOp",EDGE,"E12.54.7"),sQuery(id+"F0.wireOp",EDGE,"E12.54.8"),sQuery(id+"F0.wireOp",EDGE,"E12.54.9"),sQuery(id+"F0.wireOp",EDGE,"E12.55.0"),sQuery(id+"F0.wireOp",EDGE,"E12.55.1"),sQuery(id+"F0.wireOp",EDGE,"E12.55.2"),sQuery(id+"F0.wireOp",EDGE,"E12.55.3"),sQuery(id+"F0.wireOp",EDGE,"E12.55.4"),sQuery(id+"F0.wireOp",EDGE,"E12.55.5"),sQuery(id+"F0.wireOp",EDGE,"E12.55.6"),sQuery(id+"F0.wireOp",EDGE,"E12.55.7"),sQuery(id+"F0.wireOp",EDGE,"E12.55.8"),sQuery(id+"F0.wireOp",EDGE,"E12.55.9"),sQuery(id+"F0.wireOp",EDGE,"E12.56.0"),sQuery(id+"F0.wireOp",EDGE,"E12.56.1"),sQuery(id+"F0.wireOp",EDGE,"E12.56.2"),sQuery(id+"F0.wireOp",EDGE,"E12.56.3"),sQuery(id+"F0.wireOp",EDGE,"E12.56.4"),sQuery(id+"F0.wireOp",EDGE,"E12.56.5"),sQuery(id+"F0.wireOp",EDGE,"E12.56.6"),sQuery(id+"F0.wireOp",EDGE,"E12.56.7"),sQuery(id+"F0.wireOp",EDGE,"E12.56.8"),sQuery(id+"F0.wireOp",EDGE,"E12.56.9"),sQuery(id+"F0.wireOp",EDGE,"E12.57.0"),sQuery(id+"F0.wireOp",EDGE,"E12.57.1"),sQuery(id+"F0.wireOp",EDGE,"E12.57.2"),sQuery(id+"F0.wireOp",EDGE,"E12.57.3"),sQuery(id+"F0.wireOp",EDGE,"E12.57.4"),sQuery(id+"F0.wireOp",EDGE,"E12.57.5"),sQuery(id+"F0.wireOp",EDGE,"E12.57.6"),sQuery(id+"F0.wireOp",EDGE,"E12.57.7"),sQuery(id+"F0.wireOp",EDGE,"E12.57.8"),sQuery(id+"F0.wireOp",EDGE,"E12.57.9"),sQuery(id+"F0.wireOp",EDGE,"E12.58.0"),sQuery(id+"F0.wireOp",EDGE,"E12.58.1"),sQuery(id+"F0.wireOp",EDGE,"E12.58.2"),sQuery(id+"F0.wireOp",EDGE,"E12.58.3"),sQuery(id+"F0.wireOp",EDGE,"E12.58.4"),sQuery(id+"F0.wireOp",EDGE,"E12.58.5"),sQuery(id+"F0.wireOp",EDGE,"E12.58.6"),sQuery(id+"F0.wireOp",EDGE,"E12.58.7"),sQuery(id+"F0.wireOp",EDGE,"E12.58.8"),sQuery(id+"F0.wireOp",EDGE,"E12.58.9"),sQuery(id+"F0.wireOp",EDGE,"E12.59.0"),sQuery(id+"F0.wireOp",EDGE,"E12.59.1"),sQuery(id+"F0.wireOp",EDGE,"E12.59.2"),sQuery(id+"F0.wireOp",EDGE,"E12.59.3"),sQuery(id+"F0.wireOp",EDGE,"E12.59.4"),sQuery(id+"F0.wireOp",EDGE,"E12.59.5"),sQuery(id+"F0.wireOp",EDGE,"E12.59.6"),sQuery(id+"F0.wireOp",EDGE,"E12.59.7"),sQuery(id+"F0.wireOp",EDGE,"E12.59.8"),sQuery(id+"F0.wireOp",EDGE,"E12.59.9"),sQuery(id+"F0.wireOp",EDGE,"E13.trimOffspring"),sQuery(id+"F0.wireOp",EDGE,"E14.trimOffspring")])],"isStart":true}),makeQuery(id+"F3.opExtrude","SWEPT_FACE",FACE,{"disambiguationData":[OSD([sQuery(id+"F2.wireOp",EDGE,"E17.4.0")])]})]});
            var Q15;
            Q15=makeQuery(id+"F3.boolean.opBoolean","INTERSECT",EDGE,{"derivedFrom":[makeQuery(id+"F1.opExtrude","CAP_FACE",FACE,{"disambiguationData":[OSD([sQuery(id+"F0.wireOp",EDGE,"E0"),sQuery(id+"F0.wireOp",EDGE,"E2"),sQuery(id+"F0.wireOp",EDGE,"E3"),sQuery(id+"F0.wireOp",EDGE,"E4.trimOffspring"),sQuery(id+"F0.wireOp",EDGE,"E5.MirrorCS"),sQuery(id+"F0.wireOp",EDGE,"E6.MirrorCS"),sQuery(id+"F0.wireOp",EDGE,"E7.MirrorCS"),sQuery(id+"F0.wireOp",EDGE,"E8.filletArc"),sQuery(id+"F0.wireOp",EDGE,"E9.filletArc"),sQuery(id+"F0.wireOp",EDGE,"E10.filletArc"),sQuery(id+"F0.wireOp",EDGE,"E11.filletArc"),sQuery(id+"F0.wireOp",EDGE,"E12.1.0"),sQuery(id+"F0.wireOp",EDGE,"E12.1.1"),sQuery(id+"F0.wireOp",EDGE,"E12.1.2"),sQuery(id+"F0.wireOp",EDGE,"E12.1.3"),sQuery(id+"F0.wireOp",EDGE,"E12.1.4"),sQuery(id+"F0.wireOp",EDGE,"E12.1.5"),sQuery(id+"F0.wireOp",EDGE,"E12.1.6"),sQuery(id+"F0.wireOp",EDGE,"E12.1.7"),sQuery(id+"F0.wireOp",EDGE,"E12.1.8"),sQuery(id+"F0.wireOp",EDGE,"E12.1.9"),sQuery(id+"F0.wireOp",EDGE,"E12.2.0"),sQuery(id+"F0.wireOp",EDGE,"E12.2.1"),sQuery(id+"F0.wireOp",EDGE,"E12.2.2"),sQuery(id+"F0.wireOp",EDGE,"E12.2.3"),sQuery(id+"F0.wireOp",EDGE,"E12.2.4"),sQuery(id+"F0.wireOp",EDGE,"E12.2.5"),sQuery(id+"F0.wireOp",EDGE,"E12.2.6"),sQuery(id+"F0.wireOp",EDGE,"E12.2.7"),sQuery(id+"F0.wireOp",EDGE,"E12.2.8"),sQuery(id+"F0.wireOp",EDGE,"E12.2.9"),sQuery(id+"F0.wireOp",EDGE,"E12.3.0"),sQuery(id+"F0.wireOp",EDGE,"E12.3.1"),sQuery(id+"F0.wireOp",EDGE,"E12.3.2"),sQuery(id+"F0.wireOp",EDGE,"E12.3.3"),sQuery(id+"F0.wireOp",EDGE,"E12.3.4"),sQuery(id+"F0.wireOp",EDGE,"E12.3.5"),sQuery(id+"F0.wireOp",EDGE,"E12.3.6"),sQuery(id+"F0.wireOp",EDGE,"E12.3.7"),sQuery(id+"F0.wireOp",EDGE,"E12.3.8"),sQuery(id+"F0.wireOp",EDGE,"E12.3.9"),sQuery(id+"F0.wireOp",EDGE,"E12.4.0"),sQuery(id+"F0.wireOp",EDGE,"E12.4.1"),sQuery(id+"F0.wireOp",EDGE,"E12.4.2"),sQuery(id+"F0.wireOp",EDGE,"E12.4.3"),sQuery(id+"F0.wireOp",EDGE,"E12.4.4"),sQuery(id+"F0.wireOp",EDGE,"E12.4.5"),sQuery(id+"F0.wireOp",EDGE,"E12.4.6"),sQuery(id+"F0.wireOp",EDGE,"E12.4.7"),sQuery(id+"F0.wireOp",EDGE,"E12.4.8"),sQuery(id+"F0.wireOp",EDGE,"E12.4.9"),sQuery(id+"F0.wireOp",EDGE,"E12.5.0"),sQuery(id+"F0.wireOp",EDGE,"E12.5.1"),sQuery(id+"F0.wireOp",EDGE,"E12.5.2"),sQuery(id+"F0.wireOp",EDGE,"E12.5.3"),sQuery(id+"F0.wireOp",EDGE,"E12.5.4"),sQuery(id+"F0.wireOp",EDGE,"E12.5.5"),sQuery(id+"F0.wireOp",EDGE,"E12.5.6"),sQuery(id+"F0.wireOp",EDGE,"E12.5.7"),sQuery(id+"F0.wireOp",EDGE,"E12.5.8"),sQuery(id+"F0.wireOp",EDGE,"E12.5.9"),sQuery(id+"F0.wireOp",EDGE,"E12.6.0"),sQuery(id+"F0.wireOp",EDGE,"E12.6.1"),sQuery(id+"F0.wireOp",EDGE,"E12.6.2"),sQuery(id+"F0.wireOp",EDGE,"E12.6.3"),sQuery(id+"F0.wireOp",EDGE,"E12.6.4"),sQuery(id+"F0.wireOp",EDGE,"E12.6.5"),sQuery(id+"F0.wireOp",EDGE,"E12.6.6"),sQuery(id+"F0.wireOp",EDGE,"E12.6.7"),sQuery(id+"F0.wireOp",EDGE,"E12.6.8"),sQuery(id+"F0.wireOp",EDGE,"E12.6.9"),sQuery(id+"F0.wireOp",EDGE,"E12.7.0"),sQuery(id+"F0.wireOp",EDGE,"E12.7.1"),sQuery(id+"F0.wireOp",EDGE,"E12.7.2"),sQuery(id+"F0.wireOp",EDGE,"E12.7.3"),sQuery(id+"F0.wireOp",EDGE,"E12.7.4"),sQuery(id+"F0.wireOp",EDGE,"E12.7.5"),sQuery(id+"F0.wireOp",EDGE,"E12.7.6"),sQuery(id+"F0.wireOp",EDGE,"E12.7.7"),sQuery(id+"F0.wireOp",EDGE,"E12.7.8"),sQuery(id+"F0.wireOp",EDGE,"E12.7.9"),sQuery(id+"F0.wireOp",EDGE,"E12.8.0"),sQuery(id+"F0.wireOp",EDGE,"E12.8.1"),sQuery(id+"F0.wireOp",EDGE,"E12.8.2"),sQuery(id+"F0.wireOp",EDGE,"E12.8.3"),sQuery(id+"F0.wireOp",EDGE,"E12.8.4"),sQuery(id+"F0.wireOp",EDGE,"E12.8.5"),sQuery(id+"F0.wireOp",EDGE,"E12.8.6"),sQuery(id+"F0.wireOp",EDGE,"E12.8.7"),sQuery(id+"F0.wireOp",EDGE,"E12.8.8"),sQuery(id+"F0.wireOp",EDGE,"E12.8.9"),sQuery(id+"F0.wireOp",EDGE,"E12.9.0"),sQuery(id+"F0.wireOp",EDGE,"E12.9.1"),sQuery(id+"F0.wireOp",EDGE,"E12.9.2"),sQuery(id+"F0.wireOp",EDGE,"E12.9.3"),sQuery(id+"F0.wireOp",EDGE,"E12.9.4"),sQuery(id+"F0.wireOp",EDGE,"E12.9.5"),sQuery(id+"F0.wireOp",EDGE,"E12.9.6"),sQuery(id+"F0.wireOp",EDGE,"E12.9.7"),sQuery(id+"F0.wireOp",EDGE,"E12.9.8"),sQuery(id+"F0.wireOp",EDGE,"E12.9.9"),sQuery(id+"F0.wireOp",EDGE,"E12.10.0"),sQuery(id+"F0.wireOp",EDGE,"E12.10.1"),sQuery(id+"F0.wireOp",EDGE,"E12.10.2"),sQuery(id+"F0.wireOp",EDGE,"E12.10.3"),sQuery(id+"F0.wireOp",EDGE,"E12.10.4"),sQuery(id+"F0.wireOp",EDGE,"E12.10.5"),sQuery(id+"F0.wireOp",EDGE,"E12.10.6"),sQuery(id+"F0.wireOp",EDGE,"E12.10.7"),sQuery(id+"F0.wireOp",EDGE,"E12.10.8"),sQuery(id+"F0.wireOp",EDGE,"E12.10.9"),sQuery(id+"F0.wireOp",EDGE,"E12.11.0"),sQuery(id+"F0.wireOp",EDGE,"E12.11.1"),sQuery(id+"F0.wireOp",EDGE,"E12.11.2"),sQuery(id+"F0.wireOp",EDGE,"E12.11.3"),sQuery(id+"F0.wireOp",EDGE,"E12.11.4"),sQuery(id+"F0.wireOp",EDGE,"E12.11.5"),sQuery(id+"F0.wireOp",EDGE,"E12.11.6"),sQuery(id+"F0.wireOp",EDGE,"E12.11.7"),sQuery(id+"F0.wireOp",EDGE,"E12.11.8"),sQuery(id+"F0.wireOp",EDGE,"E12.11.9"),sQuery(id+"F0.wireOp",EDGE,"E12.12.0"),sQuery(id+"F0.wireOp",EDGE,"E12.12.1"),sQuery(id+"F0.wireOp",EDGE,"E12.12.2"),sQuery(id+"F0.wireOp",EDGE,"E12.12.3"),sQuery(id+"F0.wireOp",EDGE,"E12.12.4"),sQuery(id+"F0.wireOp",EDGE,"E12.12.5"),sQuery(id+"F0.wireOp",EDGE,"E12.12.6"),sQuery(id+"F0.wireOp",EDGE,"E12.12.7"),sQuery(id+"F0.wireOp",EDGE,"E12.12.8"),sQuery(id+"F0.wireOp",EDGE,"E12.12.9"),sQuery(id+"F0.wireOp",EDGE,"E12.13.0"),sQuery(id+"F0.wireOp",EDGE,"E12.13.1"),sQuery(id+"F0.wireOp",EDGE,"E12.13.2"),sQuery(id+"F0.wireOp",EDGE,"E12.13.3"),sQuery(id+"F0.wireOp",EDGE,"E12.13.4"),sQuery(id+"F0.wireOp",EDGE,"E12.13.5"),sQuery(id+"F0.wireOp",EDGE,"E12.13.6"),sQuery(id+"F0.wireOp",EDGE,"E12.13.7"),sQuery(id+"F0.wireOp",EDGE,"E12.13.8"),sQuery(id+"F0.wireOp",EDGE,"E12.13.9"),sQuery(id+"F0.wireOp",EDGE,"E12.14.0"),sQuery(id+"F0.wireOp",EDGE,"E12.14.1"),sQuery(id+"F0.wireOp",EDGE,"E12.14.2"),sQuery(id+"F0.wireOp",EDGE,"E12.14.3"),sQuery(id+"F0.wireOp",EDGE,"E12.14.4"),sQuery(id+"F0.wireOp",EDGE,"E12.14.5"),sQuery(id+"F0.wireOp",EDGE,"E12.14.6"),sQuery(id+"F0.wireOp",EDGE,"E12.14.7"),sQuery(id+"F0.wireOp",EDGE,"E12.14.8"),sQuery(id+"F0.wireOp",EDGE,"E12.14.9"),sQuery(id+"F0.wireOp",EDGE,"E12.15.0"),sQuery(id+"F0.wireOp",EDGE,"E12.15.1"),sQuery(id+"F0.wireOp",EDGE,"E12.15.2"),sQuery(id+"F0.wireOp",EDGE,"E12.15.3"),sQuery(id+"F0.wireOp",EDGE,"E12.15.4"),sQuery(id+"F0.wireOp",EDGE,"E12.15.5"),sQuery(id+"F0.wireOp",EDGE,"E12.15.6"),sQuery(id+"F0.wireOp",EDGE,"E12.15.7"),sQuery(id+"F0.wireOp",EDGE,"E12.15.8"),sQuery(id+"F0.wireOp",EDGE,"E12.15.9"),sQuery(id+"F0.wireOp",EDGE,"E12.16.0"),sQuery(id+"F0.wireOp",EDGE,"E12.16.1"),sQuery(id+"F0.wireOp",EDGE,"E12.16.2"),sQuery(id+"F0.wireOp",EDGE,"E12.16.3"),sQuery(id+"F0.wireOp",EDGE,"E12.16.4"),sQuery(id+"F0.wireOp",EDGE,"E12.16.5"),sQuery(id+"F0.wireOp",EDGE,"E12.16.6"),sQuery(id+"F0.wireOp",EDGE,"E12.16.7"),sQuery(id+"F0.wireOp",EDGE,"E12.16.8"),sQuery(id+"F0.wireOp",EDGE,"E12.16.9"),sQuery(id+"F0.wireOp",EDGE,"E12.17.0"),sQuery(id+"F0.wireOp",EDGE,"E12.17.1"),sQuery(id+"F0.wireOp",EDGE,"E12.17.2"),sQuery(id+"F0.wireOp",EDGE,"E12.17.3"),sQuery(id+"F0.wireOp",EDGE,"E12.17.4"),sQuery(id+"F0.wireOp",EDGE,"E12.17.5"),sQuery(id+"F0.wireOp",EDGE,"E12.17.6"),sQuery(id+"F0.wireOp",EDGE,"E12.17.7"),sQuery(id+"F0.wireOp",EDGE,"E12.17.8"),sQuery(id+"F0.wireOp",EDGE,"E12.17.9"),sQuery(id+"F0.wireOp",EDGE,"E12.18.0"),sQuery(id+"F0.wireOp",EDGE,"E12.18.1"),sQuery(id+"F0.wireOp",EDGE,"E12.18.2"),sQuery(id+"F0.wireOp",EDGE,"E12.18.3"),sQuery(id+"F0.wireOp",EDGE,"E12.18.4"),sQuery(id+"F0.wireOp",EDGE,"E12.18.5"),sQuery(id+"F0.wireOp",EDGE,"E12.18.6"),sQuery(id+"F0.wireOp",EDGE,"E12.18.7"),sQuery(id+"F0.wireOp",EDGE,"E12.18.8"),sQuery(id+"F0.wireOp",EDGE,"E12.18.9"),sQuery(id+"F0.wireOp",EDGE,"E12.19.0"),sQuery(id+"F0.wireOp",EDGE,"E12.19.1"),sQuery(id+"F0.wireOp",EDGE,"E12.19.2"),sQuery(id+"F0.wireOp",EDGE,"E12.19.3"),sQuery(id+"F0.wireOp",EDGE,"E12.19.4"),sQuery(id+"F0.wireOp",EDGE,"E12.19.5"),sQuery(id+"F0.wireOp",EDGE,"E12.19.6"),sQuery(id+"F0.wireOp",EDGE,"E12.19.7"),sQuery(id+"F0.wireOp",EDGE,"E12.19.8"),sQuery(id+"F0.wireOp",EDGE,"E12.19.9"),sQuery(id+"F0.wireOp",EDGE,"E12.20.0"),sQuery(id+"F0.wireOp",EDGE,"E12.20.1"),sQuery(id+"F0.wireOp",EDGE,"E12.20.2"),sQuery(id+"F0.wireOp",EDGE,"E12.20.3"),sQuery(id+"F0.wireOp",EDGE,"E12.20.4"),sQuery(id+"F0.wireOp",EDGE,"E12.20.5"),sQuery(id+"F0.wireOp",EDGE,"E12.20.6"),sQuery(id+"F0.wireOp",EDGE,"E12.20.7"),sQuery(id+"F0.wireOp",EDGE,"E12.20.8"),sQuery(id+"F0.wireOp",EDGE,"E12.20.9"),sQuery(id+"F0.wireOp",EDGE,"E12.21.0"),sQuery(id+"F0.wireOp",EDGE,"E12.21.1"),sQuery(id+"F0.wireOp",EDGE,"E12.21.2"),sQuery(id+"F0.wireOp",EDGE,"E12.21.3"),sQuery(id+"F0.wireOp",EDGE,"E12.21.4"),sQuery(id+"F0.wireOp",EDGE,"E12.21.5"),sQuery(id+"F0.wireOp",EDGE,"E12.21.6"),sQuery(id+"F0.wireOp",EDGE,"E12.21.7"),sQuery(id+"F0.wireOp",EDGE,"E12.21.8"),sQuery(id+"F0.wireOp",EDGE,"E12.21.9"),sQuery(id+"F0.wireOp",EDGE,"E12.22.0"),sQuery(id+"F0.wireOp",EDGE,"E12.22.1"),sQuery(id+"F0.wireOp",EDGE,"E12.22.2"),sQuery(id+"F0.wireOp",EDGE,"E12.22.3"),sQuery(id+"F0.wireOp",EDGE,"E12.22.4"),sQuery(id+"F0.wireOp",EDGE,"E12.22.5"),sQuery(id+"F0.wireOp",EDGE,"E12.22.6"),sQuery(id+"F0.wireOp",EDGE,"E12.22.7"),sQuery(id+"F0.wireOp",EDGE,"E12.22.8"),sQuery(id+"F0.wireOp",EDGE,"E12.22.9"),sQuery(id+"F0.wireOp",EDGE,"E12.23.0"),sQuery(id+"F0.wireOp",EDGE,"E12.23.1"),sQuery(id+"F0.wireOp",EDGE,"E12.23.2"),sQuery(id+"F0.wireOp",EDGE,"E12.23.3"),sQuery(id+"F0.wireOp",EDGE,"E12.23.4"),sQuery(id+"F0.wireOp",EDGE,"E12.23.5"),sQuery(id+"F0.wireOp",EDGE,"E12.23.6"),sQuery(id+"F0.wireOp",EDGE,"E12.23.7"),sQuery(id+"F0.wireOp",EDGE,"E12.23.8"),sQuery(id+"F0.wireOp",EDGE,"E12.23.9"),sQuery(id+"F0.wireOp",EDGE,"E12.24.0"),sQuery(id+"F0.wireOp",EDGE,"E12.24.1"),sQuery(id+"F0.wireOp",EDGE,"E12.24.2"),sQuery(id+"F0.wireOp",EDGE,"E12.24.3"),sQuery(id+"F0.wireOp",EDGE,"E12.24.4"),sQuery(id+"F0.wireOp",EDGE,"E12.24.5"),sQuery(id+"F0.wireOp",EDGE,"E12.24.6"),sQuery(id+"F0.wireOp",EDGE,"E12.24.7"),sQuery(id+"F0.wireOp",EDGE,"E12.24.8"),sQuery(id+"F0.wireOp",EDGE,"E12.24.9"),sQuery(id+"F0.wireOp",EDGE,"E12.25.0"),sQuery(id+"F0.wireOp",EDGE,"E12.25.1"),sQuery(id+"F0.wireOp",EDGE,"E12.25.2"),sQuery(id+"F0.wireOp",EDGE,"E12.25.3"),sQuery(id+"F0.wireOp",EDGE,"E12.25.4"),sQuery(id+"F0.wireOp",EDGE,"E12.25.5"),sQuery(id+"F0.wireOp",EDGE,"E12.25.6"),sQuery(id+"F0.wireOp",EDGE,"E12.25.7"),sQuery(id+"F0.wireOp",EDGE,"E12.25.8"),sQuery(id+"F0.wireOp",EDGE,"E12.25.9"),sQuery(id+"F0.wireOp",EDGE,"E12.26.0"),sQuery(id+"F0.wireOp",EDGE,"E12.26.1"),sQuery(id+"F0.wireOp",EDGE,"E12.26.2"),sQuery(id+"F0.wireOp",EDGE,"E12.26.3"),sQuery(id+"F0.wireOp",EDGE,"E12.26.4"),sQuery(id+"F0.wireOp",EDGE,"E12.26.5"),sQuery(id+"F0.wireOp",EDGE,"E12.26.6"),sQuery(id+"F0.wireOp",EDGE,"E12.26.7"),sQuery(id+"F0.wireOp",EDGE,"E12.26.8"),sQuery(id+"F0.wireOp",EDGE,"E12.26.9"),sQuery(id+"F0.wireOp",EDGE,"E12.27.0"),sQuery(id+"F0.wireOp",EDGE,"E12.27.1"),sQuery(id+"F0.wireOp",EDGE,"E12.27.2"),sQuery(id+"F0.wireOp",EDGE,"E12.27.3"),sQuery(id+"F0.wireOp",EDGE,"E12.27.4"),sQuery(id+"F0.wireOp",EDGE,"E12.27.5"),sQuery(id+"F0.wireOp",EDGE,"E12.27.6"),sQuery(id+"F0.wireOp",EDGE,"E12.27.7"),sQuery(id+"F0.wireOp",EDGE,"E12.27.8"),sQuery(id+"F0.wireOp",EDGE,"E12.27.9"),sQuery(id+"F0.wireOp",EDGE,"E12.28.0"),sQuery(id+"F0.wireOp",EDGE,"E12.28.1"),sQuery(id+"F0.wireOp",EDGE,"E12.28.2"),sQuery(id+"F0.wireOp",EDGE,"E12.28.3"),sQuery(id+"F0.wireOp",EDGE,"E12.28.4"),sQuery(id+"F0.wireOp",EDGE,"E12.28.5"),sQuery(id+"F0.wireOp",EDGE,"E12.28.6"),sQuery(id+"F0.wireOp",EDGE,"E12.28.7"),sQuery(id+"F0.wireOp",EDGE,"E12.28.8"),sQuery(id+"F0.wireOp",EDGE,"E12.28.9"),sQuery(id+"F0.wireOp",EDGE,"E12.29.0"),sQuery(id+"F0.wireOp",EDGE,"E12.29.1"),sQuery(id+"F0.wireOp",EDGE,"E12.29.2"),sQuery(id+"F0.wireOp",EDGE,"E12.29.3"),sQuery(id+"F0.wireOp",EDGE,"E12.29.4"),sQuery(id+"F0.wireOp",EDGE,"E12.29.5"),sQuery(id+"F0.wireOp",EDGE,"E12.29.6"),sQuery(id+"F0.wireOp",EDGE,"E12.29.7"),sQuery(id+"F0.wireOp",EDGE,"E12.29.8"),sQuery(id+"F0.wireOp",EDGE,"E12.29.9"),sQuery(id+"F0.wireOp",EDGE,"E12.30.0"),sQuery(id+"F0.wireOp",EDGE,"E12.30.1"),sQuery(id+"F0.wireOp",EDGE,"E12.30.2"),sQuery(id+"F0.wireOp",EDGE,"E12.30.3"),sQuery(id+"F0.wireOp",EDGE,"E12.30.4"),sQuery(id+"F0.wireOp",EDGE,"E12.30.5"),sQuery(id+"F0.wireOp",EDGE,"E12.30.6"),sQuery(id+"F0.wireOp",EDGE,"E12.30.7"),sQuery(id+"F0.wireOp",EDGE,"E12.30.8"),sQuery(id+"F0.wireOp",EDGE,"E12.30.9"),sQuery(id+"F0.wireOp",EDGE,"E12.31.0"),sQuery(id+"F0.wireOp",EDGE,"E12.31.1"),sQuery(id+"F0.wireOp",EDGE,"E12.31.2"),sQuery(id+"F0.wireOp",EDGE,"E12.31.3"),sQuery(id+"F0.wireOp",EDGE,"E12.31.4"),sQuery(id+"F0.wireOp",EDGE,"E12.31.5"),sQuery(id+"F0.wireOp",EDGE,"E12.31.6"),sQuery(id+"F0.wireOp",EDGE,"E12.31.7"),sQuery(id+"F0.wireOp",EDGE,"E12.31.8"),sQuery(id+"F0.wireOp",EDGE,"E12.31.9"),sQuery(id+"F0.wireOp",EDGE,"E12.32.0"),sQuery(id+"F0.wireOp",EDGE,"E12.32.1"),sQuery(id+"F0.wireOp",EDGE,"E12.32.2"),sQuery(id+"F0.wireOp",EDGE,"E12.32.3"),sQuery(id+"F0.wireOp",EDGE,"E12.32.4"),sQuery(id+"F0.wireOp",EDGE,"E12.32.5"),sQuery(id+"F0.wireOp",EDGE,"E12.32.6"),sQuery(id+"F0.wireOp",EDGE,"E12.32.7"),sQuery(id+"F0.wireOp",EDGE,"E12.32.8"),sQuery(id+"F0.wireOp",EDGE,"E12.32.9"),sQuery(id+"F0.wireOp",EDGE,"E12.33.0"),sQuery(id+"F0.wireOp",EDGE,"E12.33.1"),sQuery(id+"F0.wireOp",EDGE,"E12.33.2"),sQuery(id+"F0.wireOp",EDGE,"E12.33.3"),sQuery(id+"F0.wireOp",EDGE,"E12.33.4"),sQuery(id+"F0.wireOp",EDGE,"E12.33.5"),sQuery(id+"F0.wireOp",EDGE,"E12.33.6"),sQuery(id+"F0.wireOp",EDGE,"E12.33.7"),sQuery(id+"F0.wireOp",EDGE,"E12.33.8"),sQuery(id+"F0.wireOp",EDGE,"E12.33.9"),sQuery(id+"F0.wireOp",EDGE,"E12.34.0"),sQuery(id+"F0.wireOp",EDGE,"E12.34.1"),sQuery(id+"F0.wireOp",EDGE,"E12.34.2"),sQuery(id+"F0.wireOp",EDGE,"E12.34.3"),sQuery(id+"F0.wireOp",EDGE,"E12.34.4"),sQuery(id+"F0.wireOp",EDGE,"E12.34.5"),sQuery(id+"F0.wireOp",EDGE,"E12.34.6"),sQuery(id+"F0.wireOp",EDGE,"E12.34.7"),sQuery(id+"F0.wireOp",EDGE,"E12.34.8"),sQuery(id+"F0.wireOp",EDGE,"E12.34.9"),sQuery(id+"F0.wireOp",EDGE,"E12.35.0"),sQuery(id+"F0.wireOp",EDGE,"E12.35.1"),sQuery(id+"F0.wireOp",EDGE,"E12.35.2"),sQuery(id+"F0.wireOp",EDGE,"E12.35.3"),sQuery(id+"F0.wireOp",EDGE,"E12.35.4"),sQuery(id+"F0.wireOp",EDGE,"E12.35.5"),sQuery(id+"F0.wireOp",EDGE,"E12.35.6"),sQuery(id+"F0.wireOp",EDGE,"E12.35.7"),sQuery(id+"F0.wireOp",EDGE,"E12.35.8"),sQuery(id+"F0.wireOp",EDGE,"E12.35.9"),sQuery(id+"F0.wireOp",EDGE,"E12.36.0"),sQuery(id+"F0.wireOp",EDGE,"E12.36.1"),sQuery(id+"F0.wireOp",EDGE,"E12.36.2"),sQuery(id+"F0.wireOp",EDGE,"E12.36.3"),sQuery(id+"F0.wireOp",EDGE,"E12.36.4"),sQuery(id+"F0.wireOp",EDGE,"E12.36.5"),sQuery(id+"F0.wireOp",EDGE,"E12.36.6"),sQuery(id+"F0.wireOp",EDGE,"E12.36.7"),sQuery(id+"F0.wireOp",EDGE,"E12.36.8"),sQuery(id+"F0.wireOp",EDGE,"E12.36.9"),sQuery(id+"F0.wireOp",EDGE,"E12.37.0"),sQuery(id+"F0.wireOp",EDGE,"E12.37.1"),sQuery(id+"F0.wireOp",EDGE,"E12.37.2"),sQuery(id+"F0.wireOp",EDGE,"E12.37.3"),sQuery(id+"F0.wireOp",EDGE,"E12.37.4"),sQuery(id+"F0.wireOp",EDGE,"E12.37.5"),sQuery(id+"F0.wireOp",EDGE,"E12.37.6"),sQuery(id+"F0.wireOp",EDGE,"E12.37.7"),sQuery(id+"F0.wireOp",EDGE,"E12.37.8"),sQuery(id+"F0.wireOp",EDGE,"E12.37.9"),sQuery(id+"F0.wireOp",EDGE,"E12.38.0"),sQuery(id+"F0.wireOp",EDGE,"E12.38.1"),sQuery(id+"F0.wireOp",EDGE,"E12.38.2"),sQuery(id+"F0.wireOp",EDGE,"E12.38.3"),sQuery(id+"F0.wireOp",EDGE,"E12.38.4"),sQuery(id+"F0.wireOp",EDGE,"E12.38.5"),sQuery(id+"F0.wireOp",EDGE,"E12.38.6"),sQuery(id+"F0.wireOp",EDGE,"E12.38.7"),sQuery(id+"F0.wireOp",EDGE,"E12.38.8"),sQuery(id+"F0.wireOp",EDGE,"E12.38.9"),sQuery(id+"F0.wireOp",EDGE,"E12.39.0"),sQuery(id+"F0.wireOp",EDGE,"E12.39.1"),sQuery(id+"F0.wireOp",EDGE,"E12.39.2"),sQuery(id+"F0.wireOp",EDGE,"E12.39.3"),sQuery(id+"F0.wireOp",EDGE,"E12.39.4"),sQuery(id+"F0.wireOp",EDGE,"E12.39.5"),sQuery(id+"F0.wireOp",EDGE,"E12.39.6"),sQuery(id+"F0.wireOp",EDGE,"E12.39.7"),sQuery(id+"F0.wireOp",EDGE,"E12.39.8"),sQuery(id+"F0.wireOp",EDGE,"E12.39.9"),sQuery(id+"F0.wireOp",EDGE,"E12.40.0"),sQuery(id+"F0.wireOp",EDGE,"E12.40.1"),sQuery(id+"F0.wireOp",EDGE,"E12.40.2"),sQuery(id+"F0.wireOp",EDGE,"E12.40.3"),sQuery(id+"F0.wireOp",EDGE,"E12.40.4"),sQuery(id+"F0.wireOp",EDGE,"E12.40.5"),sQuery(id+"F0.wireOp",EDGE,"E12.40.6"),sQuery(id+"F0.wireOp",EDGE,"E12.40.7"),sQuery(id+"F0.wireOp",EDGE,"E12.40.8"),sQuery(id+"F0.wireOp",EDGE,"E12.40.9"),sQuery(id+"F0.wireOp",EDGE,"E12.41.0"),sQuery(id+"F0.wireOp",EDGE,"E12.41.1"),sQuery(id+"F0.wireOp",EDGE,"E12.41.2"),sQuery(id+"F0.wireOp",EDGE,"E12.41.3"),sQuery(id+"F0.wireOp",EDGE,"E12.41.4"),sQuery(id+"F0.wireOp",EDGE,"E12.41.5"),sQuery(id+"F0.wireOp",EDGE,"E12.41.6"),sQuery(id+"F0.wireOp",EDGE,"E12.41.7"),sQuery(id+"F0.wireOp",EDGE,"E12.41.8"),sQuery(id+"F0.wireOp",EDGE,"E12.41.9"),sQuery(id+"F0.wireOp",EDGE,"E12.42.0"),sQuery(id+"F0.wireOp",EDGE,"E12.42.1"),sQuery(id+"F0.wireOp",EDGE,"E12.42.2"),sQuery(id+"F0.wireOp",EDGE,"E12.42.3"),sQuery(id+"F0.wireOp",EDGE,"E12.42.4"),sQuery(id+"F0.wireOp",EDGE,"E12.42.5"),sQuery(id+"F0.wireOp",EDGE,"E12.42.6"),sQuery(id+"F0.wireOp",EDGE,"E12.42.7"),sQuery(id+"F0.wireOp",EDGE,"E12.42.8"),sQuery(id+"F0.wireOp",EDGE,"E12.42.9"),sQuery(id+"F0.wireOp",EDGE,"E12.43.0"),sQuery(id+"F0.wireOp",EDGE,"E12.43.1"),sQuery(id+"F0.wireOp",EDGE,"E12.43.2"),sQuery(id+"F0.wireOp",EDGE,"E12.43.3"),sQuery(id+"F0.wireOp",EDGE,"E12.43.4"),sQuery(id+"F0.wireOp",EDGE,"E12.43.5"),sQuery(id+"F0.wireOp",EDGE,"E12.43.6"),sQuery(id+"F0.wireOp",EDGE,"E12.43.7"),sQuery(id+"F0.wireOp",EDGE,"E12.43.8"),sQuery(id+"F0.wireOp",EDGE,"E12.43.9"),sQuery(id+"F0.wireOp",EDGE,"E12.44.0"),sQuery(id+"F0.wireOp",EDGE,"E12.44.1"),sQuery(id+"F0.wireOp",EDGE,"E12.44.2"),sQuery(id+"F0.wireOp",EDGE,"E12.44.3"),sQuery(id+"F0.wireOp",EDGE,"E12.44.4"),sQuery(id+"F0.wireOp",EDGE,"E12.44.5"),sQuery(id+"F0.wireOp",EDGE,"E12.44.6"),sQuery(id+"F0.wireOp",EDGE,"E12.44.7"),sQuery(id+"F0.wireOp",EDGE,"E12.44.8"),sQuery(id+"F0.wireOp",EDGE,"E12.44.9"),sQuery(id+"F0.wireOp",EDGE,"E12.45.0"),sQuery(id+"F0.wireOp",EDGE,"E12.45.1"),sQuery(id+"F0.wireOp",EDGE,"E12.45.2"),sQuery(id+"F0.wireOp",EDGE,"E12.45.3"),sQuery(id+"F0.wireOp",EDGE,"E12.45.4"),sQuery(id+"F0.wireOp",EDGE,"E12.45.5"),sQuery(id+"F0.wireOp",EDGE,"E12.45.6"),sQuery(id+"F0.wireOp",EDGE,"E12.45.7"),sQuery(id+"F0.wireOp",EDGE,"E12.45.8"),sQuery(id+"F0.wireOp",EDGE,"E12.45.9"),sQuery(id+"F0.wireOp",EDGE,"E12.46.0"),sQuery(id+"F0.wireOp",EDGE,"E12.46.1"),sQuery(id+"F0.wireOp",EDGE,"E12.46.2"),sQuery(id+"F0.wireOp",EDGE,"E12.46.3"),sQuery(id+"F0.wireOp",EDGE,"E12.46.4"),sQuery(id+"F0.wireOp",EDGE,"E12.46.5"),sQuery(id+"F0.wireOp",EDGE,"E12.46.6"),sQuery(id+"F0.wireOp",EDGE,"E12.46.7"),sQuery(id+"F0.wireOp",EDGE,"E12.46.8"),sQuery(id+"F0.wireOp",EDGE,"E12.46.9"),sQuery(id+"F0.wireOp",EDGE,"E12.47.0"),sQuery(id+"F0.wireOp",EDGE,"E12.47.1"),sQuery(id+"F0.wireOp",EDGE,"E12.47.2"),sQuery(id+"F0.wireOp",EDGE,"E12.47.3"),sQuery(id+"F0.wireOp",EDGE,"E12.47.4"),sQuery(id+"F0.wireOp",EDGE,"E12.47.5"),sQuery(id+"F0.wireOp",EDGE,"E12.47.6"),sQuery(id+"F0.wireOp",EDGE,"E12.47.7"),sQuery(id+"F0.wireOp",EDGE,"E12.47.8"),sQuery(id+"F0.wireOp",EDGE,"E12.47.9"),sQuery(id+"F0.wireOp",EDGE,"E12.48.0"),sQuery(id+"F0.wireOp",EDGE,"E12.48.1"),sQuery(id+"F0.wireOp",EDGE,"E12.48.2"),sQuery(id+"F0.wireOp",EDGE,"E12.48.3"),sQuery(id+"F0.wireOp",EDGE,"E12.48.4"),sQuery(id+"F0.wireOp",EDGE,"E12.48.5"),sQuery(id+"F0.wireOp",EDGE,"E12.48.6"),sQuery(id+"F0.wireOp",EDGE,"E12.48.7"),sQuery(id+"F0.wireOp",EDGE,"E12.48.8"),sQuery(id+"F0.wireOp",EDGE,"E12.48.9"),sQuery(id+"F0.wireOp",EDGE,"E12.49.0"),sQuery(id+"F0.wireOp",EDGE,"E12.49.1"),sQuery(id+"F0.wireOp",EDGE,"E12.49.2"),sQuery(id+"F0.wireOp",EDGE,"E12.49.3"),sQuery(id+"F0.wireOp",EDGE,"E12.49.4"),sQuery(id+"F0.wireOp",EDGE,"E12.49.5"),sQuery(id+"F0.wireOp",EDGE,"E12.49.6"),sQuery(id+"F0.wireOp",EDGE,"E12.49.7"),sQuery(id+"F0.wireOp",EDGE,"E12.49.8"),sQuery(id+"F0.wireOp",EDGE,"E12.49.9"),sQuery(id+"F0.wireOp",EDGE,"E12.50.0"),sQuery(id+"F0.wireOp",EDGE,"E12.50.1"),sQuery(id+"F0.wireOp",EDGE,"E12.50.2"),sQuery(id+"F0.wireOp",EDGE,"E12.50.3"),sQuery(id+"F0.wireOp",EDGE,"E12.50.4"),sQuery(id+"F0.wireOp",EDGE,"E12.50.5"),sQuery(id+"F0.wireOp",EDGE,"E12.50.6"),sQuery(id+"F0.wireOp",EDGE,"E12.50.7"),sQuery(id+"F0.wireOp",EDGE,"E12.50.8"),sQuery(id+"F0.wireOp",EDGE,"E12.50.9"),sQuery(id+"F0.wireOp",EDGE,"E12.51.0"),sQuery(id+"F0.wireOp",EDGE,"E12.51.1"),sQuery(id+"F0.wireOp",EDGE,"E12.51.2"),sQuery(id+"F0.wireOp",EDGE,"E12.51.3"),sQuery(id+"F0.wireOp",EDGE,"E12.51.4"),sQuery(id+"F0.wireOp",EDGE,"E12.51.5"),sQuery(id+"F0.wireOp",EDGE,"E12.51.6"),sQuery(id+"F0.wireOp",EDGE,"E12.51.7"),sQuery(id+"F0.wireOp",EDGE,"E12.51.8"),sQuery(id+"F0.wireOp",EDGE,"E12.51.9"),sQuery(id+"F0.wireOp",EDGE,"E12.52.0"),sQuery(id+"F0.wireOp",EDGE,"E12.52.1"),sQuery(id+"F0.wireOp",EDGE,"E12.52.2"),sQuery(id+"F0.wireOp",EDGE,"E12.52.3"),sQuery(id+"F0.wireOp",EDGE,"E12.52.4"),sQuery(id+"F0.wireOp",EDGE,"E12.52.5"),sQuery(id+"F0.wireOp",EDGE,"E12.52.6"),sQuery(id+"F0.wireOp",EDGE,"E12.52.7"),sQuery(id+"F0.wireOp",EDGE,"E12.52.8"),sQuery(id+"F0.wireOp",EDGE,"E12.52.9"),sQuery(id+"F0.wireOp",EDGE,"E12.53.0"),sQuery(id+"F0.wireOp",EDGE,"E12.53.1"),sQuery(id+"F0.wireOp",EDGE,"E12.53.2"),sQuery(id+"F0.wireOp",EDGE,"E12.53.3"),sQuery(id+"F0.wireOp",EDGE,"E12.53.4"),sQuery(id+"F0.wireOp",EDGE,"E12.53.5"),sQuery(id+"F0.wireOp",EDGE,"E12.53.6"),sQuery(id+"F0.wireOp",EDGE,"E12.53.7"),sQuery(id+"F0.wireOp",EDGE,"E12.53.8"),sQuery(id+"F0.wireOp",EDGE,"E12.53.9"),sQuery(id+"F0.wireOp",EDGE,"E12.54.0"),sQuery(id+"F0.wireOp",EDGE,"E12.54.1"),sQuery(id+"F0.wireOp",EDGE,"E12.54.2"),sQuery(id+"F0.wireOp",EDGE,"E12.54.3"),sQuery(id+"F0.wireOp",EDGE,"E12.54.4"),sQuery(id+"F0.wireOp",EDGE,"E12.54.5"),sQuery(id+"F0.wireOp",EDGE,"E12.54.6"),sQuery(id+"F0.wireOp",EDGE,"E12.54.7"),sQuery(id+"F0.wireOp",EDGE,"E12.54.8"),sQuery(id+"F0.wireOp",EDGE,"E12.54.9"),sQuery(id+"F0.wireOp",EDGE,"E12.55.0"),sQuery(id+"F0.wireOp",EDGE,"E12.55.1"),sQuery(id+"F0.wireOp",EDGE,"E12.55.2"),sQuery(id+"F0.wireOp",EDGE,"E12.55.3"),sQuery(id+"F0.wireOp",EDGE,"E12.55.4"),sQuery(id+"F0.wireOp",EDGE,"E12.55.5"),sQuery(id+"F0.wireOp",EDGE,"E12.55.6"),sQuery(id+"F0.wireOp",EDGE,"E12.55.7"),sQuery(id+"F0.wireOp",EDGE,"E12.55.8"),sQuery(id+"F0.wireOp",EDGE,"E12.55.9"),sQuery(id+"F0.wireOp",EDGE,"E12.56.0"),sQuery(id+"F0.wireOp",EDGE,"E12.56.1"),sQuery(id+"F0.wireOp",EDGE,"E12.56.2"),sQuery(id+"F0.wireOp",EDGE,"E12.56.3"),sQuery(id+"F0.wireOp",EDGE,"E12.56.4"),sQuery(id+"F0.wireOp",EDGE,"E12.56.5"),sQuery(id+"F0.wireOp",EDGE,"E12.56.6"),sQuery(id+"F0.wireOp",EDGE,"E12.56.7"),sQuery(id+"F0.wireOp",EDGE,"E12.56.8"),sQuery(id+"F0.wireOp",EDGE,"E12.56.9"),sQuery(id+"F0.wireOp",EDGE,"E12.57.0"),sQuery(id+"F0.wireOp",EDGE,"E12.57.1"),sQuery(id+"F0.wireOp",EDGE,"E12.57.2"),sQuery(id+"F0.wireOp",EDGE,"E12.57.3"),sQuery(id+"F0.wireOp",EDGE,"E12.57.4"),sQuery(id+"F0.wireOp",EDGE,"E12.57.5"),sQuery(id+"F0.wireOp",EDGE,"E12.57.6"),sQuery(id+"F0.wireOp",EDGE,"E12.57.7"),sQuery(id+"F0.wireOp",EDGE,"E12.57.8"),sQuery(id+"F0.wireOp",EDGE,"E12.57.9"),sQuery(id+"F0.wireOp",EDGE,"E12.58.0"),sQuery(id+"F0.wireOp",EDGE,"E12.58.1"),sQuery(id+"F0.wireOp",EDGE,"E12.58.2"),sQuery(id+"F0.wireOp",EDGE,"E12.58.3"),sQuery(id+"F0.wireOp",EDGE,"E12.58.4"),sQuery(id+"F0.wireOp",EDGE,"E12.58.5"),sQuery(id+"F0.wireOp",EDGE,"E12.58.6"),sQuery(id+"F0.wireOp",EDGE,"E12.58.7"),sQuery(id+"F0.wireOp",EDGE,"E12.58.8"),sQuery(id+"F0.wireOp",EDGE,"E12.58.9"),sQuery(id+"F0.wireOp",EDGE,"E12.59.0"),sQuery(id+"F0.wireOp",EDGE,"E12.59.1"),sQuery(id+"F0.wireOp",EDGE,"E12.59.2"),sQuery(id+"F0.wireOp",EDGE,"E12.59.3"),sQuery(id+"F0.wireOp",EDGE,"E12.59.4"),sQuery(id+"F0.wireOp",EDGE,"E12.59.5"),sQuery(id+"F0.wireOp",EDGE,"E12.59.6"),sQuery(id+"F0.wireOp",EDGE,"E12.59.7"),sQuery(id+"F0.wireOp",EDGE,"E12.59.8"),sQuery(id+"F0.wireOp",EDGE,"E12.59.9"),sQuery(id+"F0.wireOp",EDGE,"E13.trimOffspring"),sQuery(id+"F0.wireOp",EDGE,"E14.trimOffspring")])],"isStart":true}),makeQuery(id+"F3.opExtrude","SWEPT_FACE",FACE,{"disambiguationData":[OSD([sQuery(id+"F2.wireOp",EDGE,"E17.3.0")])]})]});
            chamfer(context, id + "F10", {"entities" : qUnion([Q0, Q1, Q2, Q3, Q4, Q5, Q6, Q7, Q8, Q9, Q10, Q11, Q12, Q13, Q14, Q15]), "width" : 0.79 * mm, "tangentPropagation" : true});
        }
    });
